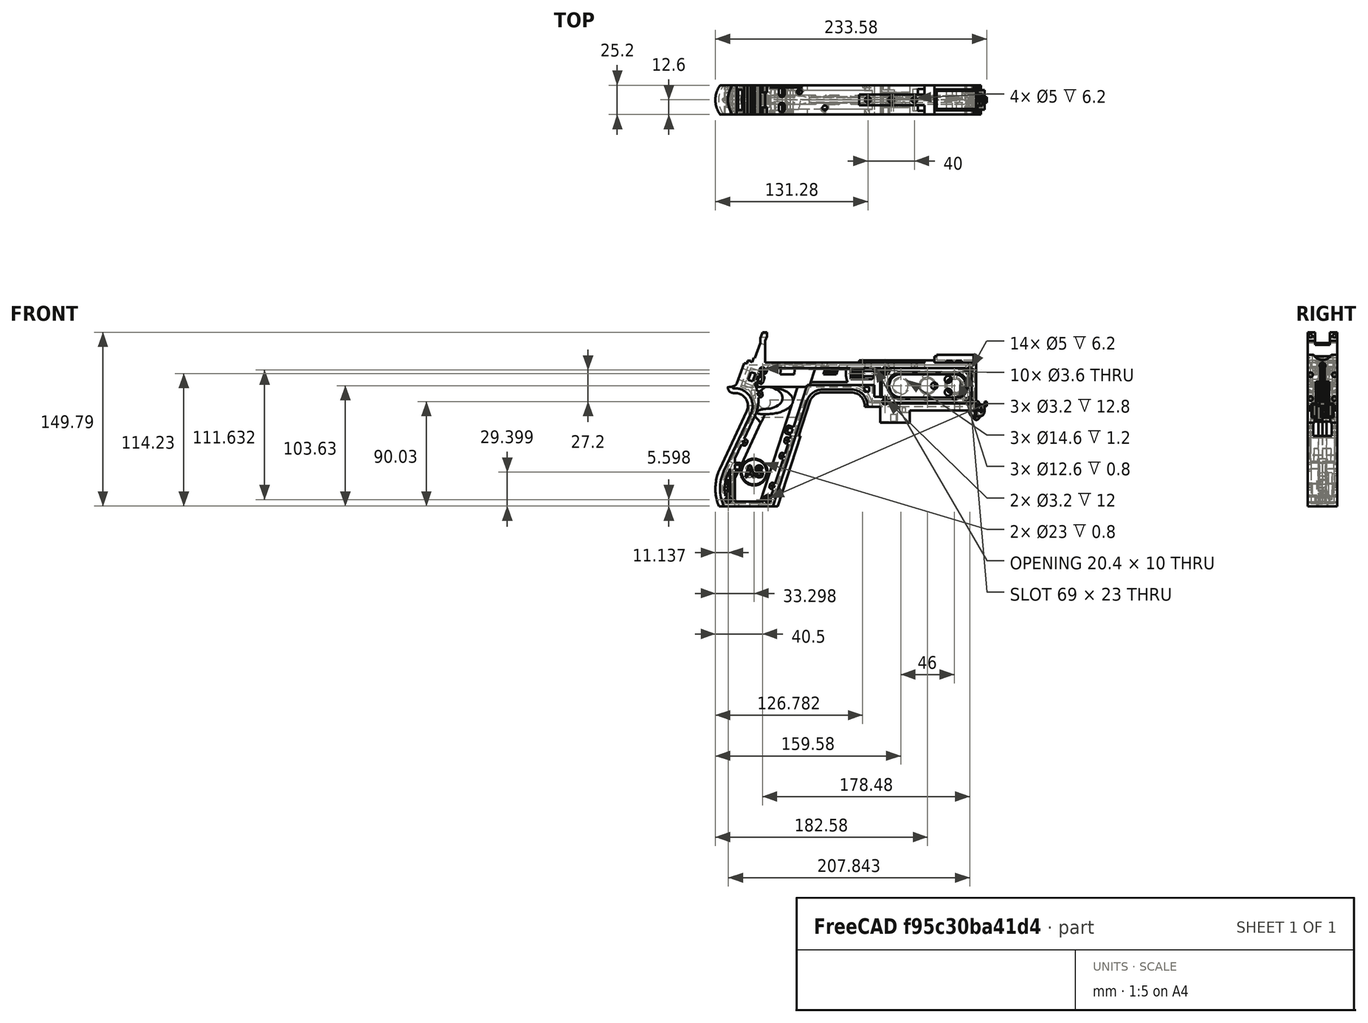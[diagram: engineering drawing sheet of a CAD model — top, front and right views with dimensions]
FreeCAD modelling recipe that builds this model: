
FCSTD DOCUMENT  (FreeCAD 1.0R39319 (Git))
Label: PICON-OF_ver_54
License: All rights reserved
LicenseURL: https://en.wikipedia.org/wiki/All_rights_reserved
objects: Sketcher::SketchObject×124, Part::Extrusion×63, Part::Cut×48, PartDesign::Pad×29, PartDesign::Pocket×21, PartDesign::Chamfer×15, PartDesign::Body×10, PartDesign::Fillet×6, Part::MultiFuse×5, Part::Part2DObjectPython×4, PartDesign::SubtractivePipe×4, PartDesign::SubtractiveLoft×4, PartDesign::Plane×3, PartDesign::SubShapeBinder×2, Part::Sweep×1, PartDesign::ShapeBinder×1, Mesh::Feature×1, PartDesign::Point×1, PartDesign::Groove×1
note: 626 computed .brp shape members not serialized (recipe doc carries the construction recipe); baked Part::Feature solids carry a one-line shape summary decoded from their .brp

FEATURE [Sketcher::SketchObject] Sketch  label="corpo principale"
  ArcFitTolerance = 1e-06
  AttacherType = Attacher::AttachEngine3D
  AttachmentSupport = -> [XZ_Plane]
  FullyConstrained = true
  MakeInternals = false
  MapMode = 5
  Placement = pos=(0,0,0) rot=(1,0,0;1.5708rad)
  sketch-geometry (65):
    g0: LineSegment StartX=0 StartY=0 StartZ=0 EndX=-57.2 EndY=0 EndZ=0
    g1: LineSegment StartX=-57.2 StartY=0 StartZ=0 EndX=-57.2 EndY=-10.4 EndZ=0
    g2: LineSegment StartX=-57.2 StartY=-10.4 StartZ=0 EndX=-82.8 EndY=-10.4 EndZ=0
    g3: LineSegment StartX=-82.8 StartY=-10.4 StartZ=0 EndX=-82.8 EndY=3.2 EndZ=0
    g4: LineSegment StartX=-82.8 StartY=3.2 StartZ=0 EndX=-93.6 EndY=3.2 EndZ=0
    g5: LineSegment StartX=-93.6 StartY=3.2 StartZ=0 EndX=-93.6 EndY=4 EndZ=0
    g6: LineSegment StartX=-107.6 StartY=18 StartZ=0 EndX=-132.428 EndY=18 EndZ=0
    g7: LineSegment StartX=-145.743 StartY=8.32624 StartZ=0 EndX=-175.232 EndY=-82.4316 EndZ=0
    g8: LineSegment StartX=-175.232 StartY=-82.4316 StartZ=0 EndX=-217.232 EndY=-82.4316 EndZ=0
    g9: LineSegment StartX=-217.232 StartY=-52.1862 StartZ=0 EndX=-193.988 EndY=-2.33927 EndZ=0
    g10: LineSegment StartX=-206.196 StartY=23.0857 StartZ=0 EndX=-199.861 EndY=40.4914 EndZ=0
    g11: LineSegment StartX=-199.861 StartY=40.4914 StartZ=0 EndX=-197.061 EndY=40.4914 EndZ=0
    g12: LineSegment StartX=-197.061 StartY=40.4914 StartZ=0 EndX=-197.061 EndY=42.8914 EndZ=0
    g13: LineSegment StartX=-197.061 StartY=42.8914 StartZ=0 EndX=-194.261 EndY=42.8914 EndZ=0
    g14: LineSegment StartX=-194.261 StartY=42.8914 StartZ=0 EndX=-194.535 EndY=42.1397 EndZ=0
    g15: LineSegment StartX=-194.535 StartY=42.1397 StartZ=0 EndX=-193.031 EndY=41.5924 EndZ=0
    g16: LineSegment StartX=-193.031 StartY=41.5924 StartZ=0 EndX=-191.663 EndY=45.3512 EndZ=0
    g17: LineSegment StartX=-191.663 StartY=45.3512 StartZ=0 EndX=-190.536 EndY=44.9408 EndZ=0
    g18: LineSegment StartX=-190.536 StartY=44.9408 StartZ=0 EndX=-185.747 EndY=58.0965 EndZ=0
    g19: LineSegment StartX=-185.747 StartY=58.0965 StartZ=0 EndX=-185.747 EndY=62.0965 EndZ=0
    g20: LineSegment StartX=-185.747 StartY=62.0965 StartZ=0 EndX=-183.832 EndY=67.3588 EndZ=0
    g21: LineSegment StartX=-183.832 StartY=67.3588 StartZ=0 EndX=-180.232 EndY=67.3588 EndZ=0
    g22: LineSegment StartX=-180.232 StartY=67.3588 StartZ=0 EndX=-180.232 EndY=63.7588 EndZ=0
    g23: LineSegment StartX=-180.232 StartY=63.7588 StartZ=0 EndX=-181.6 EndY=60 EndZ=0
    g24: LineSegment StartX=-181.6 StartY=60 StartZ=0 EndX=-181.6 EndY=41.2 EndZ=0
    g25: LineSegment StartX=-181.6 StartY=41.2 StartZ=0 EndX=-100.8 EndY=41.2 EndZ=0
    g26: LineSegment StartX=-36 StartY=43.2 StartZ=0 EndX=-36 EndY=41.2 EndZ=0
    g27: LineSegment StartX=0 StartY=48 StartZ=0 EndX=0 EndY=0 EndZ=0
    g28: LineSegment StartX=-209.901 StartY=19.85 StartZ=0 EndX=-209.901 EndY=20.1 EndZ=0
    g29: LineSegment StartX=-208.001 StartY=22 StartZ=0 EndX=-207.747 EndY=22 EndZ=0
    g30: LineSegment StartX=-207.583 StartY=19 StartZ=0 EndX=-209.051 EndY=19 EndZ=0
    g31: ArcOfCircle CenterX=-208.001 CenterY=20.1 CenterZ=0 NormalX=0 NormalY=0 NormalZ=1 AngleXU=0 Radius=1.9 StartAngle=1.5708 EndAngle=3.14159
    g32: GeomPoint [constr] X=-209.901 Y=22 Z=0
    g33: ArcOfCircle CenterX=-209.051 CenterY=19.85 CenterZ=0 NormalX=0 NormalY=0 NormalZ=1 AngleXU=0 Radius=0.85 StartAngle=3.14159 EndAngle=4.71239
    g34: GeomPoint [constr] X=-209.901 Y=19 Z=0
    g35: ArcOfCircle CenterX=-207.747 CenterY=23.65 CenterZ=0 NormalX=0 NormalY=0 NormalZ=1 AngleXU=0 Radius=1.65 StartAngle=4.71239 EndAngle=5.93412
    g36: GeomPoint [constr] X=-206.591 Y=22 Z=0
    g37: LineSegment StartX=-4 StartY=6 StartZ=0 EndX=-4 EndY=36.4 EndZ=0
    g38: LineSegment StartX=-4 StartY=36.4 StartZ=0 EndX=-185.2 EndY=36.4 EndZ=0
    g39: LineSegment StartX=-185.2 StartY=36.4 StartZ=0 EndX=-190.441 EndY=22 EndZ=0
    g40: LineSegment StartX=-214.575 StartY=-78.4316 StartZ=0 EndX=-178.142 EndY=-78.4316 EndZ=0
    g41: LineSegment StartX=-178.142 StartY=-78.4316 StartZ=0 EndX=-145.51 EndY=22 EndZ=0
    g42: LineSegment StartX=-145.51 StartY=22 StartZ=0 EndX=-87.91 EndY=22 EndZ=0
    g43: LineSegment StartX=-87.91 StartY=22 StartZ=0 EndX=-87.91 EndY=11.6 EndZ=0
    g44: LineSegment StartX=-87.91 StartY=11.6 StartZ=0 EndX=-80.11 EndY=11.6 EndZ=0
    g45: LineSegment StartX=-80.11 StartY=11.6 StartZ=0 EndX=-80.11 EndY=6 EndZ=0
    g46: LineSegment StartX=-80.11 StartY=6 StartZ=0 EndX=-4 EndY=6 EndZ=0
    g47: LineSegment StartX=-190.363 StartY=-4.02975 StartZ=0 EndX=-213.607 EndY=-53.8767 EndZ=0
    g48: ArcOfCircle CenterX=-132.428 CenterY=4 CenterZ=0 NormalX=0 NormalY=0 NormalZ=1 AngleXU=0 Radius=14 StartAngle=1.5708 EndAngle=2.82743
    g49: GeomPoint [constr] X=-142.6 Y=18 Z=0
    g50: ArcOfCircle CenterX=-107.6 CenterY=4 CenterZ=0 NormalX=0 NormalY=0 NormalZ=1 AngleXU=0 Radius=14 StartAngle=0 EndAngle=1.5708
    g51: GeomPoint [constr] X=-93.6 Y=18 Z=0
    g52: ArcOfCircle CenterX=-184.801 CenterY=-67.3089 CenterZ=0 NormalX=0 NormalY=0 NormalZ=1 AngleXU=0 Radius=35.7833 StartAngle=2.70526 EndAngle=3.57792
    g53: ArcOfCircle CenterX=-207.583 CenterY=4 CenterZ=0 NormalX=0 NormalY=0 NormalZ=1 AngleXU=0 Radius=15 StartAngle=5.84685 EndAngle=7.85398
    g54: LineSegment [constr] StartX=-213.607 StartY=-53.8767 StartZ=0 EndX=-217.232 EndY=-52.1862 EndZ=0
    g55: ArcOfCircle CenterX=-184.801 CenterY=-67.3089 CenterZ=0 NormalX=0 NormalY=0 NormalZ=1 AngleXU=0 Radius=31.7833 StartAngle=2.70526 EndAngle=3.49911
    g56: ArcOfCircle CenterX=-218.095 CenterY=8.90192 CenterZ=0 NormalX=0 NormalY=0 NormalZ=1 AngleXU=0 Radius=30.5989 StartAngle=5.84685 EndAngle=6.72553
    g57: LineSegment StartX=-44.6 StartY=43.2 StartZ=0 EndX=-36 EndY=43.2 EndZ=0
    g58: LineSegment StartX=-100.8 StartY=41.2 StartZ=0 EndX=-44.6 EndY=41.2 EndZ=0
    g59: LineSegment StartX=-44.6 StartY=41.2 StartZ=0 EndX=-44.6 EndY=43.2 EndZ=0
    g60: LineSegment StartX=-2.4 StartY=48 StartZ=0 EndX=0 EndY=48 EndZ=0
    g61: LineSegment StartX=-36 StartY=41.2 StartZ=0 EndX=-2.4 EndY=41.2 EndZ=0
    g62: LineSegment StartX=-2.4 StartY=41.2 StartZ=0 EndX=-2.4 EndY=48 EndZ=0
    g63: LineSegment [constr] StartX=-181.6 StartY=36.4 StartZ=0 EndX=-152.209 EndY=36.4 EndZ=0
    g64: LineSegment [constr] StartX=-181.6 StartY=36.4 StartZ=0 EndX=-130.41 EndY=36.4 EndZ=0
  constraints (183):
    c: Coincident(g-1,g0)
    c: PointOnObject(g0,g-1)
    c: Coincident(g0,g1)
    c: Vertical(g1)
    c: Coincident(g1,g2)
    c: Horizontal(g2)
    c: Coincident(g2,g3)
    c: Vertical(g3)
    c: Coincident(g3,g4)
    c: Coincident(g4,g5)
    c: Vertical(g5)
    c: Horizontal(g6)
    c: Coincident(g7,g8)
    c: Horizontal(g8)
    c: Coincident(g10,g11)
    c: Horizontal(g11)
    c: Coincident(g11,g12)
    c: Vertical(g12)
    c: Coincident(g12,g13)
    c: Horizontal(g13)
    c: Coincident(g13,g14)
    c: Coincident(g14,g15)
    c: Coincident(g15,g16)
    c: Coincident(g16,g17)
    c: Coincident(g17,g18)
    c: Coincident(g18,g19)
    c: Vertical(g19)
    c: Coincident(g19,g20)
    c: Coincident(g20,g21)
    c: Horizontal(g21)
    c: Coincident(g21,g22)
    c: Vertical(g22)
    c: Coincident(g22,g23)
    c: Coincident(g23,g24)
    c: Vertical(g24)
    c: Coincident(g24,g25)
    c: Horizontal(g25)
    c: Coincident(g57,g26)
    c: Vertical(g26)
    c: Coincident(g26,g61)
    c: PointOnObject(g60,g-2)
    c: Coincident(g60,g27)
    c: Coincident(g27,g0)
    c: DistanceY(g27,g27) = 48
    c: DistanceY(g1,g1) = 10.4
    c: DistanceX(g0,g0) = 57.2
    c: DistanceX(g2,g2) = 25.6
    c: Horizontal(g4)
    c: DistanceY(g3,g3) = 13.6
    c: DistanceX(g4,g4) = 10.8
    c: DistanceY(g5,g51) = 14.8
    c: DistanceX(g49,g51) = 49
    c: Distance(g7,g49) = 105.6
    c: DistanceX(g61,g60) = 36
    c: DistanceX(g25,g25) = 80.8
    c: DistanceY(g24,g24) = 18.8
    c: DistanceY(g22,g22) = 3.6
    c: Distance(g23) = 4
    c: Angle(g-1,g23) = 1.22173
    c: DistanceX(g21,g21) = 3.6
    c: Distance(g20) = 5.6
    c: Angle(g-1,g20) = 1.22173
    c: DistanceY(g19,g19) = 4
    c: Distance(g18) = 14
    c: Angle(g-1,g18) = 1.22173
    c: Distance(g17) = 1.2
    c: Distance(g16) = 4
    c: Angle(g16) = 1.22173
    c: Perpendicular(g18,g17)
    c: Distance(g15) = 1.6
    c: Perpendicular(g16,g15)
    c: Distance(g14) = 0.8
    c: DistanceX(g13,g13) = 2.8
    c: Perpendicular(g15,g14)
    c: DistanceY(g12,g12) = 2.4
    c: DistanceX(g11,g11) = 2.8
    c: Distance(g9) = 55
    c: Angle(g9,g-1) = 2.00713
    c: Horizontal(g29)
    c: Vertical(g28)
    c: Horizontal(g30)
    c: PointOnObject(g32,g29)
    c: PointOnObject(g32,g28)
    c: Tangent(g29,g31) = 1.5708
    c: Tangent(g28,g31) = 1.5708
    c: PointOnObject(g34,g28)
    c: PointOnObject(g34,g30)
    c: Tangent(g28,g33) = 1.5708
    c: Tangent(g30,g33) = 1.5708
    c: PointOnObject(g36,g29)
    c: PointOnObject(g36,g10)
    c: Tangent(g29,g35) = -1.5708
    c: Tangent(g10,g35) = -1.5708
    c: Angle(g-1,g10) = 1.22173
    c: Radius(g35) = 1.65
    c: Vertical(g37)
    c: Coincident(g37,g38)
    c: Horizontal(g38)
    c: Coincident(g38,g39)
    c: Horizontal(g40)
    c: Coincident(g40,g41)
    c: Coincident(g41,g42)
    c: Horizontal(g42)
    c: Coincident(g42,g43)
    c: Vertical(g43)
    c: Coincident(g43,g44)
    c: Horizontal(g44)
    c: Coincident(g44,g45)
    c: Vertical(g45)
    c: Coincident(g45,g46)
    c: Coincident(g46,g37)
    c: Horizontal(g46)
    c: DistanceY(g0,g37) = 6
    c: DistanceX(g37,g0) = 4
    c: DistanceY(g37,g25) = 4.8
    c: DistanceX(g38,g38) = 181.2
    c: DistanceX(g42,g42) = 57.6
    c: DistanceY(g49,g41) = 4
    c: DistanceX(g41,g49) = 2.91
    c: DistanceY(g43,g43) = 10.4
    c: DistanceX(g44,g44) = 7.8
    c: DistanceY(g7,g40) = 4
    c: Distance(g47) = 55
    c: Angle(g-1,g39) = 1.22173
    c: PointOnObject(g49,g7)
    c: PointOnObject(g49,g6)
    c: Tangent(g7,g48) = -1.5708
    c: Tangent(g6,g48) = -1.5708
    c: PointOnObject(g51,g5)
    c: PointOnObject(g51,g6)
    c: Tangent(g5,g50) = -1.5708
    c: Tangent(g6,g50) = -1.5708
    c: Radius(g50) = 14
    c: Radius(g48) = 14
    c: DistanceX(g8,g8) = 42
    c: Angle(g7,g-1) = 1.88496
    c: Parallel(g41,g7)
    c: Parallel(g47,g9)
    c: Coincident(g52,g8)
    c: Tangent(g52,g9) = 1.5708
    c: DistanceX(g9,g8) = 0
    c: Tangent(g53,g9) = -1.5708
    c: Tangent(g53,g30) = -1.5708
    c: Diameter(g53) = 30
    c: DistanceY(g53,g0) = -4
    c: Coincident(g54,g47)
    c: Distance(g54) = 4
    c: Coincident(g54,g9)
    c: Coincident(g55,g40)
    c: Tangent(g55,g47) = -1.5708
    c: Coincident(g52,g55)
    c: Coincident(g56,g39)
    c: Tangent(g56,g47) = 1.5708
    c: Horizontal(g57)
    c: DistanceX(g57,g57) = 8.6
    c: Coincident(g58,g25)
    c: Horizontal(g58)
    c: Coincident(g59,g58)
    c: Vertical(g59)
    c: DistanceY(g58,g57) = 2
    c: DistanceX(g58,g58) = 56.2
    c: Coincident(g59,g57)
    c: DistanceY(g41,g36) = 0
    c: DistanceY(g36,g39) = 0
    c: DistanceY(g28,g28) = 0.25
    c: DistanceX(g30,g36) = 2.46
    c: DistanceX(g28,g29) = 1.9
    c: Coincident(g62,g60)
    c: Horizontal(g60)
    c: DistanceX(g62,g27) = 2.4
    c: Coincident(g61,g62)
    c: DistanceY(g26,g26) = 2
    c: Vertical(g62)
    c: DistanceY(g61,g60) = 6.8
    c: Horizontal(g61)
    c: Distance(g63) = 29.391
    c: PointOnObject(g63,g38)
    c: PointOnObject(g63,g38)
    c: Distance(g64) = 51.19
    c: PointOnObject(g64,g38)
    c: PointOnObject(g64,g38)
    c: DistanceX(g24,g63) = 0
    c: DistanceX(g24,g64) = 0
FEATURE [Part::Extrusion] Extrude  label="Extrude corpo principale"
  Base = -> Sketch
  Dir = (0,-1,2e-16)
  DirMode = 2
  FaceMakerClass = Part::FaceMakerBullseye
  FaceMakerMode = 3
  LengthFwd = 25.2
  LengthRev = 12.6
  Solid = true
  Symmetric = true
FEATURE [Sketcher::SketchObject] Sketch002  label="scavo grilletto"
  ArcFitTolerance = 1e-06
  AttachmentSupport = -> [XZ_Plane]
  ExternalGeometry = -> [Sketch]
  FullyConstrained = true
  MakeInternals = false
  MapMode = 5
  Placement = pos=(0,0,0) rot=(1,0,0;1.5708rad)
  sketch-geometry (4):
    g0: LineSegment StartX=-89.51 StartY=22 StartZ=0 EndX=-152.71 EndY=22 EndZ=0
    g1: LineSegment StartX=-152.71 StartY=22 StartZ=0 EndX=-167.006 EndY=-22 EndZ=0
    g2: LineSegment StartX=-167.006 StartY=-22 StartZ=0 EndX=-89.51 EndY=-22 EndZ=0
    g3: LineSegment StartX=-89.51 StartY=-22 StartZ=0 EndX=-89.51 EndY=22 EndZ=0
  constraints (12):
    c: Horizontal(g0)
    c: Coincident(g0,g1)
    c: Coincident(g1,g2)
    c: Horizontal(g2)
    c: Coincident(g2,g3)
    c: Coincident(g3,g0)
    c: Vertical(g3)
    c: Angle(g1,g0) = 1.88496
    c: DistanceY(g3,g3) = 44
    c: DistanceX(g0,g0) = 63.2
    c: DistanceX(g0,g-3) = 1.6
    c: DistanceY(g-3,g0) = 0
FEATURE [Sketcher::SketchObject] Sketch004  label="traiettoria arrotondamento impugnatura anteriore"
  ArcFitTolerance = 1e-06
  AttachmentSupport = -> [XZ_Plane]
  ExternalGeometry = -> [Sketch]
  FullyConstrained = true
  MakeInternals = false
  MapMode = 5
  Placement = pos=(0,0,0) rot=(1,0,0;1.5708rad)
  sketch-geometry (13):
    g0: LineSegment StartX=-175.232 StartY=-82.4316 StartZ=0 EndX=-145.743 EndY=8.32624 EndZ=0
    g1: LineSegment StartX=-93.6 StartY=3.2 StartZ=0 EndX=-93.6 EndY=4 EndZ=0
    g2: LineSegment StartX=-132.428 StartY=18 StartZ=0 EndX=-107.6 EndY=18 EndZ=0
    g3: ArcOfCircle CenterX=-132.428 CenterY=4 CenterZ=0 NormalX=0 NormalY=0 NormalZ=1 AngleXU=0 Radius=14 StartAngle=1.5708 EndAngle=2.82743
    g4: ArcOfCircle CenterX=-107.6 CenterY=4 CenterZ=0 NormalX=0 NormalY=0 NormalZ=1 AngleXU=0 Radius=14 StartAngle=0 EndAngle=1.5708
    g5: LineSegment StartX=-175.232 StartY=-82.4316 StartZ=0 EndX=-217.232 EndY=-82.4316 EndZ=0
    g6: LineSegment StartX=-217.232 StartY=-52.1862 StartZ=0 EndX=-193.988 EndY=-2.33927 EndZ=0
    g7: LineSegment StartX=-209.051 StartY=19 StartZ=0 EndX=-207.583 EndY=19 EndZ=0
    g8: LineSegment StartX=-209.901 StartY=20.1 StartZ=0 EndX=-209.901 EndY=19.85 EndZ=0
    g9: ArcOfCircle CenterX=-184.801 CenterY=-67.3089 CenterZ=0 NormalX=0 NormalY=0 NormalZ=1 AngleXU=0 Radius=35.7833 StartAngle=2.70526 EndAngle=3.57792
    g10: ArcOfCircle CenterX=-207.583 CenterY=4 CenterZ=0 NormalX=0 NormalY=0 NormalZ=1 AngleXU=0 Radius=15 StartAngle=5.84685 EndAngle=7.85398
    g11: ArcOfCircle CenterX=-209.051 CenterY=19.85 CenterZ=0 NormalX=0 NormalY=0 NormalZ=1 AngleXU=0 Radius=0.85 StartAngle=3.14159 EndAngle=4.71239
    g12: ArcOfCircle CenterX=-208.001 CenterY=20.1 CenterZ=0 NormalX=0 NormalY=0 NormalZ=1 AngleXU=0 Radius=1.9 StartAngle=1.5708 EndAngle=3.14159
  constraints (26):
    c: Coincident(g0,g-3)
    c: Coincident(g0,g-6)
    c: Coincident(g1,g-8)
    c: Coincident(g1,g-7)
    c: Coincident(g2,g-5)
    c: Coincident(g2,g-4)
    c: Coincident(g3,g2)
    c: Tangent(g3,g0) = 1.5708
    c: Coincident(g4,g1)
    c: Tangent(g4,g2) = 1.5708
    c: Coincident(g5,g0)
    c: Coincident(g5,g-9)
    c: Coincident(g6,g-12)
    c: Coincident(g6,g-11)
    c: Coincident(g7,g-15)
    c: Coincident(g7,g-14)
    c: Coincident(g8,g-16)
    c: Coincident(g8,g-17)
    c: Tangent(g9,g6) = 1.5708
    c: Coincident(g9,g5)
    c: Coincident(g10,g7)
    c: Tangent(g10,g6) = -1.5708
    c: Tangent(g11,g7) = -1.5708
    c: Coincident(g11,g8)
    c: Tangent(g12,g8) = -1.5708
    c: Coincident(g12,g-17)
FEATURE [PartDesign::Plane] DatumPlane  label="Piano per disegno arrotondamento impugnatura"
  AttachmentSupport = -> [Sketch]
  Length = 73.6581
  MapMode = 7
  Placement = pos=(-145.743,1.8e-15,8.32624) rot=(0.154555,0.154555,0.97582;1.59527rad)
  ResizeMode = 0
  Width = 303.511
FEATURE [Sketcher::SketchObject] Sketch005  label="forma arrotondamento impugnatura anteriore"
  ArcFitTolerance = 1e-06
  AttachmentSupport = -> [DatumPlane]
  FullyConstrained = true
  MakeInternals = false
  MapMode = 5
  Placement = pos=(-145.743,1.8e-15,8.32624) rot=(0.154555,0.154555,0.97582;1.59527rad)
  sketch-geometry (5):
    g0: GeomPoint [constr] X=0 Y=-4 Z=0
    g1: GeomPoint [constr] X=-12.6 Y=7.1e-15 Z=0
    g2: GeomPoint [constr] X=12.6 Y=4.97e-14 Z=0
    g3: LineSegment StartX=-12.6 StartY=7.1e-15 StartZ=0 EndX=12.6 EndY=4.97e-14 EndZ=0
    g4: ArcOfCircle CenterX=-3.88e-14 CenterY=17.845 CenterZ=0 NormalX=0 NormalY=0 NormalZ=1 AngleXU=0 Radius=21.845 StartAngle=4.09759 EndAngle=5.32718
  constraints (11):
    c: DistanceY(g0,g-1) = 4
    c: DistanceX(g-1,g0) = 0
    c: DistanceX(g1,g-1) = 12.6
    c: DistanceX(g-1,g2) = 12.6
    c: DistanceY(g-1,g2) = 0
    c: DistanceY(g-1,g1) = 0
    c: Coincident(g3,g1)
    c: Coincident(g3,g2)
    c: Coincident(g4,g1)
    c: Coincident(g4,g2)
    c: PointOnObject(g0,g4)
FEATURE [Part::Sweep] Sweep  label="Sweep impugnatura"
  Frenet = true
  Sections = -> [Sketch005]
  Solid = true
  Spine = -> Sketch [Edge32,Edge33,Edge34,Edge35,Edge36,Edge37,Edge38,Edge39,Edge40,Edge41,Edge42,Edge43,Edge44]
  Transition = 1
FEATURE [Sketcher::SketchObject] Sketch008  label="buchi e pulizie varie"
  ArcFitTolerance = 1e-06
  AttachmentSupport = -> [XZ_Plane]
  ExternalGeometry = -> [Sketch]
  FullyConstrained = true
  MakeInternals = false
  MapMode = 5
  Placement = pos=(0,0,0) rot=(1,0,0;1.5708rad)
  sketch-geometry (26):
    g0: LineSegment StartX=-96.278 StartY=20.155 StartZ=0 EndX=-92.278 EndY=20.155 EndZ=0
    g1: LineSegment StartX=-92.278 StartY=20.155 StartZ=0 EndX=-92.278 EndY=16.155 EndZ=0
    g2: LineSegment StartX=-92.278 StartY=16.155 StartZ=0 EndX=-96.278 EndY=16.155 EndZ=0
    g3: LineSegment StartX=-96.278 StartY=16.155 StartZ=0 EndX=-96.278 EndY=20.155 EndZ=0
    g4: LineSegment StartX=-222.232 StartY=-82.4316 StartZ=0 EndX=-170.232 EndY=-82.4316 EndZ=0
    g5: LineSegment StartX=-170.232 StartY=-82.4316 StartZ=0 EndX=-170.232 EndY=-86.4316 EndZ=0
    g6: LineSegment StartX=-170.232 StartY=-86.4316 StartZ=0 EndX=-222.232 EndY=-86.4316 EndZ=0
    g7: LineSegment StartX=-222.232 StartY=-86.4316 StartZ=0 EndX=-222.232 EndY=-82.4316 EndZ=0
    g8: LineSegment StartX=-213.901 StartY=20.1 StartZ=0 EndX=-213.901 EndY=26 EndZ=0
    g9: LineSegment StartX=-213.901 StartY=26 StartZ=0 EndX=-206.196 EndY=26 EndZ=0
    g10: LineSegment StartX=-17.4 StartY=42.8 StartZ=0 EndX=-12.4 EndY=42.8 EndZ=0
    g11: LineSegment StartX=-12.4 StartY=42.8 StartZ=0 EndX=-12.4 EndY=41.2 EndZ=0
    g12: LineSegment StartX=-12.4 StartY=41.2 StartZ=0 EndX=-17.4 EndY=41.2 EndZ=0
    g13: LineSegment StartX=-17.4 StartY=41.2 StartZ=0 EndX=-17.4 EndY=42.8 EndZ=0
    g14: LineSegment StartX=-25.9 StartY=42.8 StartZ=0 EndX=-20.9 EndY=42.8 EndZ=0
    g15: LineSegment StartX=-20.9 StartY=42.8 StartZ=0 EndX=-20.9 EndY=41.2 EndZ=0
    g16: LineSegment StartX=-20.9 StartY=41.2 StartZ=0 EndX=-25.9 EndY=41.2 EndZ=0
    g17: LineSegment StartX=-25.9 StartY=41.2 StartZ=0 EndX=-25.9 EndY=42.8 EndZ=0
    g18: GeomPoint [constr] X=-206.196 Y=23.0857 Z=0
    g19: GeomPoint [constr] X=-213.901 Y=20.1 Z=0
    g20: BSplineCurve PolesCount=4 KnotsCount=2 Degree=3 IsPeriodic=0
    g21-g24: Circle [constr] x4 (B-spline internal-alignment scaffolding for g20; pole/knot coordinates omitted)
    g25: LineSegment StartX=-206.196 StartY=26 StartZ=0 EndX=-206.196 EndY=23.0857 EndZ=0
  constraints (73):
    c: Horizontal(g0)
    c: Coincident(g1,g0)
    c: Vertical(g1)
    c: Coincident(g2,g1)
    c: Horizontal(g2)
    c: Coincident(g3,g2)
    c: Coincident(g3,g0)
    c: Vertical(g3)
    c: DistanceX(g0,g-4) = 4.368
    c: DistanceY(g0,g-4) = 1.845
    c: DistanceY(g1,g1) = 4
    c: DistanceX(g2,g2) = 4
    c: Horizontal(g4)
    c: Coincident(g5,g4)
    c: Vertical(g5)
    c: Coincident(g6,g5)
    c: Horizontal(g6)
    c: Coincident(g7,g6)
    c: Coincident(g7,g4)
    c: Vertical(g7)
    c: DistanceY(g7,g7) = 4
    c: DistanceX(g4,g-5) = 5
    c: DistanceX(g-5,g4) = 5
    c: DistanceY(g4,g-5) = 0
    c: Coincident(g9,g8)
    c: Parallel(g9,g-6)
    c: DistanceX(g8,g-8) = 4
    c: Horizontal(g10)
    c: Coincident(g11,g10)
    c: Vertical(g11)
    c: Coincident(g12,g11)
    c: Horizontal(g12)
    c: Coincident(g13,g12)
    c: Coincident(g13,g10)
    c: Vertical(g13)
    c: Horizontal(g14)
    c: Coincident(g15,g14)
    c: Vertical(g15)
    c: Coincident(g16,g15)
    c: Horizontal(g16)
    c: Coincident(g17,g16)
    c: Coincident(g17,g14)
    c: Vertical(g17)
    c: DistanceY(g11,g10) = 1.6
    c: DistanceX(g10,g10) = 5
    c: DistanceY(g15,g14) = 1.6
    c: DistanceX(g14,g14) = 5
    c: DistanceX(g15,g12) = 3.5
    c: DistanceX(g11,g-9) = 10
    c: DistanceY(g-9,g11) = 0
    c: DistanceY(g-9,g15) = 0
    c: Perpendicular(g8,g9)
    c: DistanceY(g-7,g9) = 4
    c: DistanceY(g8,g-8) = 0
    c: InternalAlignment(g18,g20)
    c: InternalAlignment(g19,g20)
    c: InternalAlignment(g21,g20)
    c: Weight(g21) = 1
    c: InternalAlignment(g22,g20)
    c: Equal(g22,g21)
    c: InternalAlignment(g23,g20)
    c: Equal(g23,g21)
    c: InternalAlignment(g24,g20)
    c: Equal(g24,g21)
    c: Coincident(g18,g-12)
    c: Coincident(g19,g8)
    c: Coincident(g25,g9)
    c: Coincident(g25,g20)
    c: Vertical(g25)
    c: DistanceY(g20,g23) = 0
    c: DistanceY(g22,g18) = 2.26
    c: DistanceX(g22,g18) = 0.93
    c: DistanceX(g20,g23) = 2.9
FEATURE [Part::Extrusion] Extrude004  label="Extrude Buchi e pulizie varie"
  Base = -> Sketch008
  Dir = (0,-1,2e-16)
  DirMode = 2
  FaceMakerClass = Part::FaceMakerBullseye
  FaceMakerMode = 3
  LengthFwd = 25.2
  LengthRev = 0
  Solid = true
  Symmetric = true
FEATURE [Sketcher::SketchObject] Sketch009  label="rinforzi"
  ArcFitTolerance = 1e-06
  AttachmentSupport = -> [XZ_Plane]
  ExternalGeometry = -> [Sketch]
  FullyConstrained = true
  MakeInternals = false
  MapMode = 5
  Placement = pos=(0,0,0) rot=(1,0,0;1.5708rad)
  sketch-geometry (9):
    g0: LineSegment StartX=-87.91 StartY=22 StartZ=0 EndX=-87.91 EndY=36.4 EndZ=0
    g1: LineSegment StartX=-87.91 StartY=36.4 StartZ=0 EndX=-97.91 EndY=36.4 EndZ=0
    g2: LineSegment StartX=-97.91 StartY=36.4 StartZ=0 EndX=-97.91 EndY=22 EndZ=0
    g3: LineSegment StartX=-97.91 StartY=22 StartZ=0 EndX=-87.91 EndY=22 EndZ=0
    g4: LineSegment StartX=-149.713 StartY=9.06563 StartZ=0 EndX=-154.586 EndY=-5.93437 EndZ=0
    g5: LineSegment StartX=-154.586 StartY=-5.93437 StartZ=0 EndX=-191.863 EndY=-5.93437 EndZ=0
    g6: LineSegment StartX=-191.863 StartY=-5.93437 StartZ=0 EndX=-191.863 EndY=9.06563 EndZ=0
    g7: LineSegment StartX=-191.863 StartY=9.06563 StartZ=0 EndX=-149.713 EndY=9.06563 EndZ=0
    g8: LineSegment [constr] StartX=-145.51 StartY=22 StartZ=0 EndX=-149.713 EndY=9.06563 EndZ=0
  constraints (25):
    c: Vertical(g0)
    c: Coincident(g1,g0)
    c: Horizontal(g1)
    c: Coincident(g2,g1)
    c: Vertical(g2)
    c: Coincident(g3,g2)
    c: Coincident(g3,g0)
    c: Horizontal(g3)
    c: Coincident(g0,g-4)
    c: DistanceX(g3,g3) = 10
    c: DistanceY(g0,g-3) = 0
    c: Coincident(g5,g4)
    c: Horizontal(g5)
    c: Coincident(g6,g5)
    c: Vertical(g6)
    c: Coincident(g7,g6)
    c: Coincident(g7,g4)
    c: Horizontal(g7)
    c: Distance(g8) = 13.6
    c: Parallel(g-6,g8)
    c: Coincident(g-6,g8)
    c: Parallel(g4,g-6)
    c: DistanceY(g4,g4) = 15
    c: Coincident(g4,g8)
    c: DistanceX(g-5,g5) = -1.5
FEATURE [Part::Extrusion] Extrude001  label="Extrude scavo grilletto"
  Base = -> Sketch002
  Dir = (0,-1,2e-16)
  DirMode = 2
  FaceMakerClass = Part::FaceMakerBullseye
  FaceMakerMode = 3
  LengthFwd = 16
  LengthRev = 0
  Solid = true
  Symmetric = true
FEATURE [Part::Extrusion] Extrude005  label="Extrude Rinforzi"
  Base = -> Sketch009
  Dir = (0,-1,2e-16)
  DirMode = 2
  FaceMakerClass = Part::FaceMakerBullseye
  FaceMakerMode = 3
  LengthFwd = 2
  LengthRev = 0
  Placement = pos=(0,12.6,0) rot=(0,0,1;0rad)
  Solid = true
  Symmetric = false
FEATURE [PartDesign::ShapeBinder] CopyCut
  TraceSupport = false
FEATURE [PartDesign::Plane] DatumPlane001
  AttachmentSupport = -> [CopyCut]
  Length = 283.944
  MapMode = 5
  Placement = pos=(0,12.6,0) rot=(0,0.707107,0.707107;3.14159rad)
  ResizeMode = 0
  Width = 188.15
FEATURE [Sketcher::SketchObject] Sketch010  label="buco neopixel"
  ArcFitTolerance = 1e-06
  AttachmentSupport = -> [XZ_Plane]
  ExternalGeometry = -> [Sketch]
  FullyConstrained = true
  MakeInternals = false
  MapMode = 5
  Placement = pos=(0,0,0) rot=(1,0,0;1.5708rad)
  sketch-geometry (5):
    g0: LineSegment [constr] StartX=-199.861 StartY=40.4914 StartZ=0 EndX=-201.368 EndY=36.3521 EndZ=0
    g1: LineSegment StartX=-201.368 StartY=36.3521 StartZ=0 EndX=-204.932 EndY=26.5605 EndZ=0
    g2: LineSegment StartX=-201.368 StartY=36.3521 StartZ=0 EndX=-180.2 EndY=28.6477 EndZ=0
    g3: LineSegment StartX=-180.2 StartY=28.6477 StartZ=0 EndX=-183.764 EndY=18.8561 EndZ=0
    g4: LineSegment StartX=-183.764 StartY=18.8561 StartZ=0 EndX=-204.932 EndY=26.5605 EndZ=0
  constraints (14):
    c: Parallel(g0,g-3)
    c: Distance(g0) = 4.405
    c: Coincident(g0,g-3)
    c: Coincident(g2,g1)
    c: Coincident(g3,g2)
    c: Coincident(g4,g3)
    c: Coincident(g4,g1)
    c: Parallel(g1,g-3)
    c: Distance(g1) = 10.42
    c: Coincident(g1,g0)
    c: Parallel(g2,g4)
    c: Perpendicular(g1,g2)
    c: DistanceX(g-4,g2) = 5
    c: Parallel(g3,g1)
FEATURE [Part::Extrusion] Extrude006  label="Extrude buco neopixel"
  Base = -> Sketch010
  Dir = (0,-1,2e-16)
  DirMode = 2
  FaceMakerClass = Part::FaceMakerBullseye
  FaceMakerMode = 3
  LengthFwd = 17.2
  LengthRev = 0
  Solid = true
  Symmetric = true
FEATURE [Sketcher::SketchObject] Sketch011  label="fermo grilletto"
  ArcFitTolerance = 1e-06
  AttachmentSupport = -> [XZ_Plane]
  ExternalGeometry = -> [Sketch]
  FullyConstrained = true
  MakeInternals = false
  MapMode = 5
  Placement = pos=(0,0,0) rot=(1,0,0;1.5708rad)
  sketch-geometry (18):
    g0: LineSegment [constr] StartX=-145.51 StartY=22 StartZ=0 EndX=-157.347 EndY=-14.4293 EndZ=0
    g1: LineSegment [constr] StartX=-157.347 StartY=-14.4293 StartZ=0 EndX=-157.841 EndY=-15.951 EndZ=0
    g2: LineSegment StartX=-161.151 StartY=-13.1932 StartZ=0 EndX=-155.825 EndY=-14.9237 EndZ=0
    g3: LineSegment StartX=-163.167 StartY=-14.2205 StartZ=0 EndX=-164.403 EndY=-18.0247 EndZ=0
    g4: LineSegment StartX=-163.376 StartY=-20.0408 StartZ=0 EndX=-158.05 EndY=-21.7713 EndZ=0
    g5: LineSegment StartX=-158.05 StartY=-21.7713 StartZ=0 EndX=-155.825 EndY=-14.9237 EndZ=0
    g6: LineSegment StartX=-161.645 StartY=-14.7149 StartZ=0 EndX=-157.841 EndY=-15.951 EndZ=0
    g7: LineSegment StartX=-157.841 StartY=-15.951 StartZ=0 EndX=-159.077 EndY=-19.7552 EndZ=0
    g8: LineSegment StartX=-159.077 StartY=-19.7552 StartZ=0 EndX=-162.881 EndY=-18.5191 EndZ=0
    g9: LineSegment StartX=-162.881 StartY=-18.5191 StartZ=0 EndX=-161.645 EndY=-14.7149 EndZ=0
    g10: LineSegment [constr] StartX=-161.645 StartY=-14.7149 StartZ=0 EndX=-161.151 EndY=-13.1932 EndZ=0
    g11: LineSegment [constr] StartX=-159.077 StartY=-19.7552 StartZ=0 EndX=-157.555 EndY=-20.2496 EndZ=0
    g12: LineSegment [constr] StartX=-159.077 StartY=-19.7552 StartZ=0 EndX=-159.572 EndY=-21.2769 EndZ=0
    g13: LineSegment [constr] StartX=-161.645 StartY=-14.7149 StartZ=0 EndX=-163.167 EndY=-14.2205 EndZ=0
    g14: ArcOfCircle CenterX=-161.645 CenterY=-14.7149 CenterZ=0 NormalX=0 NormalY=0 NormalZ=1 AngleXU=0 Radius=1.6 StartAngle=1.25664 EndAngle=2.82743
    g15: GeomPoint [constr] X=-162.673 Y=-12.6988 Z=0
    g16: ArcOfCircle CenterX=-162.881 CenterY=-18.5191 CenterZ=0 NormalX=0 NormalY=0 NormalZ=1 AngleXU=0 Radius=1.6 StartAngle=2.82743 EndAngle=4.39823
    g17: GeomPoint [constr] X=-164.897 Y=-19.5464 Z=0
  constraints (48):
    c: Parallel(g0,g-3)
    c: Distance(g0) = 38.304
    c: Coincident(g0,g-3)
    c: Parallel(g1,g-3)
    c: Distance(g1) = 1.6
    c: Coincident(g1,g0)
    c: Coincident(g5,g4)
    c: Coincident(g5,g2)
    c: Coincident(g7,g6)
    c: Coincident(g8,g7)
    c: Coincident(g9,g8)
    c: Coincident(g9,g6)
    c: Parallel(g7,g-3)
    c: Parallel(g9,g7)
    c: Perpendicular(g6,g7)
    c: Parallel(g6,g8)
    c: Distance(g6) = 4
    c: Distance(g9) = 4
    c: Parallel(g5,g7)
    c: Parallel(g9,g3)
    c: Parallel(g2,g6)
    c: Parallel(g4,g8)
    c: Parallel(g13,g6)
    c: Parallel(g10,g9)
    c: Parallel(g11,g8)
    c: Parallel(g12,g7)
    c: Distance(g10) = 1.6
    c: Distance(g13) = 1.6
    c: Distance(g12) = 1.6
    c: Distance(g11) = 1.6
    c: Coincident(g10,g6)
    c: Coincident(g13,g6)
    c: Coincident(g12,g7)
    c: Coincident(g11,g7)
    c: Distance(g10,g15) = 1.6
    c: Distance(g15,g13) = 1.6
    c: Distance(g4,g12) = 1.6
    c: Distance(g4,g11) = 1.6
    c: PointOnObject(g15,g2)
    c: Tangent(g3,g14) = -1.5708
    c: Tangent(g2,g14) = 1.5708
    c: PointOnObject(g17,g4)
    c: PointOnObject(g17,g3)
    c: Tangent(g4,g16) = -1.5708
    c: Tangent(g3,g16) = -1.5708
    c: Equal(g16,g14)
    c: Coincident(g16,g8)
    c: Coincident(g6,g1)
FEATURE [Part::Extrusion] Extrude007  label="Extrude fermo grilletto"
  Base = -> Sketch011
  Dir = (0,-1,2e-16)
  DirMode = 2
  FaceMakerClass = Part::FaceMakerBullseye
  FaceMakerMode = 3
  LengthFwd = 25.2
  LengthRev = 0
  Solid = true
  Symmetric = true
FEATURE [Sketcher::SketchObject] Sketch012  label="buco oled"
  ArcFitTolerance = 1e-06
  AttachmentSupport = -> [XZ_Plane]
  ExternalGeometry = -> [Sketch]
  FullyConstrained = true
  MakeInternals = false
  MapMode = 5
  Placement = pos=(0,0,0) rot=(1,0,0;1.5708rad)
  sketch-geometry (4):
    g0: LineSegment StartX=-185.747 StartY=58.0965 StartZ=0 EndX=-180.232 EndY=56.0891 EndZ=0
    g1: LineSegment StartX=-185.747 StartY=58.0965 StartZ=0 EndX=-185.747 EndY=67.3588 EndZ=0
    g2: LineSegment StartX=-185.747 StartY=67.3588 StartZ=0 EndX=-180.232 EndY=67.3588 EndZ=0
    g3: LineSegment StartX=-180.232 StartY=67.3588 StartZ=0 EndX=-180.232 EndY=56.0891 EndZ=0
  constraints (10):
    c: Coincident(g1,g0)
    c: Coincident(g2,g1)
    c: Coincident(g3,g2)
    c: Coincident(g3,g0)
    c: Parallel(g1,g-5)
    c: Perpendicular(g-3,g0)
    c: Parallel(g2,g-6)
    c: Parallel(g3,g-4)
    c: Coincident(g0,g-5)
    c: Coincident(g2,g-6)
FEATURE [Part::Extrusion] Extrude008  label="Extrude buco oled"
  Base = -> Sketch012
  Dir = (0,-1,2e-16)
  DirMode = 2
  FaceMakerClass = Part::FaceMakerBullseye
  FaceMakerMode = 3
  LengthFwd = 12.8
  LengthRev = 0
  Solid = true
  Symmetric = true
FEATURE [Sketcher::SketchObject] Sketch013  label="buco pompa"
  ArcFitTolerance = 1e-06
  AttachmentSupport = -> [XZ_Plane]
  ExternalGeometry = -> [Sketch]
  FullyConstrained = true
  MakeInternals = false
  MapMode = 5
  Placement = pos=(0,0,0) rot=(1,0,0;1.5708rad)
  sketch-geometry (8):
    g0: LineSegment StartX=-82.8 StartY=-10.4 StartZ=0 EndX=-82.8 EndY=-9.6 EndZ=0
    g1: LineSegment StartX=-82.8 StartY=-9.6 StartZ=0 EndX=-67.9 EndY=-9.6 EndZ=0
    g2: LineSegment StartX=-67.9 StartY=-9.6 StartZ=0 EndX=-67.9 EndY=6 EndZ=0
    g3: LineSegment StartX=-67.9 StartY=6 StartZ=0 EndX=-65.9 EndY=6 EndZ=0
    g4: LineSegment StartX=-65.9 StartY=6 StartZ=0 EndX=-65.9 EndY=-1.7 EndZ=0
    g5: LineSegment StartX=-65.9 StartY=-1.7 StartZ=0 EndX=-57.2 EndY=-1.7 EndZ=0
    g6: LineSegment StartX=-57.2 StartY=-1.7 StartZ=0 EndX=-57.2 EndY=-10.4 EndZ=0
    g7: LineSegment StartX=-57.2 StartY=-10.4 StartZ=0 EndX=-82.8 EndY=-10.4 EndZ=0
  constraints (22):
    c: Vertical(g0)
    c: Coincident(g1,g0)
    c: Horizontal(g1)
    c: Coincident(g2,g1)
    c: Vertical(g2)
    c: Coincident(g3,g2)
    c: Horizontal(g3)
    c: Coincident(g4,g3)
    c: Vertical(g4)
    c: Coincident(g5,g4)
    c: Horizontal(g5)
    c: Coincident(g6,g5)
    c: Vertical(g6)
    c: Coincident(g7,g6)
    c: Coincident(g7,g0)
    c: DistanceY(g0,g0) = 0.8
    c: DistanceY(g6,g6) = 8.7
    c: DistanceX(g1,g1) = 14.9
    c: DistanceX(g3,g3) = 2
    c: Coincident(g0,g-4)
    c: DistanceY(g2,g-6) = 0
    c: Coincident(g6,g-5)
FEATURE [Part::Extrusion] Extrude009  label="Extrude buco pompa"
  Base = -> Sketch013
  Dir = (0,-1,2e-16)
  DirMode = 2
  FaceMakerClass = Part::FaceMakerBullseye
  FaceMakerMode = 3
  LengthFwd = 13.2
  LengthRev = 0
  Solid = true
  Symmetric = true
FEATURE [Sketcher::SketchObject] Sketch014  label="buco frontale"
  ArcFitTolerance = 1e-06
  AttachmentSupport = -> [XZ_Plane]
  ExternalGeometry = -> [Sketch]
  FullyConstrained = true
  MakeInternals = false
  MapMode = 5
  Placement = pos=(0,0,0) rot=(1,0,0;1.5708rad)
  sketch-geometry (10):
    g0: LineSegment StartX=0 StartY=0 StartZ=0 EndX=0 EndY=24.671 EndZ=0
    g1: LineSegment StartX=0 StartY=24.671 StartZ=0 EndX=-4 EndY=24.671 EndZ=0
    g2: LineSegment StartX=-4 StartY=24.671 StartZ=0 EndX=-4 EndY=16 EndZ=0
    g3: LineSegment StartX=-4 StartY=16 StartZ=0 EndX=-2.4 EndY=16 EndZ=0
    g4: LineSegment StartX=-2.4 StartY=16 StartZ=0 EndX=-2.4 EndY=10 EndZ=0
    g5: LineSegment StartX=-2.4 StartY=10 StartZ=0 EndX=-12 EndY=10 EndZ=0
    g6: LineSegment StartX=-12 StartY=10 StartZ=0 EndX=-12 EndY=6 EndZ=0
    g7: LineSegment StartX=-12 StartY=6 StartZ=0 EndX=-2.4 EndY=6 EndZ=0
    g8: LineSegment StartX=-2.4 StartY=6 StartZ=0 EndX=-2.4 EndY=0 EndZ=0
    g9: LineSegment StartX=-2.4 StartY=0 StartZ=0 EndX=0 EndY=0 EndZ=0
  constraints (29):
    c: Vertical(g0)
    c: Coincident(g1,g0)
    c: Horizontal(g1)
    c: Coincident(g2,g1)
    c: Vertical(g2)
    c: Coincident(g3,g2)
    c: Horizontal(g3)
    c: Coincident(g4,g3)
    c: Vertical(g4)
    c: Coincident(g5,g4)
    c: Horizontal(g5)
    c: Coincident(g6,g5)
    c: Vertical(g6)
    c: Coincident(g7,g6)
    c: Coincident(g8,g7)
    c: Vertical(g8)
    c: Coincident(g9,g8)
    c: Coincident(g9,g0)
    c: Horizontal(g9)
    c: DistanceY(g0,g0) = 24.671
    c: Horizontal(g7)
    c: DistanceY(g6,g6) = 4
    c: DistanceY(g4,g4) = 6
    c: DistanceX(g9,g9) = 2.4
    c: Coincident(g0,g-1)
    c: DistanceY(g-3,g7) = 0
    c: DistanceX(g8,g4) = 0
    c: DistanceX(g-3,g1) = 0
    c: DistanceX(g6,g-3) = 8
FEATURE [Part::Extrusion] Extrude010  label="Extrude buco frontale"
  Base = -> Sketch014
  Dir = (0,-1,2e-16)
  DirMode = 2
  FaceMakerClass = Part::FaceMakerBullseye
  FaceMakerMode = 3
  LengthFwd = 11.2
  LengthRev = 0
  Solid = true
  Symmetric = true
FEATURE [Sketcher::SketchObject] Sketch015  label="guida rail"
  ArcFitTolerance = 1e-06
  AttachmentSupport = -> [XZ_Plane]
  ExternalGeometry = -> [Sketch]
  FullyConstrained = true
  MakeInternals = false
  MapMode = 5
  Placement = pos=(0,0,0) rot=(1,0,0;1.5708rad)
  sketch-geometry (4):
    g0: LineSegment StartX=-100.8 StartY=43.2 StartZ=0 EndX=-44.6 EndY=43.2 EndZ=0
    g1: LineSegment StartX=-44.6 StartY=43.2 StartZ=0 EndX=-44.6 EndY=41.2 EndZ=0
    g2: LineSegment StartX=-44.6 StartY=41.2 StartZ=0 EndX=-100.8 EndY=41.2 EndZ=0
    g3: LineSegment StartX=-100.8 StartY=41.2 StartZ=0 EndX=-100.8 EndY=43.2 EndZ=0
  constraints (9):
    c: Horizontal(g0)
    c: Coincident(g1,g0)
    c: Coincident(g2,g1)
    c: Coincident(g3,g2)
    c: Coincident(g3,g0)
    c: Vertical(g3)
    c: Coincident(g2,g-3)
    c: Coincident(g1,g-3)
    c: Coincident(g0,g-4)
FEATURE [Part::Extrusion] Extrude011  label="Extrude guida rail"
  Base = -> Sketch015
  Dir = (0,-1,2e-16)
  DirMode = 2
  FaceMakerClass = Part::FaceMakerBullseye
  FaceMakerMode = 3
  LengthFwd = 9
  LengthRev = 0
  Solid = true
  Symmetric = true
FEATURE [Sketcher::SketchObject] Sketch016  label="guide per coperture laterali"
  ArcFitTolerance = 1e-06
  AttachmentSupport = -> [XZ_Plane]
  ExternalGeometry = -> [Sketch]
  FullyConstrained = true
  MakeInternals = false
  MapMode = 5
  Placement = pos=(0,0,0) rot=(1,0,0;1.5708rad)
  sketch-geometry (14):
    g0: Circle CenterX=-5.6 CenterY=7.6 CenterZ=0 NormalX=0 NormalY=0 NormalZ=1 AngleXU=0 Radius=1.6
    g1: Circle CenterX=-5.6 CenterY=7.6 CenterZ=0 NormalX=0 NormalY=0 NormalZ=1 AngleXU=0 Radius=4
    g2: Circle CenterX=-5.6 CenterY=34.8 CenterZ=0 NormalX=0 NormalY=0 NormalZ=1 AngleXU=0 Radius=1.6
    g3: Circle CenterX=-5.6 CenterY=34.8 CenterZ=0 NormalX=0 NormalY=0 NormalZ=1 AngleXU=0 Radius=4
    g4: Circle CenterX=-184.08 CenterY=34.8 CenterZ=0 NormalX=0 NormalY=0 NormalZ=1 AngleXU=0 Radius=1.6
    g5: Circle CenterX=-184.08 CenterY=34.8 CenterZ=0 NormalX=0 NormalY=0 NormalZ=1 AngleXU=0 Radius=4
    g6: Circle CenterX=-179.305 CenterY=-76.8316 CenterZ=0 NormalX=0 NormalY=0 NormalZ=1 AngleXU=0 Radius=1.6
    g7: Circle CenterX=-179.305 CenterY=-76.8316 CenterZ=0 NormalX=0 NormalY=0 NormalZ=1 AngleXU=0 Radius=4
    g8: Circle CenterX=-213.443 CenterY=-76.8316 CenterZ=0 NormalX=0 NormalY=0 NormalZ=1 AngleXU=0 Radius=1.6
    g9: Circle CenterX=-213.443 CenterY=-76.8316 CenterZ=0 NormalX=0 NormalY=0 NormalZ=1 AngleXU=0 Radius=4
    g10: Circle CenterX=-78.51 CenterY=7.6 CenterZ=0 NormalX=0 NormalY=0 NormalZ=1 AngleXU=0 Radius=1.6
    g11: Circle CenterX=-78.51 CenterY=7.6 CenterZ=0 NormalX=0 NormalY=0 NormalZ=1 AngleXU=0 Radius=4
    g12: Circle CenterX=-78.51 CenterY=34.8 CenterZ=0 NormalX=0 NormalY=0 NormalZ=1 AngleXU=0 Radius=1.6
    g13: Circle CenterX=-78.51 CenterY=34.8 CenterZ=0 NormalX=0 NormalY=0 NormalZ=1 AngleXU=0 Radius=4
  constraints (35):
    c: Diameter(g0) = 3.2
    c: Diameter(g1) = 8
    c: Coincident(g0,g1)
    c: Diameter(g2) = 3.2
    c: Diameter(g3) = 8
    c: Coincident(g3,g2)
    c: Tangent(g2,g-7)
    c: Diameter(g4) = 3.2
    c: Diameter(g5) = 8
    c: Coincident(g5,g4)
    c: Tangent(g4,g-7)
    c: Tangent(g4,g-8)
    c: Diameter(g6) = 3.2
    c: Diameter(g7) = 8
    c: Coincident(g7,g6)
    c: Tangent(g6,g-9)
    c: Tangent(g6,g-10)
    c: Diameter(g8) = 3.2
    c: Diameter(g9) = 8
    c: Coincident(g9,g8)
    c: Tangent(g8,g-10)
    c: Tangent(g8,g-11)
    c: Diameter(g10) = 3.2
    c: Diameter(g11) = 8
    c: Diameter(g12) = 3.2
    c: Diameter(g13) = 8
    c: Coincident(g12,g13)
    c: Coincident(g10,g11)
    c: Tangent(g12,g-7)
    c: DistanceX(g12,g10) = 0
    c: Tangent(g2,g-6)
    c: Tangent(g0,g-6)
    c: Tangent(g0,g-3)
    c: Tangent(g10,g-3)
    c: Tangent(g10,g-4)
FEATURE [Part::Extrusion] Extrude012  label="extrude guide per coperture laterali"
  Base = -> Sketch016
  Dir = (0,-1,2e-16)
  DirMode = 2
  FaceMakerClass = Part::FaceMakerBullseye
  FaceMakerMode = 3
  LengthFwd = 25.2
  LengthRev = 0
  Solid = true
  Symmetric = true
FEATURE [Sketcher::SketchObject] Sketch017  label="supporto CAM"
  ArcFitTolerance = 1e-06
  AttachmentSupport = -> [XZ_Plane]
  ExternalGeometry = -> [Sketch]
  FullyConstrained = true
  MakeInternals = false
  MapMode = 5
  Placement = pos=(0,0,0) rot=(1,0,0;1.5708rad)
  sketch-geometry (6):
    g0: LineSegment StartX=-2.4 StartY=48 StartZ=0 EndX=-2.4 EndY=41.2 EndZ=0
    g1: LineSegment StartX=-2.4 StartY=48 StartZ=0 EndX=-34 EndY=48 EndZ=0
    g2: LineSegment StartX=-34 StartY=48 StartZ=0 EndX=-34 EndY=46.72 EndZ=0
    g3: LineSegment StartX=-34 StartY=46.72 StartZ=0 EndX=-36 EndY=46.72 EndZ=0
    g4: LineSegment StartX=-36 StartY=46.72 StartZ=0 EndX=-36 EndY=41.2 EndZ=0
    g5: LineSegment StartX=-36 StartY=41.2 StartZ=0 EndX=-2.4 EndY=41.2 EndZ=0
  constraints (15):
    c: Coincident(g1,g0)
    c: Horizontal(g1)
    c: Coincident(g2,g1)
    c: Vertical(g2)
    c: Coincident(g3,g2)
    c: Horizontal(g3)
    c: Coincident(g4,g3)
    c: Coincident(g5,g4)
    c: DistanceX(g1,g0) = 31.6
    c: Coincident(g5,g0)
    c: Vertical(g4)
    c: DistanceY(g2,g1) = 1.28
    c: Coincident(g0,g-3)
    c: Coincident(g0,g-3)
    c: Coincident(g4,g-4)
FEATURE [Part::Extrusion] Extrude013  label="Extrude supporto CAM"
  Base = -> Sketch017
  Dir = (0,-1,2e-16)
  DirMode = 2
  FaceMakerClass = Part::FaceMakerBullseye
  FaceMakerMode = 3
  LengthFwd = 17.8
  LengthRev = 0
  Solid = true
  Symmetric = true
FEATURE [Sketcher::SketchObject] Sketch018  label="Scavo CAM"
  ArcFitTolerance = 1e-06
  AttachmentSupport = -> [YZ_Plane]
  ExternalGeometry = -> [Sketch]
  FullyConstrained = true
  MakeInternals = false
  MapMode = 5
  Placement = pos=(0,0,0) rot=(0.57735,0.57735,0.57735;2.0944rad)
  sketch-geometry (4):
    g0: LineSegment StartX=-7.73 StartY=48 StartZ=0 EndX=7.73 EndY=48 EndZ=0
    g1: LineSegment [constr] StartX=1.07e-14 StartY=48 StartZ=0 EndX=0 EndY=43.5155 EndZ=0
    g2: ArcOfCircle CenterX=9e-15 CenterY=52.42 CenterZ=0 NormalX=0 NormalY=0 NormalZ=1 AngleXU=0 Radius=8.90445 StartAngle=3.66102 EndAngle=5.76376
    g3: Circle [constr] CenterX=9e-15 CenterY=52.42 CenterZ=0 NormalX=0 NormalY=0 NormalZ=1 AngleXU=0 Radius=8.9
  constraints (13):
    c: Horizontal(g0)
    c: DistanceY(g-3,g0) = 0
    c: DistanceX(g0,g0) = 15.46
    c: DistanceX(g0,g-3) = 7.73
    c: DistanceX(g-3) = 0
    c: Coincident(g1,g-3)
    c: PointOnObject(g1,g-2)
    c: Coincident(g2,g0)
    c: Coincident(g2,g0)
    c: PointOnObject(g1,g2)
    c: Diameter(g3) = 17.8
    c: DistanceY(g1,g3) = 4.42
    c: Coincident(g2,g3)
FEATURE [Part::Extrusion] Extrude014  label="Extrude Scavo CAM"
  Base = -> Sketch018
  Dir = (1,0,0)
  DirMode = 2
  FaceMakerClass = Part::FaceMakerBullseye
  FaceMakerMode = 3
  LengthFwd = -34
  LengthRev = 0
  Solid = true
  Symmetric = false
FEATURE [Sketcher::SketchObject] Sketch019  label="scavo rumble"
  ArcFitTolerance = 1e-06
  AttachmentSupport = -> [XZ_Plane]
  ExternalGeometry = -> [Sketch]
  FullyConstrained = true
  MakeInternals = false
  MapMode = 5
  Placement = pos=(0,0,0) rot=(1,0,0;1.5708rad)
  sketch-geometry (6):
    g0: LineSegment StartX=-163.771 StartY=-21.9058 StartZ=0 EndX=-158.636 EndY=-23.5745 EndZ=0
    g1: LineSegment StartX=-158.636 StartY=-23.5745 StartZ=0 EndX=-165.743 EndY=-45.4488 EndZ=0
    g2: LineSegment StartX=-165.743 StartY=-45.4488 StartZ=0 EndX=-170.879 EndY=-43.7801 EndZ=0
    g3: LineSegment StartX=-170.879 StartY=-43.7801 StartZ=0 EndX=-163.771 EndY=-21.9058 EndZ=0
    g4: LineSegment [constr] StartX=-145.51 StartY=22 StartZ=0 EndX=-160.157 EndY=-23.0801 EndZ=0
    g5: LineSegment [constr] StartX=-158.636 StartY=-23.5745 StartZ=0 EndX=-160.157 EndY=-23.0801 EndZ=0
  constraints (17):
    c: Coincident(g1,g0)
    c: Coincident(g2,g1)
    c: Coincident(g3,g2)
    c: Coincident(g3,g0)
    c: Parallel(g3,g-3)
    c: Parallel(g3,g1)
    c: Perpendicular(g3,g0)
    c: Perpendicular(g2,g3)
    c: Distance(g2,g0) = 23
    c: Parallel(g4,g-3)
    c: Distance(g4) = 47.4
    c: Coincident(g4,g-3)
    c: Parallel(g5,g0)
    c: Distance(g5) = 1.6
    c: Coincident(g5,g0)
    c: Distance(g5,g0) = 3.8
    c: Coincident(g5,g4)
FEATURE [Part::Extrusion] Extrude015  label="scavo rumble001"
  Base = -> Sketch019
  Dir = (0,-1,2e-16)
  DirMode = 2
  FaceMakerClass = Part::FaceMakerBullseye
  FaceMakerMode = 3
  LengthFwd = 21
  LengthRev = 0
  Solid = true
  Symmetric = true
FEATURE [Sketcher::SketchObject] Sketch020  label="fermo rumble"
  ArcFitTolerance = 1e-06
  AttachmentSupport = -> [XZ_Plane]
  ExternalGeometry = -> [Sketch019,Sketch]
  FullyConstrained = true
  MakeInternals = false
  MapMode = 5
  Placement = pos=(0,0,0) rot=(1,0,0;1.5708rad)
  sketch-geometry (16):
    g0: LineSegment [constr] StartX=-165.905 StartY=-40.7697 StartZ=0 EndX=-167.265 EndY=-44.9544 EndZ=0
    g1: LineSegment [constr] StartX=-167.265 StartY=-44.9544 StartZ=0 EndX=-165.743 EndY=-45.4488 EndZ=0
    g2: LineSegment StartX=-167.318 StartY=-37.9976 StartZ=0 EndX=-165.225 EndY=-38.6774 EndZ=0
    g3: LineSegment StartX=-165.225 StartY=-38.6774 StartZ=0 EndX=-165.905 EndY=-40.7697 EndZ=0
    g4: LineSegment StartX=-165.905 StartY=-40.7697 StartZ=0 EndX=-167.997 EndY=-40.0899 EndZ=0
    g5: LineSegment StartX=-167.997 StartY=-40.0899 StartZ=0 EndX=-167.318 EndY=-37.9976 EndZ=0
    g6: LineSegment StartX=-166.823 StartY=-36.4759 StartZ=0 EndX=-163.399 EndY=-37.5883 EndZ=0
    g7: LineSegment StartX=-163.399 StartY=-37.5883 StartZ=0 EndX=-165.006 EndY=-42.5338 EndZ=0
    g8: LineSegment StartX=-165.006 StartY=-42.5338 StartZ=0 EndX=-168.43 EndY=-41.4214 EndZ=0
    g9: LineSegment StartX=-169.457 StartY=-39.4053 StartZ=0 EndX=-168.839 EndY=-37.5031 EndZ=0
    g10: LineSegment [constr] StartX=-168.839 StartY=-37.5031 StartZ=0 EndX=-168.345 EndY=-35.9815 EndZ=0
    g11: LineSegment [constr] StartX=-168.345 StartY=-35.9815 StartZ=0 EndX=-166.823 EndY=-36.4759 EndZ=0
    g12: ArcOfCircle CenterX=-167.936 CenterY=-39.8997 CenterZ=0 NormalX=0 NormalY=0 NormalZ=1 AngleXU=0 Radius=1.6 StartAngle=2.82743 EndAngle=4.39823
    g13: GeomPoint [constr] X=-169.952 Y=-40.9269 Z=0
    g14: ArcOfCircle CenterX=-167.318 CenterY=-37.9976 CenterZ=0 NormalX=0 NormalY=0 NormalZ=1 AngleXU=0 Radius=1.6 StartAngle=1.25664 EndAngle=2.82743
    g15: GeomPoint [constr] X=-168.345 Y=-35.9815 Z=0
  constraints (42):
    c: Parallel(g0,g-4)
    c: Distance(g0) = 4.4
    c: Coincident(g1,g0)
    c: Perpendicular(g0,g1)
    c: Distance(g1) = 1.6
    c: Coincident(g1,g-5)
    c: Coincident(g3,g2)
    c: Coincident(g4,g3)
    c: Coincident(g5,g4)
    c: Coincident(g5,g2)
    c: Parallel(g3,g-4)
    c: Parallel(g3,g5)
    c: Perpendicular(g2,g3)
    c: Parallel(g4,g2)
    c: Distance(g2) = 2.2
    c: Distance(g3) = 2.2
    c: Coincident(g7,g6)
    c: Coincident(g8,g7)
    c: Parallel(g7,g-4)
    c: Parallel(g7,g9)
    c: Perpendicular(g6,g7)
    c: Parallel(g6,g8)
    c: Distance(g6,g15) = 5.2
    c: Distance(g7) = 5.2
    c: Coincident(g11,g10)
    c: Parallel(g10,g9)
    c: Parallel(g11,g6)
    c: Distance(g10) = 1.6
    c: Distance(g11) = 1.6
    c: Coincident(g10,g15)
    c: Distance(g11,g2) = 1.6
    c: Distance(g2,g10) = 1.6
    c: PointOnObject(g13,g8)
    c: PointOnObject(g13,g9)
    c: Tangent(g8,g12) = 1.5708
    c: Tangent(g9,g12) = 1.5708
    c: PointOnObject(g15,g9)
    c: Tangent(g6,g14) = 1.5708
    c: Tangent(g9,g14) = 1.5708
    c: Equal(g12,g14)
    c: Coincident(g6,g11)
    c: Coincident(g3,g0)
FEATURE [Part::Extrusion] Extrude016  label="Extrude fermo rumble"
  Base = -> Sketch020
  Dir = (0,-1,2e-16)
  DirMode = 2
  FaceMakerClass = Part::FaceMakerBullseye
  FaceMakerMode = 3
  LengthFwd = 25.2
  LengthRev = 0
  Solid = true
  Symmetric = true
FEATURE [Sketcher::SketchObject] Sketch021  label="perno fermo rumble001"
  ArcFitTolerance = 1e-06
  AttachmentSupport = -> [XZ_Plane001]
  FullyConstrained = true
  MakeInternals = false
  MapMode = 5
  Placement = pos=(0,0,0) rot=(1,0,0;1.5708rad)
  sketch-geometry (16):
    g0: LineSegment StartX=0 StartY=0.45 StartZ=0 EndX=0 EndY=1.55 EndZ=0
    g1: LineSegment StartX=0.45 StartY=2 StartZ=0 EndX=1.55 EndY=2 EndZ=0
    g2: LineSegment StartX=2 StartY=1.55 StartZ=0 EndX=2 EndY=0.45 EndZ=0
    g3: LineSegment StartX=1.55 StartY=0 StartZ=0 EndX=0.45 EndY=0 EndZ=0
    g4: ArcOfCircle [constr] CenterX=0.45 CenterY=1.55 CenterZ=0 NormalX=0 NormalY=0 NormalZ=1 AngleXU=0 Radius=0.45 StartAngle=1.5708 EndAngle=3.14159
    g5: GeomPoint [constr] X=0 Y=2 Z=0
    g6: LineSegment StartX=0.45 StartY=2 StartZ=0 EndX=0 EndY=1.55 EndZ=0
    g7: ArcOfCircle [constr] CenterX=1.55 CenterY=1.55 CenterZ=0 NormalX=0 NormalY=0 NormalZ=1 AngleXU=0 Radius=0.45 StartAngle=0 EndAngle=1.5708
    g8: GeomPoint [constr] X=2 Y=2 Z=0
    g9: LineSegment StartX=2 StartY=1.55 StartZ=0 EndX=1.55 EndY=2 EndZ=0
    g10: ArcOfCircle [constr] CenterX=1.55 CenterY=0.45 CenterZ=0 NormalX=0 NormalY=0 NormalZ=1 AngleXU=0 Radius=0.45 StartAngle=4.71239 EndAngle=6.28319
    g11: GeomPoint [constr] X=2 Y=0 Z=0
    g12: LineSegment StartX=1.55 StartY=0 StartZ=0 EndX=2 EndY=0.45 EndZ=0
    g13: ArcOfCircle [constr] CenterX=0.45 CenterY=0.45 CenterZ=0 NormalX=0 NormalY=0 NormalZ=1 AngleXU=0 Radius=0.45 StartAngle=3.14159 EndAngle=4.71239
    g14: GeomPoint [constr] X=0 Y=0 Z=0
    g15: LineSegment StartX=0 StartY=0.45 StartZ=0 EndX=0.45 EndY=0 EndZ=0
  constraints (35):
    c: Coincident(g14,g-1)
    c: PointOnObject(g5,g-2)
    c: Horizontal(g1)
    c: Vertical(g2)
    c: Horizontal(g3)
    c: DistanceX(g5,g8) = 2
    c: DistanceY(g11,g8) = 2
    c: PointOnObject(g5,g0)
    c: PointOnObject(g5,g1)
    c: Tangent(g0,g4) = 1.5708
    c: Tangent(g1,g4) = 1.5708
    c: Coincident(g6,g0)
    c: Coincident(g6,g1)
    c: PointOnObject(g8,g2)
    c: PointOnObject(g8,g1)
    c: Tangent(g2,g7) = 1.5708
    c: Tangent(g1,g7) = 1.5708
    c: Coincident(g9,g2)
    c: Coincident(g9,g1)
    c: PointOnObject(g11,g2)
    c: PointOnObject(g11,g3)
    c: Tangent(g2,g10) = 1.5708
    c: Tangent(g3,g10) = 1.5708
    c: Coincident(g12,g2)
    c: Coincident(g12,g3)
    c: PointOnObject(g14,g0)
    c: PointOnObject(g14,g3)
    c: Tangent(g0,g13) = 1.5708
    c: Tangent(g3,g13) = 1.5708
    c: Coincident(g15,g0)
    c: Coincident(g15,g3)
    c: Equal(g6,g9)
    c: Equal(g9,g12)
    c: Equal(g12,g15)
    c: DistanceX(g14,g3) = 0.45
FEATURE [Sketcher::SketchObject] Sketch022  label="fori per M3x5(OD)x6(L)"
  ArcFitTolerance = 1e-06
  AttachmentSupport = -> [XZ_Plane]
  ExternalGeometry = -> [Sketch016]
  FullyConstrained = true
  MakeInternals = false
  MapMode = 5
  Placement = pos=(0,0,0) rot=(1,0,0;1.5708rad)
  sketch-geometry (7):
    g0: Circle CenterX=-5.6 CenterY=34.8 CenterZ=0 NormalX=0 NormalY=0 NormalZ=1 AngleXU=0 Radius=2.5
    g1: Circle CenterX=-5.6 CenterY=7.6 CenterZ=0 NormalX=0 NormalY=0 NormalZ=1 AngleXU=0 Radius=2.5
    g2: Circle CenterX=-78.51 CenterY=34.8 CenterZ=0 NormalX=0 NormalY=0 NormalZ=1 AngleXU=0 Radius=2.5
    g3: Circle CenterX=-78.51 CenterY=7.6 CenterZ=0 NormalX=0 NormalY=0 NormalZ=1 AngleXU=0 Radius=2.5
    g4: Circle CenterX=-184.08 CenterY=34.8 CenterZ=0 NormalX=0 NormalY=0 NormalZ=1 AngleXU=0 Radius=2.5
    g5: Circle CenterX=-179.305 CenterY=-76.8316 CenterZ=0 NormalX=0 NormalY=0 NormalZ=1 AngleXU=0 Radius=2.5
    g6: Circle CenterX=-213.443 CenterY=-76.8316 CenterZ=0 NormalX=0 NormalY=0 NormalZ=1 AngleXU=0 Radius=2.5
  constraints (14):
    c: Diameter(g0) = 5
    c: Diameter(g1) = 5
    c: Diameter(g2) = 5
    c: Diameter(g3) = 5
    c: Diameter(g4) = 5
    c: Diameter(g5) = 5
    c: Diameter(g6) = 5
    c: Coincident(g0,g-8)
    c: Coincident(g1,g-9)
    c: Coincident(g2,g-6)
    c: Coincident(g3,g-7)
    c: Coincident(g4,g-5)
    c: Coincident(g5,g-4)
    c: Coincident(g6,g-3)
FEATURE [Part::Extrusion] Extrude018  label="Extrude fori M3x5x6 - dx"
  Base = -> Sketch022
  Dir = (0,-1,2e-16)
  DirMode = 2
  FaceMakerClass = Part::FaceMakerBullseye
  FaceMakerMode = 3
  LengthFwd = 6.2
  LengthRev = 0
  Placement = pos=(0,-9.5,0) rot=(0,0,1;0rad)
  Solid = true
  Symmetric = true
FEATURE [Part::Extrusion] Extrude019  label="Extrude fori M3x5x6 - sx"
  Base = -> Sketch022
  Dir = (0,-1,2e-16)
  DirMode = 2
  FaceMakerClass = Part::FaceMakerBullseye
  FaceMakerMode = 3
  LengthFwd = 6.2
  LengthRev = 0
  Placement = pos=(0,9.5,0) rot=(0,0,1;0rad)
  Solid = true
  Symmetric = true
FEATURE [Sketcher::SketchObject] Sketch023  label="foro anteriore M3x5x6"
  ArcFitTolerance = 1e-06
  AttachmentSupport = -> [YZ_Plane]
  FullyConstrained = true
  MakeInternals = false
  MapMode = 5
  Placement = pos=(0,0,0) rot=(0.57735,0.57735,0.57735;2.0944rad)
  sketch-geometry (2):
    g0: LineSegment [constr] StartX=0 StartY=0 StartZ=0 EndX=0 EndY=38.6 EndZ=0
    g1: Circle CenterX=0 CenterY=38.6 CenterZ=0 NormalX=0 NormalY=0 NormalZ=1 AngleXU=0 Radius=2.5
  constraints (5):
    c: Coincident(g0,g-1)
    c: PointOnObject(g0,g-2)
    c: DistanceY(g0,g0) = 38.6
    c: Diameter(g1) = 5
    c: Coincident(g1,g0)
FEATURE [Part::Extrusion] Extrude020  label="Extrude foro anteriore M3x5x6"
  Base = -> Sketch023
  Dir = (1,0,0)
  DirMode = 2
  FaceMakerClass = Part::FaceMakerBullseye
  FaceMakerMode = 3
  LengthFwd = -6.2
  LengthRev = 0
  Solid = true
  Symmetric = false
FEATURE [Sketcher::SketchObject] Sketch024  label="fori per viti frontale"
  ArcFitTolerance = 1e-06
  AttachmentSupport = -> [YZ_Plane]
  FullyConstrained = true
  MakeInternals = false
  MapMode = 5
  Placement = pos=(0,0,0) rot=(0.57735,0.57735,0.57735;2.0944rad)
  sketch-geometry (9):
    g0: LineSegment [constr] StartX=-10.3 StartY=30.721 StartZ=0 EndX=10.3 EndY=30.721 EndZ=0
    g1: LineSegment [constr] StartX=10.3 StartY=30.721 StartZ=0 EndX=10.3 EndY=10.121 EndZ=0
    g2: LineSegment [constr] StartX=10.3 StartY=10.121 StartZ=0 EndX=-10.3 EndY=10.121 EndZ=0
    g3: LineSegment [constr] StartX=-10.3 StartY=10.121 StartZ=0 EndX=-10.3 EndY=30.721 EndZ=0
    g4: LineSegment [constr] StartX=0 StartY=0 StartZ=0 EndX=0 EndY=10.121 EndZ=0
    g5: Circle CenterX=-10.3 CenterY=30.721 CenterZ=0 NormalX=0 NormalY=0 NormalZ=1 AngleXU=0 Radius=2
    g6: Circle CenterX=10.3 CenterY=30.721 CenterZ=0 NormalX=0 NormalY=0 NormalZ=1 AngleXU=0 Radius=2
    g7: Circle CenterX=-10.3 CenterY=10.121 CenterZ=0 NormalX=0 NormalY=0 NormalZ=1 AngleXU=0 Radius=2
    g8: Circle CenterX=10.3 CenterY=10.121 CenterZ=0 NormalX=0 NormalY=0 NormalZ=1 AngleXU=0 Radius=2
  constraints (22):
    c: Horizontal(g0)
    c: Coincident(g1,g0)
    c: Vertical(g1)
    c: Coincident(g2,g1)
    c: Horizontal(g2)
    c: Coincident(g3,g2)
    c: Coincident(g3,g0)
    c: Vertical(g3)
    c: DistanceX(g0,g0) = 20.6
    c: DistanceY(g3,g3) = 20.6
    c: Coincident(g4,g-1)
    c: PointOnObject(g4,g-2)
    c: DistanceY(g4,g4) = 10.121
    c: Symmetric(g2,g2,g4)
    c: Diameter(g5) = 4
    c: Diameter(g6) = 4
    c: Diameter(g7) = 4
    c: Diameter(g8) = 4
    c: Coincident(g5,g0)
    c: Coincident(g6,g0)
    c: Coincident(g7,g2)
    c: Coincident(g8,g1)
FEATURE [Part::Extrusion] Extrude021  label="Extrude fori per viti frontale"
  Base = -> Sketch024
  Dir = (1,0,0)
  DirMode = 2
  FaceMakerClass = Part::FaceMakerBullseye
  FaceMakerMode = 3
  LengthFwd = -2.4
  LengthRev = 0
  Solid = true
  Symmetric = false
FEATURE [Sketcher::SketchObject] Sketch025  label="foro per filo CAM"
  ArcFitTolerance = 1e-06
  AttachmentSupport = -> [XZ_Plane]
  ExternalGeometry = -> [Sketch]
  FullyConstrained = true
  MakeInternals = false
  MapMode = 5
  Placement = pos=(0,0,0) rot=(1,0,0;1.5708rad)
  sketch-geometry (4):
    g0: LineSegment StartX=-44.6 StartY=41.2 StartZ=0 EndX=-44.6 EndY=36.4 EndZ=0
    g1: LineSegment StartX=-44.6 StartY=36.4 StartZ=0 EndX=-54.6 EndY=36.4 EndZ=0
    g2: LineSegment StartX=-54.6 StartY=36.4 StartZ=0 EndX=-50.4 EndY=41.2 EndZ=0
    g3: LineSegment StartX=-50.4 StartY=41.2 StartZ=0 EndX=-44.6 EndY=41.2 EndZ=0
  constraints (11):
    c: Vertical(g0)
    c: Coincident(g1,g0)
    c: Horizontal(g1)
    c: Coincident(g2,g1)
    c: Coincident(g3,g2)
    c: Coincident(g3,g0)
    c: Horizontal(g3)
    c: Coincident(g0,g-3)
    c: DistanceY(g0,g-4) = 0
    c: DistanceX(g3,g3) = 5.8
    c: DistanceX(g1,g1) = 10
FEATURE [Part::Extrusion] Extrude022  label="Extrude foro per filo CAM dx"
  Base = -> Sketch025
  Dir = (0,-1,2e-16)
  DirMode = 2
  FaceMakerClass = Part::FaceMakerBullseye
  FaceMakerMode = 3
  LengthFwd = 4.9
  LengthRev = 0
  Placement = pos=(0,6.95,0) rot=(0,0,1;0rad)
  Solid = true
  Symmetric = true
FEATURE [Part::Extrusion] Extrude023  label="Extrude foro per filo CAM sx"
  Base = -> Sketch025
  Dir = (0,-1,2e-16)
  DirMode = 2
  FaceMakerClass = Part::FaceMakerBullseye
  FaceMakerMode = 3
  LengthFwd = 4.9
  LengthRev = 0
  Placement = pos=(0,-6.95,0) rot=(0,0,1;0rad)
  Solid = true
  Symmetric = true
FEATURE [Sketcher::SketchObject] Sketch026  label="foro sotto anteriore M3x5x6"
  ArcFitTolerance = 1e-06
  AttachmentSupport = -> [XY_Plane]
  FullyConstrained = true
  MakeInternals = false
  MapMode = 5
  sketch-geometry (2):
    g0: LineSegment [constr] StartX=0 StartY=0 StartZ=0 EndX=-16.5 EndY=0 EndZ=0
    g1: Circle CenterX=-16.5 CenterY=0 CenterZ=0 NormalX=0 NormalY=0 NormalZ=1 AngleXU=0 Radius=2.5
  constraints (5):
    c: Distance(g0) = 16.5
    c: Coincident(g0,g-1)
    c: PointOnObject(g0,g-1)
    c: Diameter(g1) = 5
    c: Coincident(g0,g1)
FEATURE [Sketcher::SketchObject] Sketch027  label="foro sotto posteriore M3x5x6"
  ArcFitTolerance = 1e-06
  AttachmentSupport = -> [XY_Plane]
  ExternalGeometry = -> [Sketch]
  FullyConstrained = true
  MakeInternals = false
  MapMode = 5
  sketch-geometry (2):
    g0: LineSegment [constr] StartX=-82.8 StartY=2e-16 StartZ=0 EndX=-71.3 EndY=2e-16 EndZ=0
    g1: Circle CenterX=-71.3 CenterY=2e-16 CenterZ=0 NormalX=0 NormalY=0 NormalZ=1 AngleXU=0 Radius=2.5
  constraints (5):
    c: Distance(g0) = 11.5
    c: Coincident(g0,g-3)
    c: PointOnObject(g0,g-3)
    c: Diameter(g1) = 5
    c: Coincident(g1,g0)
FEATURE [Sketcher::SketchObject] Sketch029  label="fori sotto impugnatura"
  ArcFitTolerance = 1e-06
  AttachmentSupport = -> [XY_Plane]
  ExternalGeometry = -> [Sketch]
  FullyConstrained = true
  MakeInternals = false
  MapMode = 5
  sketch-geometry (15):
    g0: LineSegment [constr] StartX=-175.232 StartY=-1.83e-14 StartZ=0 EndX=-191.232 EndY=0 EndZ=0
    g1: Circle CenterX=-191.232 CenterY=0 CenterZ=0 NormalX=0 NormalY=0 NormalZ=1 AngleXU=0 Radius=3.95
    g2: LineSegment [constr] StartX=-175.232 StartY=-1.83e-14 StartZ=0 EndX=-204.275 EndY=0 EndZ=0
    g3: LineSegment StartX=-204.275 StartY=3.525 StartZ=0 EndX=-204.275 EndY=-3.525 EndZ=0
    g4: LineSegment StartX=-205.4 StartY=-4.65 StartZ=0 EndX=-206.65 EndY=-4.65 EndZ=0
    g5: LineSegment StartX=-207.775 StartY=-3.525 StartZ=0 EndX=-207.775 EndY=3.525 EndZ=0
    g6: LineSegment StartX=-206.65 StartY=4.65 StartZ=0 EndX=-205.4 EndY=4.65 EndZ=0
    g7: ArcOfCircle CenterX=-206.65 CenterY=3.525 CenterZ=0 NormalX=0 NormalY=0 NormalZ=1 AngleXU=0 Radius=1.125 StartAngle=1.5708 EndAngle=3.14159
    g8: GeomPoint [constr] X=-207.775 Y=4.65 Z=0
    g9: ArcOfCircle CenterX=-205.4 CenterY=3.525 CenterZ=0 NormalX=0 NormalY=0 NormalZ=1 AngleXU=0 Radius=1.125 StartAngle=0 EndAngle=1.5708
    g10: GeomPoint [constr] X=-204.275 Y=4.65 Z=0
    g11: ArcOfCircle CenterX=-205.4 CenterY=-3.525 CenterZ=0 NormalX=0 NormalY=0 NormalZ=1 AngleXU=0 Radius=1.125 StartAngle=4.71239 EndAngle=6.28319
    g12: GeomPoint [constr] X=-204.275 Y=-4.65 Z=0
    g13: ArcOfCircle CenterX=-206.65 CenterY=-3.525 CenterZ=0 NormalX=0 NormalY=0 NormalZ=1 AngleXU=0 Radius=1.125 StartAngle=3.14159 EndAngle=4.71239
    g14: GeomPoint [constr] X=-207.775 Y=-4.65 Z=0
  constraints (35):
    c: Distance(g0) = 16
    c: Coincident(g0,g-3)
    c: PointOnObject(g0,g-1)
    c: Diameter(g1) = 7.9
    c: Coincident(g1,g0)
    c: Coincident(g2,g0)
    c: PointOnObject(g2,g-1)
    c: Vertical(g3)
    c: Horizontal(g4)
    c: Vertical(g5)
    c: Horizontal(g6)
    c: DistanceY(g12,g10) = 9.3
    c: DistanceX(g8,g10) = 3.5
    c: Symmetric(g10,g12,g2)
    c: PointOnObject(g8,g5)
    c: PointOnObject(g8,g6)
    c: Tangent(g5,g7) = 1.5708
    c: Tangent(g6,g7) = 1.5708
    c: PointOnObject(g10,g3)
    c: PointOnObject(g10,g6)
    c: Tangent(g3,g9) = 1.5708
    c: Tangent(g6,g9) = 1.5708
    c: PointOnObject(g12,g3)
    c: PointOnObject(g12,g4)
    c: Tangent(g3,g11) = 1.5708
    c: Tangent(g4,g11) = 1.5708
    c: PointOnObject(g14,g4)
    c: PointOnObject(g14,g5)
    c: Tangent(g4,g13) = 1.5708
    c: Tangent(g5,g13) = 1.5708
    c: Equal(g7,g9)
    c: Equal(g9,g11)
    c: Equal(g11,g13)
    c: DistanceX(g6,g6) = 1.25
    c: DistanceX(g-5,g5) = 6.8
FEATURE [Sketcher::SketchObject] Sketch030  label="fori superiori per solenoide e oled"
  ArcFitTolerance = 1e-06
  AttachmentSupport = -> [XY_Plane]
  ExternalGeometry = -> [Sketch]
  FullyConstrained = true
  MakeInternals = false
  MapMode = 5
  sketch-geometry (33):
    g0: LineSegment [constr] StartX=-181.6 StartY=1.12e-14 StartZ=0 EndX=-169.91 EndY=0 EndZ=0
    g1: LineSegment [constr] StartX=-169.91 StartY=0 StartZ=0 EndX=-169.91 EndY=-2.6 EndZ=0
    g2: LineSegment [constr] StartX=-169.91 StartY=0 StartZ=0 EndX=-169.91 EndY=2.6 EndZ=0
    g3: LineSegment StartX=-169.91 StartY=4.975 StartZ=0 EndX=-169.91 EndY=8.225 EndZ=0
    g4: LineSegment StartX=-167.535 StartY=10.6 StartZ=0 EndX=-167.285 EndY=10.6 EndZ=0
    g5: LineSegment StartX=-164.91 StartY=8.225 StartZ=0 EndX=-164.91 EndY=4.975 EndZ=0
    g6: LineSegment StartX=-167.285 StartY=2.6 StartZ=0 EndX=-167.535 EndY=2.6 EndZ=0
    g7: LineSegment StartX=-169.91 StartY=-4.975 StartZ=0 EndX=-169.91 EndY=-8.225 EndZ=0
    g8: LineSegment StartX=-167.535 StartY=-10.6 StartZ=0 EndX=-167.285 EndY=-10.6 EndZ=0
    g9: LineSegment StartX=-164.91 StartY=-8.225 StartZ=0 EndX=-164.91 EndY=-4.975 EndZ=0
    g10: LineSegment StartX=-167.285 StartY=-2.6 StartZ=0 EndX=-167.535 EndY=-2.6 EndZ=0
    g11: ArcOfCircle CenterX=-167.535 CenterY=8.225 CenterZ=0 NormalX=0 NormalY=0 NormalZ=1 AngleXU=0 Radius=2.375 StartAngle=1.5708 EndAngle=3.14159
    g12: GeomPoint [constr] X=-169.91 Y=10.6 Z=0
    g13: ArcOfCircle CenterX=-167.285 CenterY=8.225 CenterZ=0 NormalX=0 NormalY=0 NormalZ=1 AngleXU=0 Radius=2.375 StartAngle=0 EndAngle=1.5708
    g14: GeomPoint [constr] X=-164.91 Y=10.6 Z=0
    g15: ArcOfCircle CenterX=-167.285 CenterY=4.975 CenterZ=0 NormalX=0 NormalY=0 NormalZ=1 AngleXU=0 Radius=2.375 StartAngle=4.71239 EndAngle=6.28319
    g16: GeomPoint [constr] X=-164.91 Y=2.6 Z=0
    g17: ArcOfCircle CenterX=-167.535 CenterY=4.975 CenterZ=0 NormalX=0 NormalY=0 NormalZ=1 AngleXU=0 Radius=2.375 StartAngle=3.14159 EndAngle=4.71239
    g18: GeomPoint [constr] X=-169.91 Y=2.6 Z=0
    g19: ArcOfCircle CenterX=-167.535 CenterY=-4.975 CenterZ=0 NormalX=0 NormalY=0 NormalZ=1 AngleXU=0 Radius=2.375 StartAngle=1.5708 EndAngle=3.14159
    g20: GeomPoint [constr] X=-169.91 Y=-2.6 Z=0
    g21: ArcOfCircle CenterX=-167.285 CenterY=-4.975 CenterZ=0 NormalX=0 NormalY=0 NormalZ=1 AngleXU=0 Radius=2.375 StartAngle=0 EndAngle=1.5708
    g22: GeomPoint [constr] X=-164.91 Y=-2.6 Z=0
    g23: ArcOfCircle CenterX=-167.285 CenterY=-8.225 CenterZ=0 NormalX=0 NormalY=0 NormalZ=1 AngleXU=0 Radius=2.375 StartAngle=4.71239 EndAngle=6.28319
    g24: GeomPoint [constr] X=-164.91 Y=-10.6 Z=0
    g25: ArcOfCircle CenterX=-167.535 CenterY=-8.225 CenterZ=0 NormalX=0 NormalY=0 NormalZ=1 AngleXU=0 Radius=2.375 StartAngle=3.14159 EndAngle=4.71239
    g26: GeomPoint [constr] X=-169.91 Y=-10.6 Z=0
    g27: LineSegment [constr] StartX=-181.6 StartY=1.12e-14 StartZ=0 EndX=-152.209 EndY=0 EndZ=0
    g28: LineSegment [constr] StartX=-181.6 StartY=1.12e-14 StartZ=0 EndX=-130.41 EndY=0 EndZ=0
    g29: LineSegment [constr] StartX=-152.209 StartY=0 StartZ=0 EndX=-152.209 EndY=6.95 EndZ=0
    g30: LineSegment [constr] StartX=-130.41 StartY=0 StartZ=0 EndX=-130.41 EndY=-6.95 EndZ=0
    g31: Circle CenterX=-152.209 CenterY=6.95 CenterZ=0 NormalX=0 NormalY=0 NormalZ=1 AngleXU=0 Radius=2.1
    g32: Circle CenterX=-130.41 CenterY=-6.95 CenterZ=0 NormalX=0 NormalY=0 NormalZ=1 AngleXU=0 Radius=2.1
  constraints (79):
    c: Distance(g0) = 11.69
    c: PointOnObject(g0,g-1)
    c: Coincident(g-4,g0)
    c: Distance(g1) = 2.6
    c: Coincident(g1,g0)
    c: Vertical(g1)
    c: Distance(g2) = 2.6
    c: Coincident(g2,g0)
    c: Vertical(g2)
    c: Distance(g18,g12) = 8
    c: Coincident(g18,g2)
    c: Vertical(g3)
    c: Distance(g14,g12) = 5
    c: Horizontal(g4)
    c: Distance(g16,g14) = 8
    c: Vertical(g5)
    c: Distance(g26,g20) = 8
    c: Coincident(g20,g1)
    c: Vertical(g7)
    c: Distance(g26,g24) = 5
    c: Horizontal(g8)
    c: Distance(g24,g22) = 8
    c: Vertical(g9)
    c: PointOnObject(g12,g3)
    c: PointOnObject(g12,g4)
    c: Tangent(g3,g11) = 1.5708
    c: Tangent(g4,g11) = 1.5708
    c: PointOnObject(g14,g5)
    c: PointOnObject(g14,g4)
    c: Tangent(g5,g13) = 1.5708
    c: Tangent(g4,g13) = 1.5708
    c: PointOnObject(g16,g5)
    c: PointOnObject(g16,g6)
    c: Tangent(g5,g15) = 1.5708
    c: Tangent(g6,g15) = 1.5708
    c: PointOnObject(g18,g3)
    c: PointOnObject(g18,g6)
    c: Tangent(g3,g17) = 1.5708
    c: Tangent(g6,g17) = 1.5708
    c: Equal(g11,g13)
    c: Equal(g13,g15)
    c: Equal(g15,g17)
    c: DistanceX(g4,g4) = 0.25
    c: PointOnObject(g20,g7)
    c: PointOnObject(g20,g10)
    c: Tangent(g7,g19) = -1.5708
    c: Tangent(g10,g19) = -1.5708
    c: PointOnObject(g22,g9)
    c: PointOnObject(g22,g10)
    c: Tangent(g9,g21) = -1.5708
    c: Tangent(g10,g21) = -1.5708
    c: PointOnObject(g24,g9)
    c: PointOnObject(g24,g8)
    c: Tangent(g9,g23) = -1.5708
    c: Tangent(g8,g23) = -1.5708
    c: PointOnObject(g26,g8)
    c: PointOnObject(g26,g7)
    c: Tangent(g8,g25) = -1.5708
    c: Tangent(g7,g25) = -1.5708
    c: Equal(g19,g21)
    c: Equal(g21,g23)
    c: Equal(g23,g25)
    c: DistanceX(g10,g10) = 0.25
    c: Distance(g27) = 29.391
    c: Coincident(g27,g0)
    c: PointOnObject(g27,g-1)
    c: Distance(g28) = 51.19
    c: Coincident(g28,g0)
    c: PointOnObject(g28,g-1)
    c: Distance(g29) = 6.95
    c: Coincident(g29,g27)
    c: Vertical(g29)
    c: Distance(g30) = 6.95
    c: Coincident(g30,g28)
    c: Vertical(g30)
    c: Diameter(g31) = 4.2
    c: Diameter(g32) = 4.2
    c: Coincident(g32,g30)
    c: Coincident(g31,g29)
FEATURE [Sketcher::SketchObject] Sketch031  label="fori inferiori switch pompa"
  ArcFitTolerance = 1e-06
  AttachmentSupport = -> [XY_Plane]
  ExternalGeometry = -> [Sketch]
  FullyConstrained = true
  MakeInternals = false
  MapMode = 5
  sketch-geometry (4):
    g0: LineSegment [constr] StartX=-57.2 StartY=1.9e-15 StartZ=0 EndX=-62.45 EndY=1.9e-15 EndZ=0
    g1: LineSegment [constr] StartX=-62.45 StartY=3.25 StartZ=0 EndX=-62.45 EndY=-3.25 EndZ=0
    g2: Circle CenterX=-62.45 CenterY=3.25 CenterZ=0 NormalX=0 NormalY=0 NormalZ=1 AngleXU=0 Radius=1.6
    g3: Circle CenterX=-62.45 CenterY=-3.25 CenterZ=0 NormalX=0 NormalY=0 NormalZ=1 AngleXU=0 Radius=1.6
  constraints (10):
    c: Distance(g0) = 5.25
    c: Coincident(g0,g-3)
    c: PointOnObject(g0,g-3)
    c: Vertical(g1)
    c: DistanceY(g1,g1) = 6.5
    c: Symmetric(g1,g1,g0)
    c: Diameter(g2) = 3.2
    c: Diameter(g3) = 3.2
    c: Coincident(g2,g1)
    c: Coincident(g3,g1)
FEATURE [Sketcher::SketchObject] Sketch032  label="spazio per PILA 18650"
  ArcFitTolerance = 1e-06
  AttachmentSupport = -> [XY_Plane]
  ExternalGeometry = -> [Sketch]
  FullyConstrained = true
  MakeInternals = false
  MapMode = 5
  sketch-geometry (2):
    g0: LineSegment [constr] StartX=-178.142 StartY=-1.74e-14 StartZ=0 EndX=-191.142 EndY=-1.83e-14 EndZ=0
    g1: Circle CenterX=-191.142 CenterY=-1.83e-14 CenterZ=0 NormalX=0 NormalY=0 NormalZ=1 AngleXU=0 Radius=10.5
  constraints (5):
    c: Distance(g0) = 13
    c: Coincident(g0,g-3)
    c: PointOnObject(g0,g-4)
    c: Diameter(g1) = 21
    c: Coincident(g1,g0)
FEATURE [Part::Extrusion] Extrude030  label="Extrude spazio per PILA 18650"
  Base = -> Sketch032
  Dir = (0,0,1)
  DirLink = -> Sketch [Edge45]
  DirMode = 2
  FaceMakerClass = Part::FaceMakerBullseye
  FaceMakerMode = 3
  LengthFwd = 76
  LengthRev = 0
  Placement = pos=(6,0,-72) rot=(0,0,1;0rad)
  Solid = true
  Symmetric = false
FEATURE [Sketcher::SketchObject] Sketch033  label="fermo per scheda micro"
  ArcFitTolerance = 1e-06
  AttachmentSupport = -> [XZ_Plane]
  ExternalGeometry = -> [Sketch]
  FullyConstrained = true
  MakeInternals = false
  MapMode = 5
  Placement = pos=(0,0,0) rot=(1,0,0;1.5708rad)
  sketch-geometry (12):
    g0: LineSegment StartX=-11.6 StartY=6 StartZ=0 EndX=-4 EndY=6 EndZ=0
    g1: LineSegment StartX=-4 StartY=6 StartZ=0 EndX=-4 EndY=36.4 EndZ=0
    g2: LineSegment StartX=-4 StartY=36.4 StartZ=0 EndX=-11.6 EndY=36.4 EndZ=0
    g3: LineSegment StartX=-11.6 StartY=36.4 StartZ=0 EndX=-11.6 EndY=6 EndZ=0
    g4: LineSegment StartX=-80.11 StartY=11.6 StartZ=0 EndX=-70.51 EndY=11.6 EndZ=0
    g5: LineSegment StartX=-70.51 StartY=11.6 StartZ=0 EndX=-70.51 EndY=6 EndZ=0
    g6: LineSegment StartX=-70.51 StartY=6 StartZ=0 EndX=-80.11 EndY=6 EndZ=0
    g7: LineSegment StartX=-80.11 StartY=6 StartZ=0 EndX=-80.11 EndY=11.6 EndZ=0
    g8: LineSegment StartX=-78.51 StartY=36.4 StartZ=0 EndX=-70.51 EndY=36.4 EndZ=0
    g9: LineSegment StartX=-70.51 StartY=36.4 StartZ=0 EndX=-70.51 EndY=30.8 EndZ=0
    g10: LineSegment StartX=-70.51 StartY=30.8 StartZ=0 EndX=-78.51 EndY=30.8 EndZ=0
    g11: LineSegment StartX=-78.51 StartY=30.8 StartZ=0 EndX=-78.51 EndY=36.4 EndZ=0
  constraints (33):
    c: Horizontal(g0)
    c: Coincident(g1,g0)
    c: Coincident(g2,g1)
    c: Horizontal(g2)
    c: Coincident(g3,g2)
    c: Coincident(g3,g0)
    c: Vertical(g3)
    c: DistanceX(g2,g2) = 7.6
    c: Coincident(g1,g-3)
    c: Coincident(g0,g-3)
    c: Horizontal(g4)
    c: Coincident(g5,g4)
    c: Vertical(g5)
    c: Coincident(g6,g5)
    c: Horizontal(g6)
    c: Coincident(g7,g6)
    c: Coincident(g7,g4)
    c: Vertical(g7)
    c: DistanceY(g5,g5) = 5.6
    c: DistanceX(g4,g4) = 9.6
    c: Coincident(g9,g8)
    c: Vertical(g9)
    c: Coincident(g10,g9)
    c: Horizontal(g10)
    c: Coincident(g11,g10)
    c: Coincident(g11,g8)
    c: Vertical(g11)
    c: DistanceY(g9,g9) = 5.6
    c: DistanceX(g10,g10) = 8
    c: Coincident(g4,g-4)
    c: DistanceX(g4,g10) = 1.6
    c: Horizontal(g8)
    c: DistanceY(g8,g1) = 0
FEATURE [Sketcher::SketchObject] Sketch034  label="buchi guida rail"
  ArcFitTolerance = 1e-06
  AttachmentSupport = -> [XY_Plane]
  ExternalGeometry = -> [Sketch]
  FullyConstrained = true
  MakeInternals = false
  MapMode = 5
  sketch-geometry (6):
    g0: LineSegment [constr] StartX=-100.8 StartY=9.1e-15 StartZ=0 EndX=-93.3 EndY=0 EndZ=0
    g1: LineSegment [constr] StartX=-93.3 StartY=0 StartZ=0 EndX=-73.3 EndY=0 EndZ=0
    g2: LineSegment [constr] StartX=-73.3 StartY=0 StartZ=0 EndX=-53.3 EndY=0 EndZ=0
    g3: Circle CenterX=-93.3 CenterY=0 CenterZ=0 NormalX=0 NormalY=0 NormalZ=1 AngleXU=0 Radius=2.5
    g4: Circle CenterX=-73.3 CenterY=0 CenterZ=0 NormalX=0 NormalY=0 NormalZ=1 AngleXU=0 Radius=2.5
    g5: Circle CenterX=-53.3 CenterY=0 CenterZ=0 NormalX=0 NormalY=0 NormalZ=1 AngleXU=0 Radius=2.5
  constraints (15):
    c: Distance(g0) = 7.5
    c: Coincident(g0,g-3)
    c: PointOnObject(g0,g-1)
    c: Distance(g1) = 20
    c: Coincident(g1,g0)
    c: PointOnObject(g1,g-1)
    c: Distance(g2) = 20
    c: Coincident(g2,g1)
    c: PointOnObject(g2,g-1)
    c: Diameter(g3) = 5
    c: Diameter(g4) = 5
    c: Diameter(g5) = 5
    c: Coincident(g3,g0)
    c: Coincident(g4,g1)
    c: Coincident(g5,g2)
FEATURE [Part::Extrusion] Extrude032  label="Extrude buchi guida rail"
  Base = -> Sketch034
  Dir = (0,0,1)
  DirMode = 2
  FaceMakerClass = Part::FaceMakerBullseye
  FaceMakerMode = 3
  LengthFwd = -6.2
  LengthRev = 0
  Placement = pos=(0,0,43.2) rot=(0,0,1;0rad)
  Solid = true
  Symmetric = false
FEATURE [Part::Extrusion] Extrude033  label="Extrude fori superiori per solenoide e oled001"
  Base = -> Sketch030
  Dir = (0,0,1)
  DirMode = 2
  FaceMakerClass = Part::FaceMakerBullseye
  FaceMakerMode = 3
  LengthFwd = -4.8
  LengthRev = 0
  Placement = pos=(0,0,41.2) rot=(0,0,1;0rad)
  Solid = true
  Symmetric = false
FEATURE [Part::Extrusion] Extrude034  label="Extrude fori sotto impugnatura001"
  Base = -> Sketch029
  Dir = (0,0,1)
  DirMode = 2
  FaceMakerClass = Part::FaceMakerBullseye
  FaceMakerMode = 3
  LengthFwd = 5
  LengthRev = 0
  Placement = pos=(0,0,-83) rot=(0,0,1;0rad)
  Solid = true
  Symmetric = false
FEATURE [Part::Extrusion] Extrude035  label="Extrude fori inferiori switch pompa001"
  Base = -> Sketch031
  Dir = (0,0,1)
  DirMode = 2
  FaceMakerClass = Part::FaceMakerBullseye
  FaceMakerMode = 3
  LengthFwd = 4
  LengthRev = 0
  Placement = pos=(0,0,-1.7) rot=(0,0,1;0rad)
  Solid = true
  Symmetric = false
FEATURE [Part::Extrusion] Extrude036  label="Extrude foro sotto posteriore M3x5x007"
  Base = -> Sketch027
  Dir = (0,0,1)
  DirMode = 2
  FaceMakerClass = Part::FaceMakerBullseye
  FaceMakerMode = 3
  LengthFwd = 6.2
  LengthRev = 0
  Placement = pos=(0,0,-9.6) rot=(0,0,1;0rad)
  Solid = true
  Symmetric = false
FEATURE [Part::Extrusion] Extrude037  label="Extrude foro sotto anteriore M3x5x007"
  Base = -> Sketch026
  Dir = (0,0,1)
  DirMode = 2
  FaceMakerClass = Part::FaceMakerBullseye
  FaceMakerMode = 3
  LengthFwd = 6.2
  LengthRev = 0
  Solid = true
  Symmetric = false
FEATURE [Sketcher::SketchObject] Sketch035  label="foro per fissaggio micro"
  ArcFitTolerance = 1e-06
  AttachmentSupport = -> [XZ_Plane]
  ExternalGeometry = -> [Sketch,Sketch033]
  FullyConstrained = true
  MakeInternals = false
  MapMode = 5
  Placement = pos=(0,0,0) rot=(1,0,0;1.5708rad)
  sketch-geometry (3):
    g0: Circle CenterX=-7.8 CenterY=21.2 CenterZ=0 NormalX=0 NormalY=0 NormalZ=1 AngleXU=0 Radius=1.6
    g1: GeomPoint [constr] X=-4 Y=21.2 Z=0
    g2: LineSegment [constr] StartX=-4 StartY=21.2 StartZ=0 EndX=-11.6 EndY=21.2 EndZ=0
  constraints (6):
    c: Diameter(g0) = 3.2
    c: Symmetric(g-3,g-3,g1)
    c: Coincident(g2,g1)
    c: Horizontal(g2)
    c: DistanceX(g-4,g2) = 0
    c: Symmetric(g2,g1,g0)
FEATURE [Part::Extrusion] Extrude038  label="Extrude foro per fissaggio micro"
  Base = -> Sketch035
  Dir = (0,-1,2e-16)
  DirMode = 2
  FaceMakerClass = Part::FaceMakerBullseye
  FaceMakerMode = 3
  LengthFwd = 3
  LengthRev = 0
  Placement = pos=(0,8.6,0) rot=(0,0,1;0rad)
  Solid = true
  Symmetric = false
FEATURE [Sketcher::SketchObject] Sketch036  label="supporto per alimentatore"
  ArcFitTolerance = 1e-06
  AttachmentSupport = -> [XZ_Plane]
  ExternalGeometry = -> [Sketch,Sketch016,Sketch022]
  FullyConstrained = true
  MakeInternals = false
  MapMode = 5
  Placement = pos=(0,0,0) rot=(1,0,0;1.5708rad)
  sketch-geometry (5):
    g0: LineSegment StartX=-211.843 StartY=-50.0944 StartZ=0 EndX=-211.843 EndY=-80.4316 EndZ=0
    g1: LineSegment StartX=-211.843 StartY=-50.0944 StartZ=0 EndX=-207.775 EndY=-41.3701 EndZ=0
    g2: LineSegment [constr] StartX=-209.443 StartY=-50.0944 StartZ=0 EndX=-209.443 EndY=-80.4316 EndZ=0
    g3: LineSegment StartX=-207.775 StartY=-41.3701 StartZ=0 EndX=-207.775 EndY=-80.4316 EndZ=0
    g4: LineSegment StartX=-211.843 StartY=-80.4316 StartZ=0 EndX=-207.775 EndY=-80.4316 EndZ=0
  constraints (15):
    c: Vertical(g0)
    c: Coincident(g1,g0)
    c: Vertical(g2)
    c: Tangent(g2,g-5)
    c: Coincident(g3,g1)
    c: Vertical(g3)
    c: DistanceY(g-3,g3) = -2
    c: Tangent(g1,g-8)
    c: DistanceY(g-3,g0) = -2
    c: Coincident(g4,g0)
    c: Coincident(g4,g3)
    c: Tangent(g0,g-6)
    c: DistanceY(g-3,g2) = -2
    c: DistanceY(g2,g0) = 0
    c: DistanceX(g-3,g3) = 6.8
FEATURE [Part::Extrusion] Extrude039  label="Extrude039 supporto alimentatore"
  Base = -> Sketch036
  Dir = (0,-1,2e-16)
  DirMode = 2
  FaceMakerClass = Part::FaceMakerBullseye
  FaceMakerMode = 3
  LengthFwd = 25.2
  LengthRev = 0
  Solid = true
  Symmetric = true
FEATURE [Sketcher::SketchObject] Sketch037  label="scavo per alimentatore"
  ArcFitTolerance = 1e-06
  AttachmentSupport = -> [XZ_Plane]
  ExternalGeometry = -> [Sketch036]
  FullyConstrained = true
  MakeInternals = false
  MapMode = 5
  Placement = pos=(0,0,0) rot=(1,0,0;1.5708rad)
  sketch-geometry (4):
    g0: LineSegment StartX=-209.575 StartY=-50.4316 StartZ=0 EndX=-209.575 EndY=-80.4316 EndZ=0
    g1: LineSegment StartX=-209.575 StartY=-50.4316 StartZ=0 EndX=-207.775 EndY=-50.4316 EndZ=0
    g2: LineSegment StartX=-207.775 StartY=-50.4316 StartZ=0 EndX=-207.775 EndY=-80.4316 EndZ=0
    g3: LineSegment StartX=-207.775 StartY=-80.4316 StartZ=0 EndX=-209.575 EndY=-80.4316 EndZ=0
  constraints (11):
    c: Vertical(g0)
    c: Coincident(g1,g0)
    c: Horizontal(g1)
    c: Coincident(g2,g1)
    c: Vertical(g2)
    c: Coincident(g3,g2)
    c: Coincident(g3,g0)
    c: Horizontal(g3)
    c: DistanceX(g1,g1) = 1.8
    c: Coincident(g2,g-3)
    c: DistanceY(g2,g2) = 30
FEATURE [Part::Extrusion] Extrude040  label="Extrude040 scavo alimentatore"
  Base = -> Sketch037
  Dir = (0,-1,2e-16)
  DirMode = 2
  FaceMakerClass = Part::FaceMakerBullseye
  FaceMakerMode = 3
  LengthFwd = 19.5
  LengthRev = 0
  Solid = true
  Symmetric = true
FEATURE [Part::Extrusion] Extrude031  label="Extrude fermo per scheda micro"
  Base = -> Sketch033
  Dir = (0,-1,2e-16)
  DirMode = 2
  FaceMakerClass = Part::FaceMakerBullseye
  FaceMakerMode = 3
  LengthFwd = 3
  LengthRev = 0
  Placement = pos=(0,8.6,0) rot=(0,0,1;0rad)
  Solid = true
  Symmetric = false
FEATURE [Sketcher::SketchObject] Sketch038  label="scavo driver solenoide"
  ArcFitTolerance = 1e-06
  AttachmentSupport = -> [XZ_Plane]
  ExternalGeometry = -> [Sketch,Sketch036]
  FullyConstrained = true
  MakeInternals = false
  MapMode = 5
  Placement = pos=(0,0,0) rot=(1,0,0;1.5708rad)
  sketch-geometry (7):
    g0: LineSegment StartX=-192.222 StartY=-8.0175 StartZ=0 EndX=-194.941 EndY=-6.74965 EndZ=0
    g1: LineSegment StartX=-194.941 StartY=-6.74965 StartZ=0 EndX=-212.269 EndY=-43.9083 EndZ=0
    g2: LineSegment StartX=-192.222 StartY=-8.0175 StartZ=0 EndX=-188.779 EndY=-9.62345 EndZ=0
    g3: LineSegment StartX=-188.779 StartY=-9.62345 StartZ=0 EndX=-205.357 EndY=-45.1761 EndZ=0
    g4: LineSegment StartX=-205.357 StartY=-45.1761 StartZ=0 EndX=-209.55 EndY=-45.1761 EndZ=0
    g5: LineSegment [constr] StartX=-212.269 StartY=-43.9083 StartZ=0 EndX=-209.55 EndY=-45.1761 EndZ=0
    g6: LineSegment StartX=-212.269 StartY=-43.9083 StartZ=0 EndX=-209.55 EndY=-45.1761 EndZ=0
  constraints (20):
    c: Coincident(g1,g0)
    c: Coincident(g3,g2)
    c: Coincident(g4,g3)
    c: Distance(g2) = 3.8
    c: Distance(g1) = 41
    c: Coincident(g5,g1)
    c: Distance(g5) = 3
    c: Perpendicular(g5,g-3)
    c: Parallel(g1,g-3)
    c: Perpendicular(g1,g0)
    c: Distance(g0) = 3
    c: Coincident(g6,g1)
    c: Parallel(g3,g-3)
    c: Perpendicular(g2,g3)
    c: Coincident(g2,g0)
    c: Perpendicular(g-4,g4)
    c: PointOnObject(g5,g-3)
    c: Distance(g-3,g5) = 9.6
    c: Coincident(g4,g5)
    c: Coincident(g6,g4)
FEATURE [Part::Extrusion] Extrude041  label="Extrude scavo driver solenoide"
  Base = -> Sketch038
  Dir = (0,-1,2e-16)
  DirMode = 2
  FaceMakerClass = Part::FaceMakerBullseye
  FaceMakerMode = 3
  LengthFwd = 20.6
  LengthRev = 0
  Solid = true
  Symmetric = true
FEATURE [Sketcher::SketchObject] Sketch039  label="scavo per cavo usb per micro"
  ArcFitTolerance = 1e-06
  AttachmentSupport = -> [XZ_Plane]
  ExternalGeometry = -> [Sketch,Sketch016]
  FullyConstrained = true
  MakeInternals = false
  MapMode = 5
  Placement = pos=(0,0,0) rot=(1,0,0;1.5708rad)
  sketch-geometry (4):
    g0: LineSegment StartX=-82.51 StartY=36.4 StartZ=0 EndX=-74.51 EndY=36.4 EndZ=0
    g1: LineSegment StartX=-74.51 StartY=36.4 StartZ=0 EndX=-74.51 EndY=30.8 EndZ=0
    g2: LineSegment StartX=-74.51 StartY=30.8 StartZ=0 EndX=-82.51 EndY=30.8 EndZ=0
    g3: LineSegment StartX=-82.51 StartY=30.8 StartZ=0 EndX=-82.51 EndY=36.4 EndZ=0
  constraints (11):
    c: Coincident(g1,g0)
    c: Vertical(g1)
    c: Coincident(g2,g1)
    c: Horizontal(g2)
    c: Coincident(g3,g2)
    c: Coincident(g3,g0)
    c: Vertical(g3)
    c: Tangent(g0,g-3)
    c: Tangent(g2,g-4)
    c: Tangent(g3,g-4)
    c: Tangent(g1,g-4)
FEATURE [Part::Extrusion] Extrude042  label="Extrude scavo per cavo usb per micro"
  Base = -> Sketch039
  Dir = (0,-1,2e-16)
  DirMode = 2
  FaceMakerClass = Part::FaceMakerBullseye
  FaceMakerMode = 3
  LengthFwd = 11.2
  LengthRev = 0
  Solid = true
  Symmetric = true
FEATURE [Sketcher::SketchObject] Sketch040  label="scavo saldature alimentatore connettore 5v"
  ArcFitTolerance = 1e-06
  AttachmentSupport = -> [XZ_Plane]
  ExternalGeometry = -> [Sketch037]
  FullyConstrained = true
  MakeInternals = false
  MapMode = 5
  Placement = pos=(0,0,0) rot=(1,0,0;1.5708rad)
  sketch-geometry (4):
    g0: LineSegment StartX=-211.175 StartY=-52.4316 StartZ=0 EndX=-211.175 EndY=-56.4316 EndZ=0
    g1: LineSegment StartX=-211.175 StartY=-52.4316 StartZ=0 EndX=-209.575 EndY=-52.4316 EndZ=0
    g2: LineSegment StartX=-209.575 StartY=-52.4316 StartZ=0 EndX=-209.575 EndY=-56.4316 EndZ=0
    g3: LineSegment StartX=-209.575 StartY=-56.4316 StartZ=0 EndX=-211.175 EndY=-56.4316 EndZ=0
  constraints (11):
    c: Vertical(g0)
    c: Coincident(g1,g0)
    c: Horizontal(g1)
    c: Coincident(g2,g1)
    c: Coincident(g3,g2)
    c: Coincident(g3,g0)
    c: Horizontal(g3)
    c: DistanceX(g1,g1) = 1.6
    c: DistanceY(g2,g2) = 4
    c: Tangent(g2,g-3)
    c: DistanceY(g1,g-3) = 2
FEATURE [Part::Extrusion] Extrude043  label="Extrude scavo saldature alimentatore connettore 5v"
  Base = -> Sketch040
  Dir = (0,-1,2e-16)
  DirMode = 2
  FaceMakerClass = Part::FaceMakerBullseye
  FaceMakerMode = 3
  LengthFwd = 8
  LengthRev = 0
  Solid = true
  Symmetric = true
FEATURE [Sketcher::SketchObject] Sketch041  label="scavo saldature alimentatore connettore 5v verticali"
  ArcFitTolerance = 1e-06
  AttachmentSupport = -> [XZ_Plane]
  ExternalGeometry = -> [Sketch037]
  FullyConstrained = true
  MakeInternals = false
  MapMode = 5
  Placement = pos=(0,0,0) rot=(1,0,0;1.5708rad)
  sketch-geometry (4):
    g0: LineSegment StartX=-211.175 StartY=-53.6316 StartZ=0 EndX=-209.575 EndY=-53.6316 EndZ=0
    g1: LineSegment StartX=-209.575 StartY=-53.6316 StartZ=0 EndX=-209.575 EndY=-76.6316 EndZ=0
    g2: LineSegment StartX=-209.575 StartY=-76.6316 StartZ=0 EndX=-211.175 EndY=-76.6316 EndZ=0
    g3: LineSegment StartX=-211.175 StartY=-76.6316 StartZ=0 EndX=-211.175 EndY=-53.6316 EndZ=0
  constraints (11):
    c: Horizontal(g0)
    c: Coincident(g1,g0)
    c: Coincident(g2,g1)
    c: Horizontal(g2)
    c: Coincident(g3,g2)
    c: Coincident(g3,g0)
    c: Vertical(g3)
    c: DistanceY(g3,g3) = 23
    c: DistanceX(g0,g0) = 1.6
    c: Tangent(g1,g-3)
    c: DistanceY(g0,g-3) = 3.2
FEATURE [Part::Extrusion] Extrude044  label="Extrude scavo saldature alimentatore connettore 5v verticali"
  Base = -> Sketch041
  Dir = (0,-1,2e-16)
  DirMode = 2
  FaceMakerClass = Part::FaceMakerBullseye
  FaceMakerMode = 3
  LengthFwd = 3.2
  LengthRev = 0
  Placement = pos=(0,8.3,0) rot=(0,0,1;0rad)
  Solid = true
  Symmetric = false
FEATURE [Sketcher::SketchObject] Sketch042  label="fermi per driver solenoide e alimentatore"
  ArcFitTolerance = 1e-06
  AttachmentSupport = -> [XZ_Plane]
  ExternalGeometry = -> [Sketch036,Sketch037,Sketch,Sketch038]
  FullyConstrained = true
  MakeInternals = false
  MapMode = 5
  Placement = pos=(0,0,0) rot=(1,0,0;1.5708rad)
  sketch-geometry (27):
    g0: LineSegment StartX=-200.506 StartY=-25.7811 StartZ=0 EndX=-201.436 EndY=-27.775 EndZ=0
    g1: LineSegment StartX=-201.436 StartY=-27.775 StartZ=0 EndX=-199.442 EndY=-28.7048 EndZ=0
    g2: LineSegment StartX=-199.442 StartY=-28.7048 StartZ=0 EndX=-198.512 EndY=-26.7109 EndZ=0
    g3: LineSegment StartX=-198.512 StartY=-26.7109 StartZ=0 EndX=-200.506 EndY=-25.7811 EndZ=0
    g4: LineSegment StartX=-201.28 StartY=-23.6549 StartZ=0 EndX=-203.562 EndY=-28.5489 EndZ=0
    g5: LineSegment StartX=-203.562 StartY=-28.5489 StartZ=0 EndX=-200.118 EndY=-30.1549 EndZ=0
    g6: LineSegment StartX=-197.992 StartY=-29.381 StartZ=0 EndX=-197.062 EndY=-27.3871 EndZ=0
    g7: LineSegment StartX=-197.836 StartY=-25.2608 StartZ=0 EndX=-201.28 EndY=-23.6549 EndZ=0
    g8: LineSegment [constr] StartX=-198.668 StartY=-30.8311 StartZ=0 EndX=-197.992 EndY=-29.381 EndZ=0
    g9: LineSegment [constr] StartX=-198.668 StartY=-30.8311 StartZ=0 EndX=-200.118 EndY=-30.1549 EndZ=0
    g10: ArcOfCircle CenterX=-198.512 CenterY=-26.7109 CenterZ=0 NormalX=0 NormalY=0 NormalZ=1 AngleXU=0 Radius=1.6 StartAngle=5.84685 EndAngle=7.41765
    g11: GeomPoint [constr] X=-196.386 Y=-25.937 Z=0
    g12: ArcOfCircle CenterX=-199.442 CenterY=-28.7048 CenterZ=0 NormalX=0 NormalY=0 NormalZ=1 AngleXU=0 Radius=1.6 StartAngle=4.27606 EndAngle=5.84685
    g13: GeomPoint [constr] X=-198.668 Y=-30.8311 Z=0
    g14: LineSegment StartX=-207.775 StartY=-46.8316 StartZ=0 EndX=-207.775 EndY=-50.8316 EndZ=0
    g15: LineSegment StartX=-207.775 StartY=-46.8316 StartZ=0 EndX=-203.775 EndY=-46.8316 EndZ=0
    g16: LineSegment StartX=-203.775 StartY=-46.8316 StartZ=0 EndX=-203.775 EndY=-50.8316 EndZ=0
    g17: LineSegment StartX=-207.775 StartY=-50.8316 StartZ=0 EndX=-203.775 EndY=-50.8316 EndZ=0
    g18: LineSegment StartX=-209.375 StartY=-52.4316 StartZ=0 EndX=-203.775 EndY=-52.4316 EndZ=0
    g19: LineSegment StartX=-202.175 StartY=-50.8316 StartZ=0 EndX=-202.175 EndY=-46.8316 EndZ=0
    g20: LineSegment StartX=-203.775 StartY=-45.2316 StartZ=0 EndX=-209.375 EndY=-45.2316 EndZ=0
    g21: LineSegment StartX=-209.375 StartY=-45.2316 StartZ=0 EndX=-209.375 EndY=-52.4316 EndZ=0
    g22: ArcOfCircle CenterX=-203.775 CenterY=-46.8316 CenterZ=0 NormalX=0 NormalY=0 NormalZ=1 AngleXU=0 Radius=1.6 StartAngle=1.8e-15 EndAngle=1.5708
    g23: GeomPoint [constr] X=-202.175 Y=-45.2316 Z=0
    g24: ArcOfCircle CenterX=-203.775 CenterY=-50.8316 CenterZ=0 NormalX=0 NormalY=0 NormalZ=1 AngleXU=0 Radius=1.6 StartAngle=4.71239 EndAngle=6.28319
    g25: GeomPoint [constr] X=-202.175 Y=-52.4316 Z=0
    g26: LineSegment [constr] StartX=-207.775 StartY=-50.4316 StartZ=0 EndX=-207.775 EndY=-50.8316 EndZ=0
  constraints (69):
    c: Coincident(g1,g0)
    c: Coincident(g2,g1)
    c: Coincident(g3,g2)
    c: Coincident(g3,g0)
    c: Parallel(g0,g2)
    c: Perpendicular(g3,g0)
    c: Perpendicular(g1,g0)
    c: Coincident(g5,g4)
    c: Coincident(g7,g4)
    c: Distance(g3) = 2.2
    c: Distance(g2) = 2.2
    c: Parallel(g6,g2)
    c: Parallel(g6,g4)
    c: Perpendicular(g5,g6)
    c: Perpendicular(g7,g6)
    c: Distance(g13,g11) = 5.4
    c: Distance(g5,g13) = 5.4
    c: Coincident(g9,g8)
    c: Distance(g8) = 1.6
    c: Distance(g9) = 1.6
    c: Perpendicular(g9,g8)
    c: Parallel(g8,g6)
    c: Coincident(g8,g13)
    c: Distance(g8,g1) = 1.6
    c: Distance(g9,g1) = 1.6
    c: Tangent(g0,g-5)
    c: Distance(g0,g-6) = 19.2
    c: PointOnObject(g11,g7)
    c: PointOnObject(g11,g6)
    c: Tangent(g7,g10) = -1.5708
    c: Tangent(g6,g10) = -1.5708
    c: PointOnObject(g13,g5)
    c: Tangent(g5,g12) = -1.5708
    c: Tangent(g6,g12) = -1.5708
    c: Equal(g10,g12)
    c: Coincident(g10,g2)
    c: Vertical(g14)
    c: Coincident(g15,g14)
    c: Horizontal(g15)
    c: Coincident(g16,g15)
    c: Vertical(g16)
    c: Coincident(g17,g14)
    c: Coincident(g17,g16)
    c: Horizontal(g17)
    c: Distance(g16) = 4
    c: Distance(g15) = 4
    c: Horizontal(g18)
    c: Vertical(g19)
    c: Horizontal(g20)
    c: Coincident(g21,g20)
    c: Coincident(g21,g18)
    c: Vertical(g21)
    c: Distance(g20,g23) = 7.2
    c: Distance(g25,g23) = 7.2
    c: DistanceY(g18,g14) = 1.6
    c: DistanceX(g18,g14) = 1.6
    c: PointOnObject(g23,g20)
    c: PointOnObject(g23,g19)
    c: Tangent(g20,g22) = -1.5708
    c: Tangent(g19,g22) = -1.5708
    c: PointOnObject(g25,g19)
    c: Tangent(g18,g24) = -1.5708
    c: Tangent(g19,g24) = -1.5708
    c: Equal(g22,g24)
    c: Coincident(g22,g15)
    c: Vertical(g26)
    c: Distance(g26) = 0.4
    c: Coincident(g26,g-4)
    c: Coincident(g14,g26)
FEATURE [Part::Extrusion] Extrude045  label="Extrude fermi per driver solenoide e alimentatore"
  Base = -> Sketch042
  Dir = (0,-1,2e-16)
  DirMode = 2
  FaceMakerClass = Part::FaceMakerBullseye
  FaceMakerMode = 3
  LengthFwd = 25.2
  LengthRev = 0
  Solid = true
  Symmetric = true
FEATURE [Sketcher::SketchObject] Sketch043  label="scavo pulizia fermo alimentatore"
  ArcFitTolerance = 1e-06
  AttachmentSupport = -> [XZ_Plane]
  ExternalGeometry = -> [Sketch042,Sketch036,Sketch037]
  FullyConstrained = true
  MakeInternals = false
  MapMode = 5
  Placement = pos=(0,0,0) rot=(1,0,0;1.5708rad)
  sketch-geometry (6):
    g0: LineSegment StartX=-209.375 StartY=-52.4316 StartZ=0 EndX=-209.375 EndY=-50.4316 EndZ=0
    g1: LineSegment StartX=-209.375 StartY=-50.4316 StartZ=0 EndX=-207.775 EndY=-50.4316 EndZ=0
    g2: LineSegment StartX=-207.775 StartY=-50.4316 StartZ=0 EndX=-207.775 EndY=-45.2316 EndZ=0
    g3: LineSegment StartX=-207.775 StartY=-45.2316 StartZ=0 EndX=-202.175 EndY=-45.2316 EndZ=0
    g4: LineSegment StartX=-202.175 StartY=-45.2316 StartZ=0 EndX=-202.175 EndY=-52.4316 EndZ=0
    g5: LineSegment StartX=-202.175 StartY=-52.4316 StartZ=0 EndX=-209.375 EndY=-52.4316 EndZ=0
  constraints (13):
    c: Vertical(g0)
    c: Coincident(g1,g0)
    c: Coincident(g2,g1)
    c: Coincident(g3,g2)
    c: Coincident(g4,g3)
    c: Coincident(g5,g4)
    c: Coincident(g5,g0)
    c: Horizontal(g5)
    c: Coincident(g0,g-6)
    c: Tangent(g1,g-8)
    c: Tangent(g2,g-4)
    c: Tangent(g3,g-7)
    c: Tangent(g4,g-3)
FEATURE [Part::Extrusion] Extrude046  label="Extrude scavo pulizia fermo alimentatore"
  Base = -> Sketch043
  Dir = (0,-1,2e-16)
  DirMode = 2
  FaceMakerClass = Part::FaceMakerBullseye
  FaceMakerMode = 3
  LengthFwd = 19.5
  LengthRev = 0
  Solid = true
  Symmetric = true
FEATURE [Sketcher::SketchObject] Sketch044  label="buchini per fissaggio oled"
  ArcFitTolerance = 1e-06
  AttachmentSupport = -> [YZ_Plane]
  ExternalGeometry = -> [Sketch]
  FullyConstrained = true
  MakeInternals = false
  MapMode = 5
  Placement = pos=(0,0,0) rot=(0.57735,0.57735,0.57735;2.0944rad)
  sketch-geometry (5):
    g0: LineSegment [constr] StartX=1.5e-14 StartY=67.3588 StartZ=0 EndX=0 EndY=64.3588 EndZ=0
    g1: LineSegment [constr] StartX=0 StartY=64.3588 StartZ=0 EndX=10.4 EndY=64.3588 EndZ=0
    g2: LineSegment [constr] StartX=0 StartY=64.3588 StartZ=0 EndX=-10.4 EndY=64.3588 EndZ=0
    g3: Circle CenterX=10.4 CenterY=64.3588 CenterZ=0 NormalX=0 NormalY=0 NormalZ=1 AngleXU=0 Radius=1.5
    g4: Circle CenterX=-10.4 CenterY=64.3588 CenterZ=0 NormalX=0 NormalY=0 NormalZ=1 AngleXU=0 Radius=1.5
  constraints (13):
    c: Distance(g0) = 3
    c: PointOnObject(g0,g-2)
    c: Coincident(g1,g0)
    c: Horizontal(g1)
    c: Coincident(g2,g0)
    c: Horizontal(g2)
    c: DistanceX(g1,g1) = 10.4
    c: Coincident(g3,g1)
    c: Diameter(g4) = 3
    c: Coincident(g4,g2)
    c: Coincident(g0,g-7)
    c: Equal(g1,g2)
    c: Equal(g4,g3)
FEATURE [Part::Extrusion] Extrude047  label="Extrude buchini per fissaggio oled"
  Base = -> Sketch044
  Dir = (1,0,0)
  DirMode = 2
  FaceMakerClass = Part::FaceMakerBullseye
  FaceMakerMode = 3
  LengthFwd = 10
  LengthRev = 0
  Placement = pos=(-186,0,0) rot=(0,0,1;0rad)
  Solid = true
  Symmetric = false
FEATURE [Sketcher::SketchObject] Sketch046  label="scavo 5x5 neopixel"
  ArcFitTolerance = 1e-06
  AttachmentSupport = -> [YZ_Plane002]
  FullyConstrained = true
  MakeInternals = false
  MapMode = 5
  Placement = pos=(0,0,0) rot=(0.57735,0.57735,0.57735;2.0944rad)
  sketch-geometry (4):
    g0: LineSegment StartX=-2.7 StartY=2.7 StartZ=0 EndX=2.7 EndY=2.7 EndZ=0
    g1: LineSegment StartX=2.7 StartY=2.7 StartZ=0 EndX=2.7 EndY=-2.7 EndZ=0
    g2: LineSegment StartX=2.7 StartY=-2.7 StartZ=0 EndX=-2.7 EndY=-2.7 EndZ=0
    g3: LineSegment StartX=-2.7 StartY=-2.7 StartZ=0 EndX=-2.7 EndY=2.7 EndZ=0
  constraints (11):
    c: Horizontal(g0)
    c: Coincident(g1,g0)
    c: Vertical(g1)
    c: Coincident(g2,g1)
    c: Horizontal(g2)
    c: Coincident(g3,g2)
    c: Coincident(g3,g0)
    c: Vertical(g3)
    c: DistanceX(g0,g0) = 5.4
    c: DistanceY(g1,g1) = 5.4
    c: Symmetric(g0,g1,g-1)
FEATURE [Sketcher::SketchObject] Sketch047  label="scavo 10x10 neopixel corpo"
  ArcFitTolerance = 1e-06
  AttachmentOffset = pos=(0,0,1) rot=(0,0,1;0rad)
  AttachmentSupport = -> [YZ_Plane002]
  FullyConstrained = true
  MakeInternals = false
  MapMode = 5
  Placement = pos=(1,0,0) rot=(0.57735,0.57735,0.57735;2.0944rad)
  sketch-geometry (4):
    g0: LineSegment StartX=-5 StartY=5.1 StartZ=0 EndX=5 EndY=5.1 EndZ=0
    g1: LineSegment StartX=5 StartY=5.1 StartZ=0 EndX=5 EndY=-5.1 EndZ=0
    g2: LineSegment StartX=5 StartY=-5.1 StartZ=0 EndX=-5 EndY=-5.1 EndZ=0
    g3: LineSegment StartX=-5 StartY=-5.1 StartZ=0 EndX=-5 EndY=5.1 EndZ=0
  constraints (11):
    c: Horizontal(g0)
    c: Coincident(g1,g0)
    c: Vertical(g1)
    c: Coincident(g2,g1)
    c: Horizontal(g2)
    c: Coincident(g3,g2)
    c: Coincident(g3,g0)
    c: Vertical(g3)
    c: DistanceX(g0,g0) = 10
    c: DistanceY(g1,g1) = 10.2
    c: Symmetric(g0,g2,g-1)
FEATURE [Sketcher::SketchObject] Sketch048  label="buco per perno blocco neopixel"
  ArcFitTolerance = 1e-06
  AttachmentSupport = -> [XZ_Plane002]
  FullyConstrained = true
  MakeInternals = false
  MapMode = 5
  Placement = pos=(0,0,0) rot=(1,0,0;1.5708rad)
  sketch-geometry (4):
    g0: LineSegment StartX=3 StartY=1.2 StartZ=0 EndX=3 EndY=-1.2 EndZ=0
    g1: LineSegment StartX=3 StartY=-1.2 StartZ=0 EndX=5.4 EndY=-1.2 EndZ=0
    g2: LineSegment StartX=5.4 StartY=-1.2 StartZ=0 EndX=5.4 EndY=1.2 EndZ=0
    g3: LineSegment StartX=5.4 StartY=1.2 StartZ=0 EndX=3 EndY=1.2 EndZ=0
  constraints (11):
    c: Coincident(g1,g0)
    c: Horizontal(g1)
    c: Coincident(g2,g1)
    c: Vertical(g2)
    c: Coincident(g3,g2)
    c: Coincident(g3,g0)
    c: Horizontal(g3)
    c: DistanceX(g1,g1) = 2.4
    c: DistanceY(g2,g2) = 2.4
    c: Symmetric(g0,g0,g-1)
    c: DistanceX(g-1,g0) = 3
FEATURE [Sketcher::SketchObject] Sketch045  label="blocco principale per neopixel"
  ArcFitTolerance = 1e-06
  AttachmentSupport = -> [XZ_Plane002]
  ExternalGeometry = -> [Sketch048]
  FullyConstrained = true
  MakeInternals = false
  MapMode = 5
  Placement = pos=(0,0,0) rot=(1,0,0;1.5708rad)
  sketch-geometry (6):
    g0: LineSegment StartX=0 StartY=5.1 StartZ=0 EndX=0 EndY=-5.1 EndZ=0
    g1: LineSegment StartX=0 StartY=-5.1 StartZ=0 EndX=3 EndY=-5.1 EndZ=0
    g2: LineSegment StartX=7 StartY=-1.1 StartZ=0 EndX=7 EndY=5.1 EndZ=0
    g3: LineSegment StartX=7 StartY=5.1 StartZ=0 EndX=0 EndY=5.1 EndZ=0
    g4: ArcOfCircle CenterX=3 CenterY=-1.1 CenterZ=0 NormalX=0 NormalY=0 NormalZ=1 AngleXU=0 Radius=4 StartAngle=4.71239 EndAngle=6.28319
    g5: GeomPoint [constr] X=7 Y=-5.1 Z=0
  constraints (15):
    c: Vertical(g0)
    c: Coincident(g1,g0)
    c: Horizontal(g1)
    c: Vertical(g2)
    c: Coincident(g3,g2)
    c: Coincident(g3,g0)
    c: Horizontal(g3)
    c: DistanceY(g0,g0) = 10.2
    c: Symmetric(g0,g0,g-1)
    c: DistanceX(g3,g3) = 7
    c: PointOnObject(g5,g2)
    c: PointOnObject(g5,g1)
    c: Tangent(g2,g4) = -1.5708
    c: Tangent(g1,g4) = -1.5708
    c: DistanceX(g-3,g1) = 0
FEATURE [Sketcher::SketchObject] Sketch049  label="rinforzi esterni per corpo neopoixel"
  ArcFitTolerance = 1e-06
  AttachmentSupport = -> [XZ_Plane002]
  ExternalGeometry = -> [Sketch045]
  FullyConstrained = true
  MakeInternals = false
  MapMode = 5
  Placement = pos=(0,0,0) rot=(1,0,0;1.5708rad)
  sketch-geometry (8):
    g0: LineSegment StartX=1 StartY=-4.1 StartZ=0 EndX=2 EndY=-4.1 EndZ=0
    g1: LineSegment StartX=2 StartY=-4.1 StartZ=0 EndX=2 EndY=-5.1 EndZ=0
    g2: LineSegment StartX=2 StartY=-5.1 StartZ=0 EndX=1 EndY=-5.1 EndZ=0
    g3: LineSegment StartX=1 StartY=-5.1 StartZ=0 EndX=1 EndY=-4.1 EndZ=0
    g4: LineSegment StartX=1 StartY=5.1 StartZ=0 EndX=2 EndY=5.1 EndZ=0
    g5: LineSegment StartX=2 StartY=5.1 StartZ=0 EndX=2 EndY=4.1 EndZ=0
    g6: LineSegment StartX=2 StartY=4.1 StartZ=0 EndX=1 EndY=4.1 EndZ=0
    g7: LineSegment StartX=1 StartY=4.1 StartZ=0 EndX=1 EndY=5.1 EndZ=0
  constraints (24):
    c: Horizontal(g0)
    c: Coincident(g1,g0)
    c: Vertical(g1)
    c: Coincident(g2,g1)
    c: Horizontal(g2)
    c: Coincident(g3,g2)
    c: Coincident(g3,g0)
    c: Vertical(g3)
    c: Horizontal(g4)
    c: Coincident(g5,g4)
    c: Vertical(g5)
    c: Coincident(g6,g5)
    c: Horizontal(g6)
    c: Coincident(g7,g6)
    c: Coincident(g7,g4)
    c: Vertical(g7)
    c: DistanceX(g4,g4) = 1
    c: DistanceY(g5,g5) = 1
    c: DistanceX(g0,g0) = 1
    c: DistanceY(g1,g1) = 1
    c: DistanceX(g-3,g4) = 1
    c: DistanceY(g-3,g4) = 0
    c: DistanceX(g-4,g2) = 1
    c: DistanceY(g2,g-4) = 0
FEATURE [Sketcher::SketchObject] Sketch052  label="scavo saldature driver solenoide"
  ArcFitTolerance = 1e-06
  AttachmentSupport = -> [XZ_Plane]
  ExternalGeometry = -> [Sketch038]
  FullyConstrained = true
  MakeInternals = false
  MapMode = 5
  Placement = pos=(0,0,0) rot=(1,0,0;1.5708rad)
  sketch-geometry (4):
    g0: LineSegment StartX=-195.304 StartY=-6.5806 StartZ=0 EndX=-196.994 EndY=-10.2058 EndZ=0
    g1: LineSegment StartX=-196.994 StartY=-10.2058 StartZ=0 EndX=-196.632 EndY=-10.3749 EndZ=0
    g2: LineSegment StartX=-196.632 StartY=-10.3749 StartZ=0 EndX=-194.941 EndY=-6.74965 EndZ=0
    g3: LineSegment StartX=-194.941 StartY=-6.74965 StartZ=0 EndX=-195.304 EndY=-6.5806 EndZ=0
  constraints (11):
    c: Coincident(g1,g0)
    c: Coincident(g2,g1)
    c: Coincident(g3,g2)
    c: Coincident(g3,g0)
    c: Parallel(g2,g0)
    c: Perpendicular(g2,g3)
    c: Perpendicular(g1,g2,g1) = 1.5708
    c: Parallel(g2,g-3)
    c: Distance(g2) = 4
    c: Distance(g3) = 0.4
    c: Coincident(g2,g-3)
FEATURE [Part::Extrusion] Extrude055  label="Extrude scavo saldature driver solenoide"
  Base = -> Sketch052
  Dir = (0,-1,2e-16)
  DirMode = 2
  FaceMakerClass = Part::FaceMakerBullseye
  FaceMakerMode = 3
  LengthFwd = 6
  LengthRev = 0
  Solid = true
  Symmetric = true
FEATURE [Sketcher::SketchObject] Sketch053  label="scavo saldature rumble"
  ArcFitTolerance = 1e-06
  AttachmentSupport = -> [XZ_Plane]
  ExternalGeometry = -> [Sketch019]
  FullyConstrained = true
  MakeInternals = false
  MapMode = 5
  Placement = pos=(0,0,0) rot=(1,0,0;1.5708rad)
  sketch-geometry (4):
    g0: LineSegment StartX=-164.507 StartY=-41.6446 StartZ=0 EndX=-165.743 EndY=-45.4488 EndZ=0
    g1: LineSegment StartX=-165.743 StartY=-45.4488 StartZ=0 EndX=-164.602 EndY=-45.8196 EndZ=0
    g2: LineSegment StartX=-164.602 StartY=-45.8196 StartZ=0 EndX=-163.366 EndY=-42.0154 EndZ=0
    g3: LineSegment StartX=-163.366 StartY=-42.0154 StartZ=0 EndX=-164.507 EndY=-41.6446 EndZ=0
  constraints (11):
    c: Coincident(g1,g0)
    c: Coincident(g2,g1)
    c: Coincident(g3,g2)
    c: Coincident(g3,g0)
    c: Parallel(g0,g2)
    c: Perpendicular(g3,g0)
    c: Perpendicular(g1,g0)
    c: Parallel(g0,g-3)
    c: Distance(g0) = 4
    c: Distance(g1) = 1.2
    c: Coincident(g0,g-3)
FEATURE [Part::Extrusion] Extrude056  label="Extrude scavo saldature rumble"
  Base = -> Sketch053
  Dir = (0,-1,2e-16)
  DirMode = 2
  FaceMakerClass = Part::FaceMakerBullseye
  FaceMakerMode = 3
  LengthFwd = 8.4
  LengthRev = 0
  Solid = true
  Symmetric = true
FEATURE [Sketcher::SketchObject] Sketch054  label="scavo saldature alimentatore connettore USB"
  ArcFitTolerance = 1e-06
  AttachmentSupport = -> [XZ_Plane]
  ExternalGeometry = -> [Sketch037]
  FullyConstrained = true
  MakeInternals = false
  MapMode = 5
  Placement = pos=(0,0,0) rot=(1,0,0;1.5708rad)
  sketch-geometry (4):
    g0: LineSegment StartX=-209.575 StartY=-80.4316 StartZ=0 EndX=-210.375 EndY=-80.4316 EndZ=0
    g1: LineSegment StartX=-210.375 StartY=-80.4316 StartZ=0 EndX=-210.375 EndY=-72.4316 EndZ=0
    g2: LineSegment StartX=-210.375 StartY=-72.4316 StartZ=0 EndX=-209.575 EndY=-72.4316 EndZ=0
    g3: LineSegment StartX=-209.575 StartY=-72.4316 StartZ=0 EndX=-209.575 EndY=-80.4316 EndZ=0
  constraints (11):
    c: Horizontal(g0)
    c: Coincident(g1,g0)
    c: Vertical(g1)
    c: Coincident(g2,g1)
    c: Horizontal(g2)
    c: Coincident(g3,g2)
    c: Coincident(g3,g0)
    c: Vertical(g3)
    c: DistanceX(g0,g0) = 0.8
    c: DistanceY(g3,g3) = 8
    c: Coincident(g0,g-4)
FEATURE [Part::Extrusion] Extrude057  label="Extrude scavo saldature alimentatore connettore USB"
  Base = -> Sketch054
  Dir = (0,-1,2e-16)
  DirMode = 2
  FaceMakerClass = Part::FaceMakerBullseye
  FaceMakerMode = 3
  LengthFwd = 11
  LengthRev = 0
  Solid = true
  Symmetric = true
FEATURE [Sketcher::SketchObject] Sketch055  label="buco interno per micro switch"
  ArcFitTolerance = 1e-06
  AttachmentSupport = -> [XZ_Plane]
  ExternalGeometry = -> [Sketch]
  FullyConstrained = true
  MakeInternals = false
  MapMode = 5
  Placement = pos=(0,0,0) rot=(1,0,0;1.5708rad)
  sketch-geometry (11):
    g0: LineSegment [constr] StartX=-194.483 StartY=34.2854 StartZ=0 EndX=-196.022 EndY=30.0568 EndZ=0
    g1: LineSegment [constr] StartX=-196.022 StartY=30.0568 StartZ=0 EndX=-197.561 EndY=25.8282 EndZ=0
    g2: LineSegment [constr] StartX=-196.022 StartY=30.0568 StartZ=0 EndX=-194.143 EndY=29.3727 EndZ=0
    g3: LineSegment [constr] StartX=-196.022 StartY=30.0568 StartZ=0 EndX=-197.902 EndY=30.7408 EndZ=0
    g4: LineSegment StartX=-196.362 StartY=34.9694 StartZ=0 EndX=-192.604 EndY=33.6014 EndZ=0
    g5: LineSegment StartX=-199.441 StartY=26.5122 StartZ=0 EndX=-195.682 EndY=25.1441 EndZ=0
    g6: LineSegment StartX=-192.604 StartY=33.6014 StartZ=0 EndX=-195.682 EndY=25.1441 EndZ=0
    g7: LineSegment StartX=-196.362 StartY=34.9694 StartZ=0 EndX=-199.441 EndY=26.5122 EndZ=0
    g8: GeomPoint [constr] X=-187.821 Y=29.2 Z=0
    g9: LineSegment [constr] StartX=-188.505 StartY=27.3206 StartZ=0 EndX=-196.022 EndY=30.0568 EndZ=0
    g10: LineSegment [constr] StartX=-187.821 StartY=29.2 StartZ=0 EndX=-188.505 EndY=27.3206 EndZ=0
  constraints (27):
    c: Coincident(g2,g0)
    c: Parallel(g0,g-3)
    c: Tangent(g1,g0) = -1.5708
    c: Perpendicular(g0,g2)
    c: Tangent(g2,g3)
    c: Distance(g0,g1) = 9
    c: Equal(g0,g1)
    c: Distance(g3,g2) = 4
    c: Equal(g2,g3)
    c: Parallel(g3,g4)
    c: Symmetric(g4,g4,g0)
    c: Parallel(g6,g1)
    c: Parallel(g7,g1)
    c: Symmetric(g6,g6,g2)
    c: Symmetric(g5,g5,g1)
    c: Symmetric(g7,g7,g3)
    c: Coincident(g7,g4)
    c: Coincident(g6,g4)
    c: Coincident(g5,g6)
    c: Symmetric(g-3,g-3,g8)
    c: Perpendicular(g-3,g9)
    c: Distance(g9) = 8
    c: Coincident(g3,g9)
    c: Coincident(g10,g8)
    c: Parallel(g10,g-3)
    c: Distance(g10) = 2
    c: Coincident(g10,g9)
FEATURE [Sketcher::SketchObject] Sketch056  label="buco esterno per micro switch"
  ArcFitTolerance = 1e-06
  AttachmentSupport = -> [XZ_Plane]
  ExternalGeometry = -> [Sketch055]
  FullyConstrained = true
  MakeInternals = false
  MapMode = 5
  Placement = pos=(0,0,0) rot=(1,0,0;1.5708rad)
  sketch-geometry (17):
    g0: GeomPoint [constr] X=-194.143 Y=29.3727 Z=0
    g1: GeomPoint [constr] X=-194.483 Y=34.2854 Z=0
    g2: GeomPoint [constr] X=-197.902 Y=30.7408 Z=0
    g3: GeomPoint [constr] X=-197.561 Y=25.8282 Z=0
    g4: GeomPoint [constr] X=-196.022 Y=30.0568 Z=0
    g5: LineSegment [constr] StartX=-194.483 StartY=34.2854 StartZ=0 EndX=-196.022 EndY=30.0568 EndZ=0
    g6: LineSegment [constr] StartX=-196.022 StartY=30.0568 StartZ=0 EndX=-197.561 EndY=25.8282 EndZ=0
    g7: LineSegment [constr] StartX=-197.902 StartY=30.7408 StartZ=0 EndX=-196.022 EndY=30.0568 EndZ=0
    g8: LineSegment [constr] StartX=-196.022 StartY=30.0568 StartZ=0 EndX=-194.143 EndY=29.3727 EndZ=0
    g9: LineSegment [constr] StartX=-195.338 StartY=31.9362 StartZ=0 EndX=-196.022 EndY=30.0568 EndZ=0
    g10: LineSegment [constr] StartX=-196.022 StartY=30.0568 StartZ=0 EndX=-196.706 EndY=28.1774 EndZ=0
    g11: LineSegment [constr] StartX=-196.022 StartY=30.0568 StartZ=0 EndX=-196.821 EndY=30.3475 EndZ=0
    g12: LineSegment [constr] StartX=-196.022 StartY=30.0568 StartZ=0 EndX=-195.223 EndY=29.7661 EndZ=0
    g13: LineSegment StartX=-194.539 StartY=31.6454 StartZ=0 EndX=-195.907 EndY=27.8867 EndZ=0
    g14: LineSegment StartX=-196.137 StartY=32.2269 StartZ=0 EndX=-197.505 EndY=28.4681 EndZ=0
    g15: LineSegment StartX=-196.137 StartY=32.2269 StartZ=0 EndX=-194.539 EndY=31.6454 EndZ=0
    g16: LineSegment StartX=-197.505 StartY=28.4681 StartZ=0 EndX=-195.907 EndY=27.8867 EndZ=0
  constraints (34):
    c: Symmetric(g-5,g-5,g1)
    c: Symmetric(g-5,g-6,g0)
    c: Symmetric(g-6,g-6,g3)
    c: Symmetric(g-5,g-6,g2)
    c: Coincident(g5,g1)
    c: Coincident(g5,g4)
    c: Coincident(g6,g4)
    c: Coincident(g6,g3)
    c: Equal(g5,g6)
    c: Coincident(g7,g2)
    c: Coincident(g7,g4)
    c: Coincident(g8,g4)
    c: Coincident(g8,g0)
    c: Equal(g7,g8)
    c: Coincident(g11,g9)
    c: Coincident(g12,g9)
    c: Tangent(g10,g9) = -1.5708
    c: Perpendicular(g11,g9)
    c: Parallel(g9,g-4)
    c: Equal(g9,g10)
    c: Parallel(g12,g11)
    c: Equal(g11,g12)
    c: Distance(g11,g12) = 1.7
    c: Distance(g9,g10) = 4
    c: Symmetric(g13,g13,g12)
    c: Parallel(g13,g9)
    c: Symmetric(g14,g14,g11)
    c: Symmetric(g15,g15,g9)
    c: Parallel(g15,g11)
    c: Symmetric(g16,g16,g10)
    c: Coincident(g16,g14)
    c: Coincident(g15,g14)
    c: Coincident(g13,g15)
    c: Coincident(g9,g4)
FEATURE [Sketcher::SketchObject] Sketch057  label="buco interno per SWITCH"
  ArcFitTolerance = 1e-06
  AttachmentSupport = -> [XZ_Plane]
  ExternalGeometry = -> [Sketch]
  FullyConstrained = true
  MakeInternals = false
  MapMode = 5
  Placement = pos=(0,0,0) rot=(1,0,0;1.5708rad)
  sketch-geometry (10):
    g0: GeomPoint [constr] X=-187.821 Y=29.2 Z=0
    g1: LineSegment [constr] StartX=-188.505 StartY=27.3206 StartZ=0 EndX=-193.203 EndY=29.0307 EndZ=0
    g2: LineSegment [constr] StartX=-190.809 StartY=35.6086 StartZ=0 EndX=-195.597 EndY=22.4529 EndZ=0
    g3: GeomPoint [constr] X=-193.203 Y=29.0307 Z=0
    g4: LineSegment [constr] StartX=-196.492 StartY=30.2278 StartZ=0 EndX=-189.914 EndY=27.8336 EndZ=0
    g5: LineSegment StartX=-194.098 StartY=36.8056 StartZ=0 EndX=-187.52 EndY=34.4115 EndZ=0
    g6: LineSegment StartX=-194.098 StartY=36.8056 StartZ=0 EndX=-198.886 EndY=23.6499 EndZ=0
    g7: LineSegment StartX=-187.52 StartY=34.4115 StartZ=0 EndX=-192.308 EndY=21.2558 EndZ=0
    g8: LineSegment StartX=-198.886 StartY=23.6499 StartZ=0 EndX=-192.308 EndY=21.2558 EndZ=0
    g9: LineSegment [constr] StartX=-187.821 StartY=29.2 StartZ=0 EndX=-188.505 EndY=27.3206 EndZ=0
  constraints (23):
    c: Symmetric(g-3,g-3,g0)
    c: Perpendicular(g1,g-3)
    c: Parallel(g2,g-3)
    c: Symmetric(g2,g2,g3)
    c: Perpendicular(g2,g4)
    c: Symmetric(g4,g4,g3)
    c: Distance(g2) = 14
    c: Distance(g4) = 7
    c: Distance(g1) = 5
    c: Parallel(g5,g4)
    c: Parallel(g7,g2)
    c: Symmetric(g5,g5,g2)
    c: Symmetric(g6,g6,g4)
    c: Symmetric(g7,g7,g4)
    c: Symmetric(g8,g8,g2)
    c: Coincident(g6,g5)
    c: Coincident(g7,g5)
    c: Coincident(g8,g7)
    c: Coincident(g3,g1)
    c: Coincident(g9,g0)
    c: Parallel(g9,g-3)
    c: Distance(g9) = 2
    c: Coincident(g1,g9)
FEATURE [Sketcher::SketchObject] Sketch058  label="buco esterno per SWITCH"
  ArcFitTolerance = 1e-06
  AttachmentSupport = -> [XZ_Plane]
  ExternalGeometry = -> [Sketch057]
  FullyConstrained = true
  MakeInternals = false
  MapMode = 5
  Placement = pos=(0,0,0) rot=(1,0,0;1.5708rad)
  sketch-geometry (12):
    g0: GeomPoint [constr] X=-190.809 Y=35.6086 Z=0
    g1: GeomPoint [constr] X=-196.492 Y=30.2278 Z=0
    g2: GeomPoint [constr] X=-189.914 Y=27.8336 Z=0
    g3: GeomPoint [constr] X=-195.597 Y=22.4529 Z=0
    g4: GeomPoint [constr] X=-193.203 Y=29.0307 Z=0
    g5: LineSegment [constr] StartX=-192.006 StartY=32.3196 StartZ=0 EndX=-194.4 EndY=25.7418 EndZ=0
    g6: GeomPoint [constr] X=-193.203 Y=29.0307 Z=0
    g7: LineSegment [constr] StartX=-195.082 StartY=29.7148 StartZ=0 EndX=-191.324 EndY=28.3467 EndZ=0
    g8: LineSegment StartX=-193.885 StartY=33.0037 StartZ=0 EndX=-190.127 EndY=31.6356 EndZ=0
    g9: LineSegment StartX=-190.127 StartY=31.6356 StartZ=0 EndX=-192.521 EndY=25.0578 EndZ=0
    g10: LineSegment StartX=-196.28 StartY=26.4258 StartZ=0 EndX=-192.521 EndY=25.0578 EndZ=0
    g11: LineSegment StartX=-193.885 StartY=33.0037 StartZ=0 EndX=-196.28 EndY=26.4258 EndZ=0
  constraints (21):
    c: Symmetric(g-6,g-6,g3)
    c: Symmetric(g-4,g-6,g2)
    c: Symmetric(g-5,g-4,g0)
    c: Symmetric(g-5,g-6,g1)
    c: Symmetric(g1,g2,g4)
    c: Parallel(g5,g-4)
    c: Symmetric(g5,g5,g6)
    c: Perpendicular(g7,g5)
    c: Symmetric(g7,g7,g6)
    c: Distance(g5) = 7
    c: Distance(g7) = 4
    c: Parallel(g8,g7)
    c: Parallel(g11,g5)
    c: Symmetric(g8,g8,g5)
    c: Symmetric(g9,g9,g7)
    c: Symmetric(g10,g10,g5)
    c: Symmetric(g11,g11,g7)
    c: Coincident(g11,g8)
    c: Coincident(g9,g8)
    c: Coincident(g9,g10)
    c: Coincident(g6,g4)
FEATURE [Part::Extrusion] Extrude060  label="Extrude buco interno per SWITCH destro"
  Base = -> Sketch057
  Dir = (0,-1,2e-16)
  DirMode = 2
  FaceMakerClass = Part::FaceMakerBullseye
  FaceMakerMode = 3
  LengthFwd = 13.2
  LengthRev = 0
  Placement = pos=(0,2.6,0) rot=(0,0,1;0rad)
  Solid = true
  Symmetric = false
FEATURE [Part::Extrusion] Extrude061  label="Extrude buco esterno per SWITCH destro"
  Base = -> Sketch058
  Dir = (0,-1,2e-16)
  DirMode = 2
  FaceMakerClass = Part::FaceMakerBullseye
  FaceMakerMode = 3
  LengthFwd = 2
  LengthRev = 0
  Placement = pos=(0,-10.6,0) rot=(0,0,1;0rad)
  Solid = true
  Symmetric = false
FEATURE [Sketcher::SketchObject] Sketch059  label="buco per spazio introduzione SWITCH"
  ArcFitTolerance = 1e-06
  AttachmentSupport = -> [XZ_Plane]
  ExternalGeometry = -> [Sketch057,Sketch010]
  FullyConstrained = true
  MakeInternals = false
  MapMode = 5
  Placement = pos=(0,0,0) rot=(1,0,0;1.5708rad)
  sketch-geometry (8):
    g0: LineSegment [constr] StartX=-201.368 StartY=36.3521 StartZ=0 EndX=-195.094 EndY=34.0687 EndZ=0
    g1: LineSegment [constr] StartX=-194.098 StartY=36.8056 StartZ=0 EndX=-195.094 EndY=34.0687 EndZ=0
    g2: LineSegment StartX=-198.658 StartY=24.2771 StartZ=0 EndX=-199.654 EndY=21.5401 EndZ=0
    g3: LineSegment StartX=-199.654 StartY=21.5401 StartZ=0 EndX=-181.196 EndY=14.822 EndZ=0
    g4: LineSegment StartX=-181.196 StartY=14.822 StartZ=0 EndX=-180.2 EndY=17.559 EndZ=0
    g5: LineSegment StartX=-180.2 StartY=17.559 StartZ=0 EndX=-198.658 EndY=24.2771 EndZ=0
    g6: LineSegment [constr] StartX=-204.932 StartY=26.5605 StartZ=0 EndX=-198.658 EndY=24.2771 EndZ=0
    g7: LineSegment [constr] StartX=-198.658 StartY=24.2771 StartZ=0 EndX=-199.654 EndY=21.5401 EndZ=0
  constraints (20):
    c: Parallel(g1,g-3)
    c: Parallel(g0,g-4)
    c: Coincident(g0,g-4)
    c: Coincident(g1,g-3)
    c: Coincident(g0,g1)
    c: Coincident(g3,g2)
    c: Coincident(g4,g3)
    c: Coincident(g5,g4)
    c: Coincident(g5,g2)
    c: Parallel(g5,g-5)
    c: Parallel(g3,g-5)
    c: Parallel(g4,g-6)
    c: DistanceX(g-6,g4) = 0
    c: Coincident(g6,g-5)
    c: Equal(g6,g0)
    c: Coincident(g7,g6)
    c: Equal(g7,g1)
    c: Tangent(g7,g-3)
    c: Coincident(g2,g6)
    c: Coincident(g2,g7)
FEATURE [Part::Extrusion] Extrude062  label="Extrude buco per spazio introduzione SWITCH"
  Base = -> Sketch059
  Dir = (0,-1,2e-16)
  DirMode = 2
  FaceMakerClass = Part::FaceMakerBullseye
  FaceMakerMode = 3
  LengthFwd = 13.2
  LengthRev = 0
  Solid = true
  Symmetric = true
FEATURE [Part::Extrusion] Extrude063  label="Extrude buco interno per SWITCH sinistro"
  Base = -> Sketch057
  Dir = (0,-1,2e-16)
  DirMode = 2
  FaceMakerClass = Part::FaceMakerBullseye
  FaceMakerMode = 3
  LengthFwd = 13.2
  LengthRev = 0
  Placement = pos=(0,10.6,0) rot=(0,0,1;0rad)
  Solid = true
  Symmetric = false
FEATURE [Part::Extrusion] Extrude064  label="Extrude buco esterno per SWITCH sinistro"
  Base = -> Sketch058
  Dir = (0,-1,2e-16)
  DirMode = 2
  FaceMakerClass = Part::FaceMakerBullseye
  FaceMakerMode = 3
  LengthFwd = 2
  LengthRev = 0
  Placement = pos=(0,12.6,0) rot=(0,0,1;0rad)
  Solid = true
  Symmetric = false
FEATURE [Sketcher::SketchObject] Sketch061  label="struttura esterna blocco switch"
  ArcFitTolerance = 1e-06
  AttachmentSupport = -> [XZ_Plane003]
  FullyConstrained = true
  MakeInternals = false
  MapMode = 5
  Placement = pos=(0,0,0) rot=(1,0,0;1.5708rad)
  sketch-geometry (5):
    g0: LineSegment StartX=-1 StartY=-5.1 StartZ=0 EndX=1 EndY=-5.1 EndZ=0
    g1: LineSegment StartX=1 StartY=-5.1 StartZ=0 EndX=1 EndY=5.1 EndZ=0
    g2: LineSegment StartX=1 StartY=5.1 StartZ=0 EndX=-1 EndY=5.1 EndZ=0
    g3: LineSegment StartX=-1 StartY=5.1 StartZ=0 EndX=-1 EndY=-5.1 EndZ=0
    g4: GeomPoint [constr] X=0 Y=0 Z=0
  constraints (12):
    c: Coincident(g0,g1)
    c: Coincident(g1,g2)
    c: Coincident(g2,g3)
    c: Coincident(g3,g0)
    c: Horizontal(g0)
    c: Horizontal(g2)
    c: Vertical(g1)
    c: Vertical(g3)
    c: Symmetric(g2,g0,g4)
    c: Distance(g1,g3) = 2
    c: Distance(g0,g2) = 10.2
    c: Coincident(g4,g-1)
FEATURE [Sketcher::SketchObject] Sketch062  label="struttura interna blocco switch"
  ArcFitTolerance = 1e-06
  AttachmentSupport = -> [XZ_Plane003]
  ExternalGeometry = -> [Sketch061]
  FullyConstrained = true
  MakeInternals = false
  MapMode = 5
  Placement = pos=(0,0,0) rot=(1,0,0;1.5708rad)
  sketch-geometry (5):
    g0: LineSegment StartX=-1 StartY=3.1 StartZ=0 EndX=-1 EndY=-3.1 EndZ=0
    g1: LineSegment StartX=-1 StartY=-3.1 StartZ=0 EndX=1 EndY=-3.1 EndZ=0
    g2: LineSegment StartX=1 StartY=-3.1 StartZ=0 EndX=1 EndY=3.1 EndZ=0
    g3: LineSegment StartX=1 StartY=3.1 StartZ=0 EndX=-1 EndY=3.1 EndZ=0
    g4: GeomPoint [constr] X=0 Y=0 Z=0
  constraints (12):
    c: Coincident(g0,g1)
    c: Coincident(g1,g2)
    c: Coincident(g2,g3)
    c: Coincident(g3,g0)
    c: Vertical(g0)
    c: Vertical(g2)
    c: Horizontal(g1)
    c: Horizontal(g3)
    c: Symmetric(g2,g0,g4)
    c: Coincident(g4,g-1)
    c: Distance(g0) = 6.2
    c: Equal(g3,g-3)
FEATURE [Sketcher::SketchObject] Sketch063  label="blocchi tra switch"
  ArcFitTolerance = 1e-06
  AttachmentSupport = -> [XZ_Plane003]
  ExternalGeometry = -> [Sketch061,Sketch062]
  FullyConstrained = true
  MakeInternals = false
  MapMode = 5
  Placement = pos=(0,0,0) rot=(1,0,0;1.5708rad)
  sketch-geometry (8):
    g0: LineSegment StartX=-3 StartY=5.1 StartZ=0 EndX=-1 EndY=5.1 EndZ=0
    g1: LineSegment StartX=-1 StartY=5.1 StartZ=0 EndX=-1 EndY=3.1 EndZ=0
    g2: LineSegment StartX=-1 StartY=3.1 StartZ=0 EndX=-3 EndY=3.1 EndZ=0
    g3: LineSegment StartX=-3 StartY=3.1 StartZ=0 EndX=-3 EndY=5.1 EndZ=0
    g4: LineSegment StartX=-3 StartY=-3.1 StartZ=0 EndX=-1 EndY=-3.1 EndZ=0
    g5: LineSegment StartX=-1 StartY=-3.1 StartZ=0 EndX=-1 EndY=-5.1 EndZ=0
    g6: LineSegment StartX=-1 StartY=-5.1 StartZ=0 EndX=-3 EndY=-5.1 EndZ=0
    g7: LineSegment StartX=-3 StartY=-5.1 StartZ=0 EndX=-3 EndY=-3.1 EndZ=0
  constraints (20):
    c: Horizontal(g0)
    c: Coincident(g1,g0)
    c: Coincident(g2,g1)
    c: Horizontal(g2)
    c: Coincident(g3,g2)
    c: Coincident(g3,g0)
    c: Vertical(g3)
    c: Horizontal(g4)
    c: Coincident(g5,g4)
    c: Coincident(g6,g5)
    c: Horizontal(g6)
    c: Coincident(g7,g6)
    c: Coincident(g7,g4)
    c: Vertical(g7)
    c: Coincident(g0,g-4)
    c: Coincident(g1,g-5)
    c: Coincident(g4,g-6)
    c: Coincident(g5,g-7)
    c: Distance(g0) = 2
    c: Distance(g4) = 2
FEATURE [Sketcher::SketchObject] Sketch066  label="piano per rampino"
  ArcFitTolerance = 1e-06
  AttachmentSupport = -> [XZ_Plane002]
  ExternalGeometry = -> [Sketch045]
  FullyConstrained = true
  MakeInternals = false
  MapMode = 5
  Placement = pos=(0,0,0) rot=(1,0,0;1.5708rad)
  sketch-geometry (4):
    g0: LineSegment StartX=5.4 StartY=5.1 StartZ=0 EndX=5.4 EndY=3.9 EndZ=0
    g1: LineSegment StartX=5.4 StartY=3.9 StartZ=0 EndX=7 EndY=3.9 EndZ=0
    g2: LineSegment StartX=7 StartY=3.9 StartZ=0 EndX=7 EndY=5.1 EndZ=0
    g3: LineSegment StartX=7 StartY=5.1 StartZ=0 EndX=5.4 EndY=5.1 EndZ=0
  constraints (11):
    c: Coincident(g0,g1)
    c: Coincident(g1,g2)
    c: Coincident(g2,g3)
    c: Coincident(g3,g0)
    c: Vertical(g0)
    c: Vertical(g2)
    c: Horizontal(g1)
    c: Horizontal(g3)
    c: Distance(g0,g2) = 1.6
    c: Distance(g1,g3) = 1.2
    c: Coincident(g2,g-3)
FEATURE [Sketcher::SketchObject] Sketch064  label="rampini_per_serraggio_struttura"
  ArcFitTolerance = 1e-06
  AttachmentSupport = -> [XZ_Plane002]
  ExternalGeometry = -> [Sketch066,Sketch045]
  FullyConstrained = true
  MakeInternals = false
  MapMode = 5
  Placement = pos=(0,0,0) rot=(1,0,0;1.5708rad)
  sketch-geometry (7):
    g0: LineSegment StartX=7 StartY=5.1 StartZ=0 EndX=7 EndY=3.9 EndZ=0
    g1: LineSegment StartX=7 StartY=3.9 StartZ=0 EndX=9 EndY=3.9 EndZ=0
    g2: LineSegment StartX=7 StartY=5.1 StartZ=0 EndX=7 EndY=5.1 EndZ=0
    g3: LineSegment StartX=7 StartY=5.1 StartZ=0 EndX=7 EndY=7.5 EndZ=0
    g4: LineSegment StartX=9 StartY=5.1 StartZ=0 EndX=9 EndY=3.9 EndZ=0
    g5: LineSegment StartX=7 StartY=7.5 StartZ=0 EndX=9 EndY=7.5 EndZ=0
    g6: LineSegment StartX=9 StartY=7.5 StartZ=0 EndX=9 EndY=5.1 EndZ=0
  constraints (20):
    c: Vertical(g0)
    c: Coincident(g1,g0)
    c: Horizontal(g1)
    c: Coincident(g2,g0)
    c: Horizontal(g2)
    c: Coincident(g3,g2)
    c: Vertical(g3)
    c: Coincident(g5,g3)
    c: Coincident(g4,g6)
    c: Coincident(g4,g1)
    c: Vertical(g4)
    c: Coincident(g0,g-3)
    c: DistanceY(g-4,g3) = 2.4
    c: DistanceX(g1,g1) = 2
    c: DistanceY(g2,g6) = 0
    c: DistanceX(g2,g2) = 0
    c: DistanceY(g0,g0) = 1.2
    c: Coincident(g5,g6)
    c: Horizontal(g5)
    c: Vertical(g6)
FEATURE [Sketcher::SketchObject] Sketch067  label="perno per blocco switch"
  ArcFitTolerance = 1e-06
  AttachmentSupport = -> [XZ_Plane]
  ExternalGeometry = -> [Sketch,Sketch010]
  FullyConstrained = true
  MakeInternals = false
  MapMode = 5
  Placement = pos=(0,0,0) rot=(1,0,0;1.5708rad)
  sketch-geometry (14):
    g0: LineSegment StartX=-191.073 StartY=24.9429 StartZ=0 EndX=-185.81 EndY=23.0276 EndZ=0
    g1: LineSegment StartX=-183.76 StartY=23.9839 StartZ=0 EndX=-182.392 EndY=27.7427 EndZ=0
    g2: LineSegment StartX=-183.348 StartY=29.7934 StartZ=0 EndX=-188.61 EndY=31.7087 EndZ=0
    g3: LineSegment StartX=-188.61 StartY=31.7087 StartZ=0 EndX=-191.073 EndY=24.9429 EndZ=0
    g4: GeomPoint [constr] X=-186.459 Y=27.0946 Z=0
    g5: LineSegment StartX=-189.022 StartY=25.8992 StartZ=0 EndX=-185.263 EndY=24.5311 EndZ=0
    g6: LineSegment StartX=-185.263 StartY=24.5311 StartZ=0 EndX=-183.895 EndY=28.2899 EndZ=0
    g7: LineSegment StartX=-183.895 StartY=28.2899 StartZ=0 EndX=-187.654 EndY=29.658 EndZ=0
    g8: LineSegment StartX=-187.654 StartY=29.658 StartZ=0 EndX=-189.022 EndY=25.8992 EndZ=0
    g9: GeomPoint [constr] X=-186.459 Y=27.0946 Z=0
    g10: ArcOfCircle CenterX=-185.263 CenterY=24.5311 CenterZ=0 NormalX=0 NormalY=0 NormalZ=1 AngleXU=0 Radius=1.6 StartAngle=4.36332 EndAngle=5.93412
    g11: GeomPoint [constr] X=-184.307 Y=22.4804 Z=0
    g12: ArcOfCircle CenterX=-183.895 CenterY=28.2899 CenterZ=0 NormalX=0 NormalY=0 NormalZ=1 AngleXU=0 Radius=1.6 StartAngle=5.93412 EndAngle=7.50492
    g13: GeomPoint [constr] X=-181.844 Y=29.2462 Z=0
  constraints (30):
    c: Coincident(g2,g3)
    c: Coincident(g3,g0)
    c: Symmetric(g13,g0,g4)
    c: Distance(g11,g3) = 7.2
    c: Distance(g0,g2) = 7.2
    c: Parallel(g3,g1)
    c: Parallel(g2,g0)
    c: Perpendicular(g2,g3)
    c: Coincident(g5,g6)
    c: Coincident(g6,g7)
    c: Coincident(g7,g8)
    c: Coincident(g8,g5)
    c: Symmetric(g7,g5,g9)
    c: Distance(g6,g8) = 4
    c: Distance(g5,g7) = 4
    c: Coincident(g9,g4)
    c: Parallel(g8,g6)
    c: Parallel(g7,g5)
    c: Perpendicular(g7,g8)
    c: Tangent(g8,g-3)
    c: Tangent(g2,g-4)
    c: PointOnObject(g11,g1)
    c: PointOnObject(g11,g0)
    c: Tangent(g1,g10) = -1.5708
    c: Tangent(g0,g10) = -1.5708
    c: PointOnObject(g13,g1)
    c: Tangent(g1,g12) = -1.5708
    c: Tangent(g2,g12) = -1.5708
    c: Equal(g10,g12)
    c: Coincident(g10,g5)
FEATURE [Part::Extrusion] Extrude072  label="Extrude perno per blocco switch"
  Base = -> Sketch067
  Dir = (0,-1,2e-16)
  DirMode = 2
  FaceMakerClass = Part::FaceMakerBullseye
  FaceMakerMode = 3
  LengthFwd = 25.2
  LengthRev = 0
  Solid = true
  Symmetric = true
FEATURE [Part::MultiFuse] Fusion
  Refine = true
  Shapes = -> [Extrude,Sweep,Extrude007,Extrude011,Extrude005,Extrude012,Extrude013,Extrude016,Extrude031,Extrude039,Extrude045,Extrude072]
FEATURE [Part::Cut] Cut
  Base = -> Fusion
  Refine = true
  Tool = -> Extrude001
FEATURE [Part::Cut] Cut001
  Base = -> Cut
  Refine = true
  Tool = -> Extrude004
FEATURE [Part::Cut] Cut002
  Base = -> Cut001
  Refine = true
  Tool = -> Extrude006
FEATURE [Part::Cut] Cut003
  Base = -> Cut002
  Refine = true
  Tool = -> Extrude008
FEATURE [Part::Cut] Cut004
  Base = -> Cut003
  Refine = true
  Tool = -> Extrude009
FEATURE [Part::Cut] Cut005
  Base = -> Cut004
  Refine = true
  Tool = -> Extrude010
FEATURE [Part::Cut] Cut006
  Base = -> Cut005
  Refine = true
  Tool = -> Extrude014
FEATURE [Part::Cut] Cut007
  Base = -> Cut006
  Refine = true
  Tool = -> Extrude015
FEATURE [Part::Cut] Cut008
  Base = -> Cut007
  Refine = true
  Tool = -> Extrude018
FEATURE [Part::Cut] Cut009
  Base = -> Cut008
  Refine = true
  Tool = -> Extrude019
FEATURE [Part::Cut] Cut010
  Base = -> Cut009
  Refine = true
  Tool = -> Extrude020
FEATURE [Part::Cut] Cut011
  Base = -> Cut010
  Refine = true
  Tool = -> Extrude021
FEATURE [Part::Cut] Cut012
  Base = -> Cut011
  Refine = true
  Tool = -> Extrude022
FEATURE [Part::Cut] Cut013
  Base = -> Cut012
  Refine = true
  Tool = -> Extrude023
FEATURE [Part::Cut] Cut014
  Base = -> Cut013
  Refine = true
  Tool = -> Extrude032
FEATURE [Part::Cut] Cut015
  Base = -> Cut014
  Refine = true
  Tool = -> Extrude033
FEATURE [Part::Cut] Cut016
  Base = -> Cut015
  Refine = true
  Tool = -> Extrude034
FEATURE [Part::Cut] Cut017
  Base = -> Cut016
  Refine = true
  Tool = -> Extrude035
FEATURE [Part::Cut] Cut018
  Base = -> Cut017
  Refine = true
  Tool = -> Extrude036
FEATURE [Part::Cut] Cut019
  Base = -> Cut018
  Refine = true
  Tool = -> Extrude037
FEATURE [Part::Cut] Cut020
  Base = -> Cut019
  Refine = true
  Tool = -> Extrude030
FEATURE [Part::Cut] Cut022
  Base = -> Cut020
  Refine = true
  Tool = -> Extrude038
FEATURE [Part::Cut] Cut023
  Base = -> Cut022
  Refine = true
  Tool = -> Extrude041
FEATURE [Part::Cut] Cut024
  Base = -> Cut023
  Refine = true
  Tool = -> Extrude040
FEATURE [Part::Cut] Cut025
  Base = -> Cut024
  Refine = true
  Tool = -> Extrude042
FEATURE [Part::Cut] Cut026
  Base = -> Cut025
  Refine = true
  Tool = -> Extrude043
FEATURE [Part::Cut] Cut027
  Base = -> Cut026
  Refine = true
  Tool = -> Extrude044
FEATURE [Part::Cut] Cut028
  Base = -> Cut027
  Refine = true
  Tool = -> Extrude046
FEATURE [Part::Cut] Cut029
  Base = -> Cut028
  Refine = true
  Tool = -> Extrude047
FEATURE [Part::Cut] Cut033
  Base = -> Cut029
  Refine = true
  Tool = -> Extrude055
FEATURE [Part::Cut] Cut034
  Base = -> Cut033
  Refine = true
  Tool = -> Extrude056
FEATURE [Part::Cut] Cut035
  Base = -> Cut034
  Refine = true
  Tool = -> Extrude057
FEATURE [Part::Cut] Cut037
  Base = -> Cut035
  Refine = true
  Tool = -> Extrude060
FEATURE [Part::Cut] Cut038
  Base = -> Cut037
  Refine = true
  Tool = -> Extrude061
FEATURE [Part::Cut] Cut039
  Base = -> Cut038
  Refine = true
  Tool = -> Extrude063
FEATURE [Part::Cut] Cut040
  Base = -> Cut039
  Refine = true
  Tool = -> Extrude064
FEATURE [Part::Cut] Cut041
  Base = -> Cut040
  Refine = true
  Tool = -> Extrude062
FEATURE [Sketcher::SketchObject] Sketch068  label="base con smusso sopra neopixel"
  ArcFitTolerance = 1e-06
  AttachmentSupport = -> [YZ_Plane002]
  FullyConstrained = true
  MakeInternals = false
  MapMode = 5
  Placement = pos=(0,0,0) rot=(0.57735,0.57735,0.57735;2.0944rad)
  sketch-geometry (5):
    g0: LineSegment StartX=-9.5 StartY=-6.1 StartZ=0 EndX=9.5 EndY=-6.1 EndZ=0
    g1: LineSegment StartX=9.5 StartY=-6.1 StartZ=0 EndX=9.5 EndY=6.1 EndZ=0
    g2: LineSegment StartX=9.5 StartY=6.1 StartZ=0 EndX=-9.5 EndY=6.1 EndZ=0
    g3: LineSegment StartX=-9.5 StartY=6.1 StartZ=0 EndX=-9.5 EndY=-6.1 EndZ=0
    g4: GeomPoint [constr] X=0 Y=0 Z=0
  constraints (12):
    c: Coincident(g0,g1)
    c: Coincident(g1,g2)
    c: Coincident(g2,g3)
    c: Coincident(g3,g0)
    c: Horizontal(g0)
    c: Horizontal(g2)
    c: Vertical(g1)
    c: Vertical(g3)
    c: Symmetric(g2,g0,g4)
    c: Distance(g1,g3) = 19
    c: Distance(g0,g2) = 12.2
    c: Coincident(g4,g-1)
FEATURE [Sketcher::SketchObject] Sketch069  label="cilindro minore"
  ArcFitTolerance = 1e-06
  AttachmentSupport = -> [XZ_Plane004]
  FullyConstrained = true
  MakeInternals = false
  MapMode = 5
  Placement = pos=(0,0,0) rot=(1,0,0;1.5708rad)
  sketch-geometry (1):
    g0: Circle CenterX=0 CenterY=0 CenterZ=0 NormalX=0 NormalY=0 NormalZ=1 AngleXU=0 Radius=5.8
  constraints (2):
    c: Diameter(g0) = 11.6
    c: Coincident(g0,g-1)
FEATURE [Sketcher::SketchObject] Sketch070  label="cilindro maggiore"
  ArcFitTolerance = 1e-06
  AttachmentSupport = -> [XZ_Plane004]
  ExternalGeometry = -> [Sketch069]
  FullyConstrained = true
  MakeInternals = false
  MapMode = 5
  Placement = pos=(0,0,0) rot=(1,0,0;1.5708rad)
  sketch-geometry (1):
    g0: Circle CenterX=0 CenterY=0 CenterZ=0 NormalX=0 NormalY=0 NormalZ=1 AngleXU=0 Radius=6.5
  constraints (2):
    c: Coincident(g0,g-1)
    c: Diameter(g0) = 13
FEATURE [Sketcher::SketchObject] Sketch071  label="buco interno"
  ArcFitTolerance = 1e-06
  AttachmentSupport = -> [XZ_Plane004]
  ExternalGeometry = -> [Sketch069]
  FullyConstrained = true
  MakeInternals = false
  MapMode = 5
  Placement = pos=(0,0,0) rot=(1,0,0;1.5708rad)
  sketch-geometry (1):
    g0: Circle CenterX=0 CenterY=0 CenterZ=0 NormalX=0 NormalY=0 NormalZ=1 AngleXU=0 Radius=5
  constraints (2):
    c: Coincident(g0,g-1)
    c: Diameter(g0) = 10
FEATURE [PartDesign::Pad] Pad
  Direction = (0,-1,2e-16)
  Length = 1.2
  Length2 = 10
  Placement = pos=(0,0,0) rot=(1,0,0;1.5708rad)
  Profile = -> Sketch070
  ReferenceAxis = -> Sketch070 [N_Axis]
  Refine = true
  Suppressed = false
  Type = 0
FEATURE [PartDesign::Pad] Pad001
  BaseFeature = -> Pad
  Direction = (0,-1,2e-16)
  Length = 5.6
  Length2 = 10
  Placement = pos=(0,0,0) rot=(1,0,0;1.5708rad)
  Profile = -> Sketch069
  ReferenceAxis = -> Sketch069 [N_Axis]
  Refine = true
  Suppressed = false
  Type = 0
FEATURE [PartDesign::Pocket] Pocket
  BaseFeature = -> Pad001
  Direction = (0,1,-2e-16)
  Length = 7
  Length2 = 5
  Midplane = true
  Placement = pos=(0,0,0) rot=(1,0,0;1.5708rad)
  Profile = -> Sketch071
  ReferenceAxis = -> Sketch071 [N_Axis]
  Refine = true
  Suppressed = false
  Type = 0
FEATURE [PartDesign::Fillet] Fillet
  Base = -> Pocket [Face7]
  BaseFeature = -> Pocket
  Placement = pos=(0,0,0) rot=(1,0,0;1.5708rad)
  Radius = 1
  Refine = true
  SupportTransform = false
  Suppressed = false
  UseAllEdges = false
FEATURE [PartDesign::Body] Body004  label="pulsanti lato sinistro"
  AllowCompound = false
  Group = -> [Sketch069,Sketch070,Sketch071,Pad,Pad001,Pocket,Fillet]
  Origin = -> Origin004
  Tip = -> Fillet
FEATURE [Sketcher::SketchObject] Sketch072  label="buco per saldature e diodo driver solenoide"
  ArcFitTolerance = 1e-06
  AttachmentSupport = -> [XZ_Plane]
  ExternalGeometry = -> [Sketch038]
  FullyConstrained = true
  MakeInternals = false
  MapMode = 5
  Placement = pos=(0,0,0) rot=(1,0,0;1.5708rad)
  sketch-geometry (4):
    g0: LineSegment StartX=-212.269 StartY=-43.9083 StartZ=0 EndX=-207.197 EndY=-33.0326 EndZ=0
    g1: LineSegment StartX=-207.197 StartY=-33.0326 StartZ=0 EndX=-207.56 EndY=-32.8635 EndZ=0
    g2: LineSegment StartX=-207.56 StartY=-32.8635 StartZ=0 EndX=-212.631 EndY=-43.7392 EndZ=0
    g3: LineSegment StartX=-212.631 StartY=-43.7392 StartZ=0 EndX=-212.269 EndY=-43.9083 EndZ=0
  constraints (11):
    c: Coincident(g1,g0)
    c: Coincident(g2,g1)
    c: Coincident(g3,g2)
    c: Coincident(g3,g0)
    c: Parallel(g-3,g0)
    c: Parallel(g0,g2)
    c: Perpendicular(g0,g3)
    c: Perpendicular(g1,g0)
    c: Distance(g3) = 0.4
    c: Distance(g2) = 12
    c: Coincident(g0,g-3)
FEATURE [Part::Extrusion] Extrude074  label="Extrude buco per saldature e diodo driver solenoide"
  Base = -> Sketch072
  Dir = (0,-1,2e-16)
  DirMode = 2
  FaceMakerClass = Part::FaceMakerBullseye
  FaceMakerMode = 3
  LengthFwd = 14.6
  LengthRev = 0
  Solid = true
  Symmetric = true
FEATURE [Part::Cut] Cut042
  Base = -> Cut041
  Refine = true
  Tool = -> Extrude074
FEATURE [Sketcher::SketchObject] Sketch073  label="fori slargati blocco solenoide"
  ArcFitTolerance = 1e-06
  AttachmentSupport = -> [XY_Plane]
  ExternalGeometry = -> [Sketch030]
  FullyConstrained = true
  MakeInternals = false
  MapMode = 5
  sketch-geometry (2):
    g0: Circle CenterX=-152.209 CenterY=6.95 CenterZ=0 NormalX=0 NormalY=0 NormalZ=1 AngleXU=0 Radius=3.7
    g1: Circle CenterX=-130.41 CenterY=-6.95 CenterZ=0 NormalX=0 NormalY=0 NormalZ=1 AngleXU=0 Radius=3.7
  constraints (4):
    c: Diameter(g0) = 7.4
    c: Coincident(g0,g-3)
    c: Diameter(g1) = 7.4
    c: Coincident(g1,g-4)
FEATURE [Part::Extrusion] Extrude075  label="Extrude fori slargati blocco solenoide"
  Base = -> Sketch073
  Dir = (0,0,1)
  DirMode = 2
  FaceMakerClass = Part::FaceMakerBullseye
  FaceMakerMode = 3
  LengthFwd = 1.5
  LengthRev = 0
  Placement = pos=(0,0,36.4) rot=(0,0,1;0rad)
  Solid = true
  Symmetric = false
FEATURE [Part::Cut] Cut043
  Base = -> Cut042
  Refine = true
  Tool = -> Extrude075
FEATURE [Sketcher::SketchObject] Sketch074  label="lato sx pistola"
  ArcFitTolerance = 1e-06
  AttachmentSupport = -> [XZ_Plane]
  ExternalGeometry = -> [Sketch016,Sketch,Sketch058]
  FullyConstrained = true
  MakeInternals = false
  MapMode = 5
  Placement = pos=(0,0,0) rot=(1,0,0;1.5708rad)
  sketch-geometry (37):
    g0: LineSegment StartX=-82.8 StartY=3.2 StartZ=0 EndX=0 EndY=3.2 EndZ=0
    g1: LineSegment StartX=-82.8 StartY=3.2 StartZ=0 EndX=-82.8 EndY=6.2 EndZ=0
    g2: LineSegment [constr] StartX=-107.6 StartY=18 StartZ=0 EndX=-107.6 EndY=20 EndZ=0
    g3: LineSegment [constr] StartX=-132.428 StartY=18 StartZ=0 EndX=-132.428 EndY=20 EndZ=0
    g4: LineSegment StartX=-132.428 StartY=20 StartZ=0 EndX=-107.6 EndY=20 EndZ=0
    g5: ArcOfCircle CenterX=-107.6 CenterY=4 CenterZ=0 NormalX=0 NormalY=0 NormalZ=1 AngleXU=0 Radius=16 StartAngle=0.137937 EndAngle=1.5708
    g6: LineSegment StartX=-82.8 StartY=6.2 StartZ=0 EndX=-91.752 EndY=6.2 EndZ=0
    g7: LineSegment [constr] StartX=-145.743 StartY=8.32624 StartZ=0 EndX=-147.645 EndY=8.94427 EndZ=0
    g8: ArcOfCircle CenterX=-132.428 CenterY=4 CenterZ=0 NormalX=0 NormalY=0 NormalZ=1 AngleXU=0 Radius=16 StartAngle=1.5708 EndAngle=2.82743
    g9: LineSegment StartX=-215.932 StartY=-80.4316 StartZ=0 EndX=-176.685 EndY=-80.4316 EndZ=0
    g10: LineSegment StartX=-147.645 StartY=8.94427 StartZ=0 EndX=-176.685 EndY=-80.4316 EndZ=0
    g11: LineSegment [constr] StartX=-193.988 StartY=-2.33927 StartZ=0 EndX=-192.176 EndY=-3.18451 EndZ=0
    g12: LineSegment [constr] StartX=-217.232 StartY=-52.1862 StartZ=0 EndX=-215.42 EndY=-53.0314 EndZ=0
    g13: LineSegment StartX=-192.176 StartY=-3.18451 StartZ=0 EndX=-215.42 EndY=-53.0314 EndZ=0
    g14: ArcOfCircle CenterX=-184.801 CenterY=-67.3089 CenterZ=0 NormalX=0 NormalY=0 NormalZ=1 AngleXU=0 Radius=33.7833 StartAngle=2.70526 EndAngle=3.54053
    g15: ArcOfCircle CenterX=-207.583 CenterY=4 CenterZ=0 NormalX=0 NormalY=0 NormalZ=1 AngleXU=0 Radius=17 StartAngle=5.84685 EndAngle=7.56663
    g16: LineSegment StartX=-202.765 StartY=20.303 StartZ=0 EndX=-195.887 EndY=39.2 EndZ=0
    g17: LineSegment [constr] StartX=-193.885 StartY=33.0037 StartZ=0 EndX=-197.644 EndY=34.3718 EndZ=0
    g18: LineSegment StartX=-195.887 StartY=39.2 StartZ=0 EndX=0 EndY=39.2 EndZ=0
    g19: LineSegment StartX=0 StartY=3.2 StartZ=0 EndX=0 EndY=39.2 EndZ=0
    g20: LineSegment StartX=-189.939 StartY=31.5672 StartZ=0 EndX=-192.333 EndY=24.9893 EndZ=0
    g21: LineSegment StartX=-196.467 StartY=26.4942 StartZ=0 EndX=-194.073 EndY=33.0721 EndZ=0
    g22: Circle CenterX=-213.443 CenterY=-76.8316 CenterZ=0 NormalX=0 NormalY=0 NormalZ=1 AngleXU=0 Radius=1.8
    g23: Circle CenterX=-179.305 CenterY=-76.8316 CenterZ=0 NormalX=0 NormalY=0 NormalZ=1 AngleXU=0 Radius=1.8
    g24: Circle CenterX=-184.08 CenterY=34.8 CenterZ=0 NormalX=0 NormalY=0 NormalZ=1 AngleXU=0 Radius=1.8
    g25: Circle CenterX=-78.51 CenterY=34.8 CenterZ=0 NormalX=0 NormalY=0 NormalZ=1 AngleXU=0 Radius=1.8
    g26: Circle CenterX=-78.51 CenterY=7.6 CenterZ=0 NormalX=0 NormalY=0 NormalZ=1 AngleXU=0 Radius=1.8
    g27: Circle CenterX=-5.6 CenterY=34.8 CenterZ=0 NormalX=0 NormalY=0 NormalZ=1 AngleXU=0 Radius=1.8
    g28: Circle CenterX=-5.6 CenterY=7.6 CenterZ=0 NormalX=0 NormalY=0 NormalZ=1 AngleXU=0 Radius=1.8
    g29: LineSegment StartX=-190.127 StartY=31.6356 StartZ=0 EndX=-189.939 EndY=31.5672 EndZ=0
    g30: LineSegment StartX=-194.073 StartY=33.0721 StartZ=0 EndX=-193.885 EndY=33.0037 EndZ=0
    g31: LineSegment StartX=-193.885 StartY=33.0037 StartZ=0 EndX=-190.127 EndY=31.6356 EndZ=0
    g32: LineSegment StartX=-196.467 StartY=26.4942 StartZ=0 EndX=-192.333 EndY=24.9893 EndZ=0
    g33: Circle CenterX=-19 CenterY=21.2 CenterZ=0 NormalX=0 NormalY=0 NormalZ=1 AngleXU=0 Radius=6.3
    g34: Circle CenterX=-42 CenterY=21.2 CenterZ=0 NormalX=0 NormalY=0 NormalZ=1 AngleXU=0 Radius=6.3
    g35: Circle CenterX=-65 CenterY=21.2 CenterZ=0 NormalX=0 NormalY=0 NormalZ=1 AngleXU=0 Radius=6.3
    g36: LineSegment [constr] StartX=-4 StartY=21.2 StartZ=0 EndX=-65 EndY=21.2 EndZ=0
  constraints (96):
    c: Coincident(g0,g-41)
    c: Horizontal(g0)
    c: PointOnObject(g0,g-39)
    c: Coincident(g1,g0)
    c: Vertical(g1)
    c: DistanceY(g1,g1) = 3
    c: Coincident(g2,g-17)
    c: Vertical(g2)
    c: Coincident(g3,g-16)
    c: Vertical(g3)
    c: DistanceY(g2,g2) = 2
    c: DistanceY(g3,g3) = 2
    c: Coincident(g4,g3)
    c: Coincident(g4,g2)
    c: Coincident(g5,g-17)
    c: Coincident(g5,g2)
    c: Coincident(g6,g1)
    c: Horizontal(g6)
    c: Coincident(g6,g5)
    c: Coincident(g7,g-15)
    c: Coincident(g8,g7)
    c: Coincident(g8,g3)
    c: Coincident(g8,g-15)
    c: Horizontal(g9)
    c: DistanceY(g-13,g9) = 2
    c: Coincident(g10,g7)
    c: Parallel(g10,g-14)
    c: Coincident(g9,g10)
    c: Distance(g11) = 2
    c: Coincident(g11,g-11)
    c: Perpendicular(g-11,g11)
    c: Distance(g12) = 2
    c: Coincident(g12,g-12)
    c: Perpendicular(g-11,g12)
    c: Coincident(g13,g11)
    c: Coincident(g13,g12)
    c: Coincident(g14,g-32)
    c: Coincident(g14,g12)
    c: Coincident(g14,g9)
    c: Coincident(g15,g-10)
    c: Coincident(g15,g11)
    c: Parallel(g16,g-22)
    c: Distance(g17) = 4
    c: PointOnObject(g17,g16)
    c: Coincident(g15,g16)
    c: Horizontal(g18)
    c: Coincident(g18,g16)
    c: Coincident(g19,g0)
    c: PointOnObject(g19,g-39)
    c: DistanceY(g19,g-36) = 2
    c: Coincident(g18,g19)
    c: Diameter(g22) = 3.6
    c: Coincident(g22,g-9)
    c: Diameter(g23) = 3.6
    c: Coincident(g23,g-8)
    c: Diameter(g24) = 3.6
    c: Diameter(g25) = 3.6
    c: Diameter(g26) = 3.6
    c: Diameter(g27) = 3.6
    c: Diameter(g28) = 3.6
    c: Coincident(g27,g-4)
    c: Coincident(g28,g-3)
    c: Coincident(g25,g-6)
    c: Coincident(g26,g-5)
    c: Coincident(g24,g-7)
    c: Parallel(g20,g-21)
    c: Equal(g20,g-21)
    c: Parallel(g21,g-19)
    c: Equal(g21,g-19)
    c: Distance(g29) = 0.2
    c: Distance(g30) = 0.2
    c: Parallel(g29,g-20)
    c: Parallel(g31,g-20)
    c: Equal(g31,g-20)
    c: Coincident(g30,g31)
    c: Coincident(g31,g29)
    c: Coincident(g29,g-21)
    c: Parallel(g30,g31)
    c: Coincident(g17,g30)
    c: Coincident(g20,g29)
    c: Coincident(g21,g30)
    c: Perpendicular(g16,g17)
    c: Coincident(g32,g21)
    c: Coincident(g32,g20)
    c: Perpendicular(g10,g7)
    c: Diameter(g33) = 12.6
    c: Diameter(g34) = 12.6
    c: Diameter(g35) = 12.6
    c: Horizontal(g36)
    c: PointOnObject(g33,g36)
    c: PointOnObject(g34,g36)
    c: DistanceX(g34,g33) = 23
    c: DistanceX(g35,g34) = 23
    c: DistanceX(g33,g36) = 15
    c: Symmetric(g-24,g-24,g36)
    c: Coincident(g36,g35)
FEATURE [Sketcher::SketchObject] Sketch075  label="lato dx pistola"
  ArcFitTolerance = 1e-06
  AttachmentSupport = -> [XZ_Plane]
  ExternalGeometry = -> [Sketch016,Sketch,Sketch058,Sketch074]
  FullyConstrained = true
  MakeInternals = false
  MapMode = 5
  Placement = pos=(0,0,0) rot=(1,0,0;1.5708rad)
  sketch-geometry (61):
    g0: LineSegment StartX=-82.8 StartY=3.2 StartZ=0 EndX=0 EndY=3.2 EndZ=0
    g1: LineSegment StartX=-82.8 StartY=3.2 StartZ=0 EndX=-82.8 EndY=6.2 EndZ=0
    g2: LineSegment [constr] StartX=-107.6 StartY=18 StartZ=0 EndX=-107.6 EndY=20 EndZ=0
    g3: LineSegment [constr] StartX=-132.428 StartY=18 StartZ=0 EndX=-132.428 EndY=20 EndZ=0
    g4: LineSegment StartX=-132.428 StartY=20 StartZ=0 EndX=-107.6 EndY=20 EndZ=0
    g5: ArcOfCircle CenterX=-107.6 CenterY=4 CenterZ=0 NormalX=0 NormalY=0 NormalZ=1 AngleXU=0 Radius=16 StartAngle=0.137937 EndAngle=1.5708
    g6: LineSegment StartX=-82.8 StartY=6.2 StartZ=0 EndX=-91.752 EndY=6.2 EndZ=0
    g7: LineSegment [constr] StartX=-145.743 StartY=8.32624 StartZ=0 EndX=-147.645 EndY=8.94427 EndZ=0
    g8: ArcOfCircle CenterX=-132.428 CenterY=4 CenterZ=0 NormalX=0 NormalY=0 NormalZ=1 AngleXU=0 Radius=16 StartAngle=1.5708 EndAngle=2.82743
    g9: LineSegment StartX=-215.932 StartY=-80.4316 StartZ=0 EndX=-176.685 EndY=-80.4316 EndZ=0
    g10: LineSegment StartX=-147.645 StartY=8.94427 StartZ=0 EndX=-176.685 EndY=-80.4316 EndZ=0
    g11: LineSegment [constr] StartX=-193.988 StartY=-2.33927 StartZ=0 EndX=-192.176 EndY=-3.18451 EndZ=0
    g12: LineSegment [constr] StartX=-217.232 StartY=-52.1862 StartZ=0 EndX=-215.42 EndY=-53.0314 EndZ=0
    g13: LineSegment StartX=-192.176 StartY=-3.18451 StartZ=0 EndX=-215.42 EndY=-53.0314 EndZ=0
    g14: ArcOfCircle CenterX=-184.801 CenterY=-67.3089 CenterZ=0 NormalX=0 NormalY=0 NormalZ=1 AngleXU=0 Radius=33.7833 StartAngle=2.70526 EndAngle=3.54053
    g15: ArcOfCircle CenterX=-207.583 CenterY=4 CenterZ=0 NormalX=0 NormalY=0 NormalZ=1 AngleXU=0 Radius=17 StartAngle=5.84685 EndAngle=7.56663
    g16: LineSegment StartX=-202.765 StartY=20.303 StartZ=0 EndX=-195.887 EndY=39.2 EndZ=0
    g17: LineSegment [constr] StartX=-193.885 StartY=33.0037 StartZ=0 EndX=-197.644 EndY=34.3718 EndZ=0
    g18: LineSegment StartX=-195.887 StartY=39.2 StartZ=0 EndX=0 EndY=39.2 EndZ=0
    g19: LineSegment StartX=0 StartY=3.2 StartZ=0 EndX=0 EndY=39.2 EndZ=0
    g20: LineSegment StartX=-189.939 StartY=31.5672 StartZ=0 EndX=-192.333 EndY=24.9893 EndZ=0
    g21: LineSegment StartX=-196.467 StartY=26.4942 StartZ=0 EndX=-194.073 EndY=33.0721 EndZ=0
    g22: Circle CenterX=-213.443 CenterY=-76.8316 CenterZ=0 NormalX=0 NormalY=0 NormalZ=1 AngleXU=0 Radius=1.8
    g23: Circle CenterX=-179.305 CenterY=-76.8316 CenterZ=0 NormalX=0 NormalY=0 NormalZ=1 AngleXU=0 Radius=1.8
    g24: Circle CenterX=-184.08 CenterY=34.8 CenterZ=0 NormalX=0 NormalY=0 NormalZ=1 AngleXU=0 Radius=1.8
    g25: Circle CenterX=-78.51 CenterY=34.8 CenterZ=0 NormalX=0 NormalY=0 NormalZ=1 AngleXU=0 Radius=1.8
    g26: Circle CenterX=-78.51 CenterY=7.6 CenterZ=0 NormalX=0 NormalY=0 NormalZ=1 AngleXU=0 Radius=1.8
    g27: Circle CenterX=-5.6 CenterY=34.8 CenterZ=0 NormalX=0 NormalY=0 NormalZ=1 AngleXU=0 Radius=1.8
    g28: Circle CenterX=-5.6 CenterY=7.6 CenterZ=0 NormalX=0 NormalY=0 NormalZ=1 AngleXU=0 Radius=1.8
    g29: LineSegment StartX=-190.127 StartY=31.6356 StartZ=0 EndX=-189.939 EndY=31.5672 EndZ=0
    g30: LineSegment StartX=-194.073 StartY=33.0721 StartZ=0 EndX=-193.885 EndY=33.0037 EndZ=0
    g31: LineSegment StartX=-193.885 StartY=33.0037 StartZ=0 EndX=-190.127 EndY=31.6356 EndZ=0
    g32: LineSegment StartX=-196.467 StartY=26.4942 StartZ=0 EndX=-192.333 EndY=24.9893 EndZ=0
    g33: LineSegment [constr] StartX=-4 StartY=21.2 StartZ=0 EndX=-87.91 EndY=21.2 EndZ=0
    g34: GeomPoint [constr] X=-4 Y=21.2 Z=0
    g35: LineSegment [constr] StartX=-15.2 StartY=33.7 StartZ=0 EndX=-15.2 EndY=8.7 EndZ=0
    g36: LineSegment [constr] StartX=-15.2 StartY=33.7 StartZ=0 EndX=-56.2 EndY=33.7 EndZ=0
    g37: LineSegment [constr] StartX=-15.2 StartY=8.7 StartZ=0 EndX=-56.2 EndY=8.7 EndZ=0
    g38: LineSegment [constr] StartX=-56.2 StartY=33.7 StartZ=0 EndX=-56.2 EndY=8.7 EndZ=0
    g39: Circle CenterX=-18.6 CenterY=30.3 CenterZ=0 NormalX=0 NormalY=0 NormalZ=1 AngleXU=0 Radius=3.4
    g40: Circle CenterX=-18.6 CenterY=12.1 CenterZ=0 NormalX=0 NormalY=0 NormalZ=1 AngleXU=0 Radius=3.4
    g41: Circle CenterX=-43.2 CenterY=30.3 CenterZ=0 NormalX=0 NormalY=0 NormalZ=1 AngleXU=0 Radius=3.4
    g42: Circle CenterX=-43.2 CenterY=12.1 CenterZ=0 NormalX=0 NormalY=0 NormalZ=1 AngleXU=0 Radius=3.4
    g43: LineSegment [constr] StartX=-4 StartY=21.2 StartZ=0 EndX=-15.2 EndY=21.2 EndZ=0
    g44: LineSegment [constr] StartX=-15.2 StartY=21.2 StartZ=0 EndX=-36.2 EndY=21.2 EndZ=0
    g45: LineSegment [constr] StartX=-41.5 StartY=16.2 StartZ=0 EndX=-30.9 EndY=16.2 EndZ=0
    g46: LineSegment [constr] StartX=-30.9 StartY=16.2 StartZ=0 EndX=-30.9 EndY=26.2 EndZ=0
    g47: LineSegment [constr] StartX=-30.9 StartY=26.2 StartZ=0 EndX=-41.5 EndY=26.2 EndZ=0
    g48: LineSegment [constr] StartX=-41.5 StartY=26.2 StartZ=0 EndX=-41.5 EndY=16.2 EndZ=0
    g49: GeomPoint [constr] X=-36.2 Y=21.2 Z=0
    g50: Circle CenterX=-36.2 CenterY=21.2 CenterZ=0 NormalX=0 NormalY=0 NormalZ=1 AngleXU=0 Radius=2.8
    g51: LineSegment [constr] StartX=-24.2 StartY=26.7 StartZ=0 EndX=-24.2 EndY=15.7 EndZ=0
    g52: Circle CenterX=-24.2 CenterY=26.7 CenterZ=0 NormalX=0 NormalY=0 NormalZ=1 AngleXU=0 Radius=3
    g53: Circle CenterX=-24.2 CenterY=15.7 CenterZ=0 NormalX=0 NormalY=0 NormalZ=1 AngleXU=0 Radius=3
    g54: GeomPoint X=-18.6 Y=30.3 Z=0
    g55: GeomPoint X=-18.6 Y=12.1 Z=0
    g56: GeomPoint X=-43.2 Y=12.1 Z=0
    g57: GeomPoint X=-43.2 Y=30.3 Z=0
    g58: Circle CenterX=-65 CenterY=21.2 CenterZ=0 NormalX=0 NormalY=0 NormalZ=1 AngleXU=0 Radius=1.5
    g59: Circle CenterX=-42 CenterY=21.2 CenterZ=0 NormalX=0 NormalY=0 NormalZ=1 AngleXU=0 Radius=1.5
    g60: Circle CenterX=-19 CenterY=21.2 CenterZ=0 NormalX=0 NormalY=0 NormalZ=1 AngleXU=0 Radius=1.5
  constraints (149):
    c: Coincident(g0,g-41)
    c: Horizontal(g0)
    c: PointOnObject(g0,g-39)
    c: Coincident(g1,g0)
    c: Vertical(g1)
    c: DistanceY(g1,g1) = 3
    c: Coincident(g2,g-17)
    c: Vertical(g2)
    c: Coincident(g3,g-16)
    c: Vertical(g3)
    c: DistanceY(g2,g2) = 2
    c: DistanceY(g3,g3) = 2
    c: Coincident(g4,g3)
    c: Coincident(g4,g2)
    c: Coincident(g5,g-17)
    c: Coincident(g5,g2)
    c: Coincident(g6,g1)
    c: Horizontal(g6)
    c: Coincident(g6,g5)
    c: Coincident(g7,g-15)
    c: Coincident(g8,g7)
    c: Coincident(g8,g3)
    c: Coincident(g8,g-15)
    c: Horizontal(g9)
    c: DistanceY(g-13,g9) = 2
    c: Coincident(g10,g7)
    c: Parallel(g10,g-14)
    c: Coincident(g9,g10)
    c: Distance(g11) = 2
    c: Coincident(g11,g-11)
    c: Perpendicular(g-11,g11)
    c: Distance(g12) = 2
    c: Coincident(g12,g-12)
    c: Perpendicular(g-11,g12)
    c: Coincident(g13,g11)
    c: Coincident(g13,g12)
    c: Coincident(g14,g-32)
    c: Coincident(g14,g12)
    c: Coincident(g14,g9)
    c: Coincident(g15,g-10)
    c: Coincident(g15,g11)
    c: Parallel(g16,g-22)
    c: Distance(g17) = 4
    c: PointOnObject(g17,g16)
    c: Coincident(g15,g16)
    c: Horizontal(g18)
    c: Coincident(g18,g16)
    c: Coincident(g19,g0)
    c: PointOnObject(g19,g-39)
    c: DistanceY(g19,g-36) = 2
    c: Coincident(g18,g19)
    c: Diameter(g22) = 3.6
    c: Coincident(g22,g-9)
    c: Diameter(g23) = 3.6
    c: Coincident(g23,g-8)
    c: Diameter(g24) = 3.6
    c: Diameter(g25) = 3.6
    c: Diameter(g26) = 3.6
    c: Diameter(g27) = 3.6
    c: Diameter(g28) = 3.6
    c: Coincident(g27,g-4)
    c: Coincident(g28,g-3)
    c: Coincident(g25,g-6)
    c: Coincident(g26,g-5)
    c: Coincident(g24,g-7)
    c: Parallel(g20,g-21)
    c: Equal(g20,g-21)
    c: Parallel(g21,g-19)
    c: Equal(g21,g-19)
    c: Distance(g29) = 0.2
    c: Distance(g30) = 0.2
    c: Parallel(g29,g-20)
    c: Parallel(g31,g-20)
    c: Equal(g31,g-20)
    c: Coincident(g30,g31)
    c: Coincident(g31,g29)
    c: Coincident(g29,g-21)
    c: Parallel(g30,g31)
    c: Coincident(g17,g30)
    c: Coincident(g20,g29)
    c: Coincident(g21,g30)
    c: Perpendicular(g16,g17)
    c: Coincident(g32,g21)
    c: Coincident(g32,g20)
    c: Perpendicular(g10,g7)
    c: Horizontal(g33)
    c: Symmetric(g-24,g-24,g33)
    c: PointOnObject(g33,g-28)
    c: Symmetric(g-24,g-24,g34)
    c: DistanceY(g35,g35) = 25
    c: Symmetric(g35,g35,g33)
    c: Distance(g36) = 41
    c: Coincident(g36,g35)
    c: Horizontal(g36)
    c: Coincident(g37,g35)
    c: Horizontal(g37)
    c: Coincident(g38,g36)
    c: Vertical(g38)
    c: Coincident(g37,g38)
    c: Diameter(g39) = 6.8
    c: Diameter(g40) = 6.8
    c: Tangent(g39,g36)
    c: Tangent(g40,g37)
    c: Tangent(g39,g35)
    c: Tangent(g40,g35)
    c: Diameter(g41) = 6.8
    c: Diameter(g42) = 6.8
    c: Tangent(g41,g36)
    c: Tangent(g42,g37)
    c: DistanceX(g41,g39) = 24.6
    c: DistanceX(g42,g40) = 24.6
    c: Distance(g43) = 11.2
    c: Coincident(g43,g33)
    c: PointOnObject(g43,g33)
    c: PointOnObject(g43,g35)
    c: Distance(g44) = 21
    c: Coincident(g44,g43)
    c: PointOnObject(g44,g33)
    c: Coincident(g45,g46)
    c: Coincident(g46,g47)
    c: Coincident(g47,g48)
    c: Coincident(g48,g45)
    c: Horizontal(g45)
    c: Horizontal(g47)
    c: Vertical(g46)
    c: Vertical(g48)
    c: Symmetric(g47,g45,g49)
    c: Distance(g46,g48) = 10.6
    c: Distance(g45,g47) = 10
    c: Coincident(g49,g44)
    c: Diameter(g50) = 5.6
    c: Coincident(g50,g44)
    c: Distance(g51) = 11
    c: Symmetric(g51,g51,g33)
    c: DistanceX(g51,g43) = 9
    c: Diameter(g52) = 6
    c: Coincident(g52,g51)
    c: Diameter(g53) = 6
    c: Coincident(g53,g51)
    c: Coincident(g40,g55)
    c: Coincident(g39,g54)
    c: Coincident(g41,g57)
    c: Coincident(g42,g56)
    c: Diameter(g58) = 3
    c: Diameter(g59) = 3
    c: Diameter(g60) = 3
    c: Coincident(g58,g-44)
    c: Coincident(g59,g-46)
    c: Coincident(g60,g-45)
FEATURE [Sketcher::SketchObject] Sketch078
  ArcFitTolerance = 1e-06
  AttachmentSupport = -> [XZ_Plane005]
  FullyConstrained = true
  MakeInternals = false
  MapMode = 5
  Placement = pos=(0,0,0) rot=(1,0,0;1.5708rad)
  sketch-geometry (5):
    g0: LineSegment [constr] StartX=0 StartY=5.5 StartZ=0 EndX=0 EndY=-5.5 EndZ=0
    g1: ArcOfCircle CenterX=0 CenterY=5.5 CenterZ=0 NormalX=0 NormalY=0 NormalZ=1 AngleXU=0 Radius=2.7 StartAngle=0 EndAngle=3.14159
    g2: ArcOfCircle CenterX=0 CenterY=-5.5 CenterZ=0 NormalX=0 NormalY=0 NormalZ=1 AngleXU=0 Radius=2.7 StartAngle=3.1416 EndAngle=6.28318
    g3: LineSegment StartX=-2.7 StartY=5.5 StartZ=0 EndX=-2.7 EndY=-5.50001 EndZ=0
    g4: LineSegment StartX=2.7 StartY=5.5 StartZ=0 EndX=2.7 EndY=-5.50001 EndZ=0
  constraints (13):
    c: Distance(g0) = 11
    c: Vertical(g0)
    c: Symmetric(g0,g0,g-1)
    c: Radius(g1) = 2.7
    c: Coincident(g1,g0)
    c: Radius(g2) = 2.7
    c: Coincident(g2,g0)
    c: Vertical(g3)
    c: Vertical(g4)
    c: Coincident(g2,g4)
    c: Coincident(g2,g3)
    c: Tangent(g3,g1) = -1.5708
    c: Tangent(g4,g1) = 1.5708
FEATURE [PartDesign::Pad] Pad002
  Direction = (0,-1,2e-16)
  Length = 0.8
  Length2 = 10
  Placement = pos=(0,0,0) rot=(1,0,0;1.5708rad)
  Profile = -> Sketch078
  ReferenceAxis = -> Sketch078 [N_Axis]
  Refine = true
  Suppressed = false
  Type = 0
FEATURE [Sketcher::SketchObject] Sketch079
  ArcFitTolerance = 1e-06
  AttachmentSupport = -> [XZ_Plane005]
  ExternalGeometry = -> [Sketch078]
  FullyConstrained = true
  MakeInternals = false
  MapMode = 5
  Placement = pos=(0,0,0) rot=(1,0,0;1.5708rad)
  sketch-geometry (2):
    g0: Circle CenterX=-1e-16 CenterY=5.5 CenterZ=0 NormalX=0 NormalY=0 NormalZ=1 AngleXU=0 Radius=2.7
    g1: Circle CenterX=0 CenterY=-5.5 CenterZ=0 NormalX=0 NormalY=0 NormalZ=1 AngleXU=0 Radius=2.7
  constraints (4):
    c: Coincident(g0,g-3)
    c: PointOnObject(g-3,g0)
    c: Coincident(g1,g-4)
    c: Equal(g1,g-4)
FEATURE [PartDesign::Pad] Pad003
  BaseFeature = -> Pad002
  Direction = (0,-1,2e-16)
  Length = 5
  Length2 = 10
  Placement = pos=(0,0,0) rot=(1,0,0;1.5708rad)
  Profile = -> Sketch079
  ReferenceAxis = -> Sketch079 [N_Axis]
  Refine = true
  Suppressed = false
  Type = 0
FEATURE [PartDesign::Fillet] Fillet001
  Base = -> Pad003 [Edge16,Edge14]
  BaseFeature = -> Pad003
  Placement = pos=(0,0,0) rot=(1,0,0;1.5708rad)
  Radius = 0.4
  Refine = true
  SupportTransform = false
  Suppressed = false
  UseAllEdges = false
FEATURE [PartDesign::Body] Body005  label="pulsanti lato destro"
  AllowCompound = false
  Group = -> [Sketch078,Pad002,Sketch079,Pad003,Fillet001]
  Origin = -> Origin005
  Tip = -> Fillet001
FEATURE [PartDesign::SubShapeBinder] Binder
  BindCopyOnChange = 0
  BindMode = 0
  ClaimChildren = false
  Context = -> Body006 [Binder.]
  Fuse = false
  MakeFace = true
  OffsetFill = false
  OffsetIntersection = false
  OffsetJoinType = 0
  OffsetOpenResult = false
  PartialLoad = false
  Refine = true
  Relative = true
  Support = -> [Body[Sketch074.]]
  _Version = 2
FEATURE [PartDesign::SubShapeBinder] Binder001
  BindCopyOnChange = 0
  BindMode = 0
  ClaimChildren = false
  Context = -> Body007 [Binder001.]
  Fuse = false
  MakeFace = true
  OffsetFill = false
  OffsetIntersection = false
  OffsetJoinType = 0
  OffsetOpenResult = false
  PartialLoad = false
  Refine = true
  Relative = true
  Support = -> [Body[Sketch075.]]
  _Version = 2
FEATURE [Mesh::Feature] logo_per_PCB_definitivo_positivo
  Placement = pos=(-191,17,-66) rot=(0,1,1;0rad)
FEATURE [Sketcher::SketchObject] Sketch114  label="Sketch114 - base lato DX"
  ArcFitTolerance = 1e-06
  AttachmentSupport = -> [Binder001]
  ExternalGeometry = -> [Binder001]
  FullyConstrained = true
  MakeInternals = false
  MapMode = 5
  Placement = pos=(0,1e-15,0) rot=(0,0.707107,0.707107;3.14159rad)
  sketch-geometry (30):
    g0: Circle CenterX=5.6 CenterY=34.8 CenterZ=0 NormalX=0 NormalY=0 NormalZ=1 AngleXU=0 Radius=1.8
    g1: Circle CenterX=5.6 CenterY=7.6 CenterZ=0 NormalX=0 NormalY=0 NormalZ=1 AngleXU=0 Radius=1.8
    g2: Circle CenterX=24.2 CenterY=26.7 CenterZ=0 NormalX=0 NormalY=0 NormalZ=1 AngleXU=0 Radius=3
    g3: Circle CenterX=24.2 CenterY=15.7 CenterZ=0 NormalX=0 NormalY=0 NormalZ=1 AngleXU=0 Radius=3
    g4: Circle CenterX=36.2 CenterY=21.2 CenterZ=0 NormalX=0 NormalY=0 NormalZ=1 AngleXU=0 Radius=2.8
    g5: Circle CenterX=78.51 CenterY=34.8 CenterZ=0 NormalX=0 NormalY=0 NormalZ=1 AngleXU=0 Radius=1.8
    g6: Circle CenterX=78.51 CenterY=7.6 CenterZ=0 NormalX=0 NormalY=0 NormalZ=1 AngleXU=0 Radius=1.8
    g7: Circle CenterX=184.08 CenterY=34.8 CenterZ=0 NormalX=0 NormalY=0 NormalZ=1 AngleXU=0 Radius=1.8
    g8: Circle CenterX=213.443 CenterY=-76.8316 CenterZ=0 NormalX=0 NormalY=0 NormalZ=1 AngleXU=0 Radius=1.8
    g9: Circle CenterX=179.305 CenterY=-76.8316 CenterZ=0 NormalX=0 NormalY=0 NormalZ=1 AngleXU=0 Radius=1.8
    g10: ArcOfCircle [constr] CenterX=132.428 CenterY=4 CenterZ=0 NormalX=0 NormalY=0 NormalZ=1 AngleXU=0 Radius=16 StartAngle=0.314159 EndAngle=1.5708
    g11: ArcOfCircle CenterX=107.6 CenterY=4 CenterZ=0 NormalX=0 NormalY=0 NormalZ=1 AngleXU=0 Radius=16 StartAngle=1.5708 EndAngle=3.00366
    g12: ArcOfCircle CenterX=207.583 CenterY=4 CenterZ=0 NormalX=0 NormalY=0 NormalZ=1 AngleXU=0 Radius=17 StartAngle=1.85815 EndAngle=3.57792
    g13: ArcOfCircle CenterX=184.801 CenterY=-67.3089 CenterZ=0 NormalX=0 NormalY=0 NormalZ=1 AngleXU=0 Radius=33.7833 StartAngle=5.88425 EndAngle=6.71952
    g14: LineSegment StartX=0 StartY=39.2 StartZ=0 EndX=0 EndY=3.2 EndZ=0
    g15: LineSegment StartX=0 StartY=3.2 StartZ=0 EndX=82.8 EndY=3.2 EndZ=0
    g16: LineSegment StartX=82.8 StartY=3.2 StartZ=0 EndX=82.8 EndY=6.2 EndZ=0
    g17: LineSegment StartX=82.8 StartY=6.2 StartZ=0 EndX=91.752 EndY=6.2 EndZ=0
    g18: LineSegment StartX=107.6 StartY=20 StartZ=0 EndX=132.428 EndY=20 EndZ=0
    g19: LineSegment StartX=147.645 StartY=8.94427 StartZ=0 EndX=176.685 EndY=-80.4316 EndZ=0
    g20: LineSegment StartX=176.685 StartY=-80.4316 StartZ=0 EndX=215.932 EndY=-80.4316 EndZ=0
    g21: LineSegment StartX=215.42 StartY=-53.0314 StartZ=0 EndX=192.176 EndY=-3.18451 EndZ=0
    g22: LineSegment StartX=202.765 StartY=20.303 StartZ=0 EndX=195.887 EndY=39.2 EndZ=0
    g23: LineSegment StartX=195.887 StartY=39.2 StartZ=0 EndX=0 EndY=39.2 EndZ=0
    g24: LineSegment StartX=196.467 StartY=26.4942 StartZ=0 EndX=194.073 EndY=33.0721 EndZ=0
    g25: LineSegment StartX=194.073 StartY=33.0721 StartZ=0 EndX=189.939 EndY=31.5672 EndZ=0
    g26: LineSegment StartX=189.939 StartY=31.5672 StartZ=0 EndX=192.333 EndY=24.9893 EndZ=0
    g27: LineSegment StartX=192.333 StartY=24.9893 StartZ=0 EndX=196.467 EndY=26.4942 EndZ=0
    g28: LineSegment StartX=132.428 StartY=20 StartZ=0 EndX=144.053 EndY=20 EndZ=0
    g29: LineSegment StartX=144.053 StartY=20 StartZ=0 EndX=147.645 EndY=8.94427 EndZ=0
  constraints (65):
    c: Equal(g0,g-25)
    c: Equal(g2,g-29)
    c: Equal(g3,g-30)
    c: Equal(g4,g-28)
    c: Equal(g1,g-26)
    c: Coincident(g0,g-25)
    c: Coincident(g1,g-26)
    c: Coincident(g2,g-29)
    c: Coincident(g3,g-30)
    c: Coincident(g4,g-28)
    c: Equal(g5,g-23)
    c: Equal(g6,g-24)
    c: Coincident(g5,g-23)
    c: Coincident(g6,g-24)
    c: Equal(g7,g-20)
    c: Coincident(g7,g-20)
    c: Equal(g9,g-22)
    c: Coincident(g9,g-22)
    c: Equal(g8,g-21)
    c: Coincident(g8,g-21)
    c: Equal(g13,g-12)
    c: Equal(g12,g-14)
    c: Equal(g10,g-9)
    c: Equal(g11,g-7)
    c: Coincident(g14,g-27)
    c: Coincident(g14,g-27)
    c: Coincident(g15,g14)
    c: Coincident(g15,g-5)
    c: Coincident(g16,g15)
    c: Coincident(g16,g-6)
    c: Coincident(g17,g16)
    c: Coincident(g17,g-7)
    c: Coincident(g11,g17)
    c: Coincident(g11,g-8)
    c: Coincident(g18,g11)
    c: Coincident(g18,g-9)
    c: Coincident(g10,g18)
    c: Coincident(g10,g-10)
    c: Coincident(g19,g10)
    c: Coincident(g19,g-11)
    c: Coincident(g20,g19)
    c: Coincident(g20,g-12)
    c: Coincident(g13,g20)
    c: Coincident(g13,g-13)
    c: Coincident(g21,g13)
    c: Coincident(g21,g-14)
    c: Coincident(g12,g21)
    c: Coincident(g12,g-15)
    c: Coincident(g22,g12)
    c: Coincident(g22,g-15)
    c: Coincident(g23,g22)
    c: Coincident(g23,g14)
    c: Coincident(g24,g-18)
    c: Coincident(g24,g-16)
    c: Coincident(g25,g24)
    c: Coincident(g25,g-19)
    c: Coincident(g26,g25)
    c: Coincident(g26,g-19)
    c: Coincident(g27,g26)
    c: Coincident(g27,g24)
    c: Coincident(g29,g10)
    c: Coincident(g28,g10)
    c: Coincident(g29,g28)
    c: Parallel(g28,g18)
    c: Parallel(g29,g19)
FEATURE [PartDesign::Pad] Pad011
  Direction = (0,1,-2e-16)
  Length = 2
  Length2 = 10
  Profile = -> Sketch114
  ReferenceAxis = -> Sketch114 [N_Axis]
  Refine = true
  Reversed = true
  Suppressed = false
  Type = 0
FEATURE [Sketcher::SketchObject] Sketch115
  ArcFitTolerance = 1e-06
  AttachmentSupport = -> [Pad011]
  ExternalGeometry = -> [Binder001]
  FullyConstrained = true
  MakeInternals = false
  MapMode = 5
  Placement = pos=(0,1.7e-15,0) rot=(0,0.707107,0.707107;3.14159rad)
  sketch-geometry (4):
    g0: ArcOfCircle CenterX=24.2 CenterY=26.7 CenterZ=0 NormalX=0 NormalY=0 NormalZ=1 AngleXU=0 Radius=3 StartAngle=4.48384e-08 EndAngle=3.14159
    g1: ArcOfCircle CenterX=24.2 CenterY=15.7 CenterZ=0 NormalX=0 NormalY=0 NormalZ=1 AngleXU=0 Radius=3 StartAngle=3.14159 EndAngle=6.28318
    g2: LineSegment StartX=21.2 StartY=26.7 StartZ=0 EndX=21.2 EndY=15.7 EndZ=0
    g3: LineSegment StartX=27.2 StartY=26.7 StartZ=0 EndX=27.2 EndY=15.7 EndZ=0
  constraints (12):
    c: Equal(g1,g-4)
    c: Equal(g0,g-3)
    c: Coincident(g0,g-3)
    c: Coincident(g1,g-4)
    c: Vertical(g2)
    c: Vertical(g3)
    c: Tangent(g3,g-3)
    c: Tangent(g2,g-3)
    c: Coincident(g0,g2)
    c: Coincident(g0,g3)
    c: Coincident(g1,g2)
    c: Coincident(g3,g1)
FEATURE [Sketcher::SketchObject] Sketch117  label="Sketch117 - fori per inserto M3 x 3 x 4.5"
  ArcFitTolerance = 1e-06
  AttachmentSupport = -> [Pad011]
  ExternalGeometry = -> [Binder001]
  FullyConstrained = true
  MakeInternals = false
  MapMode = 5
  Placement = pos=(0,1.7e-15,0) rot=(0,0.707107,0.707107;3.14159rad)
  sketch-geometry (4):
    g0: Circle CenterX=43.2 CenterY=30.3 CenterZ=0 NormalX=0 NormalY=0 NormalZ=1 AngleXU=0 Radius=2.25
    g1: Circle CenterX=43.2 CenterY=12.1 CenterZ=0 NormalX=0 NormalY=0 NormalZ=1 AngleXU=0 Radius=2.25
    g2: Circle CenterX=18.6 CenterY=30.3 CenterZ=0 NormalX=0 NormalY=0 NormalZ=1 AngleXU=0 Radius=2.25
    g3: Circle CenterX=18.6 CenterY=12.1 CenterZ=0 NormalX=0 NormalY=0 NormalZ=1 AngleXU=0 Radius=2.25
  constraints (8):
    c: Diameter(g0) = 4.5
    c: Diameter(g1) = 4.5
    c: Diameter(g2) = 4.5
    c: Diameter(g3) = 4.5
    c: Coincident(g2,g-3)
    c: Coincident(g3,g-6)
    c: Coincident(g0,g-4)
    c: Coincident(g1,g-5)
FEATURE [Sketcher::SketchObject] Sketch118
  ArcFitTolerance = 1e-06
  AttachmentSupport = -> [Pad011]
  ExternalGeometry = -> [Binder001]
  FullyConstrained = true
  MakeInternals = false
  MapMode = 5
  Placement = pos=(0,-2,0) rot=(1,0,0;1.5708rad)
  sketch-geometry (12):
    g0: Circle CenterX=-78.51 CenterY=34.8 CenterZ=0 NormalX=0 NormalY=0 NormalZ=1 AngleXU=0 Radius=1.8
    g1: Circle CenterX=-78.51 CenterY=7.6 CenterZ=0 NormalX=0 NormalY=0 NormalZ=1 AngleXU=0 Radius=1.8
    g2: Circle CenterX=-5.6 CenterY=34.8 CenterZ=0 NormalX=0 NormalY=0 NormalZ=1 AngleXU=0 Radius=1.8
    g3: Circle CenterX=-5.6 CenterY=7.6 CenterZ=0 NormalX=0 NormalY=0 NormalZ=1 AngleXU=0 Radius=1.8
    g4: LineSegment StartX=0 StartY=39.2 StartZ=0 EndX=0 EndY=3.2 EndZ=0
    g5: LineSegment StartX=0 StartY=3.2 StartZ=0 EndX=-82.8 EndY=3.2 EndZ=0
    g6: LineSegment StartX=-82.8 StartY=3.2 StartZ=0 EndX=-82.8 EndY=39.2 EndZ=0
    g7: LineSegment StartX=-82.8 StartY=39.2 StartZ=0 EndX=0 EndY=39.2 EndZ=0
    g8: ArcOfCircle CenterX=-65 CenterY=21.2 CenterZ=0 NormalX=0 NormalY=0 NormalZ=1 AngleXU=0 Radius=10 StartAngle=1.5708 EndAngle=4.71239
    g9: ArcOfCircle CenterX=-19 CenterY=21.2 CenterZ=0 NormalX=0 NormalY=0 NormalZ=1 AngleXU=0 Radius=10 StartAngle=4.71239 EndAngle=7.85398
    g10: LineSegment StartX=-65 StartY=31.2 StartZ=0 EndX=-19 EndY=31.2 EndZ=0
    g11: LineSegment StartX=-65 StartY=11.2 StartZ=0 EndX=-19 EndY=11.2 EndZ=0
  constraints (25):
    c: Equal(g2,g-5)
    c: Equal(g3,g-7)
    c: Equal(g1,g-6)
    c: Equal(g0,g-4)
    c: Coincident(g0,g-4)
    c: Coincident(g1,g-6)
    c: Coincident(g3,g-7)
    c: Coincident(g2,g-5)
    c: Coincident(g4,g-8)
    c: Coincident(g4,g-9)
    c: Coincident(g5,g4)
    c: Coincident(g5,g-10)
    c: Coincident(g6,g5)
    c: PointOnObject(g6,g-3)
    c: Vertical(g6)
    c: Coincident(g7,g6)
    c: Coincident(g7,g4)
    c: Tangent(g8,g10) = 1.5708
    c: Tangent(g8,g11) = -1.5708
    c: Tangent(g9,g10) = 1.5708
    c: Tangent(g9,g11) = -1.5708
    c: Equal(g8,g9)
    c: Radius(g8) = 10
    c: Coincident(g8,g-11)
    c: Coincident(g9,g-12)
FEATURE [Sketcher::SketchObject] Sketch120
  ArcFitTolerance = 1e-06
  AttachmentSupport = -> [Pad011]
  ExternalGeometry = -> [Binder001]
  FullyConstrained = true
  MakeInternals = false
  MapMode = 5
  Placement = pos=(0,-2,0) rot=(1,0,0;1.5708rad)
  sketch-geometry (4):
    g0: LineSegment StartX=-137.815 StartY=39.2 StartZ=0 EndX=-142.655 EndY=24.303 EndZ=0
    g1: LineSegment StartX=-137.815 StartY=39.2 StartZ=0 EndX=-110.815 EndY=39.2 EndZ=0
    g2: LineSegment StartX=-142.655 StartY=24.303 StartZ=0 EndX=-110.815 EndY=24.303 EndZ=0
    g3: ArcOfCircle CenterX=-92.2534 CenterY=31.7515 CenterZ=0 NormalX=0 NormalY=0 NormalZ=1 AngleXU=0 Radius=20 StartAngle=2.75997 EndAngle=3.52321
  constraints (12):
    c: PointOnObject(g0,g-3)
    c: Coincident(g1,g0)
    c: PointOnObject(g1,g-3)
    c: Coincident(g2,g0)
    c: Horizontal(g2)
    c: Tangent(g0,g-4)
    c: Vertical(g2,g1)
    c: DistanceX(g1,g1) = 27
    c: DistanceY(g-6,g0) = 4
    c: Radius(g3) = 20
    c: Coincident(g3,g1)
    c: Coincident(g3,g2)
FEATURE [Sketcher::SketchObject] Sketch121
  ArcFitTolerance = 1e-06
  AttachmentSupport = -> [Pad011]
  ExternalGeometry = -> [Binder001]
  FullyConstrained = true
  MakeInternals = false
  MapMode = 5
  Placement = pos=(0,-2,0) rot=(1,0,0;1.5708rad)
  sketch-geometry (15):
    g0: LineSegment StartX=-137.815 StartY=39.2 StartZ=0 EndX=-143.955 EndY=20.303 EndZ=0
    g1: LineSegment StartX=-143.955 StartY=20.303 StartZ=0 EndX=-190.141 EndY=20.303 EndZ=0
    g2: LineSegment StartX=-190.141 StartY=20.303 StartZ=0 EndX=-186.139 EndY=31.3 EndZ=0
    g3: LineSegment StartX=-178.754 StartY=39.2 StartZ=0 EndX=-180.791 EndY=33.6029 EndZ=0
    g4: ArcOfCircle CenterX=-184.08 CenterY=34.8 CenterZ=0 NormalX=0 NormalY=0 NormalZ=1 AngleXU=0 Radius=3.5 StartAngle=4.71239 EndAngle=5.93412
    g5: LineSegment StartX=-184.08 StartY=31.3 StartZ=0 EndX=-186.139 EndY=31.3 EndZ=0
    g6: LineSegment StartX=-137.815 StartY=39.2 StartZ=0 EndX=-156.815 EndY=39.2 EndZ=0
    g7: LineSegment StartX=-168.815 StartY=39.2 StartZ=0 EndX=-178.754 EndY=39.2 EndZ=0
    g8: LineSegment StartX=-157.815 StartY=39.2 StartZ=0 EndX=-167.815 EndY=39.2 EndZ=0
    g9: LineSegment StartX=-168.815 StartY=31.2 StartZ=0 EndX=-156.815 EndY=31.2 EndZ=0
    g10: LineSegment StartX=-167.436 StartY=36.2 StartZ=0 EndX=-157.436 EndY=36.2 EndZ=0
    g11: ArcOfCircle CenterX=-176.411 CenterY=35.2 CenterZ=0 NormalX=0 NormalY=0 NormalZ=1 AngleXU=0 Radius=20 StartAngle=6.08183 EndAngle=6.48454
    g12: ArcOfCircle CenterX=-188.411 CenterY=35.2 CenterZ=0 NormalX=0 NormalY=0 NormalZ=1 AngleXU=0 Radius=20 StartAngle=6.08183 EndAngle=6.48454
    g13: ArcOfCircle CenterX=-177.411 CenterY=35.2 CenterZ=0 NormalX=0 NormalY=0 NormalZ=1 AngleXU=0 Radius=20 StartAngle=0.0500209 EndAngle=0.201358
    g14: ArcOfCircle CenterX=-187.411 CenterY=35.2 CenterZ=0 NormalX=0 NormalY=0 NormalZ=1 AngleXU=0 Radius=20 StartAngle=0.0500209 EndAngle=0.201358
  constraints (46):
    c: PointOnObject(g0,g-3)
    c: Tangent(g0,g-5)
    c: Coincident(g1,g0)
    c: Horizontal(g1)
    c: Coincident(g2,g1)
    c: PointOnObject(g3,g-3)
    c: Parallel(g3,g-6)
    c: Parallel(g2,g-6)
    c: Radius(g4) = 3.5
    c: Coincident(g4,g-7)
    c: Tangent(g3,g4) = 1.5708
    c: Horizontal(g5)
    c: Tangent(g5,g4) = 1.5708
    c: DistanceX(g-8,g5) = 3.8
    c: Coincident(g2,g5)
    c: Coincident(g6,g0)
    c: PointOnObject(g6,g-3)
    c: DistanceX(g6,g6) = 19
    c: PointOnObject(g7,g-3)
    c: DistanceX(g7,g6) = 12
    c: Coincident(g7,g3)
    c: PointOnObject(g8,g-3)
    c: PointOnObject(g8,g-3)
    c: DistanceX(g8,g8) = 10
    c: DistanceX(g8,g6) = 1
    c: Horizontal(g9)
    c: Vertical(g7,g9)
    c: Vertical(g6,g9)
    c: DistanceY(g9,g7) = 8
    c: Horizontal(g10)
    c: Equal(g8,g10)
    c: DistanceY(g10,g8) = 3
    c: Radius(g11) = 20
    c: Coincident(g11,g6)
    c: Coincident(g11,g9)
    c: Radius(g12) = 20
    c: Coincident(g12,g7)
    c: Coincident(g12,g9)
    c: Equal(g13,g11)
    c: Coincident(g13,g8)
    c: Coincident(g13,g10)
    c: Horizontal(g13,g11)
    c: Equal(g14,g12)
    c: Coincident(g14,g8)
    c: Coincident(g14,g10)
    c: Horizontal(g1,g-6)
FEATURE [Sketcher::SketchObject] Sketch122
  ArcFitTolerance = 1e-06
  AttachmentSupport = -> [Pad011]
  ExternalGeometry = -> [Binder001]
  FullyConstrained = true
  MakeInternals = false
  MapMode = 5
  Placement = pos=(0,-2,0) rot=(1,0,0;1.5708rad)
  sketch-geometry (8):
    g0: ArcOfCircle CenterX=-184.801 CenterY=-67.3089 CenterZ=0 NormalX=0 NormalY=0 NormalZ=1 AngleXU=0 Radius=33.7833 StartAngle=2.70526 EndAngle=3.54053
    g1: LineSegment StartX=-176.685 StartY=-80.4316 StartZ=0 EndX=-215.932 EndY=-80.4316 EndZ=0
    g2: LineSegment StartX=-215.42 StartY=-53.0314 StartZ=0 EndX=-192.176 EndY=-3.18454 EndZ=0
    g3: ArcOfCircle CenterX=-207.583 CenterY=4 CenterZ=0 NormalX=0 NormalY=0 NormalZ=1 AngleXU=0 Radius=17 StartAngle=5.84685 EndAngle=7.56663
    g4: Circle CenterX=-213.443 CenterY=-76.8316 CenterZ=0 NormalX=0 NormalY=0 NormalZ=1 AngleXU=0 Radius=3
    g5: Circle CenterX=-179.305 CenterY=-76.8316 CenterZ=0 NormalX=0 NormalY=0 NormalZ=1 AngleXU=0 Radius=3
    g6: LineSegment StartX=-143.955 StartY=20.303 StartZ=0 EndX=-176.685 EndY=-80.4316 EndZ=0
    g7: LineSegment StartX=-202.765 StartY=20.303 StartZ=0 EndX=-143.955 EndY=20.303 EndZ=0
  constraints (18):
    c: Coincident(g0,g-7)
    c: Coincident(g0,g-8)
    c: Coincident(g1,g0)
    c: Tangent(g2,g-5)
    c: Coincident(g3,g-6)
    c: Coincident(g2,g3)
    c: Coincident(g0,g2)
    c: Diameter(g4) = 6
    c: Diameter(g5) = 6
    c: Coincident(g4,g-9)
    c: Coincident(g5,g-10)
    c: Horizontal(g1)
    c: Coincident(g6,g1)
    c: Tangent(g6,g-4)
    c: Coincident(g3,g-6)
    c: Coincident(g7,g3)
    c: Horizontal(g7)
    c: Coincident(g7,g6)
FEATURE [Sketcher::SketchObject] Sketch123
  ArcFitTolerance = 1e-06
  AttachmentSupport = -> [Pad011]
  ExternalGeometry = -> [Binder001]
  FullyConstrained = true
  MakeInternals = false
  MapMode = 5
  Placement = pos=(0,-2,0) rot=(1,0,0;1.5708rad)
  sketch-geometry (4):
    g0: LineSegment StartX=-108 StartY=36.8 StartZ=0 EndX=-90 EndY=36.8 EndZ=0
    g1: LineSegment StartX=-108 StartY=36.8 StartZ=0 EndX=-108 EndY=26.8 EndZ=0
    g2: LineSegment StartX=-108 StartY=26.8 StartZ=0 EndX=-90 EndY=26.8 EndZ=0
    g3: ArcOfCircle CenterX=-94 CenterY=31.8 CenterZ=0 NormalX=0 NormalY=0 NormalZ=1 AngleXU=0 Radius=6.40312 StartAngle=5.38713 EndAngle=7.17924
  constraints (13):
    c: Horizontal(g0)
    c: Coincident(g1,g0)
    c: Vertical(g1)
    c: Coincident(g2,g1)
    c: Horizontal(g2)
    c: DistanceX(g0,g0) = 18
    c: DistanceY(g1,g1) = 10
    c: Equal(g0,g2)
    c: DistanceX(g0,g-3) = 90
    c: DistanceY(g0,g-3) = 2.4
    c: Coincident(g3,g0)
    c: Coincident(g3,g2)
    c: DistanceX(g3,g0) = 4
FEATURE [PartDesign::Chamfer] Chamfer014
  Angle = 45
  Base = -> Pad011 [Edge80,Edge4,Edge7]
  BaseFeature = -> Pad011
  ChamferType = 0
  FlipDirection = false
  Refine = true
  Size = 1.9
  Size2 = 1
  SupportTransform = false
  Suppressed = false
  UseAllEdges = false
FEATURE [PartDesign::Pocket] Pocket006
  BaseFeature = -> Chamfer014
  Direction = (0,-1,2e-16)
  Length = 1.2
  Length2 = 5
  Profile = -> Sketch115
  ReferenceAxis = -> Sketch115 [N_Axis]
  Refine = true
  Suppressed = false
  Type = 0
FEATURE [Sketcher::SketchObject] Sketch116  label="Sketch116 - pieno per inserto M3 x 3 x 4,5"
  ArcFitTolerance = 1e-06
  AttachmentSupport = -> [Pocket006]
  ExternalGeometry = -> [Binder001]
  FullyConstrained = true
  MakeInternals = false
  MapMode = 5
  Placement = pos=(0,1.7e-15,0) rot=(0,0.707107,0.707107;3.14159rad)
  sketch-geometry (4):
    g0: Circle CenterX=43.2 CenterY=30.3 CenterZ=0 NormalX=0 NormalY=0 NormalZ=1 AngleXU=0 Radius=3.4
    g1: Circle CenterX=43.2 CenterY=12.1 CenterZ=0 NormalX=0 NormalY=0 NormalZ=1 AngleXU=0 Radius=3.4
    g2: Circle CenterX=18.6 CenterY=30.3 CenterZ=0 NormalX=0 NormalY=0 NormalZ=1 AngleXU=0 Radius=3.4
    g3: Circle CenterX=18.6 CenterY=12.1 CenterZ=0 NormalX=0 NormalY=0 NormalZ=1 AngleXU=0 Radius=3.4
  constraints (8):
    c: Diameter(g0) = 6.8
    c: Diameter(g1) = 6.8
    c: Diameter(g2) = 6.8
    c: Diameter(g3) = 6.8
    c: Coincident(g2,g-3)
    c: Coincident(g0,g-4)
    c: Coincident(g3,g-6)
    c: Coincident(g1,g-5)
FEATURE [PartDesign::Pad] Pad012
  BaseFeature = -> Pocket006
  Direction = (0,1,-2e-16)
  Length = 2.4
  Length2 = 10
  Profile = -> Sketch116
  ReferenceAxis = -> Sketch116 [N_Axis]
  Refine = true
  Suppressed = false
  Type = 0
FEATURE [PartDesign::Pocket] Pocket007
  BaseFeature = -> Pad012
  Direction = (0,-1,2e-16)
  Length = 0.6
  Length2 = 2.4
  Profile = -> Sketch117
  ReferenceAxis = -> Sketch117 [N_Axis]
  Refine = true
  Suppressed = false
  Type = 4
FEATURE [PartDesign::Pad] Pad013
  BaseFeature = -> Pocket007
  Direction = (0,-1,2e-16)
  Length = 1.6
  Length2 = 10
  Profile = -> Sketch118
  ReferenceAxis = -> Sketch118 [N_Axis]
  Refine = true
  Suppressed = false
  Type = 0
FEATURE [Sketcher::SketchObject] Sketch119
  ArcFitTolerance = 1e-06
  AttachmentSupport = -> [Pad013]
  ExternalGeometry = -> [Binder001]
  FullyConstrained = true
  MakeInternals = false
  MapMode = 5
  Placement = pos=(0,-3.6,0) rot=(1,0,0;1.5708rad)
  sketch-geometry (21):
    g0: LineSegment [constr] StartX=-82.8 StartY=3.2 StartZ=0 EndX=-82.8 EndY=39.2 EndZ=0
    g1: ArcOfCircle CenterX=-78.51 CenterY=34.8 CenterZ=0 NormalX=0 NormalY=0 NormalZ=1 AngleXU=0 Radius=3.5 StartAngle=4.71239 EndAngle=6.28319
    g2: ArcOfCircle CenterX=-78.51 CenterY=7.6 CenterZ=0 NormalX=0 NormalY=0 NormalZ=1 AngleXU=0 Radius=3.5 StartAngle=0 EndAngle=1.5708
    g3: ArcOfCircle CenterX=-5.6 CenterY=34.8 CenterZ=0 NormalX=0 NormalY=0 NormalZ=1 AngleXU=0 Radius=3.5 StartAngle=3.14159 EndAngle=4.71239
    g4: ArcOfCircle CenterX=-5.6 CenterY=7.6 CenterZ=0 NormalX=0 NormalY=0 NormalZ=1 AngleXU=0 Radius=3.5 StartAngle=1.5708 EndAngle=3.14159
    g5: LineSegment StartX=0 StartY=39.2 StartZ=0 EndX=0 EndY=31.3 EndZ=0
    g6: LineSegment StartX=0 StartY=39.2 StartZ=0 EndX=-9.1 EndY=39.2 EndZ=0
    g7: LineSegment StartX=0 StartY=3.2 StartZ=0 EndX=0 EndY=11.1 EndZ=0
    g8: LineSegment StartX=0 StartY=3.2 StartZ=0 EndX=-9.1 EndY=3.2 EndZ=0
    g9: LineSegment StartX=-82.8 StartY=3.2 StartZ=0 EndX=-75.01 EndY=3.2 EndZ=0
    g10: LineSegment StartX=-82.8 StartY=3.2 StartZ=0 EndX=-82.8 EndY=11.1 EndZ=0
    g11: LineSegment StartX=-82.8 StartY=39.2 StartZ=0 EndX=-82.8 EndY=31.3 EndZ=0
    g12: LineSegment StartX=-82.8 StartY=39.2 StartZ=0 EndX=-75.01 EndY=39.2 EndZ=0
    g13: LineSegment StartX=-82.8 StartY=31.3 StartZ=0 EndX=-78.51 EndY=31.3 EndZ=0
    g14: LineSegment StartX=-75.01 StartY=39.2 StartZ=0 EndX=-75.01 EndY=34.8 EndZ=0
    g15: LineSegment StartX=-82.8 StartY=11.1 StartZ=0 EndX=-78.51 EndY=11.1 EndZ=0
    g16: LineSegment StartX=-75.01 StartY=3.2 StartZ=0 EndX=-75.01 EndY=7.6 EndZ=0
    g17: LineSegment StartX=-9.1 StartY=39.2 StartZ=0 EndX=-9.1 EndY=34.8 EndZ=0
    g18: LineSegment StartX=0 StartY=31.3 StartZ=0 EndX=-5.6 EndY=31.3 EndZ=0
    g19: LineSegment StartX=0 StartY=11.1 StartZ=0 EndX=-5.6 EndY=11.1 EndZ=0
    g20: LineSegment StartX=-9.1 StartY=3.2 StartZ=0 EndX=-9.1 EndY=7.6 EndZ=0
  constraints (51):
    c: Coincident(g0,g-10)
    c: PointOnObject(g0,g-8)
    c: Vertical(g0)
    c: Coincident(g1,g-3)
    c: Coincident(g2,g-4)
    c: Coincident(g3,g-5)
    c: Coincident(g4,g-6)
    c: Radius(g4) = 3.5
    c: Radius(g3) = 3.5
    c: Radius(g1) = 3.5
    c: Radius(g2) = 3.5
    c: Coincident(g5,g-9)
    c: PointOnObject(g5,g-9)
    c: Coincident(g6,g5)
    c: PointOnObject(g6,g-8)
    c: Coincident(g7,g-9)
    c: PointOnObject(g7,g-9)
    c: Coincident(g8,g7)
    c: PointOnObject(g8,g-7)
    c: Coincident(g9,g0)
    c: PointOnObject(g9,g-7)
    c: Coincident(g10,g0)
    c: PointOnObject(g10,g0)
    c: Coincident(g11,g0)
    c: PointOnObject(g11,g0)
    c: Coincident(g12,g0)
    c: PointOnObject(g12,g-8)
    c: Coincident(g13,g11)
    c: Horizontal(g13)
    c: Coincident(g14,g12)
    c: Vertical(g14)
    c: Coincident(g15,g10)
    c: Horizontal(g15)
    c: Coincident(g16,g9)
    c: Vertical(g16)
    c: Coincident(g17,g6)
    c: Vertical(g17)
    c: Coincident(g18,g5)
    c: Horizontal(g18)
    c: Coincident(g19,g7)
    c: Horizontal(g19)
    c: Coincident(g20,g8)
    c: Vertical(g20)
    c: Tangent(g20,g4) = 1.5708
    c: Tangent(g4,g19) = -1.5708
    c: Tangent(g18,g3) = 1.5708
    c: Tangent(g3,g17) = -1.5708
    c: Tangent(g13,g1) = -1.5708
    c: Tangent(g1,g14) = 1.5708
    c: Tangent(g16,g2) = -1.5708
    c: Tangent(g2,g15) = 1.5708
FEATURE [PartDesign::Pocket] Pocket008
  BaseFeature = -> Pad013
  Direction = (0,1,-2e-16)
  Length = 1.6
  Length2 = 5
  Profile = -> Sketch119
  ReferenceAxis = -> Sketch119 [N_Axis]
  Refine = true
  Suppressed = false
  Type = 0
FEATURE [PartDesign::Pad] Pad017
  BaseFeature = -> Pocket008
  Direction = (0,-1,2e-16)
  Length = 1.6
  Length2 = 10
  Profile = -> Sketch123
  ReferenceAxis = -> Sketch123 [N_Axis]
  Refine = true
  Suppressed = false
  Type = 0
FEATURE [Sketcher::SketchObject] Sketch125
  ArcFitTolerance = 1e-06
  AttachmentSupport = -> [Pad017]
  ExternalGeometry = -> [Pad017]
  FullyConstrained = true
  MakeInternals = false
  MapMode = 5
  Placement = pos=(0,-3.6,8e-16) rot=(1,0,0;1.5708rad)
  sketch-geometry (20):
    g0: LineSegment StartX=-108 StartY=35.8 StartZ=0 EndX=-108 EndY=35 EndZ=0
    g1: LineSegment StartX=-108 StartY=35 StartZ=0 EndX=-97 EndY=35 EndZ=0
    g2: LineSegment StartX=-97 StartY=35 StartZ=0 EndX=-97 EndY=35.8 EndZ=0
    g3: LineSegment StartX=-97 StartY=35.8 StartZ=0 EndX=-108 EndY=35.8 EndZ=0
    g4: LineSegment StartX=-108 StartY=28.6 StartZ=0 EndX=-108 EndY=27.8 EndZ=0
    g5: LineSegment StartX=-108 StartY=27.8 StartZ=0 EndX=-97 EndY=27.8 EndZ=0
    g6: LineSegment StartX=-97 StartY=27.8 StartZ=0 EndX=-97 EndY=28.6 EndZ=0
    g7: LineSegment StartX=-97 StartY=28.6 StartZ=0 EndX=-108 EndY=28.6 EndZ=0
    g8: LineSegment StartX=-108 StartY=30.4 StartZ=0 EndX=-108 EndY=29.6 EndZ=0
    g9: LineSegment StartX=-108 StartY=29.6 StartZ=0 EndX=-97 EndY=29.6 EndZ=0
    g10: LineSegment StartX=-97 StartY=29.6 StartZ=0 EndX=-97 EndY=30.4 EndZ=0
    g11: LineSegment StartX=-97 StartY=30.4 StartZ=0 EndX=-108 EndY=30.4 EndZ=0
    g12: LineSegment StartX=-108 StartY=32.2 StartZ=0 EndX=-108 EndY=31.4 EndZ=0
    g13: LineSegment StartX=-108 StartY=31.4 StartZ=0 EndX=-97 EndY=31.4 EndZ=0
    g14: LineSegment StartX=-97 StartY=31.4 StartZ=0 EndX=-97 EndY=32.2 EndZ=0
    g15: LineSegment StartX=-97 StartY=32.2 StartZ=0 EndX=-108 EndY=32.2 EndZ=0
    g16: LineSegment StartX=-108 StartY=34 StartZ=0 EndX=-108 EndY=33.2 EndZ=0
    g17: LineSegment StartX=-108 StartY=33.2 StartZ=0 EndX=-97 EndY=33.2 EndZ=0
    g18: LineSegment StartX=-97 StartY=33.2 StartZ=0 EndX=-97 EndY=34 EndZ=0
    g19: LineSegment StartX=-97 StartY=34 StartZ=0 EndX=-108 EndY=34 EndZ=0
  constraints (55):
    c: Coincident(g1,g0)
    c: Horizontal(g1)
    c: Coincident(g2,g1)
    c: Vertical(g2)
    c: Coincident(g3,g2)
    c: Horizontal(g3)
    c: Coincident(g3,g0)
    c: DistanceX(g1,g1) = 11
    c: DistanceY(g2,g2) = 0.8
    c: Coincident(g5,g4)
    c: Horizontal(g5)
    c: Coincident(g6,g5)
    c: Vertical(g6)
    c: Coincident(g7,g6)
    c: Horizontal(g7)
    c: Coincident(g7,g4)
    c: Coincident(g9,g8)
    c: Horizontal(g9)
    c: Coincident(g10,g9)
    c: Vertical(g10)
    c: Coincident(g11,g10)
    c: Horizontal(g11)
    c: Coincident(g11,g8)
    c: Coincident(g13,g12)
    c: Horizontal(g13)
    c: Coincident(g14,g13)
    c: Vertical(g14)
    c: Coincident(g15,g14)
    c: Horizontal(g15)
    c: Coincident(g15,g12)
    c: Coincident(g17,g16)
    c: Horizontal(g17)
    c: Coincident(g18,g17)
    c: Vertical(g18)
    c: Coincident(g19,g18)
    c: Horizontal(g19)
    c: Coincident(g19,g16)
    c: Equal(g3,g19)
    c: Equal(g3,g15)
    c: Equal(g3,g11)
    c: Equal(g3,g7)
    c: Equal(g2,g18)
    c: Equal(g2,g14)
    c: Equal(g2,g10)
    c: Equal(g2,g6)
    c: DistanceY(g-4,g4) = 1
    c: DistanceY(g4,g8) = 1
    c: DistanceY(g8,g12) = 1
    c: DistanceY(g12,g16) = 1
    c: DistanceY(g16,g0) = 1
    c: Tangent(g0,g-5)
    c: Tangent(g16,g-5)
    c: Tangent(g12,g-5)
    c: Tangent(g8,g-5)
    c: Tangent(g4,g-5)
FEATURE [PartDesign::Chamfer] Chamfer009
  Angle = 45
  Base = -> Pad017 [Edge151,Edge154]
  BaseFeature = -> Pad017
  ChamferType = 1
  FlipDirection = false
  Refine = true
  Size = 1.5
  Size2 = 2.8
  SupportTransform = false
  Suppressed = false
  UseAllEdges = false
FEATURE [PartDesign::Pocket] Pocket009
  BaseFeature = -> Chamfer009
  Direction = (0,1,-2e-16)
  Length = 1
  Length2 = 5
  Profile = -> Sketch125
  ReferenceAxis = -> Sketch125 [N_Axis]
  Refine = true
  Suppressed = false
  Type = 0
FEATURE [PartDesign::Pad] Pad014
  BaseFeature = -> Pocket009
  Direction = (0,-1,2e-16)
  Length = 0.8
  Length2 = 10
  Profile = -> Sketch120
  ReferenceAxis = -> Sketch120 [N_Axis]
  Refine = true
  Suppressed = false
  Type = 0
FEATURE [Sketcher::SketchObject] Sketch124
  ArcFitTolerance = 1e-06
  AttachmentSupport = -> [Pad014]
  ExternalGeometry = -> [Binder001]
  FullyConstrained = true
  MakeInternals = false
  MapMode = 5
  Placement = pos=(0,-2.8,6e-16) rot=(1,0,0;1.5708rad)
  sketch-geometry (4):
    g0: LineSegment StartX=-129 StartY=39.2 StartZ=0 EndX=-131.599 EndY=31.2 EndZ=0
    g1: LineSegment StartX=-118 StartY=39.2 StartZ=0 EndX=-120.599 EndY=31.2 EndZ=0
    g2: LineSegment StartX=-129 StartY=39.2 StartZ=0 EndX=-118 EndY=39.2 EndZ=0
    g3: LineSegment StartX=-120.599 StartY=31.2 StartZ=0 EndX=-131.599 EndY=31.2 EndZ=0
  constraints (12):
    c: PointOnObject(g0,g-3)
    c: PointOnObject(g1,g-3)
    c: Parallel(g-4,g0)
    c: Parallel(g-4,g1)
    c: Coincident(g2,g0)
    c: Coincident(g2,g1)
    c: DistanceX(g2,g2) = 11
    c: DistanceY(g1,g1) = 8
    c: Coincident(g3,g1)
    c: Horizontal(g3)
    c: Coincident(g3,g0)
    c: DistanceX(g1,g-3) = 118
FEATURE [PartDesign::Pad] Pad018
  BaseFeature = -> Pad014
  Direction = (0,-1,2e-16)
  Length = 1.2
  Length2 = 10
  Profile = -> Sketch124
  ReferenceAxis = -> Sketch124 [N_Axis]
  Refine = true
  Suppressed = false
  Type = 0
FEATURE [Sketcher::SketchObject] Sketch126
  ArcFitTolerance = 1e-06
  AttachmentSupport = -> [Pad018]
  ExternalGeometry = -> [Pad018]
  FullyConstrained = true
  MakeInternals = false
  MapMode = 5
  Placement = pos=(0,-4,0) rot=(1,0,0;1.5708rad)
  sketch-geometry (8):
    g0: LineSegment StartX=-129.877 StartY=36.5 StartZ=0 EndX=-130.137 EndY=35.7 EndZ=0
    g1: LineSegment StartX=-130.69 StartY=34 StartZ=0 EndX=-130.95 EndY=33.2 EndZ=0
    g2: LineSegment StartX=-129.877 StartY=36.5 StartZ=0 EndX=-118.877 EndY=36.5 EndZ=0
    g3: LineSegment StartX=-130.137 StartY=35.7 StartZ=0 EndX=-119.137 EndY=35.7 EndZ=0
    g4: LineSegment StartX=-130.69 StartY=34 StartZ=0 EndX=-119.69 EndY=34 EndZ=0
    g5: LineSegment StartX=-130.95 StartY=33.2 StartZ=0 EndX=-119.95 EndY=33.2 EndZ=0
    g6: LineSegment StartX=-118.877 StartY=36.5 StartZ=0 EndX=-119.137 EndY=35.7 EndZ=0
    g7: LineSegment StartX=-119.69 StartY=34 StartZ=0 EndX=-119.95 EndY=33.2 EndZ=0
  constraints (20):
    c: Coincident(g2,g0)
    c: Horizontal(g2)
    c: Coincident(g3,g0)
    c: Horizontal(g3)
    c: Coincident(g4,g1)
    c: Horizontal(g4)
    c: Coincident(g5,g1)
    c: Horizontal(g5)
    c: Coincident(g6,g2)
    c: Coincident(g6,g3)
    c: Coincident(g7,g4)
    c: Coincident(g7,g5)
    c: Tangent(g0,g-4)
    c: Tangent(g6,g-5)
    c: Tangent(g1,g-4)
    c: Tangent(g7,g-5)
    c: DistanceY(g3,g2) = 0.8
    c: DistanceY(g5,g4) = 0.8
    c: DistanceY(g-6,g1) = 2
    c: DistanceY(g-6,g0) = 4.5
FEATURE [PartDesign::Chamfer] Chamfer008
  Angle = 45
  Base = -> Pad018 [Edge257]
  BaseFeature = -> Pad018
  ChamferType = 1
  FlipDirection = false
  Refine = true
  Size = 1
  Size2 = 6
  SupportTransform = false
  Suppressed = false
  UseAllEdges = false
FEATURE [PartDesign::Pocket] Pocket010
  BaseFeature = -> Chamfer008
  Direction = (0,1,-2e-16)
  Length = 1
  Length2 = 5
  Profile = -> Sketch126
  ReferenceAxis = -> Sketch126 [N_Axis]
  Refine = true
  Suppressed = false
  Type = 0
FEATURE [PartDesign::Pad] Pad015
  BaseFeature = -> Pocket010
  Direction = (0,-1,2e-16)
  Length = 2
  Length2 = 10
  Profile = -> Sketch121
  ReferenceAxis = -> Sketch121 [N_Axis]
  Refine = true
  Suppressed = false
  Type = 0
FEATURE [PartDesign::Pad] Pad016
  BaseFeature = -> Pad015
  Direction = (0,-1,2e-16)
  Length = 1.6
  Length2 = 10
  Profile = -> Sketch122
  ReferenceAxis = -> Sketch122 [N_Axis]
  Refine = true
  Suppressed = false
  Type = 0
FEATURE [Sketcher::SketchObject] Sketch129
  ArcFitTolerance = 1e-06
  AttachmentSupport = -> [Pad016]
  ExternalGeometry = -> [Binder001]
  FullyConstrained = true
  MakeInternals = false
  MapMode = 5
  Placement = pos=(0,-3.6,0) rot=(1,0,0;1.5708rad)
  sketch-geometry (12):
    g0: LineSegment [constr] StartX=-192.176 StartY=-3.18451 StartZ=0 EndX=-181.223 EndY=20.303 EndZ=0
    g1: LineSegment [constr] StartX=-202.765 StartY=20.303 StartZ=0 EndX=-181.223 EndY=20.303 EndZ=0
    g2: LineSegment StartX=-202.765 StartY=20.303 StartZ=0 EndX=-181.223 EndY=20.303 EndZ=0
    g3: LineSegment StartX=-192.176 StartY=-3.18451 StartZ=0 EndX=-196.804 EndY=-13.1107 EndZ=0
    g4: ArcOfCircle CenterX=-207.583 CenterY=4 CenterZ=0 NormalX=0 NormalY=0 NormalZ=1 AngleXU=0 Radius=17 StartAngle=5.84685 EndAngle=7.56663
    g5: ArcOfEllipse CenterX=-181.223 CenterY=8.55923 CenterZ=0 NormalX=0 NormalY=0 NormalZ=1 MajorRadius=23.4779 MinorRadius=11.7437 AngleXU=2e-16 StartAngle=4.71239 EndAngle=7.85398
    g6: LineSegment [constr] StartX=-157.745 StartY=8.55923 StartZ=0 EndX=-204.701 EndY=8.55923 EndZ=0
    g7: LineSegment [constr] StartX=-181.223 StartY=20.303 StartZ=0 EndX=-181.223 EndY=-3.18451 EndZ=0
    g8: GeomPoint [constr] X=-160.894 Y=8.55923 Z=0
    g9: GeomPoint [constr] X=-201.553 Y=8.55923 Z=0
    g10: ArcOfCircle CenterX=-181.223 CenterY=-20.3763 CenterZ=0 NormalX=0 NormalY=0 NormalZ=1 AngleXU=0 Radius=17.1918 StartAngle=1.57079 EndAngle=2.70526
    g11: GeomPoint [constr] X=-181.223 Y=-3.18451 Z=0
  constraints (23):
    c: Coincident(g0,g-5)
    c: Coincident(g1,g-6)
    c: Horizontal(g1)
    c: Coincident(g1,g0)
    c: Parallel(g0,g-4)
    c: Coincident(g2,g1)
    c: Coincident(g2,g0)
    c: Coincident(g3,g0)
    c: Equal(g4,g-5)
    c: Coincident(g4,g1)
    c: Coincident(g4,g0)
    c: InternalAlignment(g6-g9 -> g5) x4
    c: Vertical(g5,g0)
    c: Horizontal(g6)
    c: Coincident(g5,g0)
    c: DistanceX(g6,g-3) = 10.1
    c: Tangent(g10,g3) = -1.5708
    c: PointOnObject(g11,g10)
    c: Tangent(g5,g10,g11) = 1.5708
    c: Coincident(g10,g5)
    c: Coincident(g11,g7)
    c: Parallel(g3,g-4)
    c: Horizontal(g5,g0)
FEATURE [Sketcher::SketchObject] Sketch130
  ArcFitTolerance = 1e-06
  AttachmentOffset = pos=(0,0,-1.6) rot=(0,0,1;0rad)
  AttachmentSupport = -> [Pad016]
  ExternalGeometry = -> [Binder001]
  FullyConstrained = true
  MakeInternals = false
  MapMode = 5
  Placement = pos=(0,-2,-4e-16) rot=(1,0,0;1.5708rad)
  sketch-geometry (12):
    g0: LineSegment [constr] StartX=-192.176 StartY=-3.18451 StartZ=0 EndX=-181.223 EndY=20.303 EndZ=0
    g1: LineSegment [constr] StartX=-202.765 StartY=20.303 StartZ=0 EndX=-181.223 EndY=20.303 EndZ=0
    g2: LineSegment StartX=-202.765 StartY=20.303 StartZ=0 EndX=-181.223 EndY=20.303 EndZ=0
    g3: LineSegment StartX=-192.176 StartY=-3.18451 StartZ=0 EndX=-193.827 EndY=-6.72678 EndZ=0
    g4: ArcOfCircle CenterX=-207.583 CenterY=4 CenterZ=0 NormalX=0 NormalY=0 NormalZ=1 AngleXU=0 Radius=17 StartAngle=5.84685 EndAngle=7.56663
    g5: ArcOfEllipse CenterX=-181.223 CenterY=10.803 CenterZ=0 NormalX=0 NormalY=0 NormalZ=1 MajorRadius=14.4779 MinorRadius=9.5 AngleXU=0 StartAngle=4.71239 EndAngle=7.85398
    g6: LineSegment [constr] StartX=-166.745 StartY=10.803 StartZ=0 EndX=-195.701 EndY=10.803 EndZ=0
    g7: LineSegment [constr] StartX=-181.223 StartY=20.303 StartZ=0 EndX=-181.223 EndY=1.30297 EndZ=0
    g8: GeomPoint [constr] X=-170.298 Y=10.803 Z=0
    g9: GeomPoint [constr] X=-192.148 Y=10.803 Z=0
    g10: ArcOfCircle CenterX=-181.223 CenterY=-12.6042 CenterZ=0 NormalX=0 NormalY=0 NormalZ=1 AngleXU=0 Radius=13.9072 StartAngle=1.5708 EndAngle=2.70526
    g11: GeomPoint [constr] X=-181.223 Y=1.30297 Z=0
  constraints (23):
    c: Coincident(g0,g-5)
    c: Coincident(g1,g-6)
    c: Horizontal(g1)
    c: Coincident(g1,g0)
    c: Parallel(g0,g-4)
    c: Coincident(g2,g1)
    c: Coincident(g2,g0)
    c: Coincident(g3,g0)
    c: Equal(g4,g-5)
    c: Coincident(g4,g1)
    c: Coincident(g4,g0)
    c: InternalAlignment(g6-g9 -> g5) x4
    c: Vertical(g5,g0)
    c: Horizontal(g6)
    c: Coincident(g5,g0)
    c: DistanceX(g6,g-3) = 19.1
    c: Tangent(g10,g3) = -1.5708
    c: PointOnObject(g11,g10)
    c: Tangent(g5,g10,g11) = 1.5708
    c: Coincident(g10,g5)
    c: Coincident(g11,g7)
    c: Parallel(g3,g-4)
    c: DistanceY(g5,g0) = 19
FEATURE [Part::Part2DObjectPython] Clone2D001  label="Sketch130 (2D)"  # Draft 2D object (typed FeaturePython)
  Fuse = false
  Objects = -> [Sketch130]
  Placement = pos=(0,-2,-4e-16) rot=(1,0,0;1.5708rad)
  Scale = (1,1,1)
FEATURE [Sketcher::SketchObject] Sketch131
  ArcFitTolerance = 1e-06
  AttachmentOffset = pos=(0,0,-3.5) rot=(0,0,1;0rad)
  AttachmentSupport = -> [Pad016]
  ExternalGeometry = -> [Binder001]
  FullyConstrained = true
  MakeInternals = false
  MapMode = 5
  Placement = pos=(0,-0.1,-8e-16) rot=(1,0,0;1.5708rad)
  sketch-geometry (1):
    g0: GeomPoint X=-197.47 Y=8.55923 Z=0
  constraints (1):
    c: Symmetric(g-6,g-4,g0)
FEATURE [Sketcher::SketchObject] Sketch132
  ArcFitTolerance = 1e-06
  AttachmentSupport = -> [Pad016]
  ExternalGeometry = -> [Binder001]
  FullyConstrained = true
  MakeInternals = false
  MapMode = 5
  Placement = pos=(0,-3.6,0) rot=(1,0,0;1.5708rad)
  sketch-geometry (3):
    g0: LineSegment [constr] StartX=-215.42 StartY=-53.0314 StartZ=0 EndX=-167.782 EndY=-53.0314 EndZ=0
    g1: Circle CenterX=-191.282 CenterY=-53.0314 CenterZ=0 NormalX=0 NormalY=0 NormalZ=1 AngleXU=0 Radius=11.5
    g2: Circle CenterX=-191.282 CenterY=-53.0314 CenterZ=0 NormalX=0 NormalY=0 NormalZ=1 AngleXU=0 Radius=10.7
  constraints (8):
    c: Coincident(g0,g-3)
    c: PointOnObject(g0,g-4)
    c: Horizontal(g0)
    c: Diameter(g1) = 23
    c: PointOnObject(g1,g0)
    c: DistanceX(g1,g0) = 23.5
    c: Diameter(g2) = 21.4
    c: Coincident(g2,g1)
FEATURE [Part::Part2DObjectPython] ShapeString  # Draft 2D object (typed FeaturePython)
  FontFile = <path>
  Fuse = false
  Justification = 6
  JustificationReference = 0
  KeepLeftMargin = false
  MakeFace = true
  ObliqueAngle = 0
  Placement = pos=(-199,-3.6,-57.5) rot=(1,0,0;1.5708rad)
  ScaleToSize = true
  Size = 10
  String = AS
  Tracking = 0
FEATURE [Sketcher::SketchObject] Sketch133
  ArcFitTolerance = 1e-06
  AttachmentSupport = -> [Binder]
  ExternalGeometry = -> [Binder]
  FullyConstrained = true
  MakeInternals = false
  MapMode = 5
  Placement = pos=(0,9e-16,0) rot=(0,0.707107,0.707107;3.14159rad)
  sketch-geometry (30):
    g0: LineSegment StartX=0 StartY=39.2 StartZ=0 EndX=0 EndY=3.2 EndZ=0
    g1: LineSegment StartX=0 StartY=3.2 StartZ=0 EndX=82.8 EndY=3.2 EndZ=0
    g2: LineSegment StartX=82.8 StartY=3.2 StartZ=0 EndX=82.8 EndY=6.2 EndZ=0
    g3: LineSegment StartX=82.8 StartY=6.2 StartZ=0 EndX=91.752 EndY=6.2 EndZ=0
    g4: LineSegment StartX=0 StartY=39.2 StartZ=0 EndX=195.887 EndY=39.2 EndZ=0
    g5: LineSegment StartX=195.887 StartY=39.2 StartZ=0 EndX=202.765 EndY=20.303 EndZ=0
    g6: LineSegment StartX=192.333 StartY=24.9893 StartZ=0 EndX=196.467 EndY=26.4942 EndZ=0
    g7: LineSegment StartX=196.467 StartY=26.4942 StartZ=0 EndX=194.073 EndY=33.0721 EndZ=0
    g8: LineSegment StartX=194.073 StartY=33.0721 StartZ=0 EndX=189.939 EndY=31.5672 EndZ=0
    g9: LineSegment StartX=189.939 StartY=31.5672 StartZ=0 EndX=192.333 EndY=24.9893 EndZ=0
    g10: ArcOfCircle CenterX=107.6 CenterY=4 CenterZ=0 NormalX=0 NormalY=0 NormalZ=1 AngleXU=0 Radius=16 StartAngle=1.5708 EndAngle=3.00366
    g11: LineSegment StartX=107.6 StartY=20 StartZ=0 EndX=132.428 EndY=20 EndZ=0
    g12: ArcOfCircle [constr] CenterX=132.428 CenterY=4 CenterZ=0 NormalX=0 NormalY=0 NormalZ=1 AngleXU=0 Radius=16 StartAngle=0.314159 EndAngle=1.5708
    g13: LineSegment StartX=147.645 StartY=8.94427 StartZ=0 EndX=176.685 EndY=-80.4316 EndZ=0
    g14: LineSegment StartX=176.685 StartY=-80.4316 StartZ=0 EndX=215.932 EndY=-80.4316 EndZ=0
    g15: ArcOfCircle CenterX=207.583 CenterY=4 CenterZ=0 NormalX=0 NormalY=0 NormalZ=1 AngleXU=0 Radius=17 StartAngle=1.85815 EndAngle=3.57792
    g16: ArcOfCircle CenterX=184.801 CenterY=-67.3089 CenterZ=0 NormalX=0 NormalY=0 NormalZ=1 AngleXU=0 Radius=33.7833 StartAngle=5.88425 EndAngle=6.71952
    g17: LineSegment StartX=192.176 StartY=-3.18451 StartZ=0 EndX=215.42 EndY=-53.0314 EndZ=0
    g18: Circle CenterX=5.6 CenterY=34.8 CenterZ=0 NormalX=0 NormalY=0 NormalZ=1 AngleXU=0 Radius=1.8
    g19: Circle CenterX=5.6 CenterY=7.6 CenterZ=0 NormalX=0 NormalY=0 NormalZ=1 AngleXU=0 Radius=1.8
    g20: Circle CenterX=78.51 CenterY=34.8 CenterZ=0 NormalX=0 NormalY=0 NormalZ=1 AngleXU=0 Radius=1.8
    g21: Circle CenterX=78.51 CenterY=7.6 CenterZ=0 NormalX=0 NormalY=0 NormalZ=1 AngleXU=0 Radius=1.8
    g22: Circle CenterX=184.08 CenterY=34.8 CenterZ=0 NormalX=0 NormalY=0 NormalZ=1 AngleXU=0 Radius=1.8
    g23: Circle CenterX=179.305 CenterY=-76.8316 CenterZ=0 NormalX=0 NormalY=0 NormalZ=1 AngleXU=0 Radius=1.8
    g24: Circle CenterX=213.443 CenterY=-76.8316 CenterZ=0 NormalX=0 NormalY=0 NormalZ=1 AngleXU=0 Radius=1.8
    g25: Circle CenterX=19 CenterY=21.2 CenterZ=0 NormalX=0 NormalY=0 NormalZ=1 AngleXU=0 Radius=6.3
    g26: Circle CenterX=42 CenterY=21.2 CenterZ=0 NormalX=0 NormalY=0 NormalZ=1 AngleXU=0 Radius=6.3
    g27: Circle CenterX=65 CenterY=21.2 CenterZ=0 NormalX=0 NormalY=0 NormalZ=1 AngleXU=0 Radius=6.3
    g28: LineSegment StartX=132.428 StartY=20 StartZ=0 EndX=144.053 EndY=20 EndZ=0
    g29: LineSegment StartX=147.645 StartY=8.94427 StartZ=0 EndX=144.053 EndY=20 EndZ=0
  constraints (65):
    c: Coincident(g0,g-4)
    c: Coincident(g0,g-5)
    c: Coincident(g1,g0)
    c: Coincident(g1,g-6)
    c: Coincident(g2,g1)
    c: Coincident(g2,g-7)
    c: Coincident(g3,g2)
    c: Coincident(g3,g-8)
    c: Coincident(g4,g0)
    c: Coincident(g4,g-16)
    c: Coincident(g5,g4)
    c: Coincident(g5,g-16)
    c: Coincident(g6,g-20)
    c: Coincident(g6,g-21)
    c: Coincident(g7,g6)
    c: Coincident(g7,g-23)
    c: Coincident(g8,g7)
    c: Coincident(g8,g-22)
    c: Coincident(g9,g8)
    c: Coincident(g9,g6)
    c: Equal(g10,g-8)
    c: Coincident(g10,g3)
    c: Coincident(g10,g-9)
    c: Coincident(g11,g10)
    c: Coincident(g11,g-10)
    c: Equal(g12,g-10)
    c: Coincident(g12,g11)
    c: Coincident(g12,g-11)
    c: Coincident(g13,g12)
    c: Coincident(g13,g-12)
    c: Coincident(g14,g13)
    c: Coincident(g14,g-13)
    c: Equal(g15,g-15)
    c: Coincident(g15,g5)
    c: Coincident(g15,g-15)
    c: Equal(g16,g-13)
    c: Coincident(g16,g14)
    c: Coincident(g16,g-14)
    c: Coincident(g17,g15)
    c: Coincident(g17,g16)
    c: Equal(g18,g-28)
    c: Equal(g19,g-29)
    c: Equal(g20,g-26)
    c: Equal(g21,g-27)
    c: Equal(g22,g-17)
    c: Equal(g24,g-25)
    c: Equal(g23,g-24)
    c: Coincident(g23,g-24)
    c: Coincident(g24,g-25)
    c: Coincident(g22,g-17)
    c: Coincident(g20,g-26)
    c: Coincident(g21,g-27)
    c: Coincident(g18,g-28)
    c: Coincident(g19,g-29)
    c: Equal(g25,g-30)
    c: Equal(g26,g-31)
    c: Equal(g27,g-32)
    c: Coincident(g25,g-30)
    c: Coincident(g26,g-31)
    c: Coincident(g27,g-32)
    c: Parallel(g28,g11)
    c: Parallel(g29,g13)
    c: Coincident(g28,g11)
    c: Coincident(g29,g12)
    c: Coincident(g29,g28)
FEATURE [PartDesign::Pad] Pad019
  Direction = (0,1,-2e-16)
  Length = 2
  Length2 = 10
  Profile = -> Sketch133
  ReferenceAxis = -> Sketch133 [N_Axis]
  Refine = true
  Suppressed = false
  Type = 0
FEATURE [Sketcher::SketchObject] Sketch091  label="Sketch091 - forma anteriore"
  ArcFitTolerance = 1e-06
  AttachmentSupport = -> [Pad019]
  ExternalGeometry = -> [Binder]
  FullyConstrained = true
  MakeInternals = false
  MapMode = 5
  Placement = pos=(0,2,0) rot=(0,0.707107,0.707107;3.14159rad)
  sketch-geometry (12):
    g0: Circle CenterX=5.6 CenterY=34.8 CenterZ=0 NormalX=0 NormalY=0 NormalZ=1 AngleXU=0 Radius=1.8
    g1: Circle CenterX=5.6 CenterY=7.6 CenterZ=0 NormalX=0 NormalY=0 NormalZ=1 AngleXU=0 Radius=1.8
    g2: Circle CenterX=78.51 CenterY=34.8 CenterZ=0 NormalX=0 NormalY=0 NormalZ=1 AngleXU=0 Radius=1.8
    g3: Circle CenterX=78.51 CenterY=7.6 CenterZ=0 NormalX=0 NormalY=0 NormalZ=1 AngleXU=0 Radius=1.8
    g4: LineSegment StartX=0 StartY=39.2 StartZ=0 EndX=0 EndY=3.2 EndZ=0
    g5: LineSegment StartX=0 StartY=3.2 StartZ=0 EndX=82.8 EndY=3.2 EndZ=0
    g6: LineSegment StartX=82.8 StartY=3.2 StartZ=0 EndX=82.8 EndY=39.2 EndZ=0
    g7: LineSegment StartX=82.8 StartY=39.2 StartZ=0 EndX=0 EndY=39.2 EndZ=0
    g8: ArcOfCircle CenterX=19 CenterY=21.2 CenterZ=0 NormalX=0 NormalY=0 NormalZ=1 AngleXU=0 Radius=10 StartAngle=1.5708 EndAngle=4.71239
    g9: ArcOfCircle CenterX=65 CenterY=21.2 CenterZ=0 NormalX=0 NormalY=0 NormalZ=1 AngleXU=0 Radius=10 StartAngle=4.71239 EndAngle=7.85398
    g10: LineSegment StartX=19 StartY=31.2 StartZ=0 EndX=65 EndY=31.2 EndZ=0
    g11: LineSegment StartX=19 StartY=11.2 StartZ=0 EndX=65 EndY=11.2 EndZ=0
  constraints (25):
    c: Equal(g2,g-7)
    c: Equal(g3,g-8)
    c: Equal(g1,g-13)
    c: Equal(g0,g-12)
    c: Coincident(g0,g-12)
    c: Coincident(g1,g-13)
    c: Coincident(g3,g-8)
    c: Coincident(g2,g-7)
    c: Coincident(g4,g-4)
    c: Coincident(g4,g-5)
    c: Coincident(g5,g4)
    c: Coincident(g5,g-6)
    c: Coincident(g6,g5)
    c: PointOnObject(g6,g-3)
    c: Vertical(g6)
    c: Coincident(g7,g6)
    c: Coincident(g7,g4)
    c: Tangent(g8,g10) = 1.5708
    c: Tangent(g8,g11) = -1.5708
    c: Tangent(g9,g10) = 1.5708
    c: Tangent(g9,g11) = -1.5708
    c: Equal(g8,g9)
    c: Radius(g8) = 10
    c: Coincident(g8,g-11)
    c: Coincident(g9,g-9)
FEATURE [Sketcher::SketchObject] Sketch093  label="Sketch093 - scavi interni pulsanti"
  ArcFitTolerance = 1e-06
  AttachmentSupport = -> [Pad019]
  ExternalGeometry = -> [Binder]
  FullyConstrained = true
  MakeInternals = false
  MapMode = 5
  Placement = pos=(0,1.8e-15,0) rot=(1,0,0;1.5708rad)
  sketch-geometry (3):
    g0: Circle CenterX=-65 CenterY=21.2 CenterZ=0 NormalX=0 NormalY=0 NormalZ=1 AngleXU=0 Radius=7.3
    g1: Circle CenterX=-42 CenterY=21.2 CenterZ=0 NormalX=0 NormalY=0 NormalZ=1 AngleXU=0 Radius=7.3
    g2: Circle CenterX=-19 CenterY=21.2 CenterZ=0 NormalX=0 NormalY=0 NormalZ=1 AngleXU=0 Radius=7.3
  constraints (6):
    c: Coincident(g0,g-3)
    c: Coincident(g1,g-4)
    c: Coincident(g2,g-5)
    c: Diameter(g0) = 14.6
    c: Diameter(g1) = 14.6
    c: Diameter(g2) = 14.6
FEATURE [Sketcher::SketchObject] Sketch094  label="Sketch094 - forma centrale"
  ArcFitTolerance = 1e-06
  AttachmentSupport = -> [Pad019]
  ExternalGeometry = -> [Binder]
  FullyConstrained = true
  MakeInternals = false
  MapMode = 5
  Placement = pos=(0,2,0) rot=(0,0.707107,0.707107;3.14159rad)
  sketch-geometry (4):
    g0: LineSegment StartX=137.815 StartY=39.2 StartZ=0 EndX=142.655 EndY=24.303 EndZ=0
    g1: LineSegment StartX=110.815 StartY=24.303 StartZ=0 EndX=142.655 EndY=24.303 EndZ=0
    g2: LineSegment StartX=137.815 StartY=39.2 StartZ=0 EndX=110.815 EndY=39.2 EndZ=0
    g3: ArcOfCircle CenterX=92.2534 CenterY=31.7515 CenterZ=0 NormalX=0 NormalY=0 NormalZ=1 AngleXU=0 Radius=20 StartAngle=5.90156 EndAngle=6.66481
  constraints (12):
    c: PointOnObject(g0,g-3)
    c: Tangent(g0,g-5)
    c: Horizontal(g1)
    c: Coincident(g1,g0)
    c: Coincident(g2,g0)
    c: PointOnObject(g2,g-3)
    c: DistanceX(g2,g2) = 27
    c: Vertical(g1,g2)
    c: Coincident(g3,g2)
    c: Radius(g3) = 20
    c: Coincident(g3,g1)
    c: DistanceY(g-6,g0) = 4
FEATURE [Sketcher::SketchObject] Sketch095  label="Sketch095 - forma posteriore"
  ArcFitTolerance = 1e-06
  AttachmentSupport = -> [Pad019]
  ExternalGeometry = -> [Binder]
  FullyConstrained = true
  MakeInternals = false
  MapMode = 5
  Placement = pos=(0,2,0) rot=(0,0.707107,0.707107;3.14159rad)
  sketch-geometry (15):
    g0: LineSegment StartX=137.815 StartY=39.2 StartZ=0 EndX=143.955 EndY=20.303 EndZ=0
    g1: LineSegment StartX=143.955 StartY=20.303 StartZ=0 EndX=190.141 EndY=20.303 EndZ=0
    g2: ArcOfCircle CenterX=184.08 CenterY=34.8 CenterZ=0 NormalX=0 NormalY=0 NormalZ=1 AngleXU=0 Radius=3.5 StartAngle=3.49066 EndAngle=4.71239
    g3: LineSegment StartX=180.791 StartY=33.6029 StartZ=0 EndX=178.754 EndY=39.2 EndZ=0
    g4: LineSegment StartX=184.08 StartY=31.3 StartZ=0 EndX=186.139 EndY=31.3 EndZ=0
    g5: LineSegment StartX=190.141 StartY=20.303 StartZ=0 EndX=186.139 EndY=31.3 EndZ=0
    g6: LineSegment StartX=137.815 StartY=39.2 StartZ=0 EndX=156.815 EndY=39.2 EndZ=0
    g7: LineSegment StartX=178.754 StartY=39.2 StartZ=0 EndX=168.815 EndY=39.2 EndZ=0
    g8: LineSegment StartX=156.815 StartY=31.2 StartZ=0 EndX=168.815 EndY=31.2 EndZ=0
    g9: ArcOfCircle CenterX=176.411 CenterY=35.2 CenterZ=0 NormalX=0 NormalY=0 NormalZ=1 AngleXU=0 Radius=20 StartAngle=2.94023 EndAngle=3.34295
    g10: ArcOfCircle CenterX=188.411 CenterY=35.2 CenterZ=0 NormalX=0 NormalY=0 NormalZ=1 AngleXU=0 Radius=20 StartAngle=2.94023 EndAngle=3.34295
    g11: LineSegment StartX=157.815 StartY=39.2 StartZ=0 EndX=167.815 EndY=39.2 EndZ=0
    g12: LineSegment StartX=157.436 StartY=36.2 StartZ=0 EndX=167.436 EndY=36.2 EndZ=0
    g13: ArcOfCircle CenterX=177.411 CenterY=35.2 CenterZ=0 NormalX=0 NormalY=0 NormalZ=1 AngleXU=0 Radius=20 StartAngle=2.94023 EndAngle=3.09157
    g14: ArcOfCircle CenterX=187.411 CenterY=35.2 CenterZ=0 NormalX=0 NormalY=0 NormalZ=1 AngleXU=0 Radius=20 StartAngle=2.94023 EndAngle=3.09157
  constraints (46):
    c: PointOnObject(g0,g-3)
    c: Tangent(g0,g-6)
    c: Coincident(g1,g0)
    c: Horizontal(g1)
    c: Radius(g2) = 3.5
    c: Coincident(g2,g-5)
    c: PointOnObject(g3,g-3)
    c: Parallel(g3,g-4)
    c: Tangent(g3,g2) = 1.5708
    c: Horizontal(g4)
    c: Tangent(g4,g2) = -1.5708
    c: Coincident(g5,g1)
    c: Parallel(g5,g-4)
    c: Coincident(g5,g4)
    c: DistanceX(g4,g-8) = 3.8
    c: Coincident(g6,g0)
    c: PointOnObject(g6,g-3)
    c: Coincident(g7,g3)
    c: PointOnObject(g7,g-3)
    c: Horizontal(g8)
    c: DistanceX(g6,g7) = 12
    c: Vertical(g8,g6)
    c: Vertical(g7,g8)
    c: DistanceY(g8,g6) = 8
    c: Coincident(g9,g8)
    c: Coincident(g9,g6)
    c: Coincident(g10,g7)
    c: Coincident(g10,g8)
    c: Radius(g9) = 20
    c: Radius(g10) = 20
    c: PointOnObject(g11,g-3)
    c: PointOnObject(g11,g-3)
    c: DistanceX(g11,g11) = 10
    c: DistanceX(g6,g11) = 1
    c: Horizontal(g12)
    c: Equal(g12,g11)
    c: DistanceY(g12,g11) = 3
    c: Coincident(g13,g11)
    c: Coincident(g13,g12)
    c: Radius(g13) = 20
    c: Coincident(g14,g11)
    c: Coincident(g14,g12)
    c: Radius(g14) = 20
    c: DistanceX(g0,g6) = 19
    c: Horizontal(g9,g13)
    c: Horizontal(g0,g-4)
FEATURE [Sketcher::SketchObject] Sketch096  label="Sketch096 - forma impugnatura"
  ArcFitTolerance = 1e-06
  AttachmentSupport = -> [Pad019]
  ExternalGeometry = -> [Binder]
  FullyConstrained = true
  MakeInternals = false
  MapMode = 5
  Placement = pos=(0,2,0) rot=(0,0.707107,0.707107;3.14159rad)
  sketch-geometry (8):
    g0: LineSegment StartX=176.685 StartY=-80.4316 StartZ=0 EndX=143.955 EndY=20.303 EndZ=0
    g1: LineSegment StartX=176.685 StartY=-80.4316 StartZ=0 EndX=215.932 EndY=-80.4316 EndZ=0
    g2: Circle CenterX=179.305 CenterY=-76.8316 CenterZ=0 NormalX=0 NormalY=0 NormalZ=1 AngleXU=0 Radius=3
    g3: Circle CenterX=213.443 CenterY=-76.8316 CenterZ=0 NormalX=0 NormalY=0 NormalZ=1 AngleXU=0 Radius=3
    g4: LineSegment StartX=143.955 StartY=20.303 StartZ=0 EndX=202.765 EndY=20.303 EndZ=0
    g5: LineSegment StartX=215.42 StartY=-53.0314 StartZ=0 EndX=192.176 EndY=-3.18451 EndZ=0
    g6: ArcOfCircle CenterX=184.801 CenterY=-67.3089 CenterZ=0 NormalX=0 NormalY=0 NormalZ=1 AngleXU=0 Radius=33.7833 StartAngle=5.88425 EndAngle=6.71952
    g7: ArcOfCircle CenterX=207.583 CenterY=4 CenterZ=0 NormalX=0 NormalY=0 NormalZ=1 AngleXU=0 Radius=17 StartAngle=1.85815 EndAngle=3.57792
  constraints (19):
    c: Coincident(g0,g-4)
    c: PointOnObject(g0,g-3)
    c: Horizontal(g0,g-7)
    c: Coincident(g1,g0)
    c: Coincident(g1,g-5)
    c: Diameter(g2) = 6
    c: Diameter(g3) = 6
    c: Coincident(g2,g-9)
    c: Coincident(g3,g-10)
    c: Coincident(g4,g0)
    c: Coincident(g5,g-6)
    c: Coincident(g6,g1)
    c: Coincident(g6,g5)
    c: Equal(g-5,g6)
    c: Coincident(g5,g-7)
    c: Coincident(g4,g-7)
    c: Tangent(g7,g-7)
    c: Coincident(g7,g4)
    c: Coincident(g7,g5)
FEATURE [Sketcher::SketchObject] Sketch097
  ArcFitTolerance = 1e-06
  AttachmentSupport = -> [Pad019]
  ExternalGeometry = -> [Binder]
  FullyConstrained = true
  MakeInternals = false
  MapMode = 5
  Placement = pos=(0,2,0) rot=(0,0.707107,0.707107;3.14159rad)
  sketch-geometry (4):
    g0: LineSegment StartX=90 StartY=36.8 StartZ=0 EndX=108 EndY=36.8 EndZ=0
    g1: LineSegment StartX=108 StartY=36.8 StartZ=0 EndX=108 EndY=26.8 EndZ=0
    g2: LineSegment StartX=108 StartY=26.8 StartZ=0 EndX=90 EndY=26.8 EndZ=0
    g3: ArcOfCircle CenterX=94 CenterY=31.8 CenterZ=0 NormalX=0 NormalY=0 NormalZ=1 AngleXU=0 Radius=6.40312 StartAngle=2.24554 EndAngle=4.03765
  constraints (13):
    c: Horizontal(g0)
    c: Coincident(g1,g0)
    c: Vertical(g1)
    c: DistanceX(g0,g0) = 18
    c: DistanceY(g1,g1) = 10
    c: Coincident(g2,g1)
    c: Horizontal(g2)
    c: Equal(g2,g0)
    c: DistanceY(g0,g-3) = 2.4
    c: Coincident(g3,g0)
    c: Coincident(g3,g2)
    c: DistanceX(g2,g3) = 4
    c: DistanceX(g-3,g0) = 90
FEATURE [PartDesign::Chamfer] Chamfer015
  Angle = 45
  Base = -> Pad019 [Edge19,Edge22,Edge79]
  BaseFeature = -> Pad019
  ChamferType = 0
  FlipDirection = false
  Refine = true
  Size = 1.9
  Size2 = 1
  SupportTransform = false
  Suppressed = false
  UseAllEdges = false
FEATURE [PartDesign::Pocket] Pocket002
  BaseFeature = -> Chamfer015
  Direction = (0,1,-2e-16)
  Length = 1.2
  Length2 = 5
  Profile = -> Sketch093
  ReferenceAxis = -> Sketch093 [N_Axis]
  Refine = true
  Suppressed = false
  Type = 0
FEATURE [PartDesign::Pad] Pad005
  BaseFeature = -> Pocket002
  Direction = (0,1,-2e-16)
  Length = 1.6
  Length2 = 10
  Profile = -> Sketch091
  ReferenceAxis = -> Sketch091 [N_Axis]
  Refine = true
  Suppressed = false
  Type = 0
FEATURE [Sketcher::SketchObject] Sketch092  label="Sketch092 - scavi per viti anteriori"
  ArcFitTolerance = 1e-06
  AttachmentSupport = -> [Pad005]
  ExternalGeometry = -> [Binder]
  FullyConstrained = true
  MakeInternals = false
  MapMode = 5
  Placement = pos=(0,3.6,0) rot=(0,0.707107,0.707107;3.14159rad)
  sketch-geometry (20):
    g0: ArcOfCircle CenterX=5.6 CenterY=7.6 CenterZ=0 NormalX=0 NormalY=0 NormalZ=1 AngleXU=0 Radius=3.5 StartAngle=0 EndAngle=1.5708
    g1: ArcOfCircle CenterX=5.6 CenterY=34.8 CenterZ=0 NormalX=0 NormalY=0 NormalZ=1 AngleXU=0 Radius=3.5 StartAngle=4.71239 EndAngle=6.28319
    g2: ArcOfCircle CenterX=78.51 CenterY=34.8 CenterZ=0 NormalX=0 NormalY=0 NormalZ=1 AngleXU=0 Radius=3.5 StartAngle=3.14159 EndAngle=4.71239
    g3: ArcOfCircle CenterX=78.51 CenterY=7.6 CenterZ=0 NormalX=0 NormalY=0 NormalZ=1 AngleXU=0 Radius=3.5 StartAngle=1.5708 EndAngle=3.14159
    g4: LineSegment StartX=0 StartY=3.2 StartZ=0 EndX=0 EndY=11.1 EndZ=0
    g5: LineSegment StartX=0 StartY=11.1 StartZ=0 EndX=5.6 EndY=11.1 EndZ=0
    g6: LineSegment StartX=0 StartY=3.2 StartZ=0 EndX=9.1 EndY=3.2 EndZ=0
    g7: LineSegment StartX=9.1 StartY=3.2 StartZ=0 EndX=9.1 EndY=7.6 EndZ=0
    g8: LineSegment StartX=0 StartY=39.2 StartZ=0 EndX=0 EndY=31.3 EndZ=0
    g9: LineSegment StartX=0 StartY=31.3 StartZ=0 EndX=5.6 EndY=31.3 EndZ=0
    g10: LineSegment StartX=0 StartY=39.2 StartZ=0 EndX=9.1 EndY=39.2 EndZ=0
    g11: LineSegment StartX=9.1 StartY=39.2 StartZ=0 EndX=9.1 EndY=34.8 EndZ=0
    g12: LineSegment StartX=82.8 StartY=39.2 StartZ=0 EndX=75.01 EndY=39.2 EndZ=0
    g13: LineSegment StartX=82.8 StartY=39.2 StartZ=0 EndX=82.8 EndY=31.3 EndZ=0
    g14: LineSegment StartX=82.8 StartY=31.3 StartZ=0 EndX=78.51 EndY=31.3 EndZ=0
    g15: LineSegment StartX=82.8 StartY=3.2 StartZ=0 EndX=75.01 EndY=3.2 EndZ=0
    g16: LineSegment StartX=75.01 StartY=3.2 StartZ=0 EndX=75.01 EndY=7.6 EndZ=0
    g17: LineSegment StartX=82.8 StartY=3.2 StartZ=0 EndX=82.8 EndY=11.1 EndZ=0
    g18: LineSegment StartX=82.8 StartY=11.1 StartZ=0 EndX=78.51 EndY=11.1 EndZ=0
    g19: LineSegment StartX=75.01 StartY=39.2 StartZ=0 EndX=75.01 EndY=34.8 EndZ=0
  constraints (48):
    c: Radius(g0) = 3.5
    c: Coincident(g0,g-10)
    c: Radius(g1) = 3.5
    c: Coincident(g1,g-9)
    c: Radius(g2) = 3.5
    c: Coincident(g2,g-8)
    c: Radius(g3) = 3.5
    c: Coincident(g3,g-7)
    c: Coincident(g4,g-5)
    c: PointOnObject(g4,g-4)
    c: Coincident(g5,g4)
    c: Horizontal(g5)
    c: Coincident(g6,g4)
    c: PointOnObject(g6,g-5)
    c: Coincident(g7,g6)
    c: Vertical(g7)
    c: Coincident(g8,g-4)
    c: PointOnObject(g8,g-4)
    c: Coincident(g9,g8)
    c: Horizontal(g9)
    c: Coincident(g10,g8)
    c: PointOnObject(g10,g-3)
    c: Coincident(g11,g10)
    c: Vertical(g11)
    c: PointOnObject(g12,g-3)
    c: PointOnObject(g12,g-3)
    c: Coincident(g13,g12)
    c: Vertical(g13)
    c: Coincident(g14,g13)
    c: Horizontal(g14)
    c: Coincident(g15,g-6)
    c: PointOnObject(g15,g-5)
    c: Coincident(g16,g15)
    c: Vertical(g16)
    c: Coincident(g17,g15)
    c: Coincident(g18,g17)
    c: Horizontal(g18)
    c: Tangent(g3,g18) = -1.5708
    c: Tangent(g16,g3) = 1.5708
    c: Coincident(g19,g12)
    c: Vertical(g19)
    c: Tangent(g2,g19) = -1.5708
    c: Tangent(g2,g14) = 1.5708
    c: Tangent(g0,g7) = -1.5708
    c: Tangent(g0,g5) = 1.5708
    c: Tangent(g9,g1) = -1.5708
    c: Tangent(g1,g11) = 1.5708
    c: Tangent(g17,g13)
FEATURE [PartDesign::Pocket] Pocket001
  BaseFeature = -> Pad005
  Direction = (0,-1,2e-16)
  Length = 1.6
  Length2 = 5
  Profile = -> Sketch092
  ReferenceAxis = -> Sketch092 [N_Axis]
  Refine = true
  Suppressed = false
  Type = 0
FEATURE [PartDesign::Pad] Pad006
  BaseFeature = -> Pocket001
  Direction = (0,1,-2e-16)
  Length = 0.8
  Length2 = 10
  Profile = -> Sketch094
  ReferenceAxis = -> Sketch094 [N_Axis]
  Refine = true
  Suppressed = false
  Type = 0
FEATURE [PartDesign::Pad] Pad007
  BaseFeature = -> Pad006
  Direction = (0,1,-2e-16)
  Length = 2
  Length2 = 10
  Profile = -> Sketch095
  ReferenceAxis = -> Sketch095 [N_Axis]
  Refine = true
  Suppressed = false
  Type = 0
FEATURE [PartDesign::Pad] Pad008  label="Pad008 - forma impugnatura"
  BaseFeature = -> Pad007
  Direction = (0,1,-2e-16)
  Length = 1.6
  Length2 = 10
  Profile = -> Sketch096
  ReferenceAxis = -> Sketch096 [N_Axis]
  Refine = true
  Suppressed = false
  Type = 0
FEATURE [PartDesign::Pad] Pad009
  BaseFeature = -> Pad008
  Direction = (0,1,-2e-16)
  Length = 1.6
  Length2 = 10
  Profile = -> Sketch097
  ReferenceAxis = -> Sketch097 [N_Axis]
  Refine = true
  Suppressed = false
  Type = 0
FEATURE [Sketcher::SketchObject] Sketch098
  ArcFitTolerance = 1e-06
  AttachmentSupport = -> [Pad006]
  ExternalGeometry = -> [Binder]
  FullyConstrained = true
  MakeInternals = false
  MapMode = 5
  Placement = pos=(0,2.8,-7e-16) rot=(0,0.707107,0.707107;3.14159rad)
  sketch-geometry (4):
    g0: LineSegment StartX=118 StartY=39.2 StartZ=0 EndX=129 EndY=39.2 EndZ=0
    g1: LineSegment StartX=120.599 StartY=31.2 StartZ=0 EndX=131.599 EndY=31.2 EndZ=0
    g2: LineSegment StartX=129 StartY=39.2 StartZ=0 EndX=131.599 EndY=31.2 EndZ=0
    g3: LineSegment StartX=118 StartY=39.2 StartZ=0 EndX=120.599 EndY=31.2 EndZ=0
  constraints (12):
    c: PointOnObject(g0,g-3)
    c: PointOnObject(g0,g-3)
    c: DistanceX(g0,g0) = 11
    c: Horizontal(g1)
    c: Equal(g1,g0)
    c: Coincident(g2,g0)
    c: Coincident(g3,g0)
    c: Parallel(g-4,g2)
    c: Coincident(g1,g2)
    c: Coincident(g1,g3)
    c: DistanceY(g1,g0) = 8
    c: DistanceX(g-3,g0) = 118
FEATURE [Sketcher::SketchObject] Sketch099
  ArcFitTolerance = 1e-06
  AttachmentSupport = -> [Pad008]
  ExternalGeometry = -> [Binder]
  FullyConstrained = true
  MakeInternals = false
  MapMode = 5
  Placement = pos=(0,3.6,0) rot=(0,0.707107,0.707107;3.14159rad)
  sketch-geometry (13):
    g0: LineSegment StartX=192.176 StartY=-3.18451 StartZ=0 EndX=196.804 EndY=-13.1108 EndZ=0
    g1: LineSegment [constr] StartX=202.765 StartY=20.303 StartZ=0 EndX=181.223 EndY=20.303 EndZ=0
    g2: LineSegment [constr] StartX=181.223 StartY=20.303 StartZ=0 EndX=181.223 EndY=-3.18451 EndZ=0
    g3: ArcOfCircle CenterX=181.223 CenterY=-20.3764 CenterZ=0 NormalX=0 NormalY=0 NormalZ=1 AngleXU=0 Radius=17.1918 StartAngle=0.436332 EndAngle=1.57079
    g4: ArcOfEllipse CenterX=181.223 CenterY=8.55923 CenterZ=0 NormalX=0 NormalY=0 NormalZ=1 MajorRadius=23.4779 MinorRadius=11.7437 AngleXU=0 StartAngle=1.5708 EndAngle=4.71239
    g5: LineSegment [constr] StartX=204.701 StartY=8.55923 StartZ=0 EndX=157.745 EndY=8.55923 EndZ=0
    g6: LineSegment [constr] StartX=181.223 StartY=20.303 StartZ=0 EndX=181.223 EndY=-3.18451 EndZ=0
    g7: GeomPoint [constr] X=201.553 Y=8.55923 Z=0
    g8: GeomPoint [constr] X=160.894 Y=8.55923 Z=0
    g9: GeomPoint [constr] X=181.223 Y=-3.18451 Z=0
    g10: LineSegment StartX=181.223 StartY=20.303 StartZ=0 EndX=202.765 EndY=20.303 EndZ=0
    g11: ArcOfCircle CenterX=207.583 CenterY=4 CenterZ=0 NormalX=0 NormalY=0 NormalZ=1 AngleXU=0 Radius=17 StartAngle=1.85815 EndAngle=3.57792
    g12: LineSegment [constr] StartX=172.411 StartY=39.2 StartZ=0 EndX=192.176 EndY=-3.18451 EndZ=0
  constraints (27):
    c: Coincident(g1,g-7)
    c: Horizontal(g1)
    c: Coincident(g2,g1)
    c: Vertical(g2)
    c: Horizontal(g2,g0)
    c: Coincident(g3,g0)
    c: Coincident(g3,g2)
    c: InternalAlignment(g5-g8 -> g4) x4
    c: Horizontal(g5)
    c: PointOnObject(g4,g2)
    c: Coincident(g4,g1)
    c: DistanceX(g-3,g5) = 10.1
    c: Coincident(g4,g2)
    c: Tangent(g3,g-5)
    c: PointOnObject(g9,g4)
    c: PointOnObject(g9,g3)
    c: Tangent(g4,g3,g9) = 1.5708
    c: Coincident(g10,g1)
    c: Coincident(g10,g1)
    c: Equal(g11,g-4)
    c: Coincident(g11,g1)
    c: Coincident(g11,g0)
    c: PointOnObject(g12,g-6)
    c: PointOnObject(g1,g12)
    c: Tangent(g12,g-5) = -1.5708
    c: Tangent(g0,g-5) = -1.5708
    c: Horizontal(g9,g12)
FEATURE [Sketcher::SketchObject] Sketch106  label="Sketch106 - smusso impuniatura interno"
  ArcFitTolerance = 1e-06
  AttachmentSupport = -> [Pad008]
  ExternalGeometry = -> [Pad008]
  FullyConstrained = true
  MakeInternals = false
  MapMode = 5
  Placement = pos=(0,-1.586e-13,-80.4316) rot=(1,0,0;3.14159rad)
  sketch-geometry (9):
    g0: LineSegment StartX=-176.685 StartY=-3.6 StartZ=0 EndX=-176.685 EndY=3.277e-13 EndZ=0
    g1: LineSegment [constr] StartX=-176.685 StartY=-7.37e-14 StartZ=0 EndX=-176.685 EndY=3.279e-13 EndZ=0
    g2: LineSegment [constr] StartX=-186.685 StartY=-3.6 StartZ=0 EndX=-186.685 EndY=3.277e-13 EndZ=0
    g3: ArcOfEllipse CenterX=-186.685 CenterY=3.279e-13 CenterZ=0 NormalX=0 NormalY=0 NormalZ=1 MajorRadius=10 MinorRadius=3.6 AngleXU=-3.14159 StartAngle=1.5708 EndAngle=3.14159
    g4: LineSegment [constr] StartX=-196.685 StartY=-5.9e-15 StartZ=0 EndX=-176.685 EndY=-5.9e-15 EndZ=0
    g5: LineSegment [constr] StartX=-186.685 StartY=-3.6 StartZ=0 EndX=-186.685 EndY=3.6 EndZ=0
    g6: GeomPoint [constr] X=-196.015 Y=-1.3e-14 Z=0
    g7: GeomPoint [constr] X=-177.356 Y=-4.9e-15 Z=0
    g8: LineSegment StartX=-176.685 StartY=-3.6 StartZ=0 EndX=-186.685 EndY=-3.6 EndZ=0
  constraints (15):
    c: PointOnObject(g2,g-3)
    c: Coincident(g1,g-5)
    c: DistanceY(g1,g1) = 0
    c: Coincident(g0,g1)
    c: DistanceX(g2,g-5) = 10
    c: Vertical(g2)
    c: Horizontal(g2,g0)
    c: InternalAlignment(g4-g7 -> g3) x4
    c: Coincident(g3,g2)
    c: Horizontal(g4)
    c: Coincident(g3,g0)
    c: Tangent(g0,g-5) = 1.5708
    c: Coincident(g3,g2)
    c: Coincident(g8,g0)
    c: Coincident(g8,g2)
FEATURE [Sketcher::SketchObject] Sketch107  label="Sketch107 - smusso impugnatura esterno"
  ArcFitTolerance = 1e-06
  AttachmentSupport = -> [Pad008]
  ExternalGeometry = -> [Pad008]
  FullyConstrained = true
  MakeInternals = false
  MapMode = 5
  Placement = pos=(0,-1.586e-13,-80.4316) rot=(1,0,0;3.14159rad)
  sketch-geometry (9):
    g0: LineSegment [constr] StartX=-215.932 StartY=-1.416e-13 StartZ=0 EndX=-215.932 EndY=-4.13e-14 EndZ=0
    g1: LineSegment StartX=-215.932 StartY=-3.6 StartZ=0 EndX=-215.932 EndY=-4.13e-14 EndZ=0
    g2: LineSegment StartX=-215.932 StartY=-3.6 StartZ=0 EndX=-205.932 EndY=-3.6 EndZ=0
    g3: LineSegment [constr] StartX=-205.932 StartY=-3.6 StartZ=0 EndX=-205.932 EndY=-4.13e-14 EndZ=0
    g4: ArcOfEllipse CenterX=-205.932 CenterY=-4.13e-14 CenterZ=0 NormalX=0 NormalY=0 NormalZ=1 MajorRadius=10 MinorRadius=3.6 AngleXU=-3.14159 StartAngle=-2.66e-14 EndAngle=1.5708
    g5: LineSegment [constr] StartX=-215.932 StartY=-1.416e-13 StartZ=0 EndX=-195.932 EndY=-1.416e-13 EndZ=0
    g6: LineSegment [constr] StartX=-205.932 StartY=-3.6 StartZ=0 EndX=-205.932 EndY=3.6 EndZ=0
    g7: GeomPoint [constr] X=-215.262 Y=-1.336e-13 Z=0
    g8: GeomPoint [constr] X=-196.602 Y=-1.551e-13 Z=0
  constraints (16):
    c: Coincident(g0,g-6)
    c: PointOnObject(g0,g-6)
    c: DistanceY(g0,g0) = 0
    c: Coincident(g1,g-6)
    c: Coincident(g1,g0)
    c: Tangent(g2,g-3)
    c: DistanceX(g2,g2) = 10
    c: Coincident(g3,g2)
    c: Vertical(g3)
    c: Horizontal(g3,g0)
    c: InternalAlignment(g5-g8 -> g4) x4
    c: Coincident(g4,g3)
    c: Horizontal(g5)
    c: Coincident(g4,g0)
    c: Coincident(g4,g2)
    c: PointOnObject(g2,g1)
FEATURE [Sketcher::SketchObject] Sketch108
  ArcFitTolerance = 1e-06
  AttachmentOffset = pos=(0,0,-1.6) rot=(0,0,1;0rad)
  AttachmentSupport = -> [Pad008]
  ExternalGeometry = -> [Binder]
  FullyConstrained = true
  MakeInternals = false
  MapMode = 5
  Placement = pos=(0,2,4e-16) rot=(0,0.707107,0.707107;3.14159rad)
  sketch-geometry (14):
    g0: LineSegment StartX=192.176 StartY=-3.18451 StartZ=0 EndX=193.827 EndY=-6.72678 EndZ=0
    g1: LineSegment [constr] StartX=202.765 StartY=20.303 StartZ=0 EndX=181.223 EndY=20.303 EndZ=0
    g2: LineSegment [constr] StartX=181.223 StartY=20.303 StartZ=0 EndX=181.223 EndY=1.30297 EndZ=0
    g3: ArcOfCircle CenterX=181.223 CenterY=-12.6042 CenterZ=0 NormalX=0 NormalY=0 NormalZ=1 AngleXU=0 Radius=13.9072 StartAngle=0.436332 EndAngle=1.5708
    g4: ArcOfEllipse CenterX=181.223 CenterY=10.803 CenterZ=0 NormalX=0 NormalY=0 NormalZ=1 MajorRadius=14.4779 MinorRadius=9.5 AngleXU=0 StartAngle=1.5708 EndAngle=4.71239
    g5: LineSegment [constr] StartX=195.701 StartY=10.803 StartZ=0 EndX=166.745 EndY=10.803 EndZ=0
    g6: LineSegment [constr] StartX=181.223 StartY=20.303 StartZ=0 EndX=181.223 EndY=1.30297 EndZ=0
    g7: GeomPoint [constr] X=192.148 Y=10.803 Z=0
    g8: GeomPoint [constr] X=170.298 Y=10.803 Z=0
    g9: LineSegment StartX=181.223 StartY=20.303 StartZ=0 EndX=202.765 EndY=20.303 EndZ=0
    g10: ArcOfCircle CenterX=207.583 CenterY=4 CenterZ=0 NormalX=0 NormalY=0 NormalZ=1 AngleXU=0 Radius=17 StartAngle=1.85815 EndAngle=3.57792
    g11: LineSegment [constr] StartX=172.411 StartY=39.2 StartZ=0 EndX=192.176 EndY=-3.18451 EndZ=0
    g12: GeomPoint [constr] X=181.223 Y=1.30297 Z=0
    g13: GeomPoint [constr] X=181.223 Y=1.30297 Z=0
  constraints (28):
    c: Coincident(g1,g-7)
    c: Horizontal(g1)
    c: Coincident(g2,g1)
    c: Vertical(g2)
    c: Coincident(g3,g2)
    c: InternalAlignment(g5-g8 -> g4) x4
    c: Horizontal(g5)
    c: PointOnObject(g4,g2)
    c: Coincident(g4,g1)
    c: DistanceX(g-3,g5) = 19.1
    c: Coincident(g4,g2)
    c: Coincident(g9,g1)
    c: Coincident(g9,g1)
    c: Coincident(g10,g1)
    c: Coincident(g10,g0)
    c: PointOnObject(g11,g-6)
    c: PointOnObject(g1,g11)
    c: DistanceY(g2,g1) = 19
    c: Coincident(g10,g-4)
    c: PointOnObject(g12,g4)
    c: PointOnObject(g12,g3)
    c: Tangent(g11,g-5) = -1.5708
    c: Tangent(g0,g-5) = -1.5708
    c: Tangent(g3,g0) = 1.5708
    c: PointOnObject(g13,g4)
    c: PointOnObject(g13,g3)
    c: Tangent(g4,g3,g13) = 1.5708
    c: Horizontal(g11,g0)
FEATURE [Part::Part2DObjectPython] Clone2D  label="Sketch108 (2D)"  # Draft 2D object (typed FeaturePython)
  Fuse = false
  Objects = -> [Sketch108]
  Placement = pos=(0,2,4e-16) rot=(0,0.707107,0.707107;3.14159rad)
  Scale = (1,1,1)
FEATURE [Sketcher::SketchObject] Sketch109
  ArcFitTolerance = 1e-06
  AttachmentOffset = pos=(0,0,-3.5) rot=(0,0,1;0rad)
  AttachmentSupport = -> [Pad008]
  ExternalGeometry = -> [Binder]
  FullyConstrained = true
  MakeInternals = false
  MapMode = 5
  Placement = pos=(0,0.1,8e-16) rot=(0,0.707107,0.707107;3.14159rad)
  sketch-geometry (1):
    g0: GeomPoint X=197.47 Y=8.55923 Z=0
  constraints (1):
    c: Symmetric(g-7,g-5,g0)
FEATURE [PartDesign::Chamfer] Chamfer005
  Angle = 45
  Base = -> Pad009 [Edge215,Edge212]
  BaseFeature = -> Pad009
  ChamferType = 1
  FlipDirection = false
  Refine = true
  Size = 1.5
  Size2 = 2.8
  SupportTransform = false
  Suppressed = false
  UseAllEdges = false
FEATURE [Sketcher::SketchObject] Sketch111
  ArcFitTolerance = 1e-06
  AttachmentSupport = -> [Pad009]
  ExternalGeometry = -> [Pad009]
  FullyConstrained = true
  MakeInternals = false
  MapMode = 5
  Placement = pos=(0,3.6,-8e-16) rot=(0,0.707107,0.707107;3.14159rad)
  sketch-geometry (21):
    g0: LineSegment [constr] StartX=97 StartY=36.8 StartZ=0 EndX=97 EndY=26.8 EndZ=0
    g1: LineSegment StartX=97 StartY=28.6 StartZ=0 EndX=97 EndY=27.8 EndZ=0
    g2: LineSegment StartX=97 StartY=27.8 StartZ=0 EndX=108 EndY=27.8 EndZ=0
    g3: LineSegment StartX=108 StartY=27.8 StartZ=0 EndX=108 EndY=28.6 EndZ=0
    g4: LineSegment StartX=108 StartY=28.6 StartZ=0 EndX=97 EndY=28.6 EndZ=0
    g5: LineSegment StartX=97 StartY=35.8 StartZ=0 EndX=97 EndY=35 EndZ=0
    g6: LineSegment StartX=97 StartY=35 StartZ=0 EndX=108 EndY=35 EndZ=0
    g7: LineSegment StartX=108 StartY=35 StartZ=0 EndX=108 EndY=35.8 EndZ=0
    g8: LineSegment StartX=108 StartY=35.8 StartZ=0 EndX=97 EndY=35.8 EndZ=0
    g9: LineSegment StartX=97 StartY=30.4 StartZ=0 EndX=97 EndY=29.6 EndZ=0
    g10: LineSegment StartX=97 StartY=29.6 StartZ=0 EndX=108 EndY=29.6 EndZ=0
    g11: LineSegment StartX=108 StartY=29.6 StartZ=0 EndX=108 EndY=30.4 EndZ=0
    g12: LineSegment StartX=108 StartY=30.4 StartZ=0 EndX=97 EndY=30.4 EndZ=0
    g13: LineSegment StartX=97 StartY=34 StartZ=0 EndX=97 EndY=33.2 EndZ=0
    g14: LineSegment StartX=97 StartY=33.2 StartZ=0 EndX=108 EndY=33.2 EndZ=0
    g15: LineSegment StartX=108 StartY=33.2 StartZ=0 EndX=108 EndY=34 EndZ=0
    g16: LineSegment StartX=108 StartY=34 StartZ=0 EndX=97 EndY=34 EndZ=0
    g17: LineSegment StartX=97 StartY=32.2 StartZ=0 EndX=97 EndY=31.4 EndZ=0
    g18: LineSegment StartX=97 StartY=31.4 StartZ=0 EndX=108 EndY=31.4 EndZ=0
    g19: LineSegment StartX=108 StartY=31.4 StartZ=0 EndX=108 EndY=32.2 EndZ=0
    g20: LineSegment StartX=108 StartY=32.2 StartZ=0 EndX=97 EndY=32.2 EndZ=0
  constraints (54):
    c: Vertical(g0)
    c: PointOnObject(g0,g-3)
    c: PointOnObject(g0,g-4)
    c: DistanceX(g0,g-5) = 11
    c: Coincident(g1,g2)
    c: Coincident(g2,g3)
    c: Coincident(g3,g4)
    c: Coincident(g4,g1)
    c: Horizontal(g2)
    c: Horizontal(g4)
    c: Tangent(g1,g0)
    c: Tangent(g3,g-5)
    c: DistanceY(g2,g3) = 0.8
    c: Coincident(g5,g6)
    c: Coincident(g6,g7)
    c: Coincident(g7,g8)
    c: Coincident(g8,g5)
    c: Horizontal(g6)
    c: Horizontal(g8)
    c: DistanceY(g6,g7) = 0.8
    c: Coincident(g9,g10)
    c: Coincident(g10,g11)
    c: Coincident(g11,g12)
    c: Coincident(g12,g9)
    c: Horizontal(g10)
    c: Horizontal(g12)
    c: DistanceY(g10,g11) = 0.8
    c: Tangent(g5,g0)
    c: Tangent(g7,g-5)
    c: Tangent(g9,g0)
    c: Tangent(g11,g-5)
    c: Coincident(g13,g14)
    c: Coincident(g14,g15)
    c: Coincident(g15,g16)
    c: Coincident(g16,g13)
    c: Horizontal(g14)
    c: Horizontal(g16)
    c: DistanceY(g14,g15) = 0.8
    c: Tangent(g13,g0)
    c: Tangent(g15,g-5)
    c: Coincident(g17,g18)
    c: Coincident(g18,g19)
    c: Coincident(g19,g20)
    c: Coincident(g20,g17)
    c: Horizontal(g18)
    c: Horizontal(g20)
    c: DistanceY(g18,g19) = 0.8
    c: Tangent(g17,g0)
    c: Tangent(g19,g-5)
    c: DistanceY(g1,g9) = 1
    c: DistanceY(g9,g17) = 1
    c: DistanceY(g17,g13) = 1
    c: DistanceY(g13,g5) = 1
    c: DistanceY(g0,g1) = 1
FEATURE [PartDesign::Pocket] Pocket004
  BaseFeature = -> Chamfer005
  Direction = (0,-1,2e-16)
  Length = 1
  Length2 = 5
  Profile = -> Sketch111
  ReferenceAxis = -> Sketch111 [N_Axis]
  Refine = true
  Suppressed = false
  Type = 0
FEATURE [PartDesign::Pad] Pad010
  BaseFeature = -> Pocket004
  Direction = (0,1,-2e-16)
  Length = 1.2
  Length2 = 10
  Profile = -> Sketch098
  ReferenceAxis = -> Sketch098 [N_Axis]
  Refine = true
  Suppressed = false
  Type = 0
FEATURE [PartDesign::Chamfer] Chamfer006
  Angle = 45
  Base = -> Pad010 [Edge291]
  BaseFeature = -> Pad010
  ChamferType = 1
  FlipDirection = false
  Refine = true
  Size = 1
  Size2 = 6
  SupportTransform = false
  Suppressed = false
  UseAllEdges = false
FEATURE [Sketcher::SketchObject] Sketch110
  ArcFitTolerance = 1e-06
  AttachmentSupport = -> [Pad010]
  ExternalGeometry = -> [Sketch098]
  FullyConstrained = true
  MakeInternals = false
  MapMode = 5
  Placement = pos=(0,4,-9e-16) rot=(0,0.707107,0.707107;3.14159rad)
  sketch-geometry (8):
    g0: LineSegment StartX=119.69 StartY=34 StartZ=0 EndX=130.69 EndY=34 EndZ=0
    g1: LineSegment StartX=119.95 StartY=33.2 StartZ=0 EndX=130.95 EndY=33.2 EndZ=0
    g2: LineSegment StartX=119.137 StartY=35.7 StartZ=0 EndX=130.137 EndY=35.7 EndZ=0
    g3: LineSegment StartX=118.877 StartY=36.5 StartZ=0 EndX=129.877 EndY=36.5 EndZ=0
    g4: LineSegment StartX=118.877 StartY=36.5 StartZ=0 EndX=119.137 EndY=35.7 EndZ=0
    g5: LineSegment StartX=129.877 StartY=36.5 StartZ=0 EndX=130.137 EndY=35.7 EndZ=0
    g6: LineSegment StartX=119.69 StartY=34 StartZ=0 EndX=119.95 EndY=33.2 EndZ=0
    g7: LineSegment StartX=130.69 StartY=34 StartZ=0 EndX=130.95 EndY=33.2 EndZ=0
  constraints (24):
    c: Horizontal(g0)
    c: Horizontal(g1)
    c: Horizontal(g2)
    c: Horizontal(g3)
    c: Equal(g1,g-5)
    c: Equal(g0,g-5)
    c: Equal(g2,g-5)
    c: Equal(g3,g-5)
    c: PointOnObject(g0,g-3)
    c: PointOnObject(g1,g-3)
    c: PointOnObject(g2,g-3)
    c: PointOnObject(g3,g-3)
    c: Coincident(g4,g3)
    c: Coincident(g4,g2)
    c: Coincident(g5,g3)
    c: Coincident(g5,g2)
    c: Coincident(g6,g0)
    c: Coincident(g6,g1)
    c: Coincident(g7,g0)
    c: Coincident(g7,g1)
    c: DistanceY(g1,g0) = 0.8
    c: DistanceY(g2,g3) = 0.8
    c: DistanceY(g-5,g1) = 2
    c: DistanceY(g-5,g2) = 4.5
FEATURE [PartDesign::Pocket] Pocket003
  BaseFeature = -> Chamfer006
  Direction = (0,-1,2e-16)
  Length = 1
  Length2 = 5
  Profile = -> Sketch110
  ReferenceAxis = -> Sketch110 [N_Axis]
  Refine = true
  Suppressed = false
  Type = 0
FEATURE [PartDesign::SubtractivePipe] SubtractivePipe
  AuxilleryCurvelinear = true
  AuxillerySpineTangent = false
  BaseFeature = -> Pocket003
  Binormal = (0,0,0)
  Mode = 0
  Profile = -> Sketch106
  Refine = true
  Spine = -> Pad008 [Edge215]
  SpineTangent = false
  Suppressed = false
  Transformation = 0
  Transition = 0
FEATURE [PartDesign::SubtractivePipe] SubtractivePipe001
  AuxilleryCurvelinear = true
  AuxillerySpineTangent = false
  BaseFeature = -> SubtractivePipe
  Binormal = (0,0,0)
  Mode = 0
  Profile = -> Sketch107
  Refine = true
  Spine = -> Pad008 [Edge213,Edge216,Edge210]
  SpineTangent = false
  Suppressed = false
  Transformation = 0
  Transition = 0
FEATURE [PartDesign::SubtractiveLoft] SubtractiveLoft
  BaseFeature = -> SubtractivePipe001
  Closed = false
  Profile = -> Sketch099
  Refine = true
  Ruled = false
  Sections = -> [Sketch108]
  Suppressed = false
FEATURE [PartDesign::SubtractiveLoft] SubtractiveLoft001
  BaseFeature = -> SubtractiveLoft
  Closed = false
  Profile = -> Clone2D
  Refine = true
  Ruled = false
  Sections = -> [Sketch109]
  Suppressed = false
FEATURE [Sketcher::SketchObject] Sketch112
  ArcFitTolerance = 1e-06
  AttachmentSupport = -> [Pad008]
  ExternalGeometry = -> [Binder]
  FullyConstrained = true
  MakeInternals = false
  MapMode = 5
  Placement = pos=(0,3.6,0) rot=(0,0.707107,0.707107;3.14159rad)
  sketch-geometry (4):
    g0: LineSegment [constr] StartX=167.782 StartY=-53.0314 StartZ=0 EndX=215.42 EndY=-53.0314 EndZ=0
    g1: GeomPoint [constr] X=191.282 Y=-53.0314 Z=0
    g2: Circle CenterX=191.282 CenterY=-53.0314 CenterZ=0 NormalX=0 NormalY=0 NormalZ=1 AngleXU=0 Radius=11.5
    g3: Circle CenterX=191.282 CenterY=-53.0314 CenterZ=0 NormalX=0 NormalY=0 NormalZ=1 AngleXU=0 Radius=10.7
  constraints (9):
    c: Horizontal(g0)
    c: PointOnObject(g0,g-3)
    c: Diameter(g2) = 23
    c: Coincident(g2,g1)
    c: Diameter(g3) = 21.4
    c: Coincident(g3,g1)
    c: DistanceX(g0,g1) = 23.5
    c: PointOnObject(g1,g0)
    c: Coincident(g0,g-4)
FEATURE [PartDesign::Chamfer] Chamfer016
  Angle = 45
  Base = -> SubtractiveLoft001 [Edge118,Edge117,Edge119,Edge120,Edge109]
  BaseFeature = -> SubtractiveLoft001
  ChamferType = 0
  FlipDirection = false
  Refine = true
  Size = 1.5
  Size2 = 1
  SupportTransform = false
  Suppressed = false
  UseAllEdges = false
FEATURE [PartDesign::Chamfer] Chamfer017
  Angle = 45
  Base = -> Chamfer016 [Edge15]
  BaseFeature = -> Chamfer016
  ChamferType = 0
  FlipDirection = false
  Refine = true
  Size = 1.6
  Size2 = 1
  SupportTransform = false
  Suppressed = false
  UseAllEdges = false
FEATURE [PartDesign::Chamfer] Chamfer018
  Angle = 45
  Base = -> Chamfer017 [Edge10]
  BaseFeature = -> Chamfer017
  ChamferType = 0
  FlipDirection = false
  Refine = true
  Size = 3.5
  Size2 = 1
  SupportTransform = false
  Suppressed = false
  UseAllEdges = false
FEATURE [PartDesign::Chamfer] Chamfer019
  Angle = 45
  Base = -> Chamfer018 [Edge94]
  BaseFeature = -> Chamfer018
  ChamferType = 0
  FlipDirection = false
  Refine = true
  Size = 1.9
  Size2 = 1
  SupportTransform = false
  Suppressed = false
  UseAllEdges = false
FEATURE [PartDesign::Fillet] Fillet009
  Base = -> Chamfer019 [Edge83]
  BaseFeature = -> Chamfer019
  Radius = 1.1
  Refine = true
  SupportTransform = false
  Suppressed = false
  UseAllEdges = false
FEATURE [PartDesign::Fillet] Fillet010
  Base = -> Fillet009 [Edge76]
  BaseFeature = -> Fillet009
  Radius = 1.9
  Refine = true
  SupportTransform = false
  Suppressed = false
  UseAllEdges = false
FEATURE [PartDesign::Pocket] Pocket005
  BaseFeature = -> Fillet010
  Direction = (0,-1,2e-16)
  Length = 0.8
  Length2 = 5
  Profile = -> Sketch112
  ReferenceAxis = -> Sketch112 [N_Axis]
  Refine = true
  Suppressed = false
  Type = 0
FEATURE [Part::Part2DObjectPython] ShapeString001  # Draft 2D object (typed FeaturePython)
  FontFile = <path>
  Fuse = false
  Justification = 6
  JustificationReference = 0
  KeepLeftMargin = false
  MakeFace = true
  ObliqueAngle = 0
  Placement = pos=(-183.5,3.6,-57.5) rot=(0,0.707107,0.707107;3.14159rad)
  ScaleToSize = true
  Size = 10
  String = AS
  Tracking = 0
FEATURE [PartDesign::Pocket] Pocket013
  BaseFeature = -> Pocket005
  Direction = (-1e-16,-1,2e-16)
  Length = 1
  Length2 = 5
  Profile = -> ShapeString001
  ReferenceAxis = -> ShapeString001 [N_Axis]
  Refine = true
  Suppressed = false
  Type = 0
FEATURE [PartDesign::Pad] Pad020
  Direction = (0,-1,2e-16)
  Length = 25.2
  Length2 = 10
  Midplane = true
  Placement = pos=(0,0,0) rot=(1,0,0;1.5708rad)
  Profile = -> Sketch021
  ReferenceAxis = -> Sketch021 [N_Axis]
  Refine = true
  Suppressed = false
  Type = 0
FEATURE [PartDesign::Body] Body001  label="perno fermo rumble e driver solenoide"
  AllowCompound = false
  Group = -> [Sketch021,Pad020]
  Origin = -> Origin001
  Tip = -> Pad020
FEATURE [PartDesign::Pad] Pad021
  Direction = (0,-1,2e-16)
  Length = 16.8
  Length2 = 10
  Midplane = true
  Placement = pos=(0,0,0) rot=(1,0,0;1.5708rad)
  Profile = -> Sketch061
  ReferenceAxis = -> Sketch061 [N_Axis]
  Refine = true
  Suppressed = false
  Type = 0
FEATURE [PartDesign::Pocket] Pocket014
  BaseFeature = -> Pad021
  Direction = (0,1,-2e-16)
  Length = 12.8
  Length2 = 5
  Midplane = true
  Placement = pos=(0,0,0) rot=(1,0,0;1.5708rad)
  Profile = -> Sketch062
  ReferenceAxis = -> Sketch062 [N_Axis]
  Refine = true
  Suppressed = false
  Type = 0
FEATURE [PartDesign::Pad] Pad022
  BaseFeature = -> Pocket014
  Direction = (0,-1,2e-16)
  Length = 7.6
  Length2 = 10
  Midplane = true
  Placement = pos=(0,0,0) rot=(1,0,0;1.5708rad)
  Profile = -> Sketch063
  ReferenceAxis = -> Sketch063 [N_Axis]
  Refine = true
  Suppressed = false
  Type = 0
FEATURE [PartDesign::Body] Body003  label="blocco switch"
  AllowCompound = false
  Group = -> [Sketch061,Sketch062,Sketch063,Pad021,Pocket014,Pad022]
  Origin = -> Origin003
  Tip = -> Pad022
FEATURE [PartDesign::Pad] Pad024
  Direction = (0,-1,2e-16)
  Length = 17
  Length2 = 10
  Midplane = true
  Placement = pos=(0,0,0) rot=(1,0,0;1.5708rad)
  Profile = -> Sketch045
  ReferenceAxis = -> Sketch045 [N_Axis]
  Refine = true
  Suppressed = false
  Type = 0
FEATURE [PartDesign::Pocket] Pocket015
  BaseFeature = -> Pad024
  Direction = (-1,0,0)
  Length = 8
  Length2 = 5
  Placement = pos=(0,0,0) rot=(1,0,0;1.5708rad)
  Profile = -> Sketch047
  ReferenceAxis = -> Sketch047 [N_Axis]
  Refine = true
  Reversed = true
  Suppressed = false
  Type = 0
FEATURE [PartDesign::Pocket] Pocket016
  BaseFeature = -> Pocket015
  Direction = (-1,0,0)
  Length = 1
  Length2 = 5
  Placement = pos=(0,0,0) rot=(1,0,0;1.5708rad)
  Profile = -> Sketch046
  ReferenceAxis = -> Sketch046 [N_Axis]
  Refine = true
  Reversed = true
  Suppressed = false
  Type = 0
FEATURE [PartDesign::Pocket] Pocket017
  BaseFeature = -> Pocket016
  Direction = (0,1,-2e-16)
  Length = 17
  Length2 = 5
  Midplane = true
  Placement = pos=(0,0,0) rot=(1,0,0;1.5708rad)
  Profile = -> Sketch048
  ReferenceAxis = -> Sketch048 [N_Axis]
  Refine = true
  Suppressed = false
  Type = 0
FEATURE [PartDesign::Pad] Pad025
  BaseFeature = -> Pocket017
  Direction = (0,-1,2e-16)
  Length = 17
  Length2 = 10
  Midplane = true
  Placement = pos=(0,0,0) rot=(1,0,0;1.5708rad)
  Profile = -> Sketch049
  ReferenceAxis = -> Sketch049 [N_Axis]
  Refine = true
  Suppressed = false
  Type = 0
FEATURE [PartDesign::Pad] Pad026
  BaseFeature = -> Pad025
  Direction = (0,-1,2e-16)
  Length = 17
  Length2 = 10
  Midplane = true
  Placement = pos=(0,0,0) rot=(1,0,0;1.5708rad)
  Profile = -> Sketch066
  ReferenceAxis = -> Sketch066 [N_Axis]
  Refine = true
  Suppressed = false
  Type = 0
FEATURE [PartDesign::Pad] Pad027
  BaseFeature = -> Pad026
  Direction = (0,-1,2e-16)
  Length = 5
  Length2 = 10
  Midplane = true
  Placement = pos=(0,0,0) rot=(1,0,0;1.5708rad)
  Profile = -> Sketch064
  ReferenceAxis = -> Sketch064 [N_Axis]
  Refine = true
  Suppressed = false
  Type = 0
FEATURE [PartDesign::Pad] Pad028
  BaseFeature = -> Pad027
  Direction = (1,0,0)
  Length = 1
  Length2 = 10
  Placement = pos=(0,0,0) rot=(1,0,0;1.5708rad)
  Profile = -> Sketch068
  ReferenceAxis = -> Sketch068 [N_Axis]
  Refine = true
  Reversed = true
  Suppressed = false
  Type = 0
FEATURE [PartDesign::Chamfer] Chamfer020
  Angle = 45
  Base = -> Pad028 [Edge73,Edge75,Edge78,Edge77]
  BaseFeature = -> Pad028
  ChamferType = 0
  FlipDirection = false
  Placement = pos=(0,0,0) rot=(1,0,0;1.5708rad)
  Refine = true
  Size = 0.5
  Size2 = 1
  SupportTransform = false
  Suppressed = false
  UseAllEdges = false
FEATURE [PartDesign::Body] Body002  label="supporto per neopixel"
  AllowCompound = false
  Group = -> [Sketch045,Sketch047,Sketch046,Sketch048,Sketch049,Sketch066,Sketch064,Sketch068,Pad024,Pocket015,Pocket016,Pocket017,Pad025,Pad026,Pad027,Pad028,Chamfer020]
  Origin = -> Origin002
  Tip = -> Chamfer020
FEATURE [Sketcher::SketchObject] Sketch134  label="perno fermo rumble002"
  ArcFitTolerance = 1e-06
  AttachmentSupport = -> [XZ_Plane008]
  FullyConstrained = true
  MakeInternals = false
  MapMode = 5
  Placement = pos=(0,0,0) rot=(1,0,0;1.5708rad)
  sketch-geometry (16):
    g0: LineSegment StartX=0 StartY=0.45 StartZ=0 EndX=0 EndY=1.55 EndZ=0
    g1: LineSegment StartX=0.45 StartY=2 StartZ=0 EndX=1.55 EndY=2 EndZ=0
    g2: LineSegment StartX=2 StartY=1.55 StartZ=0 EndX=2 EndY=0.45 EndZ=0
    g3: LineSegment StartX=1.55 StartY=0 StartZ=0 EndX=0.45 EndY=0 EndZ=0
    g4: ArcOfCircle [constr] CenterX=0.45 CenterY=1.55 CenterZ=0 NormalX=0 NormalY=0 NormalZ=1 AngleXU=0 Radius=0.45 StartAngle=1.5708 EndAngle=3.14159
    g5: GeomPoint [constr] X=0 Y=2 Z=0
    g6: LineSegment StartX=0.45 StartY=2 StartZ=0 EndX=0 EndY=1.55 EndZ=0
    g7: ArcOfCircle [constr] CenterX=1.55 CenterY=1.55 CenterZ=0 NormalX=0 NormalY=0 NormalZ=1 AngleXU=0 Radius=0.45 StartAngle=0 EndAngle=1.5708
    g8: GeomPoint [constr] X=2 Y=2 Z=0
    g9: LineSegment StartX=2 StartY=1.55 StartZ=0 EndX=1.55 EndY=2 EndZ=0
    g10: ArcOfCircle [constr] CenterX=1.55 CenterY=0.45 CenterZ=0 NormalX=0 NormalY=0 NormalZ=1 AngleXU=0 Radius=0.45 StartAngle=4.71239 EndAngle=6.28319
    g11: GeomPoint [constr] X=2 Y=0 Z=0
    g12: LineSegment StartX=1.55 StartY=0 StartZ=0 EndX=2 EndY=0.45 EndZ=0
    g13: ArcOfCircle [constr] CenterX=0.45 CenterY=0.45 CenterZ=0 NormalX=0 NormalY=0 NormalZ=1 AngleXU=0 Radius=0.45 StartAngle=3.14159 EndAngle=4.71239
    g14: GeomPoint [constr] X=0 Y=0 Z=0
    g15: LineSegment StartX=0 StartY=0.45 StartZ=0 EndX=0.45 EndY=0 EndZ=0
  constraints (35):
    c: Coincident(g14,g-1)
    c: PointOnObject(g5,g-2)
    c: Horizontal(g1)
    c: Vertical(g2)
    c: Horizontal(g3)
    c: DistanceX(g5,g8) = 2
    c: DistanceY(g11,g8) = 2
    c: PointOnObject(g5,g0)
    c: PointOnObject(g5,g1)
    c: Tangent(g0,g4) = 1.5708
    c: Tangent(g1,g4) = 1.5708
    c: Coincident(g6,g0)
    c: Coincident(g6,g1)
    c: PointOnObject(g8,g2)
    c: PointOnObject(g8,g1)
    c: Tangent(g2,g7) = 1.5708
    c: Tangent(g1,g7) = 1.5708
    c: Coincident(g9,g2)
    c: Coincident(g9,g1)
    c: PointOnObject(g11,g2)
    c: PointOnObject(g11,g3)
    c: Tangent(g2,g10) = 1.5708
    c: Tangent(g3,g10) = 1.5708
    c: Coincident(g12,g2)
    c: Coincident(g12,g3)
    c: PointOnObject(g14,g0)
    c: PointOnObject(g14,g3)
    c: Tangent(g0,g13) = 1.5708
    c: Tangent(g3,g13) = 1.5708
    c: Coincident(g15,g0)
    c: Coincident(g15,g3)
    c: Equal(g6,g9)
    c: Equal(g9,g12)
    c: Equal(g12,g15)
    c: DistanceX(g14,g3) = 0.45
FEATURE [PartDesign::Pad] Pad029
  Direction = (0,-1,2e-16)
  Length = 17
  Length2 = 10
  Midplane = true
  Placement = pos=(0,0,0) rot=(1,0,0;1.5708rad)
  Profile = -> Sketch134
  ReferenceAxis = -> Sketch134 [N_Axis]
  Refine = true
  Suppressed = false
  Type = 0
FEATURE [PartDesign::Body] Body008  label="perno fermo neopixel"
  AllowCompound = false
  Group = -> [Sketch134,Pad029]
  Origin = -> Origin008
  Tip = -> Pad029
FEATURE [Sketcher::SketchObject] Sketch135  label="perno fermo rumble003"
  ArcFitTolerance = 1e-06
  AttachmentSupport = -> [XZ_Plane009]
  FullyConstrained = true
  MakeInternals = false
  MapMode = 5
  Placement = pos=(0,0,0) rot=(1,0,0;1.5708rad)
  sketch-geometry (16):
    g0: LineSegment StartX=4.69e-14 StartY=0.8 StartZ=0 EndX=-3.04e-14 EndY=3.1 EndZ=0
    g1: LineSegment StartX=0.8 StartY=3.9 StartZ=0 EndX=3.1 EndY=3.9 EndZ=0
    g2: LineSegment StartX=3.9 StartY=3.1 StartZ=0 EndX=3.9 EndY=0.8 EndZ=0
    g3: LineSegment StartX=3.1 StartY=0 StartZ=0 EndX=0.8 EndY=0 EndZ=0
    g4: ArcOfCircle [constr] CenterX=0.8 CenterY=3.1 CenterZ=0 NormalX=0 NormalY=0 NormalZ=1 AngleXU=0 Radius=0.8 StartAngle=1.5708 EndAngle=3.14159
    g5: GeomPoint [constr] X=0 Y=3.9 Z=0
    g6: LineSegment StartX=0.8 StartY=3.9 StartZ=0 EndX=-3.04e-14 EndY=3.1 EndZ=0
    g7: ArcOfCircle [constr] CenterX=3.1 CenterY=3.1 CenterZ=0 NormalX=0 NormalY=0 NormalZ=1 AngleXU=0 Radius=0.8 StartAngle=-2.4e-14 EndAngle=1.5708
    g8: GeomPoint [constr] X=3.9 Y=3.9 Z=0
    g9: LineSegment StartX=3.9 StartY=3.1 StartZ=0 EndX=3.1 EndY=3.9 EndZ=0
    g10: ArcOfCircle [constr] CenterX=3.1 CenterY=0.8 CenterZ=0 NormalX=0 NormalY=0 NormalZ=1 AngleXU=0 Radius=0.8 StartAngle=4.71239 EndAngle=6.28319
    g11: GeomPoint [constr] X=3.9 Y=0 Z=0
    g12: LineSegment StartX=3.1 StartY=0 StartZ=0 EndX=3.9 EndY=0.8 EndZ=0
    g13: ArcOfCircle [constr] CenterX=0.8 CenterY=0.8 CenterZ=0 NormalX=0 NormalY=0 NormalZ=1 AngleXU=0 Radius=0.8 StartAngle=3.14159 EndAngle=4.71239
    g14: GeomPoint [constr] X=0 Y=0 Z=0
    g15: LineSegment StartX=4.69e-14 StartY=0.8 StartZ=0 EndX=0.8 EndY=0 EndZ=0
  constraints (35):
    c: Coincident(g14,g-1)
    c: PointOnObject(g5,g-2)
    c: Horizontal(g1)
    c: Vertical(g2)
    c: Horizontal(g3)
    c: DistanceX(g5,g8) = 3.9
    c: DistanceY(g11,g8) = 3.9
    c: PointOnObject(g5,g0)
    c: PointOnObject(g5,g1)
    c: Tangent(g0,g4) = 1.5708
    c: Tangent(g1,g4) = 1.5708
    c: Coincident(g6,g0)
    c: Coincident(g6,g1)
    c: PointOnObject(g8,g2)
    c: PointOnObject(g8,g1)
    c: Tangent(g2,g7) = 1.5708
    c: Tangent(g1,g7) = 1.5708
    c: Coincident(g9,g2)
    c: Coincident(g9,g1)
    c: PointOnObject(g11,g2)
    c: PointOnObject(g11,g3)
    c: Tangent(g2,g10) = 1.5708
    c: Tangent(g3,g10) = 1.5708
    c: Coincident(g12,g2)
    c: Coincident(g12,g3)
    c: PointOnObject(g14,g0)
    c: PointOnObject(g14,g3)
    c: Tangent(g0,g13) = 1.5708
    c: Tangent(g3,g13) = 1.5708
    c: Coincident(g15,g0)
    c: Coincident(g15,g3)
    c: Equal(g6,g9)
    c: Equal(g9,g12)
    c: Equal(g12,g15)
    c: DistanceX(g14,g3) = 0.8
FEATURE [PartDesign::Pad] Pad030
  Direction = (0,-1,2e-16)
  Length = 25.2
  Length2 = 10
  Midplane = true
  Placement = pos=(0,0,0) rot=(1,0,0;1.5708rad)
  Profile = -> Sketch135
  ReferenceAxis = -> Sketch135 [N_Axis]
  Refine = true
  Suppressed = false
  Type = 0
FEATURE [PartDesign::Body] Body009  label="perno fermo switch - caricabatterie - grilletto"
  AllowCompound = false
  Group = -> [Sketch135,Pad030]
  Origin = -> Origin009
  Tip = -> Pad030
FEATURE [Sketcher::SketchObject] Sketch136  label="scavo_rele"
  ArcFitTolerance = 1e-06
  AttachmentSupport = -> [XZ_Plane]
  ExternalGeometry = -> [Sketch]
  FullyConstrained = true
  MakeInternals = false
  MapMode = 5
  Placement = pos=(0,0,0) rot=(1,0,0;1.5708rad)
  sketch-geometry (7):
    g0: LineSegment [constr] StartX=-173.013 StartY=-62.644 StartZ=0 EndX=-176.535 EndY=-73.4861 EndZ=0
    g1: LineSegment [constr] StartX=-173.013 StartY=-62.644 StartZ=0 EndX=-170.35 EndY=-63.5093 EndZ=0
    g2: LineSegment [constr] StartX=-173.013 StartY=-62.644 StartZ=0 EndX=-176.627 EndY=-61.4698 EndZ=0
    g3: LineSegment StartX=-176.627 StartY=-61.4698 StartZ=0 EndX=-170.35 EndY=-63.5093 EndZ=0
    g4: LineSegment StartX=-176.627 StartY=-61.4698 StartZ=0 EndX=-180.149 EndY=-72.3118 EndZ=0
    g5: LineSegment StartX=-170.35 StartY=-63.5093 StartZ=0 EndX=-173.872 EndY=-74.3513 EndZ=0
    g6: LineSegment StartX=-180.149 StartY=-72.3118 StartZ=0 EndX=-173.872 EndY=-74.3513 EndZ=0
  constraints (19):
    c: Tangent(g0,g-3)
    c: Distance(g0,g-3) = 89
    c: Distance(g0,g0) = 11.4
    c: Coincident(g1,g0)
    c: Coincident(g2,g0)
    c: Distance(g2) = 3.8
    c: Distance(g1) = 2.8
    c: Perpendicular(g0,g1)
    c: Perpendicular(g0,g2)
    c: Coincident(g3,g2)
    c: Coincident(g3,g1)
    c: Equal(g4,g0)
    c: Equal(g5,g0)
    c: Parallel(g4,g0)
    c: Parallel(g5,g0)
    c: Coincident(g4,g2)
    c: Coincident(g5,g1)
    c: Coincident(g6,g4)
    c: Coincident(g6,g5)
FEATURE [Part::Extrusion] Extrude076  label="Extrude076 - scavo_rele"
  Base = -> Sketch136
  Dir = (0,-1,2e-16)
  DirMode = 2
  FaceMakerClass = Part::FaceMakerBullseye
  FaceMakerMode = 3
  LengthFwd = 17.8
  LengthRev = 0
  Solid = true
  Symmetric = true
FEATURE [Sketcher::SketchObject] Sketch137  label="scavo_nuovo_driver"
  ArcFitTolerance = 1e-06
  AttachmentSupport = -> [XZ_Plane]
  ExternalGeometry = -> [Sketch]
  FullyConstrained = true
  MakeInternals = false
  MapMode = 5
  Placement = pos=(0,0,0) rot=(1,0,0;1.5708rad)
  sketch-geometry (7):
    g0: LineSegment [constr] StartX=-160.157 StartY=-23.0801 StartZ=0 EndX=-164.978 EndY=-37.9166 EndZ=0
    g1: LineSegment [constr] StartX=-160.157 StartY=-23.0801 StartZ=0 EndX=-157.875 EndY=-23.8217 EndZ=0
    g2: LineSegment [constr] StartX=-160.157 StartY=-23.0801 StartZ=0 EndX=-163.771 EndY=-21.9058 EndZ=0
    g3: LineSegment StartX=-163.771 StartY=-21.9058 StartZ=0 EndX=-157.875 EndY=-23.8217 EndZ=0
    g4: LineSegment StartX=-163.771 StartY=-21.9058 StartZ=0 EndX=-168.592 EndY=-36.7423 EndZ=0
    g5: LineSegment StartX=-157.875 StartY=-23.8217 StartZ=0 EndX=-162.696 EndY=-38.6582 EndZ=0
    g6: LineSegment StartX=-168.592 StartY=-36.7423 StartZ=0 EndX=-162.696 EndY=-38.6582 EndZ=0
  constraints (19):
    c: Distance(g0,g-3) = 47.4
    c: Distance(g0) = 15.6
    c: Tangent(g0,g-3)
    c: Coincident(g1,g0)
    c: Coincident(g2,g0)
    c: Distance(g1) = 2.4
    c: Distance(g2) = 3.8
    c: Perpendicular(g0,g1)
    c: Perpendicular(g0,g2)
    c: Coincident(g3,g2)
    c: Coincident(g3,g1)
    c: Equal(g4,g0)
    c: Equal(g5,g0)
    c: Parallel(g4,g0)
    c: Parallel(g5,g0)
    c: Coincident(g4,g2)
    c: Coincident(g5,g1)
    c: Coincident(g6,g4)
    c: Coincident(g6,g5)
FEATURE [Part::Extrusion] Extrude077  label="Extrude077 - scavo_nuovo_driver"
  Base = -> Sketch137
  Dir = (0,-1,2e-16)
  DirMode = 2
  FaceMakerClass = Part::FaceMakerBullseye
  FaceMakerMode = 3
  LengthFwd = 20.8
  LengthRev = 0
  Solid = true
  Symmetric = true
FEATURE [Sketcher::SketchObject] Sketch138  label="scavo_nuovo_driver_alto"
  ArcFitTolerance = 1e-06
  AttachmentSupport = -> [XZ_Plane]
  ExternalGeometry = -> [Sketch]
  FullyConstrained = true
  MakeInternals = false
  MapMode = 5
  Placement = pos=(0,0,0) rot=(1,0,0;1.5708rad)
  sketch-geometry (7):
    g0: LineSegment [constr] StartX=-188.796 StartY=17.7274 StartZ=0 EndX=-187.75 EndY=4.97025 EndZ=0
    g1: LineSegment StartX=-187.75 StartY=4.97025 StartZ=0 EndX=-189.743 EndY=4.8067 EndZ=0
    g2: LineSegment StartX=-187.75 StartY=4.97025 StartZ=0 EndX=-182.766 EndY=5.37913 EndZ=0
    g3: LineSegment StartX=-190.79 StartY=17.5638 StartZ=0 EndX=-189.743 EndY=4.8067 EndZ=0
    g4: LineSegment StartX=-183.813 StartY=18.1363 StartZ=0 EndX=-182.766 EndY=5.37913 EndZ=0
    g5: LineSegment StartX=-190.79 StartY=17.5638 StartZ=0 EndX=-188.796 EndY=17.7274 EndZ=0
    g6: LineSegment StartX=-188.796 StartY=17.7274 StartZ=0 EndX=-183.813 EndY=18.1363 EndZ=0
  constraints (20):
    c: Distance(g0) = 12.8
    c: DistanceY(g-3,g0) = 9
    c: PointOnObject(g0,g-4)
    c: PointOnObject(g0,g-4)
    c: Coincident(g1,g0)
    c: Coincident(g2,g0)
    c: Distance(g1) = 2
    c: Distance(g2) = 5
    c: Perpendicular(g0,g1)
    c: Perpendicular(g0,g2)
    c: Equal(g3,g0)
    c: Parallel(g3,g0)
    c: Coincident(g3,g1)
    c: Equal(g4,g0)
    c: Parallel(g4,g0)
    c: Coincident(g4,g2)
    c: Coincident(g5,g3)
    c: Coincident(g5,g0)
    c: Coincident(g6,g0)
    c: Coincident(g6,g4)
FEATURE [Part::Extrusion] Extrude078  label="Extrude078 - scavo_nuovo_driver_alto"
  Base = -> Sketch138
  Dir = (0,-1,2e-16)
  DirMode = 2
  FaceMakerClass = Part::FaceMakerBullseye
  FaceMakerMode = 3
  LengthFwd = 16.6
  LengthRev = 0
  Solid = true
  Symmetric = true
FEATURE [Sketcher::SketchObject] Sketch139  label="fermi_nuovo_driver_alto"
  ArcFitTolerance = 1e-06
  AttachmentSupport = -> [XZ_Plane]
  ExternalGeometry = -> [Sketch138,Sketch]
  FullyConstrained = true
  MakeInternals = false
  MapMode = 5
  Placement = pos=(0,0,0) rot=(1,0,0;1.5708rad)
  sketch-geometry (17):
    g0: LineSegment [constr] StartX=-188.314 StartY=16.4295 StartZ=0 EndX=-187.885 EndY=13.7638 EndZ=0
    g1: LineSegment [constr] StartX=-187.885 StartY=13.7638 StartZ=0 EndX=-187.456 EndY=11.0981 EndZ=0
    g2: LineSegment StartX=-187.885 StartY=13.7638 StartZ=0 EndX=-187.71 EndY=12.6778 EndZ=0
    g3: LineSegment StartX=-187.885 StartY=13.7638 StartZ=0 EndX=-188.06 EndY=14.8499 EndZ=0
    g4: LineSegment StartX=-187.71 StartY=12.6778 StartZ=0 EndX=-185.538 EndY=13.0274 EndZ=0
    g5: LineSegment StartX=-188.06 StartY=14.8499 StartZ=0 EndX=-185.888 EndY=15.1994 EndZ=0
    g6: LineSegment StartX=-185.888 StartY=15.1994 StartZ=0 EndX=-185.538 EndY=13.0274 EndZ=0
    g7: LineSegment StartX=-187.456 StartY=11.0981 StartZ=0 EndX=-189.035 EndY=10.8439 EndZ=0
    g8: LineSegment StartX=-188.314 StartY=16.4295 StartZ=0 EndX=-189.893 EndY=16.1753 EndZ=0
    g9: LineSegment StartX=-189.893 StartY=16.1753 StartZ=0 EndX=-189.035 EndY=10.8439 EndZ=0
    g10: LineSegment StartX=-187.456 StartY=11.0981 StartZ=0 EndX=-185.284 EndY=11.4477 EndZ=0
    g11: LineSegment StartX=-188.314 StartY=16.4295 StartZ=0 EndX=-186.142 EndY=16.7791 EndZ=0
    g12: LineSegment StartX=-184.308 StartY=15.4537 StartZ=0 EndX=-183.958 EndY=13.2816 EndZ=0
    g13: ArcOfCircle CenterX=-185.888 CenterY=15.1994 CenterZ=0 NormalX=0 NormalY=0 NormalZ=1 AngleXU=0 Radius=1.6 StartAngle=0.15957 EndAngle=1.73037
    g14: GeomPoint [constr] X=-184.562 Y=17.0333 Z=0
    g15: ArcOfCircle CenterX=-185.538 CenterY=13.0274 CenterZ=0 NormalX=0 NormalY=0 NormalZ=1 AngleXU=0 Radius=1.6 StartAngle=4.87196 EndAngle=6.44276
    g16: GeomPoint [constr] X=-183.704 Y=11.7019 Z=0
  constraints (43):
    c: Tangent(g1,g0) = -1.5708
    c: Distance(g0) = 2.7
    c: Equal(g1,g0)
    c: Tangent(g1,g-5)
    c: Coincident(g2,g0)
    c: Coincident(g3,g0)
    c: Distance(g2) = 1.1
    c: Equal(g3,g2)
    c: PointOnObject(g3,g2)
    c: Coincident(g4,g2)
    c: Coincident(g5,g3)
    c: Distance(g4) = 2.2
    c: Equal(g4,g5)
    c: Perpendicular(g1,g4)
    c: Perpendicular(g0,g5)
    c: Coincident(g6,g5)
    c: Coincident(g6,g4)
    c: Coincident(g7,g1)
    c: Coincident(g8,g0)
    c: Distance(g7) = 1.6
    c: Equal(g7,g8)
    c: Perpendicular(g1,g7)
    c: Perpendicular(g8,g0)
    c: Coincident(g9,g8)
    c: Coincident(g9,g7)
    c: Coincident(g10,g1)
    c: Coincident(g11,g0)
    c: Distance(g10,g16) = 3.8
    c: Perpendicular(g1,g10)
    c: Perpendicular(g1,g11)
    c: DistanceY(g0,g-4) = 3.8
    c: PointOnObject(g14,g12)
    c: PointOnObject(g14,g11)
    c: Tangent(g12,g13) = 1.5708
    c: Tangent(g11,g13) = 1.5708
    c: PointOnObject(g16,g12)
    c: PointOnObject(g16,g10)
    c: Tangent(g12,g15) = 1.5708
    c: Tangent(g10,g15) = -1.5708
    c: Equal(g13,g15)
    c: Coincident(g13,g5)
    c: Parallel(g2,g0)
    c: PointOnObject(g0,g-5)
FEATURE [Part::Extrusion] Extrude079  label="Extrude079 - fermi_nuovo_driver_alto"
  Base = -> Sketch139
  Dir = (0,-1,2e-16)
  DirMode = 2
  FaceMakerClass = Part::FaceMakerBullseye
  FaceMakerMode = 3
  LengthFwd = 25.2
  LengthRev = 0
  Solid = true
  Symmetric = true
FEATURE [Sketcher::SketchObject] Sketch140  label="scavo_diodo_nuovo_driver_alto"
  ArcFitTolerance = 1e-06
  AttachmentSupport = -> [XZ_Plane]
  ExternalGeometry = -> [Sketch138]
  FullyConstrained = true
  MakeInternals = false
  MapMode = 5
  Placement = pos=(0,0,0) rot=(1,0,0;1.5708rad)
  sketch-geometry (4):
    g0: LineSegment StartX=-190.79 StartY=17.5638 StartZ=0 EndX=-189.743 EndY=4.8067 EndZ=0
    g1: LineSegment StartX=-193.78 StartY=17.3185 StartZ=0 EndX=-192.733 EndY=4.56137 EndZ=0
    g2: LineSegment StartX=-190.79 StartY=17.5638 StartZ=0 EndX=-193.78 EndY=17.3185 EndZ=0
    g3: LineSegment StartX=-192.733 StartY=4.56137 StartZ=0 EndX=-189.743 EndY=4.8067 EndZ=0
  constraints (11):
    c: Equal(g0,g-3)
    c: Parallel(g0,g-3)
    c: Equal(g1,g-3)
    c: Parallel(g1,g-3)
    c: Coincident(g2,g0)
    c: Distance(g2) = 3
    c: Perpendicular(g0,g2)
    c: Coincident(g1,g2)
    c: Coincident(g3,g1)
    c: Coincident(g3,g0)
    c: Coincident(g0,g-3)
FEATURE [Part::Extrusion] Extrude080  label="Extrude080 - scavo_diodo_nuovo_driver_alto"
  Base = -> Sketch140
  Dir = (0,-1,2e-16)
  DirMode = 2
  FaceMakerClass = Part::FaceMakerBullseye
  FaceMakerMode = 3
  LengthFwd = 4
  LengthRev = 0
  Placement = pos=(0,7.8,0) rot=(0,0,1;0rad)
  Solid = true
  Symmetric = false
FEATURE [Part::MultiFuse] Fusion001
  Refine = true
  Shapes = -> [Cut043,Extrude079]
FEATURE [Part::Cut] Cut044
  Base = -> Fusion001
  Refine = true
  Tool = -> Extrude078
FEATURE [Part::Cut] Cut045
  Base = -> Cut044
  Refine = true
  Tool = -> Extrude080
FEATURE [Sketcher::SketchObject] Sketch141  label="fermi_nuovo_driver"
  ArcFitTolerance = 1e-06
  AttachmentSupport = -> [XZ_Plane]
  ExternalGeometry = -> [Sketch,Sketch137]
  FullyConstrained = true
  MakeInternals = false
  MapMode = 5
  Placement = pos=(0,0,0) rot=(1,0,0;1.5708rad)
  sketch-geometry (16):
    g0: LineSegment [constr] StartX=-157.875 StartY=-23.8217 StartZ=0 EndX=-160.157 EndY=-23.0801 EndZ=0
    g1: LineSegment [constr] StartX=-160.157 StartY=-23.0801 StartZ=0 EndX=-160.405 EndY=-23.8409 EndZ=0
    g2: LineSegment [constr] StartX=-160.405 StartY=-23.8409 StartZ=0 EndX=-162.073 EndY=-28.9766 EndZ=0
    g3: LineSegment StartX=-162.073 StartY=-28.9766 StartZ=0 EndX=-164.166 EndY=-28.2968 EndZ=0
    g4: LineSegment StartX=-165.193 StartY=-26.2807 StartZ=0 EndX=-164.513 EndY=-24.1883 EndZ=0
    g5: LineSegment StartX=-162.497 StartY=-23.1611 StartZ=0 EndX=-158.883 EndY=-24.3354 EndZ=0
    g6: LineSegment StartX=-158.883 StartY=-24.3354 StartZ=0 EndX=-160.552 EndY=-29.4711 EndZ=0
    g7: LineSegment StartX=-162.073 StartY=-28.9766 StartZ=0 EndX=-160.552 EndY=-29.4711 EndZ=0
    g8: LineSegment StartX=-162.991 StartY=-24.6828 StartZ=0 EndX=-163.671 EndY=-26.7751 EndZ=0
    g9: LineSegment StartX=-163.671 StartY=-26.7751 StartZ=0 EndX=-161.579 EndY=-27.4549 EndZ=0
    g10: LineSegment StartX=-161.579 StartY=-27.4549 StartZ=0 EndX=-160.899 EndY=-25.3626 EndZ=0
    g11: LineSegment StartX=-160.899 StartY=-25.3626 StartZ=0 EndX=-162.991 EndY=-24.6828 EndZ=0
    g12: ArcOfCircle CenterX=-162.991 CenterY=-24.6828 CenterZ=0 NormalX=0 NormalY=0 NormalZ=1 AngleXU=0 Radius=1.6 StartAngle=1.25664 EndAngle=2.82743
    g13: GeomPoint [constr] X=-164.019 Y=-22.6667 Z=0
    g14: ArcOfCircle CenterX=-163.671 CenterY=-26.7751 CenterZ=0 NormalX=0 NormalY=0 NormalZ=1 AngleXU=0 Radius=1.6 StartAngle=2.82743 EndAngle=4.39823
    g15: GeomPoint [constr] X=-165.687 Y=-27.8024 Z=0
  constraints (41):
    c: Coincident(g0,g-4)
    c: PointOnObject(g0,g-3)
    c: Parallel(g0,g-4)
    c: Coincident(g1,g0)
    c: Parallel(g1,g-3)
    c: Distance(g1) = 0.8
    c: Coincident(g2,g1)
    c: Distance(g2) = 5.4
    c: Coincident(g3,g2)
    c: Parallel(g2,g-3)
    c: Distance(g15,g13) = 5.4
    c: Perpendicular(g3,g2)
    c: Parallel(g4,g2)
    c: Distance(g5,g13) = 5.4
    c: Distance(g3,g15) = 3.8
    c: Perpendicular(g4,g5)
    c: Coincident(g6,g5)
    c: Distance(g6) = 5.4
    c: Parallel(g6,g4)
    c: Coincident(g7,g2)
    c: Coincident(g7,g6)
    c: Coincident(g8,g9)
    c: Coincident(g9,g10)
    c: Coincident(g10,g11)
    c: Coincident(g11,g8)
    c: Distance(g8,g10) = 2.2
    c: Distance(g9,g11) = 2.2
    c: Perpendicular(g11,g8)
    c: Equal(g8,g10)
    c: Equal(g11,g9)
    c: Tangent(g10,g2)
    c: Distance(g10,g1) = 1.6
    c: PointOnObject(g13,g4)
    c: PointOnObject(g13,g5)
    c: Tangent(g4,g12) = 1.5708
    c: Tangent(g5,g12) = 1.5708
    c: PointOnObject(g15,g4)
    c: Tangent(g4,g14) = 1.5708
    c: Tangent(g3,g14) = 1.5708
    c: Equal(g14,g12)
    c: Coincident(g12,g8)
FEATURE [Part::Extrusion] Extrude081  label="Extrude081 - fermi_nuovo_driver"
  Base = -> Sketch141
  Dir = (0,-1,2e-16)
  DirMode = 2
  FaceMakerClass = Part::FaceMakerBullseye
  FaceMakerMode = 3
  LengthFwd = 25.2
  LengthRev = 0
  Solid = true
  Symmetric = true
FEATURE [Part::MultiFuse] Fusion002
  Refine = true
  Shapes = -> [Cut045,Extrude081]
FEATURE [Part::Cut] Cut046
  Base = -> Fusion002
  Refine = true
  Tool = -> Extrude077
FEATURE [Sketcher::SketchObject] Sketch142  label="fermi_rele"
  ArcFitTolerance = 1e-06
  AttachmentSupport = -> [XZ_Plane]
  ExternalGeometry = -> [Sketch,Sketch136]
  FullyConstrained = true
  MakeInternals = false
  MapMode = 5
  Placement = pos=(0,0,0) rot=(1,0,0;1.5708rad)
  sketch-geometry (15):
    g0: LineSegment StartX=-177.245 StartY=-63.3719 StartZ=0 EndX=-177.924 EndY=-65.4642 EndZ=0
    g1: LineSegment StartX=-175.228 StartY=-62.3446 StartZ=0 EndX=-171.614 EndY=-63.5189 EndZ=0
    g2: LineSegment StartX=-171.614 StartY=-63.5189 StartZ=0 EndX=-173.283 EndY=-68.6546 EndZ=0
    g3: LineSegment StartX=-176.897 StartY=-67.4803 StartZ=0 EndX=-173.283 EndY=-68.6546 EndZ=0
    g4: LineSegment StartX=-175.723 StartY=-63.8663 StartZ=0 EndX=-173.631 EndY=-64.5461 EndZ=0
    g5: LineSegment StartX=-175.723 StartY=-63.8663 StartZ=0 EndX=-176.403 EndY=-65.9586 EndZ=0
    g6: LineSegment StartX=-173.631 StartY=-64.5461 StartZ=0 EndX=-174.31 EndY=-66.6385 EndZ=0
    g7: LineSegment StartX=-176.403 StartY=-65.9586 StartZ=0 EndX=-174.31 EndY=-66.6385 EndZ=0
    g8: LineSegment [constr] StartX=-173.631 StartY=-64.5461 StartZ=0 EndX=-173.136 EndY=-63.0245 EndZ=0
    g9: LineSegment [constr] StartX=-173.631 StartY=-64.5461 StartZ=0 EndX=-172.109 EndY=-65.0406 EndZ=0
    g10: LineSegment [constr] StartX=-170.35 StartY=-63.5093 StartZ=0 EndX=-173.013 EndY=-62.644 EndZ=0
    g11: ArcOfCircle CenterX=-175.723 CenterY=-63.8663 CenterZ=0 NormalX=0 NormalY=0 NormalZ=1 AngleXU=0 Radius=1.6 StartAngle=1.25664 EndAngle=2.82743
    g12: GeomPoint [constr] X=-176.75 Y=-61.8502 Z=0
    g13: ArcOfCircle CenterX=-176.403 CenterY=-65.9586 CenterZ=0 NormalX=0 NormalY=0 NormalZ=1 AngleXU=0 Radius=1.6 StartAngle=2.82743 EndAngle=4.39823
    g14: GeomPoint [constr] X=-178.419 Y=-66.9859 Z=0
  constraints (39):
    c: Distance(g14,g12) = 5.4
    c: Distance(g1,g12) = 5.4
    c: Perpendicular(g1,g0)
    c: Coincident(g2,g1)
    c: Parallel(g2,g0)
    c: Coincident(g3,g2)
    c: Parallel(g2,g-3)
    c: Coincident(g5,g4)
    c: Distance(g5) = 2.2
    c: Distance(g4) = 2.2
    c: Perpendicular(g4,g5)
    c: Coincident(g6,g4)
    c: Equal(g6,g5)
    c: Parallel(g6,g5)
    c: Coincident(g7,g5)
    c: Coincident(g7,g6)
    c: Coincident(g8,g4)
    c: Coincident(g9,g4)
    c: Distance(g8) = 1.6
    c: Distance(g9) = 1.6
    c: Parallel(g8,g6)
    c: Parallel(g9,g4)
    c: PointOnObject(g8,g1)
    c: PointOnObject(g9,g2)
    c: Coincident(g10,g-4)
    c: Parallel(g10,g-4)
    c: PointOnObject(g10,g-3)
    c: Tangent(g6,g-3) = 1.5708
    c: Distance(g4,g10) = 2
    c: PointOnObject(g12,g1)
    c: Tangent(g1,g11) = 1.5708
    c: Tangent(g0,g11) = -1.5708
    c: PointOnObject(g14,g3)
    c: PointOnObject(g14,g0)
    c: Tangent(g3,g13) = -1.5708
    c: Tangent(g0,g13) = -1.5708
    c: Equal(g11,g13)
    c: Coincident(g11,g4)
    c: Parallel(g3,g1)
FEATURE [Part::Extrusion] Extrude082  label="Extrude082 - fermi_rele"
  Base = -> Sketch142
  Dir = (0,-1,2e-16)
  DirMode = 2
  FaceMakerClass = Part::FaceMakerBullseye
  FaceMakerMode = 3
  LengthFwd = 25.2
  LengthRev = 0
  Solid = true
  Symmetric = true
FEATURE [Part::MultiFuse] Fusion003
  Refine = true
  Shapes = -> [Cut046,Extrude082]
FEATURE [Part::Cut] Cut047
  Base = -> Fusion003
  Refine = true
  Tool = -> Extrude076
FEATURE [Sketcher::SketchObject] Sketch143  label="foro_passaggio_cavi_led_batteria"
  ArcFitTolerance = 1e-06
  AttachmentSupport = -> [XZ_Plane]
  ExternalGeometry = -> [Sketch,Sketch042,Sketch036]
  FullyConstrained = true
  MakeInternals = false
  MapMode = 5
  Placement = pos=(0,0,0) rot=(1,0,0;1.5708rad)
  sketch-geometry (4):
    g0: LineSegment StartX=-207.775 StartY=-41.3701 StartZ=0 EndX=-213.607 EndY=-53.8767 EndZ=0
    g1: LineSegment StartX=-213.607 StartY=-53.8767 StartZ=0 EndX=-211.843 EndY=-59.5559 EndZ=0
    g2: LineSegment StartX=-207.775 StartY=-41.3701 StartZ=0 EndX=-207.775 EndY=-50.8316 EndZ=0
    g3: LineSegment StartX=-207.775 StartY=-50.8316 StartZ=0 EndX=-211.843 EndY=-59.5559 EndZ=0
  constraints (9):
    c: Coincident(g0,g-3)
    c: PointOnObject(g1,g-6)
    c: Coincident(g1,g0)
    c: Coincident(g2,g0)
    c: Coincident(g2,g-7)
    c: Coincident(g3,g2)
    c: Parallel(g3,g0)
    c: Coincident(g3,g1)
    c: Coincident(g0,g-5)
FEATURE [Part::Extrusion] Extrude083  label="Extrude083 - foro_passaggio_cavi_led_batteria"
  Base = -> Sketch143
  Dir = (0,-1,2e-16)
  DirMode = 2
  FaceMakerClass = Part::FaceMakerBullseye
  FaceMakerMode = 3
  LengthFwd = 6
  LengthRev = 0
  Solid = true
  Symmetric = true
FEATURE [Part::Cut] Cut048
  Base = -> Cut047
  Refine = true
  Tool = -> Extrude083
FEATURE [Sketcher::SketchObject] Sketch144  label="foro_areazione_alimentatore"
  ArcFitTolerance = 1e-06
  AttachmentSupport = -> [XZ_Plane]
  ExternalGeometry = -> [Sketch036]
  FullyConstrained = true
  MakeInternals = false
  MapMode = 5
  Placement = pos=(0,0,0) rot=(1,0,0;1.5708rad)
  sketch-geometry (4):
    g0: LineSegment StartX=-211.843 StartY=-60.3701 StartZ=0 EndX=-207.775 EndY=-60.3701 EndZ=0
    g1: LineSegment StartX=-207.775 StartY=-60.3701 StartZ=0 EndX=-207.775 EndY=-70.3701 EndZ=0
    g2: LineSegment StartX=-211.843 StartY=-60.3701 StartZ=0 EndX=-211.843 EndY=-70.3701 EndZ=0
    g3: LineSegment StartX=-207.775 StartY=-70.3701 StartZ=0 EndX=-211.843 EndY=-70.3701 EndZ=0
  constraints (11):
    c: Horizontal(g0)
    c: Distance(g1) = 10
    c: Coincident(g1,g0)
    c: Tangent(g1,g-3)
    c: PointOnObject(g0,g-4)
    c: Coincident(g2,g0)
    c: PointOnObject(g2,g-4)
    c: Coincident(g3,g1)
    c: Horizontal(g3)
    c: Coincident(g3,g2)
    c: DistanceY(g0,g-3) = 19
FEATURE [Part::Extrusion] Extrude084  label="Extrude084 - foro_areazione_alimentatore"
  Base = -> Sketch144
  Dir = (0,-1,2e-16)
  DirMode = 2
  FaceMakerClass = Part::FaceMakerBullseye
  FaceMakerMode = 3
  LengthFwd = 10
  LengthRev = 0
  Solid = true
  Symmetric = true
FEATURE [Part::Cut] Cut049
  Base = -> Cut048
  Refine = true
  Tool = -> Extrude084
FEATURE [Sketcher::SketchObject] Sketch145  label="foro_per_condesatore"
  ArcFitTolerance = 1e-06
  AttachmentSupport = -> [XZ_Plane]
  ExternalGeometry = -> [Sketch,Sketch139]
  FullyConstrained = true
  MakeInternals = false
  MapMode = 5
  Placement = pos=(0,0,0) rot=(1,0,0;1.5708rad)
  sketch-geometry (1):
    g0: Circle CenterX=-182.345 CenterY=7.02342 CenterZ=0 NormalX=0 NormalY=0 NormalZ=1 AngleXU=0 Radius=5.2
  constraints (3):
    c: Diameter(g0) = 10.4
    c: Tangent(g0,g-3)
    c: Tangent(g0,g-4)
FEATURE [Part::Extrusion] Extrude085  label="Extrude085 - foro_per_condesatore"
  Base = -> Sketch145
  Dir = (0,-1,2e-16)
  DirMode = 2
  FaceMakerClass = Part::FaceMakerBullseye
  FaceMakerMode = 3
  LengthFwd = 25.2
  LengthRev = 0
  Solid = true
  Symmetric = true
FEATURE [Part::Cut] Cut050
  Base = -> Cut049
  Refine = true
  Tool = -> Extrude085
FEATURE [Sketcher::SketchObject] Sketch146  label="scavo_pulsante_6x6_per_led_batteria"
  ArcFitTolerance = 1e-06
  AttachmentSupport = -> [XZ_Plane]
  ExternalGeometry = -> [Sketch016]
  FullyConstrained = true
  MakeInternals = false
  MapMode = 5
  Placement = pos=(0,0,0) rot=(1,0,0;1.5708rad)
  sketch-geometry (5):
    g0: LineSegment StartX=-216.643 StartY=-65.8316 StartZ=0 EndX=-216.643 EndY=-72.8316 EndZ=0
    g1: LineSegment StartX=-216.643 StartY=-72.8316 StartZ=0 EndX=-210.243 EndY=-72.8316 EndZ=0
    g2: LineSegment StartX=-210.243 StartY=-72.8316 StartZ=0 EndX=-210.243 EndY=-65.8316 EndZ=0
    g3: LineSegment StartX=-210.243 StartY=-65.8316 StartZ=0 EndX=-216.643 EndY=-65.8316 EndZ=0
    g4: GeomPoint [constr] X=-213.443 Y=-69.3316 Z=0
  constraints (13):
    c: Coincident(g0,g1)
    c: Coincident(g1,g2)
    c: Coincident(g2,g3)
    c: Coincident(g3,g0)
    c: Vertical(g0)
    c: Vertical(g2)
    c: Horizontal(g1)
    c: Horizontal(g3)
    c: Distance(g0,g2) = 6.4
    c: Distance(g1,g3) = 7
    c: Tangent(g1,g-3)
    c: Symmetric(g0,g2,g4)
    c: Vertical(g-3,g4)
FEATURE [Part::Extrusion] Extrude086  label="Extrude086 - scavo_pulsante_6x6_per_led_batteria"
  Base = -> Sketch146
  Dir = (0,-1,2e-16)
  DirMode = 2
  FaceMakerClass = Part::FaceMakerBullseye
  FaceMakerMode = 3
  LengthFwd = 4
  LengthRev = 0
  Placement = pos=(0,12.6,0) rot=(0,0,1;0rad)
  Solid = true
  Symmetric = false
FEATURE [Sketcher::SketchObject] Sketch147  label="scavo_led_stato_batteria"
  ArcFitTolerance = 1e-06
  AttachmentSupport = -> [XZ_Plane]
  ExternalGeometry = -> [Sketch016]
  FullyConstrained = true
  MakeInternals = false
  MapMode = 5
  Placement = pos=(0,0,0) rot=(1,0,0;1.5708rad)
  sketch-geometry (5):
    g0: LineSegment StartX=-215.843 StartY=-56.2316 StartZ=0 EndX=-215.843 EndY=-65.4316 EndZ=0
    g1: LineSegment StartX=-215.843 StartY=-65.4316 StartZ=0 EndX=-211.043 EndY=-65.4316 EndZ=0
    g2: LineSegment StartX=-211.043 StartY=-65.4316 StartZ=0 EndX=-211.043 EndY=-56.2316 EndZ=0
    g3: LineSegment StartX=-211.043 StartY=-56.2316 StartZ=0 EndX=-215.843 EndY=-56.2316 EndZ=0
    g4: GeomPoint [constr] X=-213.443 Y=-60.8316 Z=0
  constraints (13):
    c: Coincident(g0,g1)
    c: Coincident(g1,g2)
    c: Coincident(g2,g3)
    c: Coincident(g3,g0)
    c: Distance(g0,g2) = 4.8
    c: Distance(g1,g3) = 9.2
    c: Equal(g0,g2)
    c: Equal(g1,g3)
    c: Perpendicular(g3,g0)
    c: DistanceY(g-3,g0) = 11.4
    c: Vertical(g2)
    c: Symmetric(g0,g2,g4)
    c: Vertical(g4,g-3)
FEATURE [Part::Extrusion] Extrude087  label="Extrude087 - scavo_led_stato_batteria"
  Base = -> Sketch147
  Dir = (0,-1,2e-16)
  DirMode = 2
  FaceMakerClass = Part::FaceMakerBullseye
  FaceMakerMode = 3
  LengthFwd = 2.2
  LengthRev = 0
  Placement = pos=(0,12.6,0) rot=(0,0,1;0rad)
  Solid = true
  Symmetric = false
FEATURE [Sketcher::SketchObject] Sketch148
  ArcFitTolerance = 1e-06
  AttachmentSupport = -> [Pad016]
  ExternalGeometry = -> [Pad016]
  FullyConstrained = true
  MakeInternals = false
  MapMode = 5
  Placement = pos=(0,0,-80.4316) rot=(1,0,0;3.14159rad)
  sketch-geometry (8):
    g0: LineSegment StartX=-176.685 StartY=3.6 StartZ=0 EndX=-186.685 EndY=3.6 EndZ=0
    g1: LineSegment StartX=-176.685 StartY=3.6 StartZ=0 EndX=-176.685 EndY=-9e-16 EndZ=0
    g2: LineSegment [constr] StartX=-186.685 StartY=3.6 StartZ=0 EndX=-186.685 EndY=-9e-16 EndZ=0
    g3: ArcOfEllipse CenterX=-186.685 CenterY=-9e-16 CenterZ=0 NormalX=0 NormalY=0 NormalZ=1 MajorRadius=10 MinorRadius=3.6 AngleXU=0 StartAngle=0 EndAngle=1.5708
    g4: LineSegment [constr] StartX=-176.685 StartY=-1e-15 StartZ=0 EndX=-196.685 EndY=-1e-15 EndZ=0
    g5: LineSegment [constr] StartX=-186.685 StartY=3.6 StartZ=0 EndX=-186.685 EndY=-3.6 EndZ=0
    g6: GeomPoint [constr] X=-177.356 Y=-1e-15 Z=0
    g7: GeomPoint [constr] X=-196.015 Y=-1e-15 Z=0
  constraints (13):
    c: Distance(g0) = 10
    c: Coincident(g0,g-5)
    c: PointOnObject(g0,g-3)
    c: Coincident(g1,g0)
    c: Coincident(g1,g-5)
    c: Coincident(g2,g0)
    c: Vertical(g2)
    c: PointOnObject(g2,g-4)
    c: InternalAlignment(g4-g7 -> g3) x4
    c: Coincident(g3,g2)
    c: Coincident(g3,g0)
    c: Coincident(g3,g1)
    c: Horizontal(g4)
FEATURE [PartDesign::SubtractivePipe] SubtractivePipe004
  AuxilleryCurvelinear = true
  AuxillerySpineTangent = false
  BaseFeature = -> Pad016
  Binormal = (0,0,0)
  Mode = 0
  Profile = -> Sketch148
  Refine = true
  Spine = -> Pad016 [Edge253]
  SpineTangent = false
  Suppressed = false
  Transformation = 0
  Transition = 0
FEATURE [Sketcher::SketchObject] Sketch149
  ArcFitTolerance = 1e-06
  AttachmentSupport = -> [Pad016]
  ExternalGeometry = -> [Pad016]
  FullyConstrained = true
  MakeInternals = false
  MapMode = 5
  Placement = pos=(0,0,-80.4316) rot=(1,0,0;3.14159rad)
  sketch-geometry (8):
    g0: LineSegment StartX=-215.932 StartY=3.6 StartZ=0 EndX=-205.932 EndY=3.6 EndZ=0
    g1: LineSegment StartX=-215.932 StartY=3.6 StartZ=0 EndX=-215.932 EndY=-4e-16 EndZ=0
    g2: LineSegment [constr] StartX=-205.932 StartY=3.6 StartZ=0 EndX=-205.932 EndY=-9e-16 EndZ=0
    g3: ArcOfEllipse CenterX=-205.932 CenterY=-1e-15 CenterZ=0 NormalX=0 NormalY=0 NormalZ=1 MajorRadius=10 MinorRadius=3.6 AngleXU=-3.14159 StartAngle=4.71239 EndAngle=6.28319
    g4: LineSegment [constr] StartX=-215.932 StartY=-1e-15 StartZ=0 EndX=-195.932 EndY=-1e-15 EndZ=0
    g5: LineSegment [constr] StartX=-205.932 StartY=-3.6 StartZ=0 EndX=-205.932 EndY=3.6 EndZ=0
    g6: GeomPoint [constr] X=-215.262 Y=-2.1e-15 Z=0
    g7: GeomPoint [constr] X=-196.602 Y=-9e-16 Z=0
  constraints (13):
    c: Distance(g0) = 10
    c: Coincident(g0,g-5)
    c: PointOnObject(g0,g-5)
    c: Coincident(g1,g0)
    c: Coincident(g1,g-4)
    c: Coincident(g2,g0)
    c: Vertical(g2)
    c: PointOnObject(g2,g-3)
    c: InternalAlignment(g4-g7 -> g3) x4
    c: Coincident(g3,g2)
    c: Coincident(g3,g0)
    c: Coincident(g3,g1)
    c: Horizontal(g4)
FEATURE [PartDesign::SubtractivePipe] SubtractivePipe005
  AuxilleryCurvelinear = true
  AuxillerySpineTangent = false
  BaseFeature = -> SubtractivePipe004
  Binormal = (0,0,0)
  Mode = 0
  Profile = -> Sketch149
  Refine = true
  Spine = -> Pad016 [Edge251,Edge256,Edge255]
  SpineTangent = false
  Suppressed = false
  Transformation = 0
  Transition = 0
FEATURE [PartDesign::SubtractiveLoft] SubtractiveLoft002
  BaseFeature = -> SubtractivePipe005
  Closed = false
  Profile = -> Sketch129
  Refine = true
  Ruled = false
  Sections = -> [Sketch130]
  Suppressed = false
FEATURE [PartDesign::SubtractiveLoft] SubtractiveLoft003
  BaseFeature = -> SubtractiveLoft002
  Closed = false
  Profile = -> Clone2D001
  Refine = true
  Ruled = false
  Sections = -> [Sketch131]
  Suppressed = false
FEATURE [PartDesign::Chamfer] Chamfer010
  Angle = 45
  Base = -> SubtractiveLoft003 [Edge203,Edge204,Edge202,Edge201,Edge195]
  BaseFeature = -> SubtractiveLoft003
  ChamferType = 0
  FlipDirection = false
  Refine = true
  Size = 1.5
  Size2 = 1
  SupportTransform = false
  Suppressed = false
  UseAllEdges = false
FEATURE [PartDesign::Chamfer] Chamfer011
  Angle = 45
  Base = -> Chamfer010 [Edge15]
  BaseFeature = -> Chamfer010
  ChamferType = 0
  FlipDirection = false
  Refine = true
  Size = 1.6
  Size2 = 1
  SupportTransform = false
  Suppressed = false
  UseAllEdges = false
FEATURE [PartDesign::Chamfer] Chamfer012
  Angle = 45
  Base = -> Chamfer011 [Edge10]
  BaseFeature = -> Chamfer011
  ChamferType = 0
  FlipDirection = false
  Refine = true
  Size = 3.5
  Size2 = 1
  SupportTransform = false
  Suppressed = false
  UseAllEdges = false
FEATURE [PartDesign::Chamfer] Chamfer013
  Angle = 45
  Base = -> Chamfer012 [Edge94]
  BaseFeature = -> Chamfer012
  ChamferType = 0
  FlipDirection = false
  Refine = true
  Size = 1.9
  Size2 = 1
  SupportTransform = false
  Suppressed = false
  UseAllEdges = false
FEATURE [PartDesign::Fillet] Fillet007
  Base = -> Chamfer013 [Edge83]
  BaseFeature = -> Chamfer013
  Radius = 1.1
  Refine = true
  SupportTransform = false
  Suppressed = false
  UseAllEdges = false
FEATURE [PartDesign::Fillet] Fillet008
  Base = -> Fillet007 [Edge75]
  BaseFeature = -> Fillet007
  Radius = 1.9
  Refine = true
  SupportTransform = false
  Suppressed = false
  UseAllEdges = false
FEATURE [PartDesign::Pocket] Pocket011
  BaseFeature = -> Fillet008
  Direction = (0,1,-2e-16)
  Length = 0.8
  Length2 = 5
  Profile = -> Sketch132
  ReferenceAxis = -> Sketch132 [N_Axis]
  Refine = true
  Suppressed = false
  Type = 0
FEATURE [PartDesign::Pocket] Pocket012
  BaseFeature = -> Pocket011
  Direction = (0,1,0)
  Length = 1
  Length2 = 5
  Profile = -> ShapeString
  ReferenceAxis = -> ShapeString [N_Axis]
  Refine = true
  Suppressed = false
  Type = 0
FEATURE [Sketcher::SketchObject] Sketch150
  ArcFitTolerance = 1e-06
  AttachmentSupport = -> [Pad008]
  ExternalGeometry = -> [Pad008]
  FullyConstrained = true
  MakeInternals = false
  MapMode = 5
  Placement = pos=(0,3.6,0) rot=(0,0.707107,0.707107;3.14159rad)
  sketch-geometry (7):
    g0: LineSegment [constr] StartX=210.343 StartY=-66.0316 StartZ=0 EndX=210.343 EndY=-72.8316 EndZ=0
    g1: LineSegment [constr] StartX=210.343 StartY=-72.8316 StartZ=0 EndX=216.543 EndY=-72.8316 EndZ=0
    g2: LineSegment [constr] StartX=216.543 StartY=-72.8316 StartZ=0 EndX=216.543 EndY=-66.0316 EndZ=0
    g3: LineSegment [constr] StartX=216.543 StartY=-66.0316 StartZ=0 EndX=210.343 EndY=-66.0316 EndZ=0
    g4: LineSegment [constr] StartX=210.343 StartY=-72.8316 StartZ=0 EndX=216.543 EndY=-66.0316 EndZ=0
    g5: LineSegment [constr] StartX=210.343 StartY=-66.0316 StartZ=0 EndX=213.443 EndY=-69.4316 EndZ=0
    g6: Circle CenterX=213.443 CenterY=-69.4316 CenterZ=0 NormalX=0 NormalY=0 NormalZ=1 AngleXU=0 Radius=2
  constraints (18):
    c: Coincident(g0,g1)
    c: Coincident(g1,g2)
    c: Coincident(g2,g3)
    c: Coincident(g3,g0)
    c: Vertical(g0)
    c: Vertical(g2)
    c: Horizontal(g1)
    c: Horizontal(g3)
    c: Distance(g0,g2) = 6.2
    c: Distance(g1,g3) = 6.8
    c: DistanceY(g-3,g1) = 4
    c: Coincident(g4,g0)
    c: Coincident(g4,g2)
    c: Coincident(g5,g0)
    c: Symmetric(g0,g2,g5)
    c: Diameter(g6) = 4
    c: Coincident(g6,g5)
    c: Vertical(g5,g-3)
FEATURE [Sketcher::SketchObject] Sketch151
  ArcFitTolerance = 1e-06
  AttachmentSupport = -> [Pad008]
  ExternalGeometry = -> [Pad008]
  FullyConstrained = true
  MakeInternals = false
  MapMode = 5
  Placement = pos=(0,3.6,0) rot=(0,0.707107,0.707107;3.14159rad)
  sketch-geometry (10):
    g0: LineSegment [constr] StartX=211.143 StartY=-56.2316 StartZ=0 EndX=211.143 EndY=-65.4316 EndZ=0
    g1: LineSegment [constr] StartX=211.143 StartY=-65.4316 StartZ=0 EndX=215.743 EndY=-65.4316 EndZ=0
    g2: LineSegment [constr] StartX=215.743 StartY=-65.4316 StartZ=0 EndX=215.743 EndY=-56.2316 EndZ=0
    g3: LineSegment [constr] StartX=215.743 StartY=-56.2316 StartZ=0 EndX=211.143 EndY=-56.2316 EndZ=0
    g4: LineSegment StartX=212.243 StartY=-63.8316 StartZ=0 EndX=214.643 EndY=-63.8316 EndZ=0
    g5: LineSegment StartX=214.643 StartY=-63.8316 StartZ=0 EndX=214.643 EndY=-57.0316 EndZ=0
    g6: LineSegment StartX=214.643 StartY=-57.0316 StartZ=0 EndX=212.243 EndY=-57.0316 EndZ=0
    g7: LineSegment StartX=212.243 StartY=-57.0316 StartZ=0 EndX=212.243 EndY=-63.8316 EndZ=0
    g8: GeomPoint [constr] X=213.443 Y=-60.4316 Z=0
    g9: GeomPoint [constr] X=213.443 Y=-60.8316 Z=0
  constraints (26):
    c: Coincident(g0,g1)
    c: Coincident(g1,g2)
    c: Coincident(g2,g3)
    c: Coincident(g3,g0)
    c: Vertical(g0)
    c: Vertical(g2)
    c: Horizontal(g1)
    c: Horizontal(g3)
    c: Distance(g0,g2) = 4.6
    c: Distance(g1,g3) = 9.2
    c: DistanceY(g-3,g1) = 11.4
    c: Coincident(g4,g5)
    c: Coincident(g5,g6)
    c: Coincident(g6,g7)
    c: Coincident(g7,g4)
    c: Horizontal(g4)
    c: Horizontal(g6)
    c: Vertical(g5)
    c: Vertical(g7)
    c: Symmetric(g6,g4,g8)
    c: Distance(g5,g7) = 2.4
    c: Distance(g4,g6) = 6.8
    c: Symmetric(g2,g0,g9)
    c: Vertical(g8,g9)
    c: DistanceY(g1,g4) = 1.6
    c: Vertical(g9,g-3)
FEATURE [PartDesign::Pocket] Pocket019
  BaseFeature = -> Pocket013
  Direction = (0,-1,2e-16)
  Length = 3.6
  Length2 = 5
  Profile = -> Sketch151
  ReferenceAxis = -> Sketch151 [N_Axis]
  Refine = true
  Suppressed = false
  Type = 0
FEATURE [PartDesign::Pocket] Pocket018
  BaseFeature = -> Pocket019
  Direction = (0,-1,2e-16)
  Length = 3.6
  Length2 = 5
  Profile = -> Sketch150
  ReferenceAxis = -> Sketch150 [N_Axis]
  Refine = true
  Suppressed = false
  Type = 0
FEATURE [PartDesign::Point] DatumPoint
  AttacherType = Attacher::AttachEnginePoint
  AttachmentSupport = -> [Sketch150]
  MapMode = 36
  Placement = pos=(-213.443,3.6,-69.4316) rot=(0,1,0;3.14159rad)
FEATURE [PartDesign::Plane] DatumPlane002
  AttachmentSupport = -> [DatumPoint]
  Length = 260.281
  MapMode = 1
  Placement = pos=(-213.443,3.6,-69.4316) rot=(0,0,1;0rad)
  ResizeMode = 0
  Width = 71.8377
FEATURE [Sketcher::SketchObject] Sketch152
  ArcFitTolerance = 1e-06
  AttachmentSupport = -> [DatumPlane002]
  ExternalGeometry = -> [Sketch150]
  FullyConstrained = true
  MakeInternals = false
  MapMode = 5
  Placement = pos=(-213.443,3.6,-69.4316) rot=(0,0,1;0rad)
  sketch-geometry (7):
    g0: LineSegment StartX=0 StartY=0 StartZ=0 EndX=-4 EndY=3.8e-15 EndZ=0
    g1: ArcOfEllipse CenterX=0 CenterY=0 CenterZ=0 NormalX=0 NormalY=0 NormalZ=1 MajorRadius=4 MinorRadius=3.6 AngleXU=3.14159 StartAngle=2e-16 EndAngle=1.5708
    g2: LineSegment [constr] StartX=-4 StartY=9e-16 StartZ=0 EndX=4 EndY=-9e-16 EndZ=0
    g3: LineSegment [constr] StartX=0 StartY=-3.6 StartZ=0 EndX=0 EndY=3.6 EndZ=0
    g4: GeomPoint [constr] X=-1.74356 Y=2.5e-15 Z=0
    g5: GeomPoint [constr] X=1.74356 Y=-2e-15 Z=0
    g6: LineSegment StartX=0 StartY=0 StartZ=0 EndX=-5.5e-15 EndY=-3.6 EndZ=0
  constraints (11):
    c: PointOnObject(g1,g-2)
    c: Distance(g0) = 4
    c: PointOnObject(g0,g-1)
    c: InternalAlignment(g2-g5 -> g1) x4
    c: Coincident(g1,g0)
    c: Vertical(g3)
    c: Coincident(g1,g-1)
    c: Distance(g6) = 3.6
    c: Coincident(g6,g1)
    c: Coincident(g1,g6)
    c: Coincident(g0,g1)
FEATURE [PartDesign::Groove] Groove
  Angle = 360
  Angle2 = 60
  Axis = (0,1,0)
  Base = (-213.443,3.6,-69.4316)
  BaseFeature = -> Pocket018
  Profile = -> Sketch152
  ReferenceAxis = -> Sketch152 [V_Axis]
  Refine = true
  Reversed = true
  Suppressed = false
  Type = 0
FEATURE [PartDesign::Body] Body006  label="lato SX"
  AllowCompound = false
  Group = -> [Binder,Pad019,Chamfer015,Pocket002,Sketch133,Sketch091,Pad005,Sketch092,Pocket001,Sketch093,Sketch094,Pad006,Sketch095,Pad007,Sketch096,Pad008,Sketch097,Pad009,Chamfer005,Pocket004,Sketch098,Pad010,Chamfer006,Pocket003,SubtractivePipe,SubtractivePipe001,Sketch099,Sketch106,Sketch107,Sketch108,Clone2D,Sketch109,SubtractiveLoft,SubtractiveLoft001,Sketch110,Sketch111,Sketch112,Chamfer016,Chamfer017,+15 more]
  Origin = -> Origin006
  Tip = -> Groove
FEATURE [Sketcher::SketchObject] Sketch153  label="ripieno_per_sostegno_led_batteria"
  ArcFitTolerance = 1e-06
  AttachmentSupport = -> [XZ_Plane]
  ExternalGeometry = -> [Sketch036]
  FullyConstrained = true
  MakeInternals = false
  MapMode = 5
  Placement = pos=(0,0,0) rot=(1,0,0;1.5708rad)
  sketch-geometry (4):
    g0: LineSegment StartX=-217.343 StartY=-54.5944 StartZ=0 EndX=-217.343 EndY=-63.1944 EndZ=0
    g1: LineSegment StartX=-217.343 StartY=-63.1944 StartZ=0 EndX=-211.843 EndY=-63.1944 EndZ=0
    g2: LineSegment StartX=-211.843 StartY=-63.1944 StartZ=0 EndX=-211.843 EndY=-54.5944 EndZ=0
    g3: LineSegment StartX=-211.843 StartY=-54.5944 StartZ=0 EndX=-217.343 EndY=-54.5944 EndZ=0
  constraints (11):
    c: Coincident(g0,g1)
    c: Coincident(g1,g2)
    c: Coincident(g2,g3)
    c: Coincident(g3,g0)
    c: Vertical(g0)
    c: Horizontal(g1)
    c: Horizontal(g3)
    c: Tangent(g2,g-3)
    c: DistanceY(g2,g-3) = 4.5
    c: DistanceX(g3,g3) = 5.5
    c: DistanceY(g0,g0) = 8.6
FEATURE [PartDesign::Body] Body  label="Struttura pistola"
  AllowCompound = false
  Group = -> [Sketch,Sketch002,Sketch004,DatumPlane,Sketch005,DatumPlane001,CopyCut,Sketch008,Sketch009,Sketch010,Sketch011,Sketch012,Sketch013,Sketch014,Sketch015,Sketch016,Sketch017,Sketch018,Sketch019,Sketch020,Sketch022,Sketch023,Sketch024,Sketch025,Sketch026,Sketch027,Sketch029,Sketch030,Sketch031,Sketch032,Sketch033,Sketch034,Sketch035,Sketch036,Sketch037,Sketch038,Sketch039,Sketch040,Sketch041,Sketch042,+28 more]
  Origin = -> Origin
FEATURE [Part::Extrusion] Extrude088  label="Extrude088 - ripieno_per_sostegno_led_batteria"
  Base = -> Sketch153
  Dir = (0,-1,2e-16)
  DirMode = 2
  FaceMakerClass = Part::FaceMakerBullseye
  FaceMakerMode = 3
  LengthFwd = 4
  LengthRev = 0
  Placement = pos=(0,12.6,0) rot=(0,0,1;0rad)
  Solid = true
  Symmetric = false
FEATURE [Part::MultiFuse] Fusion004
  Refine = true
  Shapes = -> [Cut050,Extrude088]
FEATURE [Part::Cut] Cut051
  Base = -> Fusion004
  Refine = true
  Tool = -> Extrude087
FEATURE [Part::Cut] Cut052
  Base = -> Cut051
  Refine = true
  Tool = -> Extrude086
FEATURE [Sketcher::SketchObject] Sketch154
  ArcFitTolerance = 1e-06
  AttachmentSupport = -> [Pad016]
  ExternalGeometry = -> [Binder001]
  FullyConstrained = true
  MakeInternals = false
  MapMode = 5
  Placement = pos=(0,-3.6,0) rot=(1,0,0;1.5708rad)
  sketch-geometry (25):
    g0: LineSegment StartX=-214.643 StartY=-72.4316 StartZ=0 EndX=-212.243 EndY=-72.4316 EndZ=0
    g1: LineSegment StartX=-212.243 StartY=-72.4316 StartZ=0 EndX=-212.243 EndY=-71.2316 EndZ=0
    g2: LineSegment StartX=-212.243 StartY=-71.2316 StartZ=0 EndX=-214.643 EndY=-71.2316 EndZ=0
    g3: LineSegment StartX=-214.643 StartY=-71.2316 StartZ=0 EndX=-214.643 EndY=-72.4316 EndZ=0
    g4: GeomPoint [constr] X=-213.443 Y=-71.8316 Z=0
    g5: LineSegment StartX=-214.643 StartY=-69.6316 StartZ=0 EndX=-212.243 EndY=-69.6316 EndZ=0
    g6: LineSegment StartX=-212.243 StartY=-69.6316 StartZ=0 EndX=-212.243 EndY=-68.4316 EndZ=0
    g7: LineSegment StartX=-212.243 StartY=-68.4316 StartZ=0 EndX=-214.643 EndY=-68.4316 EndZ=0
    g8: LineSegment StartX=-214.643 StartY=-68.4316 StartZ=0 EndX=-214.643 EndY=-69.6316 EndZ=0
    g9: GeomPoint [constr] X=-213.443 Y=-69.0316 Z=0
    g10: LineSegment StartX=-214.643 StartY=-66.8316 StartZ=0 EndX=-212.243 EndY=-66.8316 EndZ=0
    g11: LineSegment StartX=-212.243 StartY=-66.8316 StartZ=0 EndX=-212.243 EndY=-65.6316 EndZ=0
    g12: LineSegment StartX=-212.243 StartY=-65.6316 StartZ=0 EndX=-214.643 EndY=-65.6316 EndZ=0
    g13: LineSegment StartX=-214.643 StartY=-65.6316 StartZ=0 EndX=-214.643 EndY=-66.8316 EndZ=0
    g14: GeomPoint [constr] X=-213.443 Y=-66.2316 Z=0
    g15: LineSegment StartX=-214.643 StartY=-64.0316 StartZ=0 EndX=-212.243 EndY=-64.0316 EndZ=0
    g16: LineSegment StartX=-212.243 StartY=-64.0316 StartZ=0 EndX=-212.243 EndY=-62.8316 EndZ=0
    g17: LineSegment StartX=-212.243 StartY=-62.8316 StartZ=0 EndX=-214.643 EndY=-62.8316 EndZ=0
    g18: LineSegment StartX=-214.643 StartY=-62.8316 StartZ=0 EndX=-214.643 EndY=-64.0316 EndZ=0
    g19: GeomPoint [constr] X=-213.443 Y=-63.4316 Z=0
    g20: LineSegment StartX=-214.643 StartY=-61.2316 StartZ=0 EndX=-212.243 EndY=-61.2316 EndZ=0
    g21: LineSegment StartX=-212.243 StartY=-61.2316 StartZ=0 EndX=-212.243 EndY=-60.0316 EndZ=0
    g22: LineSegment StartX=-212.243 StartY=-60.0316 StartZ=0 EndX=-214.643 EndY=-60.0316 EndZ=0
    g23: LineSegment StartX=-214.643 StartY=-60.0316 StartZ=0 EndX=-214.643 EndY=-61.2316 EndZ=0
    g24: GeomPoint [constr] X=-213.443 Y=-60.6316 Z=0
  constraints (65):
    c: Coincident(g0,g1)
    c: Coincident(g1,g2)
    c: Coincident(g2,g3)
    c: Coincident(g3,g0)
    c: Horizontal(g0)
    c: Horizontal(g2)
    c: Vertical(g1)
    c: Vertical(g3)
    c: Symmetric(g2,g0,g4)
    c: Distance(g1,g3) = 2.4
    c: Distance(g0,g2) = 1.2
    c: Coincident(g5,g6)
    c: Coincident(g6,g7)
    c: Coincident(g7,g8)
    c: Coincident(g8,g5)
    c: Horizontal(g5)
    c: Horizontal(g7)
    c: Vertical(g6)
    c: Vertical(g8)
    c: Symmetric(g7,g5,g9)
    c: Distance(g6,g8) = 2.4
    c: Distance(g5,g7) = 1.2
    c: Coincident(g10,g11)
    c: Coincident(g11,g12)
    c: Coincident(g12,g13)
    c: Coincident(g13,g10)
    c: Horizontal(g10)
    c: Horizontal(g12)
    c: Vertical(g11)
    c: Vertical(g13)
    c: Symmetric(g12,g10,g14)
    c: Distance(g11,g13) = 2.4
    c: Distance(g10,g12) = 1.2
    c: Coincident(g15,g16)
    c: Coincident(g16,g17)
    c: Coincident(g17,g18)
    c: Coincident(g18,g15)
    c: Horizontal(g15)
    c: Horizontal(g17)
    c: Vertical(g16)
    c: Vertical(g18)
    c: Symmetric(g17,g15,g19)
    c: Distance(g16,g18) = 2.4
    c: Distance(g15,g17) = 1.2
    c: Vertical(g4,g-3)
    c: Vertical(g9,g-3)
    c: Vertical(g14,g-3)
    c: Vertical(g19,g-3)
    c: DistanceY(g-3,g4) = 5
    c: DistanceY(g4,g9) = 2.8
    c: DistanceY(g9,g14) = 2.8
    c: DistanceY(g14,g19) = 2.8
    c: Coincident(g20,g21)
    c: Coincident(g21,g22)
    c: Coincident(g22,g23)
    c: Coincident(g23,g20)
    c: Horizontal(g20)
    c: Horizontal(g22)
    c: Vertical(g21)
    c: Vertical(g23)
    c: Symmetric(g22,g20,g24)
    c: Distance(g21,g23) = 2.4
    c: Distance(g20,g22) = 1.2
    c: DistanceY(g19,g24) = 2.8
    c: Vertical(g-3,g24)
FEATURE [PartDesign::Pocket] Pocket020
  BaseFeature = -> Pocket012
  Direction = (0,1,-2e-16)
  Length = 3.6
  Length2 = 5
  Profile = -> Sketch154
  ReferenceAxis = -> Sketch154 [N_Axis]
  Refine = true
  Suppressed = false
  Type = 0
FEATURE [PartDesign::Body] Body007  label="lato DX"
  AllowCompound = false
  Group = -> [Binder001,Sketch114,Pad011,Chamfer014,Sketch115,Pocket006,Sketch116,Pad012,Sketch117,Pocket007,Sketch118,Pad013,Sketch119,Pocket008,Pad017,Chamfer009,Pocket009,Sketch123,Sketch120,Pad014,Pad018,Chamfer008,Pocket010,Sketch121,Pad015,Sketch122,Pad016,SubtractivePipe004,SubtractivePipe005,Sketch149,Sketch148,Sketch124,Sketch125,Sketch126,Sketch129,Sketch130,Clone2D001,Sketch131,SubtractiveLoft002,+13 more]
  Origin = -> Origin007
  Tip = -> Pocket020
note: 2 file-system paths scrubbed to <path> (originals preserved in the JSON sidecar)
